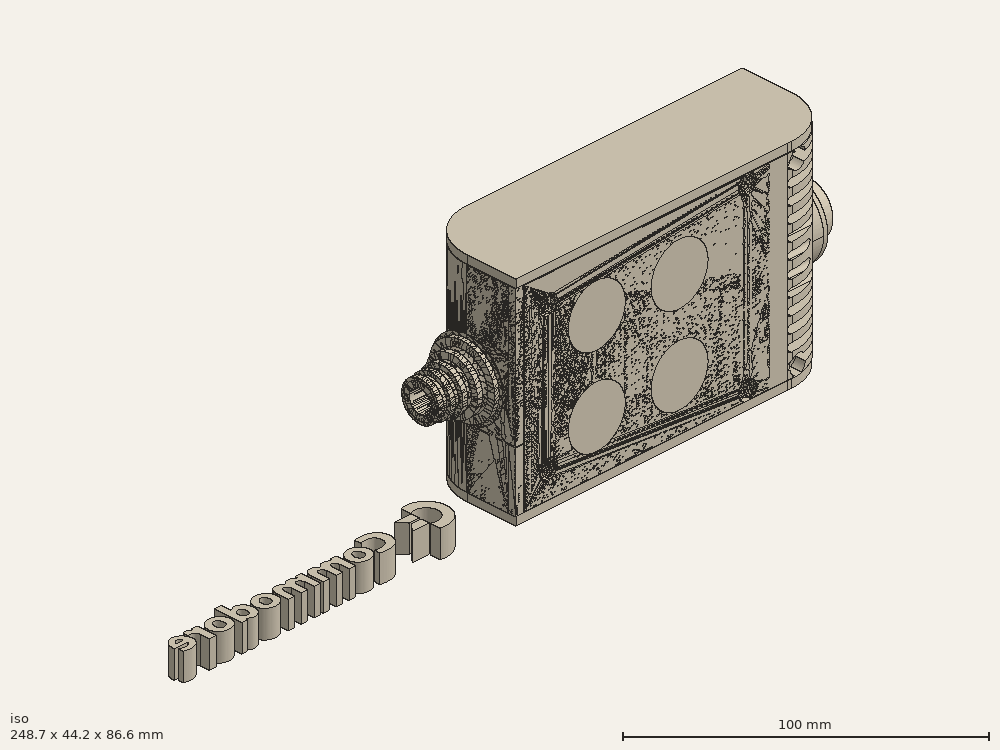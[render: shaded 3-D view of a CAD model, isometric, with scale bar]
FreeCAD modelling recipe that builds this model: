
FCSTD DOCUMENT  (FreeCAD 0.19R0.19.2)
Label: enclosure_206FCStd
License: All rights reserved
LicenseURL: http://en.wikipedia.org/wiki/All_rights_reserved
objects: Part::Revolution×152, Part::MultiFuse×146, Part::Feature×146, Sketcher::SketchObject×83, Part::Cut×70, Part::Cylinder×70, Part::Extrusion×68, Part::Fillet×58, Part::Box×36, App::MeasureDistance×4, Image::ImagePlane×1, PartDesign::Body×1, Part::FeaturePython×1, Part::Mirroring×1
note: 832 computed .brp shape members not serialized (recipe doc carries the construction recipe); baked Part::Feature solids carry a one-line shape summary decoded from their .brp

FEATURE [Sketcher::SketchObject] Sketch  label="topSketch"
  FullyConstrained = true
  sketch-geometry (20):
    g0: LineSegment StartX=5.21097e-06 StartY=3 StartZ=0 EndX=5.21097e-06 EndY=19 EndZ=0
    g1: ArcOfCircle CenterX=19 CenterY=19 CenterZ=0 NormalX=0 NormalY=0 NormalZ=1 AngleXU=0 Radius=19 StartAngle=1.5708 EndAngle=3.14159
    g2: ArcOfCircle CenterX=19 CenterY=19 CenterZ=0 NormalX=0 NormalY=0 NormalZ=1 AngleXU=0 Radius=16 StartAngle=1.5708 EndAngle=3.14159
    g3: LineSegment StartX=114 StartY=35 StartZ=0 EndX=19 EndY=35 EndZ=0
    g4: LineSegment StartX=5.21097e-06 StartY=3 StartZ=0 EndX=5.21097e-06 EndY=0 EndZ=0
    g5: LineSegment StartX=3 StartY=0 StartZ=0 EndX=5.21097e-06 EndY=0 EndZ=0
    g6: LineSegment StartX=3 StartY=19 StartZ=0 EndX=3 EndY=0 EndZ=0
    g7: LineSegment StartX=19 StartY=38 StartZ=0 EndX=124 EndY=38 EndZ=0
    g8: Circle CenterX=119 CenterY=35 CenterZ=0 NormalX=0 NormalY=0 NormalZ=1 AngleXU=0 Radius=1
    g9: Circle CenterX=121 CenterY=35 CenterZ=0 NormalX=0 NormalY=0 NormalZ=1 AngleXU=0 Radius=1
    g10: Circle CenterX=121 CenterY=33 CenterZ=0 NormalX=0 NormalY=0 NormalZ=1 AngleXU=0 Radius=1
    g11: BSplineCurve PolesCount=3 KnotsCount=2 Degree=2 IsPeriodic=0
    g12: GeomPoint X=119 Y=35 Z=0
    g13: GeomPoint X=121 Y=33 Z=0
    g14: LineSegment StartX=119 StartY=35 StartZ=0 EndX=114 EndY=35 EndZ=0
    g15: ArcOfCircle CenterX=105 CenterY=19 CenterZ=0 NormalX=0 NormalY=0 NormalZ=1 AngleXU=0 Radius=19 StartAngle=5.7297 EndAngle=6.28319
    g16: ArcOfCircle CenterX=105 CenterY=19 CenterZ=0 NormalX=0 NormalY=0 NormalZ=1 AngleXU=0 Radius=16 StartAngle=5.60905 EndAngle=6.28319
    g17: LineSegment StartX=121 StartY=33 StartZ=0 EndX=121 EndY=19 EndZ=0
    g18: LineSegment StartX=124 StartY=38 StartZ=0 EndX=124 EndY=19 EndZ=0
    g19: LineSegment StartX=117.5 StartY=9.01251 StartZ=0 EndX=121.163 EndY=9.0125 EndZ=0
  constraints (46):
    c: Vertical(g0)
    c: Block(g0)
    c: Coincident(g1,g0)
    c: Block(g1)
    c: Coincident(g2,g1)
    c: Block(g2)
    c: Coincident(g3,g2)
    c: Horizontal(g3)
    c: Tangent(g3,g2)
    c: Coincident(g4,g0)
    c: Distance(g4) = 3
    c: Vertical(g4)
    c: Coincident(g5,g4)
    c: Horizontal(g5)
    c: Coincident(g6,g2)
    c: Coincident(g6,g5)
    c: Vertical(g6)
    c: Horizontal(g7)
    c: Distance(g7) = 105
    c: Coincident(g7,g1)
    c: Block(g3)
    c: Weight(g8) = 1
    c: Equal(g8,g9)
    c: Equal(g8,g10)
    c: InternalAlignment(g8,g11)
    c: InternalAlignment(g9,g11)
    c: InternalAlignment(g10,g11)
    c: InternalAlignment(g12,g11)
    c: InternalAlignment(g13,g11)
    c: Block(g11)
    c: Coincident(g14,g11)
    c: Coincident(g14,g3)
    c: Horizontal(g14)
    c: Block(g15)
    c: Coincident(g16,g15)
    c: Block(g16)
    c: Coincident(g17,g11)
    c: Coincident(g17,g16)
    c: Vertical(g17)
    c: Distance(g17) = 14
    c: Coincident(g18,g7)
    c: Coincident(g18,g15)
    c: Vertical(g18)
    c: Distance(g18) = 19
    c: Coincident(g19,g16)
    c: Coincident(g19,g15)
FEATURE [Sketcher::SketchObject] Sketch001  label="bottomSketch"
  FullyConstrained = true
  sketch-geometry (32):
    g0: LineSegment StartX=3.3 StartY=-6.03275e-07 StartZ=0 EndX=98 EndY=-6.03275e-07 EndZ=0
    g1: ArcOfCircle CenterX=98 CenterY=19 CenterZ=0 NormalX=0 NormalY=0 NormalZ=1 AngleXU=0 Radius=19 StartAngle=4.71239 EndAngle=5.71103
    g2: LineSegment StartX=6.3 StartY=8 StartZ=0 EndX=3.3 EndY=8 EndZ=0
    g3: LineSegment StartX=3.3 StartY=8 StartZ=0 EndX=3.3 EndY=-6.03275e-07 EndZ=0
    g4: ArcOfCircle CenterX=8.3 CenterY=5 CenterZ=0 NormalX=0 NormalY=0 NormalZ=1 AngleXU=0 Radius=2 StartAngle=3.14159 EndAngle=4.71239
    g5: LineSegment StartX=6.3 StartY=8 StartZ=0 EndX=6.3 EndY=5 EndZ=0
    g6: ArcOfCircle CenterX=98 CenterY=19 CenterZ=0 NormalX=0 NormalY=0 NormalZ=1 AngleXU=0 Radius=12.7 StartAngle=4.71239 EndAngle=6.28319
    g7: LineSegment StartX=94.7 StartY=3 StartZ=0 EndX=8.3 EndY=3 EndZ=0
    g8-g12: Circle x5 (B-spline internal-alignment scaffolding for g13; pole/knot coordinates omitted)
    g13: BSplineCurve PolesCount=5 KnotsCount=3 Degree=3 IsPeriodic=0
    g14: GeomPoint X=98 Y=6.3 Z=0
    g15: GeomPoint X=96.3938 Y=4.71946 Z=0
    g16: GeomPoint X=94.7 Y=3 Z=0
    g17-g23: Circle x7 (B-spline internal-alignment scaffolding for g24; pole/knot coordinates omitted)
    g24: BSplineCurve PolesCount=7 KnotsCount=5 Degree=3 IsPeriodic=0
    g25-g29: GeomPoint x5 (B-spline internal-alignment scaffolding for g24; pole/knot coordinates omitted)
    g30: ArcOfCircle CenterX=98 CenterY=19 CenterZ=0 NormalX=0 NormalY=0 NormalZ=1 AngleXU=0 Radius=15.7 StartAngle=5.81226 EndAngle=6.28319
    g31: LineSegment StartX=110.7 StartY=19 StartZ=0 EndX=113.7 EndY=19 EndZ=0
  constraints (41):
    c: Horizontal(g0)
    c: Coincident(g1,g0)
    c: Block(g1)
    c: Horizontal(g2)
    c: Distance(g2) = 3
    c: Coincident(g3,g2)
    c: Vertical(g3)
    c: Coincident(g3,g0)
    c: Block(g4)
    c: Block(g2)
    c: Coincident(g5,g2)
    c: Coincident(g5,g4)
    c: Vertical(g5)
    c: Coincident(g6,g1)
    c: Block(g6)
    c: Coincident(g7,g4)
    c: Horizontal(g7)
    c: Block(g0)
    c: Block(g7)
    c: Block(g3)
    c: Coincident(g13,g6)
    c: Weight(g8) = 1
    c: Equal(g8, g9-g12) x4
    c: Coincident(g13,g7)
    c: InternalAlignment(g8-g12 -> g13) x5
    c: InternalAlignment(g14,g13)
    c: InternalAlignment(g15,g13)
    c: InternalAlignment(g16,g13)
    c: Block(g13)
    c: Weight(g17) = 1
    c: Equal(g17, g18-g23) x6
    c: Coincident(g24,g1)
    c: InternalAlignment(g17-g23 -> g24) x7
    c: InternalAlignment(g25-g29 -> g24) x5
    c: Block(g24)
    c: Coincident(g30,g24)
    c: Coincident(g31,g6)
    c: Coincident(g31,g30)
    c: Horizontal(g31)
    c: Block(g31)
    c: Block(g30)
FEATURE [Part::Extrusion] Extrude  label="top"
  Base = -> Sketch
  Dir = (0,0,1)
  DirMode = 2
  FaceMakerClass = Part::FaceMakerBullseye
  LengthFwd = 72
  LengthRev = 0
  Solid = true
  Symmetric = false
FEATURE [Part::Extrusion] Extrude001  label="bottom"
  Base = -> Sketch001
  Dir = (0,0,1)
  DirMode = 2
  FaceMakerClass = Part::FaceMakerBullseye
  LengthFwd = 71.4
  LengthRev = 0
  Placement = pos=(0,0,0.3) rot=(0,0,1;0rad)
  Solid = true
  Symmetric = false
FEATURE [Sketcher::SketchObject] Sketch002  label="topSketch001"
  FullyConstrained = true
  sketch-geometry (8):
    g0: ArcOfCircle CenterX=19 CenterY=19.0975 CenterZ=0 NormalX=0 NormalY=0 NormalZ=1 AngleXU=0 Radius=18.9025 StartAngle=1.5708 EndAngle=3.14674
    g1: LineSegment StartX=0.0977805 StartY=19.0003 StartZ=0 EndX=0.0977805 EndY=0.000251602 EndZ=0
    g2: LineSegment StartX=19 StartY=38 StartZ=0 EndX=124 EndY=38 EndZ=0
    g3: LineSegment StartX=0.0977805 StartY=0.000251602 StartZ=0 EndX=105.098 EndY=0.000251602 EndZ=0
    g4: LineSegment StartX=124 StartY=38 StartZ=0 EndX=125.616 EndY=38 EndZ=0
    g5: LineSegment StartX=105.098 StartY=0.000251602 StartZ=0 EndX=106.713 EndY=0.000251602 EndZ=0
    g6: ArcOfCircle CenterX=106.616 CenterY=19 CenterZ=0 NormalX=0 NormalY=0 NormalZ=1 AngleXU=0 Radius=19 StartAngle=4.71754 EndAngle=6.28319
    g7: LineSegment StartX=125.616 StartY=38 StartZ=0 EndX=125.616 EndY=19 EndZ=0
  constraints (21):
    c: Block(g0)
    c: Coincident(g1,g0)
    c: Vertical(g1)
    c: Horizontal(g2)
    c: Distance(g2) = 105
    c: Coincident(g2,g0)
    c: Distance(g1) = 19
    c: Coincident(g3,g1)
    c: Horizontal(g3)
    c: Distance(g3) = 105
    c: Coincident(g4,g2)
    c: Horizontal(g4)
    c: Distance(g4) = 1.61553
    c: Horizontal(g5)
    c: Equal(g4,g5) = 1.61553
    c: Coincident(g5,g3)
    c: Block(g6)
    c: Coincident(g6,g5)
    c: Coincident(g7,g4)
    c: Coincident(g7,g6)
    c: Vertical(g7)
FEATURE [Part::Extrusion] Extrude002  label="sideA"
  Base = -> Sketch002
  Dir = (0,0,1)
  DirMode = 2
  FaceMakerClass = Part::FaceMakerBullseye
  LengthFwd = 3
  LengthRev = 0
  Placement = pos=(0,0,-3) rot=(0,0,1;0rad)
  Solid = true
  Symmetric = false
FEATURE [Sketcher::SketchObject] Sketch003  label="topSketch002"
  FullyConstrained = true
  sketch-geometry (6):
    g0: LineSegment StartX=19 StartY=38 StartZ=0 EndX=117 EndY=38 EndZ=0
    g1: ArcOfCircle CenterX=19 CenterY=19 CenterZ=0 NormalX=0 NormalY=0 NormalZ=1 AngleXU=0 Radius=19 StartAngle=1.5708 EndAngle=3.14159
    g2: LineSegment StartX=117 StartY=38 StartZ=0 EndX=117 EndY=19 EndZ=0
    g3: LineSegment StartX=98 StartY=1.0161e-12 StartZ=0 EndX=5.22862e-06 EndY=1.0161e-12 EndZ=0
    g4: LineSegment StartX=5.22862e-06 StartY=19 StartZ=0 EndX=5.22862e-06 EndY=1.0161e-12 EndZ=0
    g5: ArcOfCircle CenterX=98 CenterY=19 CenterZ=0 NormalX=0 NormalY=0 NormalZ=1 AngleXU=0 Radius=19 StartAngle=4.71239 EndAngle=6.28319
  constraints (16):
    c: Horizontal(g0)
    c: Distance(g0) = 98
    c: Coincident(g1,g0)
    c: Block(g1)
    c: Coincident(g2,g0)
    c: Vertical(g2)
    c: Distance(g2) = 19
    c: Horizontal(g3)
    c: Coincident(g4,g1)
    c: Vertical(g4)
    c: Coincident(g3,g4)
    c: Block(g3)
    c: Coincident(g5,g2)
    c: Coincident(g5,g3)
    c: Block(g0)
    c: Block(g5)
FEATURE [Sketcher::SketchObject] Sketch004
  FullyConstrained = true
  MapMode = 3
  Placement = pos=(0,0,0) rot=(1,0,0;1.5708rad)
  Support = -> [Extrude]
  sketch-geometry (8):
    g0: Circle CenterX=80.351 CenterY=-67.6202 CenterZ=0 NormalX=0 NormalY=0 NormalZ=1 AngleXU=0 Radius=2
    g1: Circle CenterX=80.351 CenterY=-67.6202 CenterZ=0 NormalX=0 NormalY=0 NormalZ=1 AngleXU=0 Radius=3
    g2: Circle CenterX=80.351 CenterY=-4.92017 CenterZ=0 NormalX=0 NormalY=0 NormalZ=1 AngleXU=0 Radius=2
    g3: Circle CenterX=80.351 CenterY=-4.92017 CenterZ=0 NormalX=0 NormalY=0 NormalZ=1 AngleXU=0 Radius=3
    g4: Circle CenterX=23.851 CenterY=-4.92017 CenterZ=0 NormalX=0 NormalY=0 NormalZ=1 AngleXU=0 Radius=2
    g5: Circle CenterX=23.851 CenterY=-4.92017 CenterZ=0 NormalX=0 NormalY=0 NormalZ=1 AngleXU=0 Radius=3
    g6: Circle CenterX=23.851 CenterY=-67.6202 CenterZ=0 NormalX=0 NormalY=0 NormalZ=1 AngleXU=0 Radius=2
    g7: Circle CenterX=23.851 CenterY=-67.6202 CenterZ=0 NormalX=0 NormalY=0 NormalZ=1 AngleXU=0 Radius=3
  constraints (8):
    c: Block(g3)
    c: Block(g2)
    c: Block(g1)
    c: Block(g0)
    c: Block(g6)
    c: Block(g7)
    c: Block(g4)
    c: Block(g5)
FEATURE [Part::Extrusion] Extrude004
  Base = -> Sketch004
  Dir = (0,-1,2e-16)
  DirMode = 2
  FaceMakerClass = Part::FaceMakerBullseye
  LengthFwd = 6
  LengthRev = 0
  Placement = pos=(0,9,0) rot=(0,0,1;0rad)
  Solid = true
  Symmetric = false
FEATURE [Sketcher::SketchObject] Sketch005
  FullyConstrained = true
  MapMode = 3
  Placement = pos=(0,0,0) rot=(1,0,0;1.5708rad)
  Support = -> [Extrude]
  sketch-geometry (8):
    g0: Circle CenterX=80.351 CenterY=-67.6202 CenterZ=0 NormalX=0 NormalY=0 NormalZ=1 AngleXU=0 Radius=3
    g1: Circle CenterX=80.351 CenterY=-4.92017 CenterZ=0 NormalX=0 NormalY=0 NormalZ=1 AngleXU=0 Radius=3
    g2: Circle CenterX=23.851 CenterY=-4.92017 CenterZ=0 NormalX=0 NormalY=0 NormalZ=1 AngleXU=0 Radius=3
    g3: Circle CenterX=23.851 CenterY=-67.6202 CenterZ=0 NormalX=0 NormalY=0 NormalZ=1 AngleXU=0 Radius=3
    g4: Circle CenterX=23.851 CenterY=-67.6202 CenterZ=0 NormalX=0 NormalY=0 NormalZ=1 AngleXU=0 Radius=5
    g5: Circle CenterX=80.351 CenterY=-67.6202 CenterZ=0 NormalX=0 NormalY=0 NormalZ=1 AngleXU=0 Radius=5
    g6: Circle CenterX=23.851 CenterY=-4.92017 CenterZ=0 NormalX=0 NormalY=0 NormalZ=1 AngleXU=0 Radius=5
    g7: Circle CenterX=80.351 CenterY=-4.92017 CenterZ=0 NormalX=0 NormalY=0 NormalZ=1 AngleXU=0 Radius=5
  constraints (8):
    c: Block(g1)
    c: Block(g0)
    c: Block(g3)
    c: Block(g2)
    c: Block(g5)
    c: Block(g4)
    c: Block(g6)
    c: Block(g7)
FEATURE [Part::Extrusion] Extrude005
  Base = -> Sketch005
  Dir = (0,-1,2e-16)
  DirMode = 2
  FaceMakerClass = Part::FaceMakerBullseye
  LengthFwd = 2
  LengthRev = 0
  Solid = true
  Symmetric = false
FEATURE [Sketcher::SketchObject] Sketch006
  FullyConstrained = true
  MapMode = 3
  Placement = pos=(0,0,0) rot=(1,0,0;1.5708rad)
  sketch-geometry (8):
    g0: Circle CenterX=80.351 CenterY=-67.6202 CenterZ=0 NormalX=0 NormalY=0 NormalZ=1 AngleXU=0 Radius=3
    g1: Circle CenterX=80.351 CenterY=-4.92017 CenterZ=0 NormalX=0 NormalY=0 NormalZ=1 AngleXU=0 Radius=3
    g2: Circle CenterX=23.851 CenterY=-4.92017 CenterZ=0 NormalX=0 NormalY=0 NormalZ=1 AngleXU=0 Radius=3
    g3: Circle CenterX=23.851 CenterY=-67.6202 CenterZ=0 NormalX=0 NormalY=0 NormalZ=1 AngleXU=0 Radius=3
    g4: Circle CenterX=23.851 CenterY=-67.6202 CenterZ=0 NormalX=0 NormalY=0 NormalZ=1 AngleXU=0 Radius=5
    g5: Circle CenterX=80.351 CenterY=-67.6202 CenterZ=0 NormalX=0 NormalY=0 NormalZ=1 AngleXU=0 Radius=5
    g6: Circle CenterX=23.851 CenterY=-4.92017 CenterZ=0 NormalX=0 NormalY=0 NormalZ=1 AngleXU=0 Radius=5
    g7: Circle CenterX=80.351 CenterY=-4.92017 CenterZ=0 NormalX=0 NormalY=0 NormalZ=1 AngleXU=0 Radius=5
  constraints (8):
    c: Block(g1)
    c: Block(g0)
    c: Block(g3)
    c: Block(g2)
    c: Block(g5)
    c: Block(g4)
    c: Block(g6)
    c: Block(g7)
FEATURE [Part::Extrusion] Extrude007
  Base = -> Sketch006
  Dir = (0,-1,2e-16)
  DirMode = 2
  FaceMakerClass = Part::FaceMakerBullseye
  LengthFwd = 2
  LengthRev = 0
  Solid = true
  Symmetric = false
FEATURE [Part::Fillet] Fillet
  Base = -> Extrude007
  Edges = 4 edges r=1.99: [Edge6,Edge12,Edge18,Edge24]
FEATURE [Part::Cut] Cut
  Base = -> Extrude005
  Placement = pos=(0,5,0) rot=(0,0,1;0rad)
  Tool = -> Fillet
FEATURE [Part::MultiFuse] Fusion  label="pCBScrews"
  Placement = pos=(-2.5,0,72.3) rot=(0,0,1;0rad)
  Shapes = -> [Extrude004,Cut]
FEATURE [App::MeasureDistance] Distance  label="Distance: 0.69 mm"
  Distance = 0.685967
  P1 = (24.0138,2.9647,0.3)
  P2 = (23.8901,3,-0.373787)
FEATURE [App::MeasureDistance] Distance001  label="Distance: 0.53 mm"
  Distance = 0.533607
  P1 = (80.2939,3,72.2334)
  P2 = (80.281,2.99661,71.7)
FEATURE [Part::Fillet] Fillet001
  Base = -> Extrude001
  Edges = 1 edges r=2.4: [Edge17]
FEATURE [Part::Fillet] Fillet002  label="bottom001"
  Base = -> Fillet001
  Edges = 1 edges r=2.4: [Edge36]
FEATURE [Part::Fillet] Fillet003  label="top001"
  Base = -> Extrude
  Edges = 1 edges r=2: [Edge1]
FEATURE [Sketcher::SketchObject] Sketch007
  FullyConstrained = true
  sketch-geometry (16):
    g0: LineSegment StartX=4 StartY=0 StartZ=0 EndX=4 EndY=2.4 EndZ=0
    g1: LineSegment StartX=4 StartY=2.4 StartZ=0 EndX=7 EndY=2.4 EndZ=0
    g2: LineSegment StartX=4 StartY=0 StartZ=0 EndX=5.7 EndY=0 EndZ=0
    g3: LineSegment StartX=5.7 StartY=0 StartZ=0 EndX=5.7 EndY=-5.6 EndZ=0
    g4-g8: Circle x5 (B-spline internal-alignment scaffolding for g9; pole/knot coordinates omitted)
    g9: BSplineCurve PolesCount=5 KnotsCount=3 Degree=3 IsPeriodic=0
    g10: GeomPoint X=7 Y=2.4 Z=0
    g11: GeomPoint X=10.4582 Y=-1.55472 Z=0
    g12: GeomPoint X=14 Y=-5.6 Z=0
    g13: LineSegment StartX=14 StartY=-5.6 StartZ=0 EndX=14 EndY=-14.1 EndZ=0
    g14: LineSegment StartX=14 StartY=-14.1 StartZ=0 EndX=6.5 EndY=-14.1 EndZ=0
    g15: LineSegment StartX=5.7 StartY=-5.6 StartZ=0 EndX=6.5 EndY=-14.1 EndZ=0
  constraints (28):
    c: Distance(g0) = 2.4
    c: Vertical(g0)
    c: Block(g0)
    c: Coincident(g1,g0)
    c: Horizontal(g1)
    c: Distance(g1) = 3
    c: Coincident(g2,g0)
    c: Horizontal(g2)
    c: Distance(g2) = 1.7
    c: Coincident(g3,g2)
    c: Vertical(g3)
    c: Distance(g3) = 5.6
    c: Coincident(g9,g1)
    c: Weight(g4) = 1
    c: Equal(g4, g5-g8) x4
    c: InternalAlignment(g4-g8 -> g9) x5
    c: InternalAlignment(g10,g9)
    c: InternalAlignment(g11,g9)
    c: InternalAlignment(g12,g9)
    c: Block(g9)
    c: Coincident(g13,g9)
    c: Vertical(g13)
    c: Distance(g13) = 8.5
    c: Coincident(g14,g13)
    c: Horizontal(g14)
    c: Distance(g14) = 7.5
    c: Coincident(g15,g3)
    c: Coincident(g15,g14)
FEATURE [Part::Feature] Face
  shape: bbox 10 x 16.5 x 2e-07 mm, 1 faces, 0 solids (baked)
FEATURE [Part::Revolution] Revolve  label="plugHousing"
  Angle = 360
  Axis = (0,1,0)
  Base = (0,0,0)
  FaceMakerClass = Part::FaceMakerBullseye
  Placement = pos=(0,0,36.15) rot=(0,0,1;0rad)
  Solid = false
  Source = -> Face
  Symmetric = false
FEATURE [Part::Feature] Face001
  shape: bbox 10 x 16.5 x 2e-07 mm, 1 faces, 0 solids (baked)
FEATURE [Part::Revolution] Revolve001  label="plugHousing001"
  Angle = 360
  Axis = (0,1,0)
  Base = (0,0,0)
  FaceMakerClass = Part::FaceMakerBullseye
  Placement = pos=(0,0,36.15) rot=(0,0,1;0rad)
  Solid = false
  Source = -> Face001
  Symmetric = false
FEATURE [Part::MultiFuse] Fusion001  label="plugHousing002"
  Placement = pos=(0,0,0) rot=(0,0,1;1.5708rad)
  Shapes = -> [Revolve001,Revolve]
FEATURE [Part::Feature] Face002
  shape: bbox 10 x 16.5 x 2e-07 mm, 1 faces, 0 solids (baked)
FEATURE [Part::Revolution] Revolve003  label="plugHousing005"
  Angle = 360
  Axis = (0,1,0)
  Base = (0,0,0)
  FaceMakerClass = Part::FaceMakerBullseye
  Placement = pos=(0,0,36.15) rot=(0,0,1;0rad)
  Solid = false
  Source = -> Face002
  Symmetric = false
FEATURE [Part::Feature] Face003
  shape: bbox 10 x 16.5 x 2e-07 mm, 1 faces, 0 solids (baked)
FEATURE [Part::Revolution] Revolve002  label="plugHousing003"
  Angle = 360
  Axis = (0,1,0)
  Base = (0,0,0)
  FaceMakerClass = Part::FaceMakerBullseye
  Placement = pos=(0,0,36.15) rot=(0,0,1;0rad)
  Solid = false
  Source = -> Face003
  Symmetric = false
FEATURE [Part::MultiFuse] Fusion002  label="plugHousing004"
  Placement = pos=(0,0,0) rot=(0,0,1;1.5708rad)
  Shapes = -> [Revolve002,Revolve003]
FEATURE [Part::MultiFuse] Fusion003  label="plugHousing006"
  Placement = pos=(0,19,0) rot=(0,0,1;3.14159rad)
  Shapes = -> [Fusion002,Fusion001]
FEATURE [Part::Feature] Face004
  shape: bbox 10 x 16.5 x 2e-07 mm, 1 faces, 0 solids (baked)
FEATURE [Part::Revolution] Revolve006  label="plugHousing010"
  Angle = 360
  Axis = (0,1,0)
  Base = (0,0,0)
  FaceMakerClass = Part::FaceMakerBullseye
  Placement = pos=(0,0,36.15) rot=(0,0,1;0rad)
  Solid = false
  Source = -> Face004
  Symmetric = false
FEATURE [Part::Feature] Face005
  shape: bbox 10 x 16.5 x 2e-07 mm, 1 faces, 0 solids (baked)
FEATURE [Part::Revolution] Revolve007  label="plugHousing011"
  Angle = 360
  Axis = (0,1,0)
  Base = (0,0,0)
  FaceMakerClass = Part::FaceMakerBullseye
  Placement = pos=(0,0,36.15) rot=(0,0,1;0rad)
  Solid = false
  Source = -> Face005
  Symmetric = false
FEATURE [Part::Feature] Face006
  shape: bbox 10 x 16.5 x 2e-07 mm, 1 faces, 0 solids (baked)
FEATURE [Part::Revolution] Revolve004  label="plugHousing007"
  Angle = 360
  Axis = (0,1,0)
  Base = (0,0,0)
  FaceMakerClass = Part::FaceMakerBullseye
  Placement = pos=(0,0,36.15) rot=(0,0,1;0rad)
  Solid = false
  Source = -> Face006
  Symmetric = false
FEATURE [Part::MultiFuse] Fusion004  label="plugHousing009"
  Placement = pos=(0,0,0) rot=(0,0,1;1.5708rad)
  Shapes = -> [Revolve004,Revolve007]
FEATURE [Part::Feature] Face007
  shape: bbox 10 x 16.5 x 2e-07 mm, 1 faces, 0 solids (baked)
FEATURE [Part::Revolution] Revolve005  label="plugHousing008"
  Angle = 360
  Axis = (0,1,0)
  Base = (0,0,0)
  FaceMakerClass = Part::FaceMakerBullseye
  Placement = pos=(0,0,36.15) rot=(0,0,1;0rad)
  Solid = false
  Source = -> Face007
  Symmetric = false
FEATURE [Part::MultiFuse] Fusion005  label="plugHousing012"
  Placement = pos=(0,0,0) rot=(0,0,1;1.5708rad)
  Shapes = -> [Revolve006,Revolve005]
FEATURE [Part::MultiFuse] Fusion006  label="plugHousing013"
  Placement = pos=(0,19,0) rot=(0,0,1;3.14159rad)
  Shapes = -> [Fusion005,Fusion004]
FEATURE [Part::MultiFuse] Fusion007  label="plugHousing014"
  Placement = pos=(122.621,0,-0.15) rot=(0,0,1;0rad)
  Shapes = -> [Fusion003,Fusion006]
FEATURE [Part::Cylinder] Cylinder002
  Angle = 360
  AttacherType = Attacher::AttachEngine3D
  Height = 20
  Placement = pos=(0,0,36.15) rot=(0,0,1;0rad)
  Radius = 4
FEATURE [Part::Cylinder] Cylinder003
  Angle = 360
  AttacherType = Attacher::AttachEngine3D
  Height = 10
  Placement = pos=(0,0,36.15) rot=(0,0,1;0rad)
  Radius = 4
FEATURE [Part::MultiFuse] Fusion009  label="removeToCreateHoleForPlugHousing"
  Placement = pos=(70,19,36.15) rot=(0,1,0;1.5708rad)
  Shapes = -> [Cylinder002,Cylinder003]
FEATURE [Part::Cylinder] Cylinder004
  Angle = 360
  AttacherType = Attacher::AttachEngine3D
  Height = 20
  Placement = pos=(0,0,36.15) rot=(0,0,1;0rad)
  Radius = 4
FEATURE [Part::Cylinder] Cylinder005
  Angle = 360
  AttacherType = Attacher::AttachEngine3D
  Height = 10
  Placement = pos=(0,0,36.15) rot=(0,0,1;0rad)
  Radius = 4
FEATURE [Part::MultiFuse] Fusion010  label="removeToCreateHoleForPlugHousing001"
  Placement = pos=(70,19,36.15) rot=(0,1,0;1.5708rad)
  Shapes = -> [Cylinder004,Cylinder005]
FEATURE [Part::Cut] Cut001
  Base = -> Fillet003
  Tool = -> Fusion010
FEATURE [Part::Cut] Cut002  label="Bottom"
  Base = -> Fillet002
  Tool = -> Fusion009
FEATURE [Part::Feature] Face008
  shape: bbox 10 x 16.5 x 2e-07 mm, 1 faces, 0 solids (baked)
FEATURE [Part::Revolution] Revolve011  label="plugHousing021"
  Angle = 360
  Axis = (0,1,0)
  Base = (0,0,0)
  FaceMakerClass = Part::FaceMakerBullseye
  Placement = pos=(0,0,36.15) rot=(0,0,1;0rad)
  Solid = false
  Source = -> Face008
  Symmetric = false
FEATURE [Part::Feature] Face009
  shape: bbox 10 x 16.5 x 2e-07 mm, 1 faces, 0 solids (baked)
FEATURE [Part::Revolution] Revolve012  label="plugHousing022"
  Angle = 360
  Axis = (0,1,0)
  Base = (0,0,0)
  FaceMakerClass = Part::FaceMakerBullseye
  Placement = pos=(0,0,36.15) rot=(0,0,1;0rad)
  Solid = false
  Source = -> Face009
  Symmetric = false
FEATURE [Part::Feature] Face010 .. Face013  x4 (patterned run collapsed; names and placements below)
  shape: bbox 10 x 16.5 x 2e-07 mm, 1 faces, 0 solids (baked)
FEATURE [Part::Revolution] Revolve015  label="plugHousing027"
  Angle = 360
  Axis = (0,1,0)
  Base = (0,0,0)
  FaceMakerClass = Part::FaceMakerBullseye
  Placement = pos=(0,0,36.15) rot=(0,0,1;0rad)
  Solid = false
  Source = -> Face013
  Symmetric = false
FEATURE [Part::Feature] Face014
  shape: bbox 10 x 16.5 x 2e-07 mm, 1 faces, 0 solids (baked)
FEATURE [Part::Feature] Face015
  shape: bbox 10 x 16.5 x 2e-07 mm, 1 faces, 0 solids (baked)
FEATURE [Part::Feature] Face016
  shape: bbox 10 x 16.5 x 2e-07 mm, 1 faces, 0 solids (baked)
FEATURE [Part::Revolution] Revolve019  label="plugHousing033"
  Angle = 360
  Axis = (0,1,0)
  Base = (0,0,0)
  FaceMakerClass = Part::FaceMakerBullseye
  Placement = pos=(0,0,36.15) rot=(0,0,1;0rad)
  Solid = false
  Source = -> Face016
  Symmetric = false
FEATURE [Part::Feature] Face017
  shape: bbox 10 x 16.5 x 2e-07 mm, 1 faces, 0 solids (baked)
FEATURE [Part::Revolution] Revolve020  label="plugHousing034"
  Angle = 360
  Axis = (0,1,0)
  Base = (0,0,0)
  FaceMakerClass = Part::FaceMakerBullseye
  Placement = pos=(0,0,36.15) rot=(0,0,1;0rad)
  Solid = false
  Source = -> Face017
  Symmetric = false
FEATURE [Part::Feature] Face018
  shape: bbox 10 x 16.5 x 2e-07 mm, 1 faces, 0 solids (baked)
FEATURE [Part::Revolution] Revolve016  label="plugHousing030"
  Angle = 360
  Axis = (0,1,0)
  Base = (0,0,0)
  FaceMakerClass = Part::FaceMakerBullseye
  Placement = pos=(0,0,36.15) rot=(0,0,1;0rad)
  Solid = false
  Source = -> Face018
  Symmetric = false
FEATURE [Part::MultiFuse] Fusion020  label="plugHousing038"
  Placement = pos=(0,0,0) rot=(0,0,1;1.5708rad)
  Shapes = -> [Revolve016,Revolve020]
FEATURE [Part::Feature] Face019
  shape: bbox 10 x 16.5 x 2e-07 mm, 1 faces, 0 solids (baked)
FEATURE [Part::Feature] Face020
  shape: bbox 10 x 16.5 x 2e-07 mm, 1 faces, 0 solids (baked)
FEATURE [Part::Revolution] Revolve017  label="plugHousing031"
  Angle = 360
  Axis = (0,1,0)
  Base = (0,0,0)
  FaceMakerClass = Part::FaceMakerBullseye
  Placement = pos=(0,0,36.15) rot=(0,0,1;0rad)
  Solid = false
  Source = -> Face020
  Symmetric = false
FEATURE [Part::MultiFuse] Fusion021  label="plugHousing039"
  Placement = pos=(0,0,0) rot=(0,0,1;1.5708rad)
  Shapes = -> [Revolve019,Revolve017]
FEATURE [Part::MultiFuse] Fusion023  label="plugHousing041"
  Placement = pos=(0,19,0) rot=(0,0,1;3.14159rad)
  Shapes = -> [Fusion021,Fusion020]
FEATURE [Part::Revolution] Revolve022  label="plugHousing043"
  Angle = 360
  Axis = (0,1,0)
  Base = (0,0,0)
  FaceMakerClass = Part::FaceMakerBullseye
  Placement = pos=(0,0,36.15) rot=(0,0,1;0rad)
  Solid = false
  Source = -> Face019
  Symmetric = false
FEATURE [Part::Feature] Face021
  shape: bbox 10 x 16.5 x 2e-07 mm, 1 faces, 0 solids (baked)
FEATURE [Part::Revolution] Revolve023  label="plugHousing044"
  Angle = 360
  Axis = (0,1,0)
  Base = (0,0,0)
  FaceMakerClass = Part::FaceMakerBullseye
  Placement = pos=(0,0,36.15) rot=(0,0,1;0rad)
  Solid = false
  Source = -> Face021
  Symmetric = false
FEATURE [Part::Feature] Face022
  shape: bbox 10 x 16.5 x 2e-07 mm, 1 faces, 0 solids (baked)
FEATURE [Part::Revolution] Revolve018  label="plugHousing032"
  Angle = 360
  Axis = (0,1,0)
  Base = (0,0,0)
  FaceMakerClass = Part::FaceMakerBullseye
  Placement = pos=(0,0,36.15) rot=(0,0,1;0rad)
  Solid = false
  Source = -> Face022
  Symmetric = false
FEATURE [Part::MultiFuse] Fusion022  label="plugHousing040"
  Placement = pos=(0,0,0) rot=(0,0,1;1.5708rad)
  Shapes = -> [Revolve018,Revolve023]
FEATURE [Part::Feature] Face023
  shape: bbox 10 x 16.5 x 2e-07 mm, 1 faces, 0 solids (baked)
FEATURE [Part::Revolution] Revolve021  label="plugHousing035"
  Angle = 360
  Axis = (0,1,0)
  Base = (0,0,0)
  FaceMakerClass = Part::FaceMakerBullseye
  Placement = pos=(0,0,36.15) rot=(0,0,1;0rad)
  Solid = false
  Source = -> Face023
  Symmetric = false
FEATURE [Part::MultiFuse] Fusion018  label="plugHousing036"
  Placement = pos=(0,0,0) rot=(0,0,1;1.5708rad)
  Shapes = -> [Revolve022,Revolve021]
FEATURE [Part::MultiFuse] Fusion019  label="plugHousing037"
  Placement = pos=(0,19,0) rot=(0,0,1;3.14159rad)
  Shapes = -> [Fusion018,Fusion022]
FEATURE [Part::MultiFuse] Fusion024  label="plugHousing042"
  Placement = pos=(122.621,0,-0.15) rot=(0,0,1;0rad)
  Shapes = -> [Fusion023,Fusion019]
FEATURE [Part::Cylinder] Cylinder006
  Angle = 360
  AttacherType = Attacher::AttachEngine3D
  Height = 20
  Placement = pos=(0,0,36.15) rot=(0,0,1;0rad)
  Radius = 14.3
FEATURE [Part::Cylinder] Cylinder007
  Angle = 360
  AttacherType = Attacher::AttachEngine3D
  Height = 10
  Placement = pos=(0,0,36.15) rot=(0,0,1;0rad)
  Radius = 4
FEATURE [Part::MultiFuse] Fusion026  label="removeToCreteHoleForPlugHousing"
  Placement = pos=(70,19,36) rot=(0,1,0;1.5708rad)
  Shapes = -> [Cylinder006,Cylinder007]
FEATURE [Part::Box] Box001  label="Cube001"
  AttacherType = Attacher::AttachEngine3D
  Height = 28
  Length = 3
  Placement = pos=(110.7,19,22) rot=(0,0,1;0rad)
  Width = 15.7
FEATURE [Part::Cut] Cut003  label="top002"
  Base = -> Cut001
  Tool = -> Fusion007
FEATURE [Part::Revolution] Revolve008  label="plugHousing015"
  Angle = 360
  Axis = (0,1,0)
  Base = (0,0,0)
  FaceMakerClass = Part::FaceMakerBullseye
  Placement = pos=(0,0,36.15) rot=(0,0,1;0rad)
  Solid = false
  Source = -> Face010
  Symmetric = false
FEATURE [Part::MultiFuse] Fusion013  label="plugHousing020"
  Placement = pos=(0,0,0) rot=(0,0,1;1.5708rad)
  Shapes = -> [Revolve008,Revolve012]
FEATURE [Part::Cut] Cut004  label="top003"
  Base = -> Cut003
  Placement = pos=(1,0,0) rot=(0,0,1;0rad)
  Tool = -> Fusion026
FEATURE [Part::Cylinder] Cylinder008
  Angle = 360
  AttacherType = Attacher::AttachEngine3D
  Height = 20
  Placement = pos=(0,0,36.15) rot=(0,0,1;0rad)
  Radius = 10.3
FEATURE [Part::Cylinder] Cylinder009
  Angle = 360
  AttacherType = Attacher::AttachEngine3D
  Height = 10
  Placement = pos=(0,0,36.15) rot=(0,0,1;0rad)
  Radius = 4
FEATURE [Part::MultiFuse] Fusion027  label="removeToCreteHoleForPlugHousing001"
  Placement = pos=(70,19,36) rot=(0,1,0;1.5708rad)
  Shapes = -> [Cylinder008,Cylinder009]
FEATURE [Part::Cut] Cut005  label="plugHousingTab"
  Base = -> Box001
  Tool = -> Fusion027
FEATURE [Part::MultiFuse] Fusion028  label="plugHousing045"
  Shapes = -> [Fusion024,Cut005]
FEATURE [Part::Box] Box002  label="Cube002"
  AttacherType = Attacher::AttachEngine3D
  Height = 28.8
  Length = 3
  Placement = pos=(107.3,28,21.6) rot=(0,0,1;0rad)
  Width = 7
FEATURE [Part::Box] Box003  label="Cube003"
  AttacherType = Attacher::AttachEngine3D
  Height = 3
  Length = 6.4
  Placement = pos=(107.3,28,18.6) rot=(0,0,1;0rad)
  Width = 7
FEATURE [Part::Box] Box004  label="Cube004"
  AttacherType = Attacher::AttachEngine3D
  Height = 3
  Length = 6.4
  Placement = pos=(107.3,28,50.4) rot=(0,0,1;0rad)
  Width = 7
FEATURE [Part::MultiFuse] Fusion029  label="plugHousingBracketHolder"
  Shapes = -> [Box004,Box002,Box003]
FEATURE [Part::Cylinder] Cylinder010
  Angle = 360
  AttacherType = Attacher::AttachEngine3D
  Height = 20
  Placement = pos=(0,0,36.15) rot=(0,0,1;0rad)
  Radius = 14.3
FEATURE [Part::Cylinder] Cylinder011
  Angle = 360
  AttacherType = Attacher::AttachEngine3D
  Height = 10
  Placement = pos=(0,0,36.15) rot=(0,0,1;0rad)
  Radius = 4
FEATURE [Part::MultiFuse] Fusion030  label="removeToCreteHoleForPlugHousing002"
  Placement = pos=(70,19,36) rot=(0,1,0;1.5708rad)
  Shapes = -> [Cylinder010,Cylinder011]
FEATURE [Part::Cut] Cut006  label="plugHousingBracketHolder001"
  Base = -> Fusion029
  Tool = -> Fusion030
FEATURE [Part::Cylinder] Cylinder012
  Angle = 360
  AttacherType = Attacher::AttachEngine3D
  Height = 20
  Placement = pos=(0,0,36.15) rot=(0,0,1;0rad)
  Radius = 7
FEATURE [Part::Cylinder] Cylinder013
  Angle = 360
  AttacherType = Attacher::AttachEngine3D
  Height = 10
  Placement = pos=(0,0,36.15) rot=(0,0,1;0rad)
  Radius = 4
FEATURE [Part::MultiFuse] Fusion032  label="removeToCreteHoleForPlugHousing003"
  Placement = pos=(70,19,36) rot=(0,1,0;1.5708rad)
  Shapes = -> [Cylinder012,Cylinder013]
FEATURE [Part::Cut] Cut007  label="bottom002"
  Base = -> Cut002
  Tool = -> Fusion032
FEATURE [Sketcher::SketchObject] Sketch008
  FullyConstrained = true
  sketch-geometry (54):
    g0: LineSegment StartX=-4.2 StartY=0 StartZ=0 EndX=-6.2 EndY=0 EndZ=0
    g1: LineSegment StartX=-14 StartY=-18 StartZ=0 EndX=-14 EndY=-26.5 EndZ=0
    g2: LineSegment StartX=-4.2 StartY=0 StartZ=0 EndX=-4.2 EndY=-13.4877 EndZ=0
    g3: Circle CenterX=-4.2 CenterY=-13.4877 CenterZ=0 NormalX=0 NormalY=0 NormalZ=1 AngleXU=0 Radius=1
    g4: Circle CenterX=-4.2 CenterY=-26.5 CenterZ=0 NormalX=0 NormalY=0 NormalZ=1 AngleXU=0 Radius=1
    g5: Circle CenterX=-8.2 CenterY=-26.5 CenterZ=0 NormalX=0 NormalY=0 NormalZ=1 AngleXU=0 Radius=1
    g6: BSplineCurve PolesCount=3 KnotsCount=2 Degree=2 IsPeriodic=0
    g7: GeomPoint X=-4.2 Y=-13.4877 Z=0
    g8: GeomPoint X=-8.2 Y=-26.5 Z=0
    g9: LineSegment StartX=-14 StartY=-26.5 StartZ=0 EndX=-8.2 EndY=-26.5 EndZ=0
    g10: LineSegment StartX=-10.15 StartY=-12 StartZ=0 EndX=-10.15 EndY=-14 EndZ=0
    g11: LineSegment StartX=-12.8401 StartY=-16 StartZ=0 EndX=-10.1571 EndY=-16 EndZ=0
    g12: LineSegment StartX=-10.15 StartY=-14 StartZ=0 EndX=-8.70761 EndY=-14 EndZ=0
    g13: LineSegment StartX=-12.8401 StartY=-16 StartZ=0 EndX=-12.8401 EndY=-17.6958 EndZ=0
    g14: LineSegment StartX=-10.15 StartY=-12 StartZ=0 EndX=-7.79258 EndY=-12 EndZ=0
    g15: Circle CenterX=-6.2215 CenterY=-2 CenterZ=0 NormalX=0 NormalY=0 NormalZ=1 AngleXU=0 Radius=1
    g16: Circle CenterX=-6.22762 CenterY=-2.58724 CenterZ=0 NormalX=0 NormalY=0 NormalZ=1 AngleXU=0 Radius=1
    g17: Circle CenterX=-6.32538 CenterY=-4 CenterZ=0 NormalX=0 NormalY=0 NormalZ=1 AngleXU=0 Radius=1
    g18: BSplineCurve PolesCount=3 KnotsCount=2 Degree=2 IsPeriodic=0
    g19: GeomPoint X=-6.2215 Y=-2 Z=0
    g20: GeomPoint X=-6.32538 Y=-4 Z=0
    g21: Circle CenterX=-6.48644 CenterY=-5.99526 CenterZ=0 NormalX=0 NormalY=0 NormalZ=1 AngleXU=0 Radius=1
    g22: Circle CenterX=-6.58486 CenterY=-6.99526 CenterZ=0 NormalX=0 NormalY=0 NormalZ=1 AngleXU=0 Radius=1
    g23: Circle CenterX=-6.77343 CenterY=-8 CenterZ=0 NormalX=0 NormalY=0 NormalZ=1 AngleXU=0 Radius=1
    g24: BSplineCurve PolesCount=3 KnotsCount=2 Degree=2 IsPeriodic=0
    g25: GeomPoint X=-6.48644 Y=-5.99526 Z=0
    g26: GeomPoint X=-6.77343 Y=-8 Z=0
    g27: Circle CenterX=-7.19003 CenterY=-10 CenterZ=0 NormalX=0 NormalY=0 NormalZ=1 AngleXU=0 Radius=1
    g28: Circle CenterX=-7.44407 CenterY=-11.0915 CenterZ=0 NormalX=0 NormalY=0 NormalZ=1 AngleXU=0 Radius=1
    g29: Circle CenterX=-7.79258 CenterY=-12 CenterZ=0 NormalX=0 NormalY=0 NormalZ=1 AngleXU=0 Radius=1
    g30: BSplineCurve PolesCount=3 KnotsCount=2 Degree=2 IsPeriodic=0
    g31: GeomPoint X=-7.19003 Y=-10 Z=0
    g32: GeomPoint X=-7.79258 Y=-12 Z=0
    g33: Circle CenterX=-8.70761 CenterY=-14 CenterZ=0 NormalX=0 NormalY=0 NormalZ=1 AngleXU=0 Radius=1
    g34: Circle CenterX=-9.33087 CenterY=-15.1837 CenterZ=0 NormalX=0 NormalY=0 NormalZ=1 AngleXU=0 Radius=1
    g35: Circle CenterX=-10.1571 CenterY=-16 CenterZ=0 NormalX=0 NormalY=0 NormalZ=1 AngleXU=0 Radius=1
    g36: BSplineCurve PolesCount=3 KnotsCount=2 Degree=2 IsPeriodic=0
    g37: GeomPoint X=-8.70761 Y=-14 Z=0
    g38: GeomPoint X=-10.1571 Y=-16 Z=0
    g39: Circle CenterX=-12.8401 CenterY=-17.6958 CenterZ=0 NormalX=0 NormalY=0 NormalZ=1 AngleXU=0 Radius=1
    g40: Circle CenterX=-13.3521 CenterY=-17.9027 CenterZ=0 NormalX=0 NormalY=0 NormalZ=1 AngleXU=0 Radius=1
    g41: Circle CenterX=-14 CenterY=-18 CenterZ=0 NormalX=0 NormalY=0 NormalZ=1 AngleXU=0 Radius=1
    g42: BSplineCurve PolesCount=3 KnotsCount=2 Degree=2 IsPeriodic=0
    g43: GeomPoint X=-12.8401 Y=-17.6958 Z=0
    g44: GeomPoint X=-14 Y=-18 Z=0
    g45: LineSegment StartX=-6.2 StartY=0 StartZ=0 EndX=-7.2 EndY=0 EndZ=0
    g46: LineSegment StartX=-7.2 StartY=0 StartZ=0 EndX=-7.2 EndY=-2 EndZ=0
    g47: LineSegment StartX=-7.2 StartY=-2 StartZ=0 EndX=-6.2215 EndY=-2 EndZ=0
    g48: LineSegment StartX=-6.32538 StartY=-4 StartZ=0 EndX=-7.65538 EndY=-4 EndZ=0
    g49: LineSegment StartX=-7.65538 StartY=-4 StartZ=0 EndX=-7.65538 EndY=-5.99526 EndZ=0
    g50: LineSegment StartX=-7.65538 StartY=-5.99526 StartZ=0 EndX=-6.48644 EndY=-5.99526 EndZ=0
    g51: LineSegment StartX=-6.77343 StartY=-8 StartZ=0 EndX=-8.43343 EndY=-8 EndZ=0
    g52: LineSegment StartX=-8.43343 StartY=-8 StartZ=0 EndX=-8.43343 EndY=-10 EndZ=0
    g53: LineSegment StartX=-8.43343 StartY=-10 StartZ=0 EndX=-7.19003 EndY=-10 EndZ=0
  constraints (112):
    c: Horizontal(g0)
    c: Distance(g0) = 2
    c: Block(g0)
    c: Vertical(g1)
    c: Coincident(g2,g0)
    c: Vertical(g2)
    c: Block(g2)
    c: Coincident(g6,g2)
    c: Weight(g3) = 1
    c: Equal(g3,g4)
    c: Equal(g3,g5)
    c: InternalAlignment(g3,g6)
    c: InternalAlignment(g4,g6)
    c: InternalAlignment(g5,g6)
    c: InternalAlignment(g7,g6)
    c: InternalAlignment(g8,g6)
    c: Block(g6)
    c: Coincident(g9,g1)
    c: Coincident(g9,g6)
    c: Horizontal(g9)
    c: Vertical(g10)
    c: Block(g10)
    c: Horizontal(g11)
    c: Block(g11)
    c: Coincident(g12,g10)
    c: Horizontal(g12)
    c: Block(g12)
    c: Coincident(g13,g11)
    c: Vertical(g13)
    c: Block(g13)
    c: Coincident(g14,g10)
    c: Horizontal(g14)
    c: Block(g14)
    c: Block(g9)
    c: Block(g1)
    c: Weight(g15) = 1
    c: Equal(g15,g16)
    c: Equal(g15,g17)
    c: InternalAlignment(g15,g18)
    c: InternalAlignment(g16,g18)
    c: InternalAlignment(g17,g18)
    c: InternalAlignment(g19,g18)
    c: InternalAlignment(g20,g18)
    c: Weight(g21) = 1
    c: Equal(g21,g22)
    c: Equal(g21,g23)
    c: InternalAlignment(g21,g24)
    c: InternalAlignment(g22,g24)
    c: InternalAlignment(g23,g24)
    c: InternalAlignment(g25,g24)
    c: InternalAlignment(g26,g24)
    c: Weight(g27) = 1
    c: Equal(g27,g28)
    c: Equal(g27,g29)
    c: Coincident(g30,g14)
    c: InternalAlignment(g27,g30)
    c: InternalAlignment(g28,g30)
    c: InternalAlignment(g29,g30)
    c: InternalAlignment(g31,g30)
    c: InternalAlignment(g32,g30)
    c: Coincident(g36,g12)
    c: Weight(g33) = 1
    c: Equal(g33,g34)
    c: Equal(g33,g35)
    c: Coincident(g36,g11)
    c: InternalAlignment(g33,g36)
    c: InternalAlignment(g34,g36)
    c: InternalAlignment(g35,g36)
    c: InternalAlignment(g37,g36)
    c: InternalAlignment(g38,g36)
    c: Coincident(g42,g13)
    c: Weight(g39) = 1
    c: Equal(g39,g40)
    c: Equal(g39,g41)
    c: Coincident(g42,g1)
    c: InternalAlignment(g39,g42)
    c: InternalAlignment(g40,g42)
    c: InternalAlignment(g41,g42)
    c: InternalAlignment(g43,g42)
    c: InternalAlignment(g44,g42)
    c: Block(g18)
    c: Block(g24)
    c: Block(g30)
    c: Block(g36)
    c: Block(g42)
    c: Horizontal(g45)
    c: Coincident(g45,g0)
    c: Vertical(g46)
    c: Coincident(g46,g45)
    c: Coincident(g47,g46)
    c: Coincident(g47,g18)
    c: Horizontal(g47)
    c: Block(g46)
    c: Coincident(g48,g18)
    c: Horizontal(g48)
    c: Distance(g48) = 1.33
    c: Vertical(g49)
    c: Coincident(g49,g48)
    c: Coincident(g50,g49)
    c: Coincident(g50,g24)
    c: Horizontal(g50)
    c: Tangent(g50,g22)
    c: Horizontal(g51)
    c: Coincident(g51,g24)
    c: Block(g51)
    c: Vertical(g52)
    c: Block(g52)
    c: Coincident(g52,g51)
    c: Coincident(g53,g52)
    c: Coincident(g53,g30)
    c: Horizontal(g53)
    c: Distance(g1) = 8.5
FEATURE [Part::Feature] Face024
  shape: bbox 9.8 x 26.5 x 2e-07 mm, 1 faces, 0 solids (baked)
FEATURE [Part::Revolution] Revolve024
  Angle = 360
  Axis = (0,1,0)
  Base = (0,0,0)
  FaceMakerClass = Part::FaceMakerBullseye
  Placement = pos=(0,0,0) rot=(0,0,1;1.5708rad)
  Solid = false
  Source = -> Face024
  Symmetric = false
FEATURE [Part::Feature] Face025
  shape: bbox 9.8 x 26.5 x 2e-07 mm, 1 faces, 0 solids (baked)
FEATURE [Part::Revolution] Revolve025
  Angle = 360
  Axis = (0,1,0)
  Base = (0,0,0)
  FaceMakerClass = Part::FaceMakerBullseye
  Placement = pos=(0,0,0) rot=(0,0,1;1.5708rad)
  Solid = false
  Source = -> Face025
  Symmetric = false
FEATURE [Part::MultiFuse] Fusion033
  Placement = pos=(-18,19,36) rot=(0,0,1;0rad)
  Shapes = -> [Revolve025,Revolve024]
FEATURE [Part::Cylinder] Cylinder014
  Angle = 360
  AttacherType = Attacher::AttachEngine3D
  Height = 20
  Placement = pos=(0,0,36.15) rot=(0,0,1;0rad)
  Radius = 14.3
FEATURE [Part::Cylinder] Cylinder015
  Angle = 360
  AttacherType = Attacher::AttachEngine3D
  Height = 10
  Placement = pos=(0,0,36.15) rot=(0,0,1;0rad)
  Radius = 4
FEATURE [Part::MultiFuse] Fusion034  label="removeToCreteHoleForPlugHousing004"
  Placement = pos=(-42,19,36) rot=(0,1,0;1.5708rad)
  Shapes = -> [Cylinder014,Cylinder015]
FEATURE [Part::Cut] Cut008  label="top004"
  Base = -> Cut004
  Placement = pos=(-1,0,0) rot=(0,0,1;0rad)
  Tool = -> Fusion034
FEATURE [Part::Box] Box005  label="Cube005"
  AttacherType = Attacher::AttachEngine3D
  Height = 28
  Length = 3
  Placement = pos=(110.7,19,22) rot=(0,0,1;0rad)
  Width = 15.7
FEATURE [Part::Cylinder] Cylinder016
  Angle = 360
  AttacherType = Attacher::AttachEngine3D
  Height = 10
  Placement = pos=(0,0,36.15) rot=(0,0,1;0rad)
  Radius = 4
FEATURE [Part::Cylinder] Cylinder017
  Angle = 360
  AttacherType = Attacher::AttachEngine3D
  Height = 20
  Placement = pos=(0,0,36.15) rot=(0,0,1;0rad)
  Radius = 10.3
FEATURE [Part::MultiFuse] Fusion035  label="removeToCreteHoleForPlugHousing005"
  Placement = pos=(70,19,36) rot=(0,1,0;1.5708rad)
  Shapes = -> [Cylinder017,Cylinder016]
FEATURE [Part::Cut] Cut009  label="plugHousingTab001"
  Base = -> Box005
  Placement = pos=(-107.4,-14,0) rot=(0,0,1;0rad)
  Tool = -> Fusion035
FEATURE [Part::Box] Box006  label="Cube006"
  AttacherType = Attacher::AttachEngine3D
  Height = 28
  Length = 3
  Placement = pos=(110.7,19,22) rot=(0,0,1;0rad)
  Width = 15.7
FEATURE [Part::Cylinder] Cylinder018
  Angle = 360
  AttacherType = Attacher::AttachEngine3D
  Height = 10
  Placement = pos=(0,0,36.15) rot=(0,0,1;0rad)
  Radius = 4
FEATURE [Part::Cylinder] Cylinder019
  Angle = 360
  AttacherType = Attacher::AttachEngine3D
  Height = 20
  Placement = pos=(0,0,36.15) rot=(0,0,1;0rad)
  Radius = 10.3
FEATURE [Part::MultiFuse] Fusion036  label="removeToCreteHoleForPlugHousing006"
  Placement = pos=(70,19,36) rot=(0,1,0;1.5708rad)
  Shapes = -> [Cylinder019,Cylinder018]
FEATURE [Part::Cut] Cut010  label="plugHousingTab002"
  Base = -> Box006
  Placement = pos=(-107.4,-14,0) rot=(0,0,1;0rad)
  Tool = -> Fusion036
FEATURE [Part::MultiFuse] Fusion037
  Placement = pos=(9.6,23,0) rot=(0,0,1;3.14159rad)
  Shapes = -> [Cut009,Cut010]
FEATURE [Part::Box] Box  label="Cube"
  AttacherType = Attacher::AttachEngine3D
  Height = 10
  Length = 3
  Placement = pos=(3.3,4,12) rot=(0,0,1;0rad)
  Width = 10
FEATURE [Part::Fillet] Fillet004
  Base = -> Fusion028
  Edges = 1 edges r=2: [Edge25]
FEATURE [Part::Fillet] Fillet005  label="plugHousing046"
  Base = -> Fillet004
  Edges = 1 edges r=2: [Edge8]
FEATURE [Part::Fillet] Fillet006
  Base = -> Box
  Edges = 1 edges r=2: [Edge11]
FEATURE [Part::Box] Box007  label="Cube007"
  AttacherType = Attacher::AttachEngine3D
  Height = 10
  Length = 3
  Placement = pos=(3.3,4,50) rot=(0,0,1;0rad)
  Width = 10
FEATURE [Part::Fillet] Fillet007
  Base = -> Box007
  Edges = 1 edges r=2: [Edge12]
FEATURE [Part::Box] Box008  label="Cube008"
  AttacherType = Attacher::AttachEngine3D
  Height = 28
  Length = 4
  Placement = pos=(5,0,22) rot=(0,0,1;0rad)
  Width = 10
FEATURE [Part::Fillet] Fillet008
  Base = -> Box008
  Edges = 1 edges r=1: [Edge7]
FEATURE [Part::Fillet] Fillet009
  Base = -> Fillet008
  Edges = 1 edges r=2: [Edge5]
FEATURE [Part::Fillet] Fillet010
  Base = -> Fillet009
  Edges = 1 edges r=2: [Edge2]
FEATURE [Sketcher::SketchObject] Sketch009  label="topSketch003"
  FullyConstrained = true
  sketch-geometry (4):
    g0: LineSegment StartX=16.8446 StartY=31.512 StartZ=0 EndX=16.3251 EndY=34.4666 EndZ=0
    g1: ArcOfCircle CenterX=19 CenterY=19.2524 CenterZ=0 NormalX=0 NormalY=0 NormalZ=1 AngleXU=0 Radius=15.4476 StartAngle=1.74483 EndAngle=2.72717
    g2: ArcOfCircle CenterX=19 CenterY=19.2524 CenterZ=0 NormalX=0 NormalY=0 NormalZ=1 AngleXU=0 Radius=12.4476 StartAngle=1.74483 EndAngle=2.73189
    g3: LineSegment StartX=4.86004 StartY=25.4725 StartZ=0 EndX=7.58253 EndY=24.2107 EndZ=0
  constraints (7):
    c: Block(g0)
    c: Coincident(g1,g0)
    c: Coincident(g2,g0)
    c: Coincident(g3,g1)
    c: Coincident(g3,g2)
    c: Block(g1)
    c: Block(g2)
FEATURE [Part::Extrusion] Extrude008
  Base = -> Sketch009
  Dir = (0,0,1)
  DirMode = 2
  FaceMakerClass = Part::FaceMakerBullseye
  LengthFwd = 10
  LengthRev = 0
  Placement = pos=(0,0,31) rot=(0,0,1;0rad)
  Solid = true
  Symmetric = false
FEATURE [Part::Cylinder] Cylinder020
  Angle = 360
  AttacherType = Attacher::AttachEngine3D
  Height = 20
  Placement = pos=(0,0,36.15) rot=(0,0,1;0rad)
  Radius = 8.2
FEATURE [Part::Cylinder] Cylinder021
  Angle = 360
  AttacherType = Attacher::AttachEngine3D
  Height = 10
  Placement = pos=(0,0,36.15) rot=(0,0,1;0rad)
  Radius = 4
FEATURE [Part::MultiFuse] Fusion038  label="removeToCreteHoleForPlugHousing007"
  Placement = pos=(-42,19,36) rot=(0,1,0;1.5708rad)
  Shapes = -> [Cylinder020,Cylinder021]
FEATURE [Part::Cut] Cut011
  Base = -> Extrude008
  Tool = -> Fusion038
FEATURE [Part::Fillet] Fillet011
  Base = -> Cut011
  Edges = 1 edges r=2: [Edge1]
FEATURE [Part::Fillet] Fillet012
  Base = -> Fillet011
  Edges = 1 edges r=2.5: [Edge1]
FEATURE [Part::Fillet] Fillet013
  Base = -> Fillet012
  Edges = 1 edges r=2.5: [Edge2]
FEATURE [Part::Box] Box010  label="Cube010"
  AttacherType = Attacher::AttachEngine3D
  Height = 16
  Length = 8
  Placement = pos=(12.7,31.52,28) rot=(0,0,1;0rad)
  Width = 4
FEATURE [Sketcher::SketchObject] Sketch010  label="topSketch004"
  FullyConstrained = true
  sketch-geometry (4):
    g0: LineSegment StartX=16.8446 StartY=31.512 StartZ=0 EndX=16.3251 EndY=34.4666 EndZ=0
    g1: ArcOfCircle CenterX=19 CenterY=19.2524 CenterZ=0 NormalX=0 NormalY=0 NormalZ=1 AngleXU=0 Radius=15.4476 StartAngle=1.74483 EndAngle=2.72717
    g2: ArcOfCircle CenterX=19 CenterY=19.2524 CenterZ=0 NormalX=0 NormalY=0 NormalZ=1 AngleXU=0 Radius=12.4476 StartAngle=1.74483 EndAngle=2.73189
    g3: LineSegment StartX=4.86004 StartY=25.4725 StartZ=0 EndX=7.58253 EndY=24.2107 EndZ=0
  constraints (7):
    c: Block(g0)
    c: Coincident(g1,g0)
    c: Coincident(g2,g0)
    c: Coincident(g3,g1)
    c: Coincident(g3,g2)
    c: Block(g1)
    c: Block(g2)
FEATURE [Part::Cylinder] Cylinder022
  Angle = 360
  AttacherType = Attacher::AttachEngine3D
  Height = 10
  Placement = pos=(0,0,36.15) rot=(0,0,1;0rad)
  Radius = 4
FEATURE [Sketcher::SketchObject] Sketch011  label="topSketch005"
  FullyConstrained = true
  sketch-geometry (4):
    g0: LineSegment StartX=16.8446 StartY=31.512 StartZ=0 EndX=16.3251 EndY=34.4666 EndZ=0
    g1: ArcOfCircle CenterX=19 CenterY=19.2524 CenterZ=0 NormalX=0 NormalY=0 NormalZ=1 AngleXU=0 Radius=15.4476 StartAngle=1.74483 EndAngle=2.72717
    g2: ArcOfCircle CenterX=19 CenterY=19.2524 CenterZ=0 NormalX=0 NormalY=0 NormalZ=1 AngleXU=0 Radius=12.4476 StartAngle=1.74483 EndAngle=2.73189
    g3: LineSegment StartX=4.86004 StartY=25.4725 StartZ=0 EndX=7.58253 EndY=24.2107 EndZ=0
  constraints (7):
    c: Block(g0)
    c: Coincident(g1,g0)
    c: Coincident(g2,g0)
    c: Coincident(g3,g1)
    c: Coincident(g3,g2)
    c: Block(g1)
    c: Block(g2)
FEATURE [Part::Extrusion] Extrude010
  Base = -> Sketch011
  Dir = (0,0,1)
  DirMode = 2
  FaceMakerClass = Part::FaceMakerBullseye
  LengthFwd = 10.6
  LengthRev = 0
  Placement = pos=(0,0,31) rot=(0,0,1;0rad)
  Solid = true
  Symmetric = false
FEATURE [Part::Cylinder] Cylinder023
  Angle = 360
  AttacherType = Attacher::AttachEngine3D
  Height = 20
  Placement = pos=(0,0,36.15) rot=(0,0,1;0rad)
  Radius = 8.2
FEATURE [Part::MultiFuse] Fusion039  label="removeToCreteHoleForPlugHousing008"
  Placement = pos=(-42,19,36) rot=(0,1,0;1.5708rad)
  Shapes = -> [Cylinder023,Cylinder022]
FEATURE [Part::Cut] Cut012
  Base = -> Extrude010
  Placement = pos=(0,0,-0.3) rot=(0,0,1;0rad)
  Tool = -> Fusion039
FEATURE [Part::Cut] Cut013
  Base = -> Box010
  Tool = -> Cut012
FEATURE [Part::Fillet] Fillet014
  Base = -> Cut013
  Edges = 1 edges r=0.7: [Edge13]
FEATURE [Part::Fillet] Fillet015
  Base = -> Fillet014
  Edges = 1 edges r=0.7: [Edge13]
FEATURE [Part::Fillet] Fillet016
  Base = -> Fillet015
  Edges = 1 edges r=0.7: [Edge16]
FEATURE [Part::Fillet] Fillet017
  Base = -> Fillet016
  Edges = 1 edges r=0.7: [Edge11]
FEATURE [Part::Fillet] Fillet018
  Base = -> Fillet017
  Edges = 1 edges r=0.7: [Edge10]
FEATURE [Part::Fillet] Fillet019
  Base = -> Fillet018
  Edges = 1 edges r=1.2: [Edge5]
FEATURE [Part::Fillet] Fillet020
  Base = -> Fillet019
  Edges = 1 edges r=1.2: [Edge12]
FEATURE [Part::Fillet] Fillet021
  Base = -> Fillet020
  Edges = 1 edges r=2: [Edge1]
  Placement = pos=(0.3,0,0) rot=(0,0,1;0rad)
FEATURE [Part::MultiFuse] Fusion040  label="top005"
  Shapes = -> [Cut008,Fillet021]
FEATURE [Part::MultiFuse] Fusion041  label="wireHolder"
  Shapes = -> [Fusion033,Fillet013]
FEATURE [Part::MultiFuse] Fusion042
  Shapes = -> [Fillet007,Fusion041]
FEATURE [Part::MultiFuse] Fusion043  label="wireHolder001"
  Shapes = -> [Fusion042,Fillet010]
FEATURE [Part::MultiFuse] Fusion044  label="wireHolder002"
  Shapes = -> [Fillet006,Fusion037,Fusion043]
FEATURE [Part::Feature] Face026
  shape: bbox 11 x 6 x 2e-07 mm, 1 faces, 0 solids (baked)
FEATURE [Part::Revolution] Revolve026
  Angle = 360
  Axis = (0,1,0)
  Base = (0,0,0)
  FaceMakerClass = Part::FaceMakerBullseye
  Placement = pos=(30.3,-1,19.7) rot=(0,0,1;0rad)
  Solid = false
  Source = -> Face026
  Symmetric = false
FEATURE [Sketcher::SketchObject] Sketch013  label="topSketch006"
  FullyConstrained = true
  sketch-geometry (13):
    g0: LineSegment StartX=117 StartY=19 StartZ=0 EndX=117 EndY=38 EndZ=0
    g1: ArcOfCircle CenterX=98 CenterY=19 CenterZ=0 NormalX=0 NormalY=0 NormalZ=1 AngleXU=0 Radius=19 StartAngle=5.7297 EndAngle=6.28319
    g2: LineSegment StartX=0 StartY=3 StartZ=0 EndX=0 EndY=19 EndZ=0
    g3: LineSegment StartX=19 StartY=38 StartZ=0 EndX=117 EndY=38 EndZ=0
    g4: ArcOfCircle CenterX=19 CenterY=19 CenterZ=0 NormalX=0 NormalY=0 NormalZ=1 AngleXU=0 Radius=19 StartAngle=1.5708 EndAngle=3.14159
    g5: ArcOfCircle CenterX=19 CenterY=19 CenterZ=0 NormalX=0 NormalY=0 NormalZ=1 AngleXU=0 Radius=16 StartAngle=1.5708 EndAngle=3.14159
    g6: ArcOfCircle CenterX=98 CenterY=19 CenterZ=0 NormalX=0 NormalY=0 NormalZ=1 AngleXU=0 Radius=16 StartAngle=5.60905 EndAngle=6.28319
    g7: LineSegment StartX=114 StartY=19 StartZ=0 EndX=114 EndY=35 EndZ=0
    g8: LineSegment StartX=110.5 StartY=9.01251 StartZ=0 EndX=114.163 EndY=9.01251 EndZ=0
    g9: LineSegment StartX=114 StartY=35 StartZ=0 EndX=19 EndY=35 EndZ=0
    g10: LineSegment StartX=0 StartY=3 StartZ=0 EndX=0 EndY=0 EndZ=0
    g11: LineSegment StartX=3 StartY=0 StartZ=0 EndX=0 EndY=0 EndZ=0
    g12: LineSegment StartX=3 StartY=19 StartZ=0 EndX=3 EndY=0 EndZ=0
  constraints (33):
    c: Vertical(g0)
    c: Distance(g0) = 19
    c: Block(g0)
    c: Coincident(g1,g0)
    c: Block(g1)
    c: Vertical(g2)
    c: Block(g2)
    c: Coincident(g3,g0)
    c: Horizontal(g3)
    c: Distance(g3) = 98
    c: Coincident(g4,g3)
    c: Coincident(g4,g2)
    c: Block(g4)
    c: Coincident(g5,g4)
    c: Coincident(g6,g1)
    c: Block(g6)
    c: Block(g5)
    c: Coincident(g7,g6)
    c: Vertical(g7)
    c: Coincident(g8,g6)
    c: Coincident(g8,g1)
    c: Coincident(g9,g7)
    c: Coincident(g9,g5)
    c: Horizontal(g9)
    c: Tangent(g9,g5)
    c: Coincident(g10,g2)
    c: Distance(g10) = 3
    c: Vertical(g10)
    c: Coincident(g11,g10)
    c: Horizontal(g11)
    c: Coincident(g12,g5)
    c: Coincident(g12,g11)
    c: Vertical(g12)
FEATURE [Part::Extrusion] Extrude011  label="top006"
  Base = -> Sketch013
  Dir = (0,0,1)
  DirMode = 2
  FaceMakerClass = Part::FaceMakerBullseye
  LengthFwd = 72
  LengthRev = 0
  Solid = true
  Symmetric = false
FEATURE [Sketcher::SketchObject] Sketch014
  FullyConstrained = true
  MapMode = 3
  Placement = pos=(0,0,0) rot=(1,0,0;1.5708rad)
  Support = -> [Extrude011]
  sketch-geometry (8):
    g0: Circle CenterX=80.351 CenterY=-67.6202 CenterZ=0 NormalX=0 NormalY=0 NormalZ=1 AngleXU=0 Radius=2
    g1: Circle CenterX=80.351 CenterY=-67.6202 CenterZ=0 NormalX=0 NormalY=0 NormalZ=1 AngleXU=0 Radius=3
    g2: Circle CenterX=80.351 CenterY=-4.92017 CenterZ=0 NormalX=0 NormalY=0 NormalZ=1 AngleXU=0 Radius=2
    g3: Circle CenterX=80.351 CenterY=-4.92017 CenterZ=0 NormalX=0 NormalY=0 NormalZ=1 AngleXU=0 Radius=3
    g4: Circle CenterX=23.851 CenterY=-4.92017 CenterZ=0 NormalX=0 NormalY=0 NormalZ=1 AngleXU=0 Radius=2
    g5: Circle CenterX=23.851 CenterY=-4.92017 CenterZ=0 NormalX=0 NormalY=0 NormalZ=1 AngleXU=0 Radius=3
    g6: Circle CenterX=23.851 CenterY=-67.6202 CenterZ=0 NormalX=0 NormalY=0 NormalZ=1 AngleXU=0 Radius=2
    g7: Circle CenterX=23.851 CenterY=-67.6202 CenterZ=0 NormalX=0 NormalY=0 NormalZ=1 AngleXU=0 Radius=3
  constraints (8):
    c: Block(g3)
    c: Block(g2)
    c: Block(g1)
    c: Block(g0)
    c: Block(g6)
    c: Block(g7)
    c: Block(g4)
    c: Block(g5)
FEATURE [Part::Feature] Face027
  shape: bbox 11 x 6 x 2e-07 mm, 1 faces, 0 solids (baked)
FEATURE [Part::Revolution] Revolve027
  Angle = 360
  Axis = (0,1,0)
  Base = (0,0,0)
  FaceMakerClass = Part::FaceMakerBullseye
  Placement = pos=(30.3,-1,51.7) rot=(0,0,1;0rad)
  Solid = false
  Source = -> Face027
  Symmetric = false
FEATURE [Part::Feature] Face028
  shape: bbox 11 x 6 x 2e-07 mm, 1 faces, 0 solids (baked)
FEATURE [Part::Revolution] Revolve028
  Angle = 360
  Axis = (0,1,0)
  Base = (0,0,0)
  FaceMakerClass = Part::FaceMakerBullseye
  Placement = pos=(62.3,-1,19.7) rot=(0,0,1;0rad)
  Solid = false
  Source = -> Face028
  Symmetric = false
FEATURE [Part::Feature] Face029
  shape: bbox 11 x 6 x 2e-07 mm, 1 faces, 0 solids (baked)
FEATURE [Part::Revolution] Revolve029
  Angle = 360
  Axis = (0,1,0)
  Base = (0,0,0)
  FaceMakerClass = Part::FaceMakerBullseye
  Placement = pos=(62.3,-1,51.7) rot=(0,0,1;0rad)
  Solid = false
  Source = -> Face029
  Symmetric = false
FEATURE [Part::Feature] Wire
  shape: bbox 11 x 5.2 x 2e-07 mm, 0 faces, 0 solids (baked)
FEATURE [Part::Revolution] Revolve030
  Angle = 360
  Axis = (0,1,0)
  Base = (0,0,0)
  FaceMakerClass = Part::FaceMakerBullseye
  Placement = pos=(30.3,38,19.7) rot=(0,0,1;0rad)
  Solid = true
  Source = -> Wire
  Symmetric = false
FEATURE [Part::Feature] Wire001
  shape: bbox 11 x 5.2 x 2e-07 mm, 0 faces, 0 solids (baked)
FEATURE [Part::Revolution] Revolve031
  Angle = 360
  Axis = (0,1,0)
  Base = (0,0,0)
  FaceMakerClass = Part::FaceMakerBullseye
  Placement = pos=(30.3,38,51.7) rot=(0,0,1;0rad)
  Solid = true
  Source = -> Wire001
  Symmetric = false
FEATURE [Part::Feature] Wire002
  shape: bbox 11 x 5.2 x 2e-07 mm, 0 faces, 0 solids (baked)
FEATURE [Part::Revolution] Revolve032
  Angle = 360
  Axis = (0,1,0)
  Base = (0,0,0)
  FaceMakerClass = Part::FaceMakerBullseye
  Placement = pos=(62.3,38,51.7) rot=(0,0,1;0rad)
  Solid = true
  Source = -> Wire002
  Symmetric = false
FEATURE [Part::Feature] Wire003
  shape: bbox 11 x 5.2 x 2e-07 mm, 0 faces, 0 solids (baked)
FEATURE [Part::Revolution] Revolve033
  Angle = 360
  Axis = (0,1,0)
  Base = (0,0,0)
  FaceMakerClass = Part::FaceMakerBullseye
  Placement = pos=(62.3,38,19.7) rot=(0,0,1;0rad)
  Solid = true
  Source = -> Wire003
  Symmetric = false
FEATURE [Part::MultiFuse] Fusion045  label="altRandScrewHousing"
  Shapes = -> [Revolve029,Revolve027,Revolve028,Revolve026]
FEATURE [Part::MultiFuse] Fusion046  label="fanScrewHousing"
  Shapes = -> [Revolve033,Revolve032,Revolve031,Revolve030]
FEATURE [Sketcher::SketchObject] Sketch015
  FullyConstrained = true
  sketch-geometry (17):
    g0: Circle CenterX=-3.5 CenterY=23.5 CenterZ=0 NormalX=0 NormalY=0 NormalZ=1 AngleXU=0 Radius=1
    g1: Circle CenterX=-1 CenterY=15.25 CenterZ=0 NormalX=0 NormalY=0 NormalZ=1 AngleXU=0 Radius=1
    g2: Circle CenterX=-3.5 CenterY=7 CenterZ=0 NormalX=0 NormalY=0 NormalZ=1 AngleXU=0 Radius=1
    g3: BSplineCurve PolesCount=3 KnotsCount=2 Degree=2 IsPeriodic=0
    g4: GeomPoint X=-3.5 Y=23.5 Z=0
    g5: GeomPoint X=-3.5 Y=7 Z=0
    g6: Circle CenterX=-4.8 CenterY=30.5 CenterZ=0 NormalX=0 NormalY=0 NormalZ=1 AngleXU=0 Radius=1
    g7: Circle CenterX=-3.5 CenterY=30.5 CenterZ=0 NormalX=0 NormalY=0 NormalZ=1 AngleXU=0 Radius=1
    g8: Circle CenterX=-3.5 CenterY=29.2 CenterZ=0 NormalX=0 NormalY=0 NormalZ=1 AngleXU=0 Radius=1
    g9: BSplineCurve PolesCount=3 KnotsCount=2 Degree=2 IsPeriodic=0
    g10: GeomPoint X=-4.8 Y=30.5 Z=0
    g11: GeomPoint X=-3.5 Y=29.2 Z=0
    g12: LineSegment StartX=-3.5 StartY=29.2 StartZ=0 EndX=-3.5 EndY=23.5 EndZ=0
    g13: LineSegment StartX=-4.8 StartY=30.5 StartZ=0 EndX=0 EndY=30.5 EndZ=0
    g14: LineSegment StartX=-3.5 StartY=0.3 StartZ=0 EndX=0 EndY=0.3 EndZ=0
    g15: LineSegment StartX=-3.5 StartY=0.3 StartZ=0 EndX=-3.5 EndY=7 EndZ=0
    g16: LineSegment StartX=0 StartY=0.3 StartZ=0 EndX=0 EndY=30.5 EndZ=0
  constraints (33):
    c: Weight(g0) = 1
    c: Equal(g0,g1)
    c: Equal(g0,g2)
    c: InternalAlignment(g0,g3)
    c: InternalAlignment(g1,g3)
    c: InternalAlignment(g2,g3)
    c: InternalAlignment(g4,g3)
    c: InternalAlignment(g5,g3)
    c: Block(g3)
    c: Weight(g6) = 1
    c: Equal(g6,g7)
    c: Equal(g6,g8)
    c: InternalAlignment(g6,g9)
    c: InternalAlignment(g7,g9)
    c: InternalAlignment(g8,g9)
    c: InternalAlignment(g10,g9)
    c: InternalAlignment(g11,g9)
    c: Block(g9)
    c: Coincident(g12,g9)
    c: Coincident(g12,g3)
    c: Vertical(g12)
    c: Coincident(g13,g9)
    c: Horizontal(g13)
    c: Distance(g13) = 4.8
    c: Horizontal(g14)
    c: Block(g14)
    c: Coincident(g15,g14)
    c: Coincident(g15,g3)
    c: Vertical(g15)
    c: Coincident(g16,g14)
    c: Coincident(g16,g13)
    c: Vertical(g16)
    c: Tangent(g16,g1)
FEATURE [Sketcher::SketchObject] Sketch016
  FullyConstrained = true
  sketch-geometry (16):
    g0: Circle CenterX=-3.5 CenterY=23.5 CenterZ=0 NormalX=0 NormalY=0 NormalZ=1 AngleXU=0 Radius=1
    g1: Circle CenterX=-1 CenterY=15.25 CenterZ=0 NormalX=0 NormalY=0 NormalZ=1 AngleXU=0 Radius=1
    g2: Circle CenterX=-3.5 CenterY=7 CenterZ=0 NormalX=0 NormalY=0 NormalZ=1 AngleXU=0 Radius=1
    g3: BSplineCurve PolesCount=3 KnotsCount=2 Degree=2 IsPeriodic=0
    g4: GeomPoint X=-3.5 Y=23.5 Z=0
    g5: GeomPoint X=-3.5 Y=7 Z=0
    g6: LineSegment StartX=-3.5 StartY=28.2 StartZ=0 EndX=-3.5 EndY=23.5 EndZ=0
    g7: LineSegment StartX=0 StartY=29.5 StartZ=0 EndX=0 EndY=30 EndZ=0
    g8: LineSegment StartX=-3.5 StartY=28.2 StartZ=0 EndX=-3.5 EndY=30 EndZ=0
    g9: LineSegment StartX=0 StartY=30 StartZ=0 EndX=0 EndY=30.5 EndZ=0
    g10: LineSegment StartX=0 StartY=30.5 StartZ=0 EndX=-3.5 EndY=30.5 EndZ=0
    g11: LineSegment StartX=-3.5 StartY=30.5 StartZ=0 EndX=-3.5 EndY=30 EndZ=0
    g12: LineSegment StartX=0 StartY=29.5 StartZ=0 EndX=0 EndY=5 EndZ=0
    g13: LineSegment StartX=-3.5 StartY=0.3 StartZ=0 EndX=-3.5 EndY=7 EndZ=0
    g14: LineSegment StartX=-3.5 StartY=0.3 StartZ=0 EndX=0 EndY=0.3 EndZ=0
    g15: LineSegment StartX=0 StartY=5 StartZ=0 EndX=0 EndY=0.3 EndZ=0
  constraints (39):
    c: Weight(g0) = 1
    c: Equal(g0,g1)
    c: Equal(g0,g2)
    c: InternalAlignment(g0,g3)
    c: InternalAlignment(g1,g3)
    c: InternalAlignment(g2,g3)
    c: InternalAlignment(g4,g3)
    c: InternalAlignment(g5,g3)
    c: Block(g3)
    c: Coincident(g6,g3)
    c: Vertical(g6)
    c: Vertical(g7)
    c: Distance(g7) = 0.5
    c: Coincident(g8,g6)
    c: Vertical(g8)
    c: Block(g6)
    c: Block(g7)
    c: Vertical(g9)
    c: Equal(g7,g9) = 0.5
    c: Block(g9)
    c: Coincident(g9,g7)
    c: Horizontal(g10)
    c: Coincident(g10,g9)
    c: Coincident(g11,g10)
    c: Coincident(g11,g8)
    c: Vertical(g11)
    c: Block(g11)
    c: Coincident(g12,g7)
    c: Vertical(g12)
    c: Coincident(g13,g3)
    c: Vertical(g13)
    c: Distance(g13) = 6.7
    c: Coincident(g14,g13)
    c: Horizontal(g14)
    c: Block(g14)
    c: Coincident(g15,g12)
    c: Coincident(g15,g14)
    c: Vertical(g15)
    c: Block(g15)
FEATURE [Sketcher::SketchObject] Sketch017
  FullyConstrained = true
  sketch-geometry (11):
    g0: LineSegment StartX=-3.5 StartY=1e-16 StartZ=0 EndX=-1.6 EndY=1e-16 EndZ=0
    g1: LineSegment StartX=-1.6 StartY=1e-16 StartZ=0 EndX=-1.6 EndY=1.5 EndZ=0
    g2: LineSegment StartX=-3.5 StartY=1.5 StartZ=0 EndX=-1.6 EndY=1.5 EndZ=0
    g3: LineSegment StartX=-3.5 StartY=1e-16 StartZ=0 EndX=-4.8 EndY=1e-16 EndZ=0
    g4: Circle CenterX=-3.5 CenterY=1.3 CenterZ=0 NormalX=0 NormalY=0 NormalZ=1 AngleXU=0 Radius=1
    g5: Circle CenterX=-3.5 CenterY=1e-16 CenterZ=0 NormalX=0 NormalY=0 NormalZ=1 AngleXU=0 Radius=1
    g6: Circle CenterX=-4.8 CenterY=1e-16 CenterZ=0 NormalX=0 NormalY=0 NormalZ=1 AngleXU=0 Radius=1
    g7: BSplineCurve PolesCount=3 KnotsCount=2 Degree=2 IsPeriodic=0
    g8: GeomPoint X=-3.5 Y=1.3 Z=0
    g9: GeomPoint X=-4.8 Y=1e-16 Z=0
    g10: LineSegment StartX=-3.5 StartY=1.3 StartZ=0 EndX=-3.5 EndY=1.5 EndZ=0
  constraints (24):
    c: Horizontal(g0)
    c: Distance(g0) = 1.9
    c: Block(g0)
    c: Coincident(g1,g0)
    c: Vertical(g1)
    c: Coincident(g2,g1)
    c: Horizontal(g2)
    c: Coincident(g3,g0)
    c: Horizontal(g3)
    c: Distance(g3) = 1.3
    c: Weight(g4) = 1
    c: Equal(g4,g5)
    c: Coincident(g5,g0)
    c: Equal(g4,g6)
    c: Coincident(g7,g3)
    c: InternalAlignment(g4,g7)
    c: InternalAlignment(g5,g7)
    c: InternalAlignment(g6,g7)
    c: InternalAlignment(g8,g7)
    c: InternalAlignment(g9,g7)
    c: Coincident(g10,g7)
    c: Coincident(g10,g2)
    c: Vertical(g10)
    c: Block(g10)
FEATURE [Part::Feature] Face035
  shape: bbox 3.2 x 1.5 x 2e-07 mm, 1 faces, 0 solids (baked)
FEATURE [Part::Revolution] Revolve039  label="backCaseScrewRetainer"
  Angle = 360
  Axis = (0,1,0)
  Base = (0,0,0)
  FaceMakerClass = Part::FaceMakerBullseye
  Placement = pos=(12.5,3,62) rot=(0,0,1;0rad)
  Solid = false
  Source = -> Face035
  Symmetric = false
FEATURE [Part::Feature] Face036
  shape: bbox 3.2 x 1.5 x 2e-07 mm, 1 faces, 0 solids (baked)
FEATURE [Part::Feature] Face039
  shape: bbox 4.8 x 30.2 x 2e-07 mm, 1 faces, 0 solids (baked)
FEATURE [Part::Revolution] Revolve043  label="frontCaseScrewPost002"
  Angle = 360
  Axis = (0,1,0)
  Base = (0,0,0)
  FaceMakerClass = Part::FaceMakerBullseye
  Placement = pos=(89.5,4.5,3.5) rot=(0,0,1;0rad)
  Solid = false
  Source = -> Face039
  Symmetric = false
FEATURE [Part::Feature] Face042
  shape: bbox 4.8 x 30.2 x 2e-07 mm, 1 faces, 0 solids (baked)
FEATURE [Part::Revolution] Revolve046  label="frontCaseScrewPost003"
  Angle = 360
  Axis = (0,1,0)
  Base = (0,0,0)
  FaceMakerClass = Part::FaceMakerBullseye
  Placement = pos=(89.5,4.5,68.5) rot=(0,0,1;0rad)
  Solid = false
  Source = -> Face042
  Symmetric = false
FEATURE [Part::Feature] Face043
  shape: bbox 3.2 x 1.5 x 2e-07 mm, 1 faces, 0 solids (baked)
FEATURE [Part::Revolution] Revolve047  label="frontCaseScrewRetainer002"
  Angle = 360
  Axis = (0,1,0)
  Base = (0,0,0)
  FaceMakerClass = Part::FaceMakerBullseye
  Placement = pos=(89.5,3,68.5) rot=(0,0,1;0rad)
  Solid = false
  Source = -> Face043
  Symmetric = false
FEATURE [Part::Feature] Face044
  shape: bbox 3.2 x 1.5 x 2e-07 mm, 1 faces, 0 solids (baked)
FEATURE [Part::Revolution] Revolve048  label="frontCaseScrewRetainer003"
  Angle = 360
  Axis = (0,1,0)
  Base = (0,0,0)
  FaceMakerClass = Part::FaceMakerBullseye
  Placement = pos=(89.5,3,3.5) rot=(0,0,1;0rad)
  Solid = false
  Source = -> Face044
  Symmetric = false
FEATURE [App::MeasureDistance] Distance002  label="Distance: 1.67 mm"
  Distance = 1.66921
  P1 = (99.2361,4.7524,71.7)
  P2 = (99.2347,6.42161,71.7)
FEATURE [Sketcher::SketchObject] Sketch018
  FullyConstrained = true
  sketch-geometry (7):
    g0: LineSegment StartX=0 StartY=0 StartZ=0 EndX=0 EndY=6 EndZ=0
    g1: Circle CenterX=0 CenterY=0 CenterZ=0 NormalX=0 NormalY=0 NormalZ=1 AngleXU=0 Radius=1
    g2: Circle CenterX=8 CenterY=6 CenterZ=0 NormalX=0 NormalY=0 NormalZ=1 AngleXU=0 Radius=1
    g3: BSplineCurve PolesCount=3 KnotsCount=2 Degree=2 IsPeriodic=0
    g4: GeomPoint X=0 Y=0 Z=0
    g5: GeomPoint X=8 Y=6 Z=0
    g6: LineSegment StartX=0 StartY=6 StartZ=0 EndX=8 EndY=6 EndZ=0
  constraints (14):
    c: Coincident(g0,g-1)
    c: Distance(g0) = 6
    c: Vertical(g0)
    c: Coincident(g3,g0)
    c: Weight(g1) = 1
    c: Equal(g1,g2)
    c: InternalAlignment(g1,g3)
    c: InternalAlignment(g2,g3)
    c: InternalAlignment(g4,g3)
    c: InternalAlignment(g5,g3)
    c: Block(g3)
    c: Coincident(g6,g0)
    c: Coincident(g6,g3)
    c: Horizontal(g6)
FEATURE [Part::Extrusion] Extrude012  label="caseScrewPillarBracket"
  Base = -> Sketch018
  Dir = (0,0,1)
  DirMode = 2
  FaceMakerClass = Part::FaceMakerBullseye
  LengthFwd = 2.4
  LengthRev = 0
  Placement = pos=(15.76,29,8.8) rot=(0,1,0;0rad)
  Solid = true
  Symmetric = false
FEATURE [Sketcher::SketchObject] Sketch019
  FullyConstrained = true
  sketch-geometry (7):
    g0: LineSegment StartX=0 StartY=0 StartZ=0 EndX=0 EndY=6 EndZ=0
    g1: Circle CenterX=0 CenterY=0 CenterZ=0 NormalX=0 NormalY=0 NormalZ=1 AngleXU=0 Radius=1
    g2: Circle CenterX=8 CenterY=6 CenterZ=0 NormalX=0 NormalY=0 NormalZ=1 AngleXU=0 Radius=1
    g3: BSplineCurve PolesCount=3 KnotsCount=2 Degree=2 IsPeriodic=0
    g4: GeomPoint X=0 Y=0 Z=0
    g5: GeomPoint X=8 Y=6 Z=0
    g6: LineSegment StartX=0 StartY=6 StartZ=0 EndX=8 EndY=6 EndZ=0
  constraints (14):
    c: Coincident(g0,g-1)
    c: Distance(g0) = 6
    c: Vertical(g0)
    c: Coincident(g3,g0)
    c: Weight(g1) = 1
    c: Equal(g1,g2)
    c: InternalAlignment(g1,g3)
    c: InternalAlignment(g2,g3)
    c: InternalAlignment(g4,g3)
    c: InternalAlignment(g5,g3)
    c: Block(g3)
    c: Coincident(g6,g0)
    c: Coincident(g6,g3)
    c: Horizontal(g6)
FEATURE [Part::Extrusion] Extrude013  label="caseScrewPillarBracket001"
  Base = -> Sketch019
  Dir = (0,0,1)
  DirMode = 2
  FaceMakerClass = Part::FaceMakerBullseye
  LengthFwd = 2.4
  LengthRev = 0
  Placement = pos=(15.76,29,60.8) rot=(0,0,1;0rad)
  Solid = true
  Symmetric = false
FEATURE [Sketcher::SketchObject] Sketch020
  FullyConstrained = true
  sketch-geometry (7):
    g0: LineSegment StartX=0 StartY=0 StartZ=0 EndX=0 EndY=6 EndZ=0
    g1: Circle CenterX=0 CenterY=0 CenterZ=0 NormalX=0 NormalY=0 NormalZ=1 AngleXU=0 Radius=1
    g2: Circle CenterX=8 CenterY=6 CenterZ=0 NormalX=0 NormalY=0 NormalZ=1 AngleXU=0 Radius=1
    g3: BSplineCurve PolesCount=3 KnotsCount=2 Degree=2 IsPeriodic=0
    g4: GeomPoint X=0 Y=0 Z=0
    g5: GeomPoint X=8 Y=6 Z=0
    g6: LineSegment StartX=0 StartY=6 StartZ=0 EndX=8 EndY=6 EndZ=0
  constraints (14):
    c: Coincident(g0,g-1)
    c: Distance(g0) = 6
    c: Vertical(g0)
    c: Coincident(g3,g0)
    c: Weight(g1) = 1
    c: Equal(g1,g2)
    c: InternalAlignment(g1,g3)
    c: InternalAlignment(g2,g3)
    c: InternalAlignment(g4,g3)
    c: InternalAlignment(g5,g3)
    c: Block(g3)
    c: Coincident(g6,g0)
    c: Coincident(g6,g3)
    c: Horizontal(g6)
FEATURE [Part::Extrusion] Extrude014  label="caseScrewPillarBracket002"
  Base = -> Sketch020
  Dir = (0,0,1)
  DirMode = 2
  FaceMakerClass = Part::FaceMakerBullseye
  LengthFwd = 2.4
  LengthRev = 0
  Placement = pos=(13.7,29,13.26) rot=(0,-1,0;1.5708rad)
  Solid = true
  Symmetric = false
FEATURE [Sketcher::SketchObject] Sketch021
  FullyConstrained = true
  sketch-geometry (7):
    g0: LineSegment StartX=0 StartY=0 StartZ=0 EndX=0 EndY=6 EndZ=0
    g1: Circle CenterX=0 CenterY=0 CenterZ=0 NormalX=0 NormalY=0 NormalZ=1 AngleXU=0 Radius=1
    g2: Circle CenterX=8 CenterY=6 CenterZ=0 NormalX=0 NormalY=0 NormalZ=1 AngleXU=0 Radius=1
    g3: BSplineCurve PolesCount=3 KnotsCount=2 Degree=2 IsPeriodic=0
    g4: GeomPoint X=0 Y=0 Z=0
    g5: GeomPoint X=8 Y=6 Z=0
    g6: LineSegment StartX=0 StartY=6 StartZ=0 EndX=8 EndY=6 EndZ=0
  constraints (14):
    c: Coincident(g0,g-1)
    c: Distance(g0) = 6
    c: Vertical(g0)
    c: Coincident(g3,g0)
    c: Weight(g1) = 1
    c: Equal(g1,g2)
    c: InternalAlignment(g1,g3)
    c: InternalAlignment(g2,g3)
    c: InternalAlignment(g4,g3)
    c: InternalAlignment(g5,g3)
    c: Block(g3)
    c: Coincident(g6,g0)
    c: Coincident(g6,g3)
    c: Horizontal(g6)
FEATURE [Part::Extrusion] Extrude015  label="caseScrewPillarBracket003"
  Base = -> Sketch021
  Dir = (0,0,1)
  DirMode = 2
  FaceMakerClass = Part::FaceMakerBullseye
  LengthFwd = 2.4
  LengthRev = 0
  Placement = pos=(11.3,29,58.74) rot=(0,1,0;1.5708rad)
  Solid = true
  Symmetric = false
FEATURE [Sketcher::SketchObject] Sketch022
  FullyConstrained = true
  sketch-geometry (7):
    g0: LineSegment StartX=0 StartY=0 StartZ=0 EndX=0 EndY=6 EndZ=0
    g1: Circle CenterX=0 CenterY=0 CenterZ=0 NormalX=0 NormalY=0 NormalZ=1 AngleXU=0 Radius=1
    g2: Circle CenterX=8 CenterY=6 CenterZ=0 NormalX=0 NormalY=0 NormalZ=1 AngleXU=0 Radius=1
    g3: BSplineCurve PolesCount=3 KnotsCount=2 Degree=2 IsPeriodic=0
    g4: GeomPoint X=0 Y=0 Z=0
    g5: GeomPoint X=8 Y=6 Z=0
    g6: LineSegment StartX=0 StartY=6 StartZ=0 EndX=8 EndY=6 EndZ=0
  constraints (14):
    c: Coincident(g0,g-1)
    c: Distance(g0) = 6
    c: Vertical(g0)
    c: Coincident(g3,g0)
    c: Weight(g1) = 1
    c: Equal(g1,g2)
    c: InternalAlignment(g1,g3)
    c: InternalAlignment(g2,g3)
    c: InternalAlignment(g4,g3)
    c: InternalAlignment(g5,g3)
    c: Block(g3)
    c: Coincident(g6,g0)
    c: Coincident(g6,g3)
    c: Horizontal(g6)
FEATURE [Part::Extrusion] Extrude016  label="caseScrewPillarBracket004"
  Base = -> Sketch022
  Dir = (0,0,1)
  DirMode = 2
  FaceMakerClass = Part::FaceMakerBullseye
  LengthFwd = 2.4
  LengthRev = 0
  Placement = pos=(88.3,29,65.23) rot=(0,1,0;1.5708rad)
  Solid = true
  Symmetric = false
FEATURE [Sketcher::SketchObject] Sketch023
  FullyConstrained = true
  sketch-geometry (7):
    g0: LineSegment StartX=0 StartY=0 StartZ=0 EndX=0 EndY=6 EndZ=0
    g1: Circle CenterX=0 CenterY=0 CenterZ=0 NormalX=0 NormalY=0 NormalZ=1 AngleXU=0 Radius=1
    g2: Circle CenterX=8 CenterY=6 CenterZ=0 NormalX=0 NormalY=0 NormalZ=1 AngleXU=0 Radius=1
    g3: BSplineCurve PolesCount=3 KnotsCount=2 Degree=2 IsPeriodic=0
    g4: GeomPoint X=0 Y=0 Z=0
    g5: GeomPoint X=8 Y=6 Z=0
    g6: LineSegment StartX=0 StartY=6 StartZ=0 EndX=8 EndY=6 EndZ=0
  constraints (14):
    c: Coincident(g0,g-1)
    c: Distance(g0) = 6
    c: Vertical(g0)
    c: Coincident(g3,g0)
    c: Weight(g1) = 1
    c: Equal(g1,g2)
    c: InternalAlignment(g1,g3)
    c: InternalAlignment(g2,g3)
    c: InternalAlignment(g4,g3)
    c: InternalAlignment(g5,g3)
    c: Block(g3)
    c: Coincident(g6,g0)
    c: Coincident(g6,g3)
    c: Horizontal(g6)
FEATURE [Part::Extrusion] Extrude017  label="caseScrewPillarBracket005"
  Base = -> Sketch023
  Dir = (0,0,1)
  DirMode = 2
  FaceMakerClass = Part::FaceMakerBullseye
  LengthFwd = 2.4
  LengthRev = 0
  Placement = pos=(90.7,29,6.77) rot=(0,-1,0;1.5708rad)
  Solid = true
  Symmetric = false
FEATURE [Sketcher::SketchObject] Sketch024
  FullyConstrained = true
  sketch-geometry (7):
    g0: LineSegment StartX=0 StartY=0 StartZ=0 EndX=0 EndY=6 EndZ=0
    g1: Circle CenterX=0 CenterY=0 CenterZ=0 NormalX=0 NormalY=0 NormalZ=1 AngleXU=0 Radius=1
    g2: Circle CenterX=8 CenterY=6 CenterZ=0 NormalX=0 NormalY=0 NormalZ=1 AngleXU=0 Radius=1
    g3: BSplineCurve PolesCount=3 KnotsCount=2 Degree=2 IsPeriodic=0
    g4: GeomPoint X=0 Y=0 Z=0
    g5: GeomPoint X=8 Y=6 Z=0
    g6: LineSegment StartX=0 StartY=6 StartZ=0 EndX=8 EndY=6 EndZ=0
  constraints (14):
    c: Coincident(g0,g-1)
    c: Distance(g0) = 6
    c: Vertical(g0)
    c: Coincident(g3,g0)
    c: Weight(g1) = 1
    c: Equal(g1,g2)
    c: InternalAlignment(g1,g3)
    c: InternalAlignment(g2,g3)
    c: InternalAlignment(g4,g3)
    c: InternalAlignment(g5,g3)
    c: Block(g3)
    c: Coincident(g6,g0)
    c: Coincident(g6,g3)
    c: Horizontal(g6)
FEATURE [Part::Extrusion] Extrude018  label="caseScrewPillarBracket006"
  Base = -> Sketch024
  Dir = (0,0,1)
  DirMode = 2
  FaceMakerClass = Part::FaceMakerBullseye
  LengthFwd = 2.4
  LengthRev = 0
  Placement = pos=(103.7,29,6.77) rot=(0,-1,0;1.5708rad)
  Solid = true
  Symmetric = false
FEATURE [Sketcher::SketchObject] Sketch025
  FullyConstrained = true
  sketch-geometry (7):
    g0: LineSegment StartX=0 StartY=0 StartZ=0 EndX=0 EndY=6 EndZ=0
    g1: Circle CenterX=0 CenterY=0 CenterZ=0 NormalX=0 NormalY=0 NormalZ=1 AngleXU=0 Radius=1
    g2: Circle CenterX=8 CenterY=6 CenterZ=0 NormalX=0 NormalY=0 NormalZ=1 AngleXU=0 Radius=1
    g3: BSplineCurve PolesCount=3 KnotsCount=2 Degree=2 IsPeriodic=0
    g4: GeomPoint X=0 Y=0 Z=0
    g5: GeomPoint X=8 Y=6 Z=0
    g6: LineSegment StartX=0 StartY=6 StartZ=0 EndX=8 EndY=6 EndZ=0
  constraints (14):
    c: Coincident(g0,g-1)
    c: Distance(g0) = 6
    c: Vertical(g0)
    c: Coincident(g3,g0)
    c: Weight(g1) = 1
    c: Equal(g1,g2)
    c: InternalAlignment(g1,g3)
    c: InternalAlignment(g2,g3)
    c: InternalAlignment(g4,g3)
    c: InternalAlignment(g5,g3)
    c: Block(g3)
    c: Coincident(g6,g0)
    c: Coincident(g6,g3)
    c: Horizontal(g6)
FEATURE [Part::Extrusion] Extrude019  label="caseScrewPillarBracket007"
  Base = -> Sketch025
  Dir = (0,0,1)
  DirMode = 2
  FaceMakerClass = Part::FaceMakerBullseye
  LengthFwd = 2.4
  LengthRev = 0
  Placement = pos=(101.3,29,65.23) rot=(0,1,0;1.5708rad)
  Solid = true
  Symmetric = false
FEATURE [Part::Box] Box011  label="frontCaseScrewPillarBracket"
  AttacherType = Attacher::AttachEngine3D
  Height = 2.4
  Length = 16
  Placement = pos=(87,28,2.3) rot=(0,0,1;0rad)
  Width = 7
FEATURE [Part::Box] Box012  label="frontCaseScrewPillarBracket001"
  AttacherType = Attacher::AttachEngine3D
  Height = 2.4
  Length = 16
  Placement = pos=(87,28,67.3) rot=(0,0,1;0rad)
  Width = 7
FEATURE [Sketcher::SketchObject] Sketch026
  FullyConstrained = true
  sketch-geometry (17):
    g0: Circle CenterX=-3.5 CenterY=23.5 CenterZ=0 NormalX=0 NormalY=0 NormalZ=1 AngleXU=0 Radius=1
    g1: Circle CenterX=-1 CenterY=15.25 CenterZ=0 NormalX=0 NormalY=0 NormalZ=1 AngleXU=0 Radius=1
    g2: Circle CenterX=-3.5 CenterY=7 CenterZ=0 NormalX=0 NormalY=0 NormalZ=1 AngleXU=0 Radius=1
    g3: BSplineCurve PolesCount=3 KnotsCount=2 Degree=2 IsPeriodic=0
    g4: GeomPoint X=-3.5 Y=23.5 Z=0
    g5: GeomPoint X=-3.5 Y=7 Z=0
    g6: Circle CenterX=-4.8 CenterY=30.5 CenterZ=0 NormalX=0 NormalY=0 NormalZ=1 AngleXU=0 Radius=1
    g7: Circle CenterX=-3.5 CenterY=30.5 CenterZ=0 NormalX=0 NormalY=0 NormalZ=1 AngleXU=0 Radius=1
    g8: Circle CenterX=-3.5 CenterY=29.2 CenterZ=0 NormalX=0 NormalY=0 NormalZ=1 AngleXU=0 Radius=1
    g9: BSplineCurve PolesCount=3 KnotsCount=2 Degree=2 IsPeriodic=0
    g10: GeomPoint X=-4.8 Y=30.5 Z=0
    g11: GeomPoint X=-3.5 Y=29.2 Z=0
    g12: LineSegment StartX=-3.5 StartY=29.2 StartZ=0 EndX=-3.5 EndY=23.5 EndZ=0
    g13: LineSegment StartX=-4.8 StartY=30.5 StartZ=0 EndX=0 EndY=30.5 EndZ=0
    g14: LineSegment StartX=-3.5 StartY=5 StartZ=0 EndX=-3.5 EndY=7 EndZ=0
    g15: LineSegment StartX=0 StartY=5 StartZ=0 EndX=0 EndY=30.5 EndZ=0
    g16: LineSegment StartX=-3.5 StartY=5 StartZ=0 EndX=0 EndY=5 EndZ=0
  constraints (33):
    c: Weight(g0) = 1
    c: Equal(g0,g1)
    c: Equal(g0,g2)
    c: InternalAlignment(g0,g3)
    c: InternalAlignment(g1,g3)
    c: InternalAlignment(g2,g3)
    c: InternalAlignment(g4,g3)
    c: InternalAlignment(g5,g3)
    c: Block(g3)
    c: Weight(g6) = 1
    c: Equal(g6,g7)
    c: Equal(g6,g8)
    c: InternalAlignment(g6,g9)
    c: InternalAlignment(g7,g9)
    c: InternalAlignment(g8,g9)
    c: InternalAlignment(g10,g9)
    c: InternalAlignment(g11,g9)
    c: Block(g9)
    c: Coincident(g12,g9)
    c: Coincident(g12,g3)
    c: Vertical(g12)
    c: Coincident(g13,g9)
    c: Horizontal(g13)
    c: Distance(g13) = 4.8
    c: Coincident(g14,g3)
    c: Vertical(g14)
    c: Coincident(g15,g13)
    c: Vertical(g15)
    c: Tangent(g15,g1)
    c: Distance(g14) = 2
    c: Coincident(g16,g14)
    c: Horizontal(g16)
    c: Coincident(g15,g16)
FEATURE [Part::Feature] Face050
  shape: bbox 4.8 x 25.5 x 2e-07 mm, 1 faces, 0 solids (baked)
FEATURE [Part::Revolution] Revolve054  label="moreFrontCaseScrewPost001"
  Angle = 360
  Axis = (0,1,0)
  Base = (0,0,0)
  FaceMakerClass = Part::FaceMakerBullseye
  Placement = pos=(102.5,4.5,3.5) rot=(0,0,1;0rad)
  Solid = false
  Source = -> Face050
  Symmetric = false
FEATURE [Part::Feature] Face051
  shape: bbox 4.8 x 25.5 x 2e-07 mm, 1 faces, 0 solids (baked)
FEATURE [Part::Revolution] Revolve055  label="moreFrontCaseScrewPost002"
  Angle = 360
  Axis = (0,1,0)
  Base = (0,0,0)
  FaceMakerClass = Part::FaceMakerBullseye
  Placement = pos=(102.5,4.5,68.5) rot=(0,0,1;0rad)
  Solid = false
  Source = -> Face051
  Symmetric = false
FEATURE [Sketcher::SketchObject] Sketch027
  FullyConstrained = true
  sketch-geometry (10):
    g0: LineSegment StartX=-1.6 StartY=4.7 StartZ=0 EndX=-1.6 EndY=1.7 EndZ=0
    g1: LineSegment StartX=-3.5 StartY=4.7 StartZ=0 EndX=-1.6 EndY=4.7 EndZ=0
    g2: LineSegment StartX=-1.6 StartY=1.7 StartZ=0 EndX=-1.6 EndY=1.5 EndZ=0
    g3: LineSegment StartX=-1.6 StartY=1.5 StartZ=0 EndX=-5.2 EndY=1.5 EndZ=0
    g4: Circle CenterX=-3.5 CenterY=4.7 CenterZ=0 NormalX=0 NormalY=0 NormalZ=1 AngleXU=0 Radius=1
    g5: Circle CenterX=-3.59627 CenterY=2.99743 CenterZ=0 NormalX=0 NormalY=0 NormalZ=1 AngleXU=0 Radius=1
    g6: Circle CenterX=-5.2 CenterY=1.5 CenterZ=0 NormalX=0 NormalY=0 NormalZ=1 AngleXU=0 Radius=1
    g7: BSplineCurve PolesCount=3 KnotsCount=2 Degree=2 IsPeriodic=0
    g8: GeomPoint X=-3.5 Y=4.7 Z=0
    g9: GeomPoint X=-5.2 Y=1.5 Z=0
  constraints (23):
    c: Vertical(g0)
    c: Distance(g0) = 3
    c: Coincident(g1,g0)
    c: Horizontal(g1)
    c: Block(g0)
    c: Block(g1)
    c: Coincident(g2,g0)
    c: Vertical(g2)
    c: Distance(g2) = 0.2
    c: Coincident(g3,g2)
    c: Horizontal(g3)
    c: Block(g3)
    c: Coincident(g7,g1)
    c: Weight(g4) = 1
    c: Equal(g4,g5)
    c: Equal(g4,g6)
    c: Coincident(g7,g3)
    c: InternalAlignment(g4,g7)
    c: InternalAlignment(g5,g7)
    c: InternalAlignment(g6,g7)
    c: InternalAlignment(g8,g7)
    c: InternalAlignment(g9,g7)
    c: Block(g7)
FEATURE [Sketcher::SketchObject] Sketch028
  FullyConstrained = true
  sketch-geometry (18):
    g0: LineSegment StartX=0 StartY=3e-16 StartZ=0 EndX=0 EndY=1.7 EndZ=0
    g1: LineSegment StartX=-3.5 StartY=0 StartZ=0 EndX=-3.5 EndY=0.9 EndZ=0
    g2: Circle CenterX=-2.7 CenterY=1.7 CenterZ=0 NormalX=0 NormalY=0 NormalZ=1 AngleXU=0 Radius=1
    g3: Circle CenterX=-3.5 CenterY=1.7 CenterZ=0 NormalX=0 NormalY=0 NormalZ=1 AngleXU=0 Radius=1
    g4: Circle CenterX=-3.5 CenterY=0.9 CenterZ=0 NormalX=0 NormalY=0 NormalZ=1 AngleXU=0 Radius=1
    g5: BSplineCurve PolesCount=3 KnotsCount=2 Degree=2 IsPeriodic=0
    g6: GeomPoint X=-2.7 Y=1.7 Z=0
    g7: GeomPoint X=-3.5 Y=0.9 Z=0
    g8: LineSegment StartX=-3.5 StartY=0 StartZ=0 EndX=-3.5 EndY=-7 EndZ=0
    g9: LineSegment StartX=0 StartY=3e-16 StartZ=0 EndX=0 EndY=-7 EndZ=0
    g10: LineSegment StartX=-3.5 StartY=-7 StartZ=0 EndX=0 EndY=-7 EndZ=0
    g11: LineSegment StartX=-2.7 StartY=1.7 StartZ=0 EndX=-1.6 EndY=1.7 EndZ=0
    g12: LineSegment StartX=0 StartY=1.7 StartZ=0 EndX=0 EndY=4.5 EndZ=0
    g13: LineSegment StartX=0 StartY=4.5 StartZ=0 EndX=0 EndY=10.8 EndZ=0
    g14: LineSegment StartX=0 StartY=10.8 StartZ=0 EndX=-2 EndY=10.8 EndZ=0
    g15: LineSegment StartX=-1.6 StartY=4.7 StartZ=0 EndX=-1.6 EndY=1.7 EndZ=0
    g16: LineSegment StartX=-1.6 StartY=4.7 StartZ=0 EndX=-2 EndY=4.7 EndZ=0
    g17: LineSegment StartX=-2 StartY=4.7 StartZ=0 EndX=-2 EndY=10.8 EndZ=0
  constraints (44):
    c: Vertical(g0)
    c: Vertical(g1)
    c: Distance(g1) = 0.9
    c: Block(g0)
    c: Distance(g0) = 1.7
    c: Weight(g2) = 1
    c: Equal(g2,g3)
    c: Equal(g2,g4)
    c: Coincident(g5,g1)
    c: InternalAlignment(g2,g5)
    c: InternalAlignment(g3,g5)
    c: InternalAlignment(g4,g5)
    c: InternalAlignment(g6,g5)
    c: InternalAlignment(g7,g5)
    c: Block(g5)
    c: Coincident(g8,g1)
    c: Vertical(g8)
    c: Distance(g8) = 7
    c: Vertical(g9)
    c: Equal(g8,g9) = 7
    c: Coincident(g9,g0)
    c: Coincident(g10,g8)
    c: Coincident(g10,g9)
    c: Horizontal(g10)
    c: Coincident(g11,g5)
    c: Horizontal(g11)
    c: Coincident(g12,g0)
    c: Vertical(g12)
    c: Distance(g12) = 2.8
    c: Coincident(g13,g12)
    c: Vertical(g13)
    c: Distance(g13) = 6.3
    c: Coincident(g14,g13)
    c: Horizontal(g14)
    c: Distance(g14) = 2
    c: Vertical(g15)
    c: Distance(g15) = 3
    c: Block(g11)
    c: Coincident(g15,g11)
    c: Coincident(g16,g15)
    c: Horizontal(g16)
    c: Coincident(g17,g16)
    c: Coincident(g17,g14)
    c: Vertical(g17)
FEATURE [Part::Revolution] Revolve040  label="backCaseScrewRetainer001"
  Angle = 360
  Axis = (0,1,0)
  Base = (0,0,0)
  FaceMakerClass = Part::FaceMakerBullseye
  Placement = pos=(12.5,3,10) rot=(0,0,1;0rad)
  Solid = false
  Source = -> Face036
  Symmetric = false
FEATURE [Part::Feature] Face055
  shape: bbox 3.5 x 30.2 x 2e-07 mm, 1 faces, 0 solids (baked)
FEATURE [Part::Revolution] Revolve059  label="backCaseScrewPost"
  Angle = 360
  Axis = (0,1,0)
  Base = (0,0,0)
  FaceMakerClass = Part::FaceMakerBullseye
  Placement = pos=(12.5,4.5,10) rot=(0,0,1;0rad)
  Solid = false
  Source = -> Face055
  Symmetric = false
FEATURE [Part::Feature] Face056
  shape: bbox 3.5 x 30.2 x 2e-07 mm, 1 faces, 0 solids (baked)
FEATURE [Part::Revolution] Revolve060  label="backCaseScrewPost001"
  Angle = 360
  Axis = (0,1,0)
  Base = (0,0,0)
  FaceMakerClass = Part::FaceMakerBullseye
  Placement = pos=(12.5,4.5,62) rot=(0,0,1;0rad)
  Solid = false
  Source = -> Face056
  Symmetric = false
FEATURE [Part::Feature] Face057
  shape: bbox 3.5 x 17.8 x 2e-07 mm, 1 faces, 0 solids (baked)
FEATURE [Part::Revolution] Revolve061  label="removeToCreateScrewAndThreadedInsertHole"
  Angle = 360
  Axis = (0,1,0)
  Base = (0,0,0)
  FaceMakerClass = Part::FaceMakerBullseye
  Placement = pos=(12.5,0,10) rot=(0,0,1;0rad)
  Solid = false
  Source = -> Face057
  Symmetric = false
FEATURE [Part::Feature] Face058
  shape: bbox 3.5 x 17.8 x 2e-07 mm, 1 faces, 0 solids (baked)
FEATURE [Part::Revolution] Revolve062  label="removeToCreateScrewAndThreadedInsertHole001"
  Angle = 360
  Axis = (0,1,0)
  Base = (0,0,0)
  FaceMakerClass = Part::FaceMakerBullseye
  Placement = pos=(12.5,0,62) rot=(0,0,1;0rad)
  Solid = false
  Source = -> Face058
  Symmetric = false
FEATURE [Part::Feature] Face059
  shape: bbox 3.5 x 17.8 x 2e-07 mm, 1 faces, 0 solids (baked)
FEATURE [Part::Revolution] Revolve063  label="removeToCreateScrewAndThreadedInsertHole002"
  Angle = 360
  Axis = (0,1,0)
  Base = (0,0,0)
  FaceMakerClass = Part::FaceMakerBullseye
  Placement = pos=(89.5,0,68.5) rot=(0,0,1;0rad)
  Solid = false
  Source = -> Face059
  Symmetric = false
FEATURE [Part::Feature] Face060
  shape: bbox 3.5 x 17.8 x 2e-07 mm, 1 faces, 0 solids (baked)
FEATURE [Part::Revolution] Revolve064  label="removeToCreateScrewAndThreadedInsertHole003"
  Angle = 360
  Axis = (0,1,0)
  Base = (0,0,0)
  FaceMakerClass = Part::FaceMakerBullseye
  Placement = pos=(89.5,0,3.5) rot=(0,0,1;0rad)
  Solid = false
  Source = -> Face060
  Symmetric = false
FEATURE [Part::Feature] Face061
  shape: bbox 3.5 x 17.8 x 2e-07 mm, 1 faces, 0 solids (baked)
FEATURE [Part::Revolution] Revolve065  label="removeToCreateScrewAndThreadedInsertHole004"
  Angle = 360
  Axis = (0,1,0)
  Base = (0,0,0)
  FaceMakerClass = Part::FaceMakerBullseye
  Placement = pos=(102.5,4.7,3.5) rot=(0,0,1;0rad)
  Solid = false
  Source = -> Face061
  Symmetric = false
FEATURE [Part::Feature] Face062
  shape: bbox 3.5 x 17.8 x 2e-07 mm, 1 faces, 0 solids (baked)
FEATURE [Part::Revolution] Revolve066  label="removeToCreateScrewAndThreadedInsertHole005"
  Angle = 360
  Axis = (0,1,0)
  Base = (0,0,0)
  FaceMakerClass = Part::FaceMakerBullseye
  Placement = pos=(102.5,4.7,68.5) rot=(0,0,1;0rad)
  Solid = false
  Source = -> Face062
  Symmetric = false
FEATURE [Part::MultiFuse] Fusion047  label="makeHoles"
  Shapes = -> [Revolve066,Revolve065,Revolve064,Revolve063,Revolve062,Revolve061]
FEATURE [Part::Feature] Face063
  shape: bbox 3.6 x 3.2 x 2e-07 mm, 1 faces, 0 solids (baked)
FEATURE [Part::Revolution] Revolve067  label="moreFrontCaseScrewRetainer002"
  Angle = 360
  Axis = (0,1,0)
  Base = (0,0,0)
  FaceMakerClass = Part::FaceMakerBullseye
  Placement = pos=(102.5,4.5,68.5) rot=(0,0,1;0rad)
  Solid = false
  Source = -> Face063
  Symmetric = false
FEATURE [Part::Feature] Face064
  shape: bbox 3.6 x 3.2 x 2e-07 mm, 1 faces, 0 solids (baked)
FEATURE [Part::Revolution] Revolve068  label="moreFrontCaseScrewRetainer003"
  Angle = 360
  Axis = (0,1,0)
  Base = (0,0,0)
  FaceMakerClass = Part::FaceMakerBullseye
  Placement = pos=(102.5,4.5,3.5) rot=(0,0,1;0rad)
  Solid = false
  Source = -> Face064
  Symmetric = false
FEATURE [Part::Feature] Face065
  shape: bbox 3.5 x 17.8 x 2e-07 mm, 1 faces, 0 solids (baked)
FEATURE [Part::Revolution] Revolve069  label="removeToCreateScrewAndThreadedInsertHole006"
  Angle = 360
  Axis = (0,1,0)
  Base = (0,0,0)
  FaceMakerClass = Part::FaceMakerBullseye
  Placement = pos=(12.5,0,10) rot=(0,0,1;0rad)
  Solid = false
  Source = -> Face065
  Symmetric = false
FEATURE [Part::Feature] Face066
  shape: bbox 3.5 x 17.8 x 2e-07 mm, 1 faces, 0 solids (baked)
FEATURE [Part::Revolution] Revolve070  label="removeToCreateScrewAndThreadedInsertHole007"
  Angle = 360
  Axis = (0,1,0)
  Base = (0,0,0)
  FaceMakerClass = Part::FaceMakerBullseye
  Placement = pos=(12.5,0,62) rot=(0,0,1;0rad)
  Solid = false
  Source = -> Face066
  Symmetric = false
FEATURE [Part::Feature] Face067
  shape: bbox 3.5 x 17.8 x 2e-07 mm, 1 faces, 0 solids (baked)
FEATURE [Part::Revolution] Revolve071  label="removeToCreateScrewAndThreadedInsertHole008"
  Angle = 360
  Axis = (0,1,0)
  Base = (0,0,0)
  FaceMakerClass = Part::FaceMakerBullseye
  Placement = pos=(89.5,0,68.5) rot=(0,0,1;0rad)
  Solid = false
  Source = -> Face067
  Symmetric = false
FEATURE [Part::Feature] Face068
  shape: bbox 3.5 x 17.8 x 2e-07 mm, 1 faces, 0 solids (baked)
FEATURE [Part::Revolution] Revolve072  label="removeToCreateScrewAndThreadedInsertHole009"
  Angle = 360
  Axis = (0,1,0)
  Base = (0,0,0)
  FaceMakerClass = Part::FaceMakerBullseye
  Placement = pos=(89.5,0,3.5) rot=(0,0,1;0rad)
  Solid = false
  Source = -> Face068
  Symmetric = false
FEATURE [Part::Feature] Face069
  shape: bbox 3.5 x 17.8 x 2e-07 mm, 1 faces, 0 solids (baked)
FEATURE [Part::Feature] Face070
  shape: bbox 3.5 x 17.8 x 2e-07 mm, 1 faces, 0 solids (baked)
FEATURE [Part::Revolution] Revolve073  label="removeToCreateScrewAndThreadedInsertHole010"
  Angle = 360
  Axis = (0,1,0)
  Base = (0,0,0)
  FaceMakerClass = Part::FaceMakerBullseye
  Placement = pos=(102.5,4.7,3.5) rot=(0,0,1;0rad)
  Solid = false
  Source = -> Face069
  Symmetric = false
FEATURE [Part::Revolution] Revolve074  label="removeToCreateScrewAndThreadedInsertHole011"
  Angle = 360
  Axis = (0,1,0)
  Base = (0,0,0)
  FaceMakerClass = Part::FaceMakerBullseye
  Placement = pos=(102.5,4.7,68.5) rot=(0,0,1;0rad)
  Solid = false
  Source = -> Face070
  Symmetric = false
FEATURE [Part::MultiFuse] Fusion048  label="makeHoles001"
  Shapes = -> [Revolve074,Revolve073,Revolve072,Revolve071,Revolve070,Revolve069]
FEATURE [Part::MultiFuse] Fusion049  label="caseScrewRetainers"
  Shapes = -> [Revolve067,Revolve068,Revolve048,Revolve047,Revolve039,Revolve040]
FEATURE [Part::Cut] Cut015  label="caseScrewRetainers001"
  Base = -> Fusion049
  Tool = -> Fusion048
FEATURE [Part::MultiFuse] Fusion050  label="casePillars"
  Shapes = -> [Revolve055,Revolve054,Revolve043,Revolve046,Revolve059,Revolve060]
FEATURE [Part::Feature] Face071 .. Face076  x6 (patterned run collapsed; names and placements below)
  shape: bbox 3.5 x 17.8 x 2e-07 mm, 1 faces, 0 solids (baked)
FEATURE [Part::Revolution] Revolve075  label="removeToCreateScrewAndThreadedInsertHole012"
  Angle = 360
  Axis = (0,1,0)
  Base = (0,0,0)
  FaceMakerClass = Part::FaceMakerBullseye
  Placement = pos=(12.5,0,10) rot=(0,0,1;0rad)
  Solid = false
  Source = -> Face071
  Symmetric = false
FEATURE [Part::Revolution] Revolve076  label="removeToCreateScrewAndThreadedInsertHole013"
  Angle = 360
  Axis = (0,1,0)
  Base = (0,0,0)
  FaceMakerClass = Part::FaceMakerBullseye
  Placement = pos=(12.5,0,62) rot=(0,0,1;0rad)
  Solid = false
  Source = -> Face072
  Symmetric = false
FEATURE [Part::Revolution] Revolve077  label="removeToCreateScrewAndThreadedInsertHole014"
  Angle = 360
  Axis = (0,1,0)
  Base = (0,0,0)
  FaceMakerClass = Part::FaceMakerBullseye
  Placement = pos=(89.5,0,68.5) rot=(0,0,1;0rad)
  Solid = false
  Source = -> Face073
  Symmetric = false
FEATURE [Part::Revolution] Revolve078  label="removeToCreateScrewAndThreadedInsertHole015"
  Angle = 360
  Axis = (0,1,0)
  Base = (0,0,0)
  FaceMakerClass = Part::FaceMakerBullseye
  Placement = pos=(89.5,0,3.5) rot=(0,0,1;0rad)
  Solid = false
  Source = -> Face074
  Symmetric = false
FEATURE [Part::Revolution] Revolve079  label="removeToCreateScrewAndThreadedInsertHole016"
  Angle = 360
  Axis = (0,1,0)
  Base = (0,0,0)
  FaceMakerClass = Part::FaceMakerBullseye
  Placement = pos=(102.5,4.7,3.5) rot=(0,0,1;0rad)
  Solid = false
  Source = -> Face075
  Symmetric = false
FEATURE [Part::Revolution] Revolve080  label="removeToCreateScrewAndThreadedInsertHole017"
  Angle = 360
  Axis = (0,1,0)
  Base = (0,0,0)
  FaceMakerClass = Part::FaceMakerBullseye
  Placement = pos=(102.5,4.7,68.5) rot=(0,0,1;0rad)
  Solid = false
  Source = -> Face076
  Symmetric = false
FEATURE [Part::MultiFuse] Fusion051  label="makeHoles002"
  Shapes = -> [Revolve080,Revolve079,Revolve078,Revolve077,Revolve076,Revolve075]
FEATURE [Part::Cut] Cut016  label="caesPillars"
  Base = -> Fusion050
  Tool = -> Fusion051
FEATURE [Part::Revolution] Revolve009  label="plugHousing016"
  Angle = 360
  Axis = (0,1,0)
  Base = (0,0,0)
  FaceMakerClass = Part::FaceMakerBullseye
  Placement = pos=(0,0,36.15) rot=(0,0,1;0rad)
  Solid = false
  Source = -> Face012
  Symmetric = false
FEATURE [Part::MultiFuse] Fusion014  label="plugHousing023"
  Placement = pos=(0,0,0) rot=(0,0,1;1.5708rad)
  Shapes = -> [Revolve011,Revolve009]
FEATURE [Part::Revolution] Revolve010  label="plugHousing017"
  Angle = 360
  Axis = (0,1,0)
  Base = (0,0,0)
  FaceMakerClass = Part::FaceMakerBullseye
  Placement = pos=(0,0,36.15) rot=(0,0,1;0rad)
  Solid = false
  Source = -> Face014
  Symmetric = false
FEATURE [Part::MultiFuse] Fusion015  label="plugHousing024"
  Placement = pos=(0,0,0) rot=(0,0,1;1.5708rad)
  Shapes = -> [Revolve010,Revolve015]
FEATURE [Part::Revolution] Revolve014  label="plugHousing026"
  Angle = 360
  Axis = (0,1,0)
  Base = (0,0,0)
  FaceMakerClass = Part::FaceMakerBullseye
  Placement = pos=(0,0,36.15) rot=(0,0,1;0rad)
  Solid = false
  Source = -> Face011
  Symmetric = false
FEATURE [Part::Revolution] Revolve013  label="plugHousing025"
  Angle = 360
  Axis = (0,1,0)
  Base = (0,0,0)
  FaceMakerClass = Part::FaceMakerBullseye
  Placement = pos=(0,0,36.15) rot=(0,0,1;0rad)
  Solid = false
  Source = -> Face015
  Symmetric = false
FEATURE [Part::MultiFuse] Fusion016  label="plugHousing028"
  Placement = pos=(0,19,0) rot=(0,0,1;3.14159rad)
  Shapes = -> [Fusion014,Fusion013]
FEATURE [Part::MultiFuse] Fusion011  label="plugHousing018"
  Placement = pos=(0,0,0) rot=(0,0,1;1.5708rad)
  Shapes = -> [Revolve014,Revolve013]
FEATURE [Part::MultiFuse] Fusion012  label="plugHousing019"
  Placement = pos=(0,19,0) rot=(0,0,1;3.14159rad)
  Shapes = -> [Fusion011,Fusion015]
FEATURE [Part::MultiFuse] Fusion017  label="plugHousing029"
  Placement = pos=(122.621,0,-0.15) rot=(0,0,1;0rad)
  Shapes = -> [Fusion016,Fusion012]
FEATURE [Part::MultiFuse] Fusion052  label="casePillarRetainers"
  Shapes = -> [Extrude012,Extrude013,Extrude014,Extrude015,Extrude016,Extrude017,Extrude018,Extrude019,Box011,Box012]
FEATURE [Part::Feature] Face077
  shape: bbox 3.5 x 17.8 x 2e-07 mm, 1 faces, 0 solids (baked)
FEATURE [Part::Revolution] Revolve081  label="removeToCreateScrewAndThreadedInsertHole018"
  Angle = 360
  Axis = (0,1,0)
  Base = (0,0,0)
  FaceMakerClass = Part::FaceMakerBullseye
  Placement = pos=(62.3,30.3,19.7) rot=(0,0,1;0rad)
  Solid = false
  Source = -> Face077
  Symmetric = false
FEATURE [Part::Feature] Face078
  shape: bbox 3.5 x 17.8 x 2e-07 mm, 1 faces, 0 solids (baked)
FEATURE [Part::Revolution] Revolve082  label="removeToCreateScrewAndThreadedInsertHole019"
  Angle = 360
  Axis = (0,1,0)
  Base = (0,0,0)
  FaceMakerClass = Part::FaceMakerBullseye
  Placement = pos=(62.3,30.3,51.7) rot=(0,0,1;0rad)
  Solid = false
  Source = -> Face078
  Symmetric = false
FEATURE [Part::Feature] Face079
  shape: bbox 3.5 x 17.8 x 2e-07 mm, 1 faces, 0 solids (baked)
FEATURE [Part::Revolution] Revolve083  label="removeToCreateScrewAndThreadedInsertHole020"
  Angle = 360
  Axis = (0,1,0)
  Base = (0,0,0)
  FaceMakerClass = Part::FaceMakerBullseye
  Placement = pos=(30.3,30.3,19.7) rot=(0,0,1;0rad)
  Solid = false
  Source = -> Face079
  Symmetric = false
FEATURE [Part::Feature] Face080
  shape: bbox 3.5 x 17.8 x 2e-07 mm, 1 faces, 0 solids (baked)
FEATURE [Part::Revolution] Revolve084  label="removeToCreateScrewAndThreadedInsertHole021"
  Angle = 360
  Axis = (0,1,0)
  Base = (0,0,0)
  FaceMakerClass = Part::FaceMakerBullseye
  Placement = pos=(30.3,30.3,51.7) rot=(0,0,1;0rad)
  Solid = false
  Source = -> Face080
  Symmetric = false
FEATURE [Part::MultiFuse] Fusion053  label="createThreadedInsertHolesForFan"
  Shapes = -> [Revolve081,Revolve082,Revolve083,Revolve084]
FEATURE [Part::Cut] Cut017  label="fanScrewHousing001"
  Base = -> Fusion046
  Tool = -> Fusion053
FEATURE [Part::Feature] Face081
  shape: bbox 3.5 x 17.8 x 2e-07 mm, 1 faces, 0 solids (baked)
FEATURE [Part::Revolution] Revolve085  label="removeToCreateScrewAndThreadedInsertHole022"
  Angle = 360
  Axis = (0,1,0)
  Base = (0,0,0)
  FaceMakerClass = Part::FaceMakerBullseye
  Placement = pos=(62.3,30.3,19.7) rot=(0,0,1;0rad)
  Solid = false
  Source = -> Face081
  Symmetric = false
FEATURE [Part::Feature] Face082
  shape: bbox 3.5 x 17.8 x 2e-07 mm, 1 faces, 0 solids (baked)
FEATURE [Part::Revolution] Revolve086  label="removeToCreateScrewAndThreadedInsertHole023"
  Angle = 360
  Axis = (0,1,0)
  Base = (0,0,0)
  FaceMakerClass = Part::FaceMakerBullseye
  Placement = pos=(62.3,30.3,51.7) rot=(0,0,1;0rad)
  Solid = false
  Source = -> Face082
  Symmetric = false
FEATURE [Part::Feature] Face083
  shape: bbox 3.5 x 17.8 x 2e-07 mm, 1 faces, 0 solids (baked)
FEATURE [Part::Revolution] Revolve087  label="removeToCreateScrewAndThreadedInsertHole024"
  Angle = 360
  Axis = (0,1,0)
  Base = (0,0,0)
  FaceMakerClass = Part::FaceMakerBullseye
  Placement = pos=(30.3,30.3,19.7) rot=(0,0,1;0rad)
  Solid = false
  Source = -> Face083
  Symmetric = false
FEATURE [Part::Feature] Face084
  shape: bbox 3.5 x 17.8 x 2e-07 mm, 1 faces, 0 solids (baked)
FEATURE [Part::Revolution] Revolve088  label="removeToCreateScrewAndThreadedInsertHole025"
  Angle = 360
  Axis = (0,1,0)
  Base = (0,0,0)
  FaceMakerClass = Part::FaceMakerBullseye
  Placement = pos=(30.3,30.3,51.7) rot=(0,0,1;0rad)
  Solid = false
  Source = -> Face084
  Symmetric = false
FEATURE [Part::MultiFuse] Fusion054  label="createThreadedInsertHolesForFan001"
  Shapes = -> [Revolve085,Revolve086,Revolve087,Revolve088]
FEATURE [Part::Cut] Cut018  label="top007"
  Base = -> Fusion040
  Tool = -> Fusion054
FEATURE [Sketcher::SketchObject] Sketch029
  FullyConstrained = false
  Placement = pos=(0,0,0) rot=(1,0,0;1.5708rad)
  sketch-geometry (24):
    g0: ArcOfCircle CenterX=-4 CenterY=-10.5 CenterZ=0 NormalX=0 NormalY=0 NormalZ=1 AngleXU=0 Radius=1.5 StartAngle=6e-16 EndAngle=3.14159
    g1: ArcOfCircle CenterX=-34.2 CenterY=-10.5 CenterZ=0 NormalX=0 NormalY=0 NormalZ=1 AngleXU=0 Radius=1.5 StartAngle=0 EndAngle=3.14159
    g2: ArcOfCircle CenterX=-34.2 CenterY=-27.7 CenterZ=0 NormalX=0 NormalY=0 NormalZ=1 AngleXU=0 Radius=1.5 StartAngle=3.14159 EndAngle=6.28319
    g3: ArcOfCircle CenterX=-4 CenterY=-27.7 CenterZ=0 NormalX=0 NormalY=0 NormalZ=1 AngleXU=0 Radius=1.5 StartAngle=3.1416 EndAngle=6.28319
    g4: ArcOfCircle CenterX=-10 CenterY=-4.3 CenterZ=0 NormalX=0 NormalY=0 NormalZ=1 AngleXU=0 Radius=1.5 StartAngle=2e-16 EndAngle=3.14159
    g5: ArcOfCircle CenterX=-16.1 CenterY=-1.8 CenterZ=0 NormalX=0 NormalY=0 NormalZ=1 AngleXU=0 Radius=1.5 StartAngle=5e-16 EndAngle=3.14159
    g6: ArcOfCircle CenterX=-22.1 CenterY=-1.8 CenterZ=0 NormalX=0 NormalY=0 NormalZ=1 AngleXU=0 Radius=1.5 StartAngle=5e-16 EndAngle=3.14159
    g7: ArcOfCircle CenterX=-28.2 CenterY=-4.3 CenterZ=0 NormalX=0 NormalY=0 NormalZ=1 AngleXU=0 Radius=1.5 StartAngle=2e-16 EndAngle=3.14159
    g8: ArcOfCircle CenterX=-10 CenterY=-33.9 CenterZ=0 NormalX=0 NormalY=0 NormalZ=1 AngleXU=0 Radius=1.5 StartAngle=3.14159 EndAngle=6.28319
    g9: ArcOfCircle CenterX=-16.1 CenterY=-36.4 CenterZ=0 NormalX=0 NormalY=0 NormalZ=1 AngleXU=0 Radius=1.5 StartAngle=3.14159 EndAngle=6.28319
    g10: ArcOfCircle CenterX=-22.1 CenterY=-36.4 CenterZ=0 NormalX=0 NormalY=0 NormalZ=1 AngleXU=0 Radius=1.5 StartAngle=3.14159 EndAngle=6.28319
    g11: ArcOfCircle CenterX=-28.2 CenterY=-33.9 CenterZ=0 NormalX=0 NormalY=0 NormalZ=1 AngleXU=0 Radius=1.5 StartAngle=3.14159 EndAngle=6.28319
    g12: LineSegment StartX=-35.7 StartY=-10.5 StartZ=0 EndX=-35.7 EndY=-27.7 EndZ=0
    g13: LineSegment StartX=-32.7 StartY=-10.5 StartZ=0 EndX=-32.7 EndY=-27.7 EndZ=0
    g14: LineSegment StartX=-29.7 StartY=-33.9 StartZ=0 EndX=-29.7 EndY=-4.3 EndZ=0
    g15: LineSegment StartX=-26.7 StartY=-33.9 StartZ=0 EndX=-26.7 EndY=-4.3 EndZ=0
    g16: LineSegment StartX=-2.5 StartY=-10.5 StartZ=0 EndX=-2.5 EndY=-27.7 EndZ=0
    g17: LineSegment StartX=-8.5 StartY=-4.3 StartZ=0 EndX=-8.5 EndY=-33.9 EndZ=0
    g18: LineSegment StartX=-5.5 StartY=-10.5 StartZ=0 EndX=-5.5 EndY=-27.7 EndZ=0
    g19: LineSegment StartX=-11.5 StartY=-4.3 StartZ=0 EndX=-11.5 EndY=-33.9 EndZ=0
    g20: LineSegment StartX=-14.6 StartY=-1.8 StartZ=0 EndX=-14.6 EndY=-36.4 EndZ=0
    g21: LineSegment StartX=-17.6 StartY=-1.8 StartZ=0 EndX=-17.6 EndY=-36.4 EndZ=0
    g22: LineSegment StartX=-20.6 StartY=-36.4 StartZ=0 EndX=-20.6 EndY=-1.8 EndZ=0
    g23: LineSegment StartX=-23.6 StartY=-1.8 StartZ=0 EndX=-23.6 EndY=-36.4 EndZ=0
  constraints (48):
    c: Block(g0)
    c: Block(g1)
    c: Block(g2)
    c: Block(g3)
    c: Block(g4)
    c: Block(g5)
    c: Block(g6)
    c: Block(g7)
    c: Block(g8)
    c: Block(g9)
    c: Block(g10)
    c: Block(g11)
    c: Coincident(g12,g1)
    c: Coincident(g12,g2)
    c: Vertical(g12)
    c: Coincident(g13,g1)
    c: Coincident(g13,g2)
    c: Vertical(g13)
    c: Coincident(g14,g11)
    c: Coincident(g14,g7)
    c: Vertical(g14)
    c: Coincident(g15,g11)
    c: Coincident(g15,g7)
    c: Vertical(g15)
    c: Coincident(g16,g0)
    c: Coincident(g16,g3)
    c: Vertical(g16)
    c: Coincident(g17,g4)
    c: Coincident(g17,g8)
    c: Vertical(g17)
    c: Coincident(g18,g0)
    c: Coincident(g18,g3)
    c: Vertical(g18)
    c: Coincident(g19,g4)
    c: Coincident(g19,g8)
    c: Vertical(g19)
    c: Coincident(g20,g5)
    c: Coincident(g20,g9)
    c: Vertical(g20)
    c: Coincident(g21,g5)
    c: Coincident(g21,g9)
    c: Vertical(g21)
    c: Coincident(g22,g10)
    c: Coincident(g22,g6)
    c: Vertical(g22)
    c: Coincident(g23,g6)
    c: Coincident(g23,g10)
    c: Vertical(g23)
FEATURE [Part::Extrusion] Extrude020  label="removeToCreateFanGrillHoles"
  Base = -> Sketch029
  Dir = (0,-1,6e-16)
  DirMode = 2
  FaceMakerClass = Part::FaceMakerBullseye
  LengthFwd = 10
  LengthRev = 0
  Placement = pos=(65.4,44,54.82) rot=(0,0,1;0rad)
  Solid = true
  Symmetric = false
FEATURE [Part::MultiFuse] Fusion055  label="top008"
  Shapes = -> [Cut017,Cut018]
FEATURE [Part::Cut] Cut019  label="top009"
  Base = -> Fusion055
  Tool = -> Extrude020
FEATURE [App::MeasureDistance] Distance003  label="Distance: 71.95 mm"
  Distance = 71.9513
  P1 = (117,38,72)
  P2 = (117,38,0.0487319)
FEATURE [Sketcher::SketchObject] Sketch030
  FullyConstrained = true
  Placement = pos=(117,19,0) rot=(0.57735,0.57735,0.57735;2.0944rad)
  sketch-geometry (48):
    g0: LineSegment StartX=-49.19 StartY=69.25 StartZ=0 EndX=-49.19 EndY=66.25 EndZ=0
    g1: LineSegment StartX=-49.19 StartY=63.5 StartZ=0 EndX=-49.19 EndY=60.5 EndZ=0
    g2: LineSegment StartX=-49.19 StartY=57.75 StartZ=0 EndX=-49.19 EndY=54.75 EndZ=0
    g3: LineSegment StartX=-49.19 StartY=52 StartZ=0 EndX=-49.19 EndY=49 EndZ=0
    g4: LineSegment StartX=-49.19 StartY=46.25 StartZ=0 EndX=-49.19 EndY=43.25 EndZ=0
    g5: LineSegment StartX=-49.19 StartY=40.5 StartZ=0 EndX=-49.19 EndY=37.5 EndZ=0
    g6: LineSegment StartX=-49.19 StartY=34.5 StartZ=0 EndX=-49.19 EndY=31.5 EndZ=0
    g7: LineSegment StartX=-49.19 StartY=28.75 StartZ=0 EndX=-49.19 EndY=25.75 EndZ=0
    g8: LineSegment StartX=-49.19 StartY=23 StartZ=0 EndX=-49.19 EndY=20 EndZ=0
    g9: LineSegment StartX=-49.19 StartY=17.25 StartZ=0 EndX=-49.19 EndY=14.25 EndZ=0
    g10: LineSegment StartX=-49.19 StartY=11.5 StartZ=0 EndX=-49.19 EndY=8.5 EndZ=0
    g11: LineSegment StartX=-49.19 StartY=5.75 StartZ=0 EndX=-49.19 EndY=2.75 EndZ=0
    g12: ArcOfCircle CenterX=-1.5 CenterY=67.75 CenterZ=0 NormalX=0 NormalY=0 NormalZ=1 AngleXU=0 Radius=1.5 StartAngle=4.71239 EndAngle=7.85398
    g13: ArcOfCircle CenterX=-1.5 CenterY=62 CenterZ=0 NormalX=0 NormalY=0 NormalZ=1 AngleXU=0 Radius=1.5 StartAngle=4.71239 EndAngle=7.85398
    g14: ArcOfCircle CenterX=-1.5 CenterY=56.25 CenterZ=0 NormalX=0 NormalY=0 NormalZ=1 AngleXU=0 Radius=1.5 StartAngle=4.71239 EndAngle=7.85398
    g15: ArcOfCircle CenterX=-11.49 CenterY=50.5 CenterZ=0 NormalX=0 NormalY=0 NormalZ=1 AngleXU=0 Radius=1.5 StartAngle=4.71239 EndAngle=7.85398
    g16: ArcOfCircle CenterX=-16.28 CenterY=44.75 CenterZ=0 NormalX=0 NormalY=0 NormalZ=1 AngleXU=0 Radius=1.5 StartAngle=4.71239 EndAngle=7.85398
    g17: ArcOfCircle CenterX=-18.2337 CenterY=39 CenterZ=0 NormalX=0 NormalY=0 NormalZ=1 AngleXU=0 Radius=1.5 StartAngle=4.71485 EndAngle=7.85398
    g18: ArcOfCircle CenterX=-16.2837 CenterY=27.25 CenterZ=0 NormalX=0 NormalY=0 NormalZ=1 AngleXU=0 Radius=1.5 StartAngle=4.71485 EndAngle=7.85398
    g19: ArcOfCircle CenterX=-18.2337 CenterY=33 CenterZ=0 NormalX=0 NormalY=0 NormalZ=1 AngleXU=0 Radius=1.5 StartAngle=4.71485 EndAngle=7.85398
    g20: ArcOfCircle CenterX=-11.49 CenterY=21.5 CenterZ=0 NormalX=0 NormalY=0 NormalZ=1 AngleXU=0 Radius=1.5 StartAngle=4.71239 EndAngle=7.85398
    g21: ArcOfCircle CenterX=-1.5 CenterY=4.25 CenterZ=0 NormalX=0 NormalY=0 NormalZ=1 AngleXU=0 Radius=1.5 StartAngle=4.71239 EndAngle=7.85398
    g22: ArcOfCircle CenterX=-1.5 CenterY=10 CenterZ=0 NormalX=0 NormalY=0 NormalZ=1 AngleXU=0 Radius=1.5 StartAngle=4.71239 EndAngle=7.85398
    g23: ArcOfCircle CenterX=-1.5 CenterY=15.75 CenterZ=0 NormalX=0 NormalY=0 NormalZ=1 AngleXU=0 Radius=1.5 StartAngle=4.71239 EndAngle=7.85398
    g24: LineSegment StartX=-49.19 StartY=69.25 StartZ=0 EndX=-1.5 EndY=69.25 EndZ=0
    g25: LineSegment StartX=-49.19 StartY=66.25 StartZ=0 EndX=-1.5 EndY=66.25 EndZ=0
    g26: LineSegment StartX=-49.19 StartY=63.5 StartZ=0 EndX=-1.5 EndY=63.5 EndZ=0
    g27: LineSegment StartX=-49.19 StartY=60.5 StartZ=0 EndX=-1.5 EndY=60.5 EndZ=0
    g28: LineSegment StartX=-49.19 StartY=57.75 StartZ=0 EndX=-1.5 EndY=57.75 EndZ=0
    g29: LineSegment StartX=-49.19 StartY=54.75 StartZ=0 EndX=-1.5 EndY=54.75 EndZ=0
    g30: LineSegment StartX=-49.19 StartY=52 StartZ=0 EndX=-11.49 EndY=52 EndZ=0
    g31: LineSegment StartX=-49.19 StartY=49 StartZ=0 EndX=-11.49 EndY=49 EndZ=0
    g32: LineSegment StartX=-49.19 StartY=46.25 StartZ=0 EndX=-16.28 EndY=46.25 EndZ=0
    g33: LineSegment StartX=-49.19 StartY=43.25 StartZ=0 EndX=-16.28 EndY=43.25 EndZ=0
    g34: LineSegment StartX=-49.19 StartY=40.5 StartZ=0 EndX=-18.2337 EndY=40.5 EndZ=0
    g35: LineSegment StartX=-49.19 StartY=37.5 StartZ=0 EndX=-18.23 EndY=37.5 EndZ=0
    g36: LineSegment StartX=-49.19 StartY=34.5 StartZ=0 EndX=-18.2337 EndY=34.5 EndZ=0
    g37: LineSegment StartX=-49.19 StartY=31.5 StartZ=0 EndX=-18.23 EndY=31.5 EndZ=0
    g38: LineSegment StartX=-49.19 StartY=28.75 StartZ=0 EndX=-16.2837 EndY=28.75 EndZ=0
    g39: LineSegment StartX=-49.19 StartY=25.75 StartZ=0 EndX=-16.28 EndY=25.75 EndZ=0
    g40: LineSegment StartX=-49.19 StartY=23 StartZ=0 EndX=-11.49 EndY=23 EndZ=0
    g41: LineSegment StartX=-49.19 StartY=20 StartZ=0 EndX=-11.49 EndY=20 EndZ=0
    g42: LineSegment StartX=-49.19 StartY=17.25 StartZ=0 EndX=-1.5 EndY=17.25 EndZ=0
    g43: LineSegment StartX=-49.19 StartY=14.25 StartZ=0 EndX=-1.5 EndY=14.25 EndZ=0
    g44: LineSegment StartX=-49.19 StartY=11.5 StartZ=0 EndX=-1.5 EndY=11.5 EndZ=0
    g45: LineSegment StartX=-49.19 StartY=8.5 StartZ=0 EndX=-1.5 EndY=8.5 EndZ=0
    g46: LineSegment StartX=-49.19 StartY=5.75 StartZ=0 EndX=-1.5 EndY=5.75 EndZ=0
    g47: LineSegment StartX=-49.19 StartY=2.75 StartZ=0 EndX=-1.5 EndY=2.75 EndZ=0
  constraints (120):
    c: Vertical(g0)
    c: Distance(g0) = 3
    c: Block(g0)
    c: Vertical(g1)
    c: Distance(g1) = 3
    c: Vertical(g2)
    c: Equal(g0,g2) = 3
    c: Block(g2)
    c: Vertical(g3)
    c: Equal(g1,g3) = 3
    c: Vertical(g4)
    c: Equal(g0,g4) = 3
    c: Block(g4)
    c: Vertical(g5)
    c: Equal(g1,g5) = 3
    c: Vertical(g6)
    c: Equal(g0,g6) = 3
    c: Block(g6)
    c: Vertical(g7)
    c: Equal(g1,g7) = 3
    c: Vertical(g8)
    c: Equal(g0,g8) = 3
    c: Block(g8)
    c: Vertical(g9)
    c: Equal(g1,g9) = 3
    c: Vertical(g10)
    c: Equal(g0,g10) = 3
    c: Block(g10)
    c: Vertical(g11)
    c: Equal(g1,g11) = 3
    c: Block(g12)
    c: Block(g13)
    c: Block(g14)
    c: Block(g15)
    c: Block(g16)
    c: Block(g17)
    c: Block(g18)
    c: Block(g19)
    c: Block(g20)
    c: Block(g21)
    c: Block(g22)
    c: Block(g23)
    c: Block(g11)
    c: Block(g9)
    c: Block(g7)
    c: Block(g5)
    c: Block(g3)
    c: Block(g1)
    c: Coincident(g24,g0)
    c: Coincident(g24,g12)
    c: Horizontal(g24)
    c: Coincident(g25,g0)
    c: Coincident(g25,g12)
    c: Horizontal(g25)
    c: Coincident(g26,g1)
    c: Coincident(g26,g13)
    c: Horizontal(g26)
    c: Coincident(g27,g1)
    c: Coincident(g27,g13)
    c: Horizontal(g27)
    c: Coincident(g28,g2)
    c: Coincident(g28,g14)
    c: Horizontal(g28)
    c: Coincident(g29,g2)
    c: Coincident(g29,g14)
    c: Horizontal(g29)
    c: Coincident(g30,g3)
    c: Coincident(g30,g15)
    c: Horizontal(g30)
    c: Coincident(g31,g3)
    c: Coincident(g31,g15)
    c: Horizontal(g31)
    c: Coincident(g32,g4)
    c: Coincident(g32,g16)
    c: Horizontal(g32)
    c: Coincident(g33,g4)
    c: Coincident(g33,g16)
    c: Horizontal(g33)
    c: Coincident(g34,g5)
    c: Coincident(g34,g17)
    c: Horizontal(g34)
    c: Coincident(g35,g5)
    c: Coincident(g35,g17)
    c: Horizontal(g35)
    c: Coincident(g36,g6)
    c: Coincident(g36,g19)
    c: Horizontal(g36)
    c: Coincident(g37,g6)
    c: Coincident(g37,g19)
    c: Horizontal(g37)
    c: Coincident(g38,g7)
    c: Coincident(g38,g18)
    c: Horizontal(g38)
    c: Coincident(g39,g7)
    c: Coincident(g39,g18)
    c: Horizontal(g39)
    c: Coincident(g40,g8)
    c: Coincident(g40,g20)
    c: Horizontal(g40)
    c: Coincident(g41,g8)
    c: Coincident(g41,g20)
    c: Horizontal(g41)
    c: Coincident(g42,g9)
    c: Coincident(g42,g23)
    c: Horizontal(g42)
    c: Coincident(g43,g9)
    c: Coincident(g43,g23)
    c: Horizontal(g43)
    c: Coincident(g44,g10)
    c: Coincident(g44,g22)
    c: Horizontal(g44)
    c: Coincident(g45,g10)
    c: Coincident(g45,g22)
    c: Horizontal(g45)
    c: Coincident(g46,g11)
    c: Coincident(g46,g21)
    c: Horizontal(g46)
    c: Coincident(g47,g11)
    c: Coincident(g47,g21)
    c: Horizontal(g47)
FEATURE [Sketcher::SketchObject] Sketch031
  FullyConstrained = true
  Placement = pos=(117,19,0) rot=(0.57735,0.57735,0.57735;2.0944rad)
  sketch-geometry (24):
    g0: ArcOfCircle CenterX=-49.19 CenterY=67.75 CenterZ=0 NormalX=0 NormalY=0 NormalZ=1 AngleXU=0 Radius=1.5 StartAngle=1.5708 EndAngle=4.71239
    g1: ArcOfCircle CenterX=-49.19 CenterY=62 CenterZ=0 NormalX=0 NormalY=0 NormalZ=1 AngleXU=0 Radius=1.5 StartAngle=1.5708 EndAngle=4.71239
    g2: ArcOfCircle CenterX=-49.19 CenterY=56.25 CenterZ=0 NormalX=0 NormalY=0 NormalZ=1 AngleXU=0 Radius=1.5 StartAngle=1.5708 EndAngle=4.71239
    g3: ArcOfCircle CenterX=-49.19 CenterY=50.5 CenterZ=0 NormalX=0 NormalY=0 NormalZ=1 AngleXU=0 Radius=1.5 StartAngle=1.5708 EndAngle=4.71239
    g4: ArcOfCircle CenterX=-49.19 CenterY=44.75 CenterZ=0 NormalX=0 NormalY=0 NormalZ=1 AngleXU=0 Radius=1.5 StartAngle=1.5708 EndAngle=4.71239
    g5: ArcOfCircle CenterX=-49.19 CenterY=39 CenterZ=0 NormalX=0 NormalY=0 NormalZ=1 AngleXU=0 Radius=1.5 StartAngle=1.5708 EndAngle=4.71239
    g6: ArcOfCircle CenterX=-49.19 CenterY=33 CenterZ=0 NormalX=0 NormalY=0 NormalZ=1 AngleXU=0 Radius=1.5 StartAngle=1.5708 EndAngle=4.71239
    g7: ArcOfCircle CenterX=-49.19 CenterY=27.25 CenterZ=0 NormalX=0 NormalY=0 NormalZ=1 AngleXU=0 Radius=1.5 StartAngle=1.5708 EndAngle=4.71239
    g8: ArcOfCircle CenterX=-49.19 CenterY=21.5 CenterZ=0 NormalX=0 NormalY=0 NormalZ=1 AngleXU=0 Radius=1.5 StartAngle=1.5708 EndAngle=4.71239
    g9: ArcOfCircle CenterX=-49.19 CenterY=15.75 CenterZ=0 NormalX=0 NormalY=0 NormalZ=1 AngleXU=0 Radius=1.5 StartAngle=1.5708 EndAngle=4.71239
    g10: ArcOfCircle CenterX=-49.19 CenterY=10 CenterZ=0 NormalX=0 NormalY=0 NormalZ=1 AngleXU=0 Radius=1.5 StartAngle=1.5708 EndAngle=4.71239
    g11: ArcOfCircle CenterX=-49.19 CenterY=4.25 CenterZ=0 NormalX=0 NormalY=0 NormalZ=1 AngleXU=0 Radius=1.5 StartAngle=1.5708 EndAngle=4.71239
    g12: LineSegment StartX=-49.19 StartY=69.25 StartZ=0 EndX=-49.19 EndY=66.25 EndZ=0
    g13: LineSegment StartX=-49.19 StartY=63.5 StartZ=0 EndX=-49.19 EndY=60.5 EndZ=0
    g14: LineSegment StartX=-49.19 StartY=57.75 StartZ=0 EndX=-49.19 EndY=54.75 EndZ=0
    g15: LineSegment StartX=-49.19 StartY=52 StartZ=0 EndX=-49.19 EndY=49 EndZ=0
    g16: LineSegment StartX=-49.19 StartY=46.25 StartZ=0 EndX=-49.19 EndY=43.25 EndZ=0
    g17: LineSegment StartX=-49.19 StartY=40.5 StartZ=0 EndX=-49.19 EndY=37.5 EndZ=0
    g18: LineSegment StartX=-49.19 StartY=34.5 StartZ=0 EndX=-49.19 EndY=31.5 EndZ=0
    g19: LineSegment StartX=-49.19 StartY=28.75 StartZ=0 EndX=-49.19 EndY=25.75 EndZ=0
    g20: LineSegment StartX=-49.19 StartY=23 StartZ=0 EndX=-49.19 EndY=20 EndZ=0
    g21: LineSegment StartX=-49.19 StartY=17.25 StartZ=0 EndX=-49.19 EndY=14.25 EndZ=0
    g22: LineSegment StartX=-49.19 StartY=11.5 StartZ=0 EndX=-49.19 EndY=8.5 EndZ=0
    g23: LineSegment StartX=-49.19 StartY=5.75 StartZ=0 EndX=-49.19 EndY=2.75 EndZ=0
  constraints (48):
    c: Block(g0)
    c: Block(g1)
    c: Block(g2)
    c: Block(g3)
    c: Block(g4)
    c: Block(g5)
    c: Block(g6)
    c: Block(g7)
    c: Block(g8)
    c: Block(g9)
    c: Block(g10)
    c: Block(g11)
    c: Coincident(g12,g0)
    c: Coincident(g12,g0)
    c: Vertical(g12)
    c: Vertical(g13)
    c: Coincident(g13,g1)
    c: Vertical(g14)
    c: Coincident(g14,g2)
    c: Vertical(g15)
    c: Coincident(g15,g3)
    c: Vertical(g16)
    c: Coincident(g16,g4)
    c: Vertical(g17)
    c: Coincident(g17,g5)
    c: Vertical(g18)
    c: Coincident(g18,g6)
    c: Vertical(g19)
    c: Coincident(g19,g7)
    c: Vertical(g20)
    c: Coincident(g20,g8)
    c: Vertical(g21)
    c: Coincident(g21,g9)
    c: Vertical(g22)
    c: Coincident(g22,g10)
    c: Vertical(g23)
    c: Coincident(g23,g11)
    c: Block(g23)
    c: Block(g22)
    c: Block(g21)
    c: Block(g20)
    c: Block(g13)
    c: Block(g14)
    c: Block(g15)
    c: Block(g16)
    c: Block(g17)
    c: Block(g18)
    c: Block(g19)
FEATURE [Part::Extrusion] Extrude022
  Base = -> Sketch030
  Dir = (1,-2e-16,2e-16)
  DirMode = 2
  FaceMakerClass = Part::FaceMakerBullseye
  LengthFwd = 19
  LengthRev = 0
  Placement = pos=(-19,0,0) rot=(0,0,1;0rad)
  Solid = true
  Symmetric = false
FEATURE [Part::Fillet] Fillet022
  Base = -> Extrude022
  Edges = 24 edges r=1.49: [Edge6,Edge11,Edge18,Edge23,Edge30,Edge35,Edge42,Edge47,Edge54,Edge59,Edge66,Edge71,Edge78,Edge83,Edge90,Edge95,Edge102,Edge107,Edge114,Edge119,Edge126,Edge131,Edge138,Edge143]
FEATURE [Part::Cut] Cut020  label="top010"
  Base = -> Cut019
  Tool = -> Fillet022
FEATURE [Sketcher::SketchObject] Sketch032
  FullyConstrained = true
  Placement = pos=(117,19,0) rot=(0.57735,0.57735,0.57735;2.0944rad)
  sketch-geometry (48):
    g0: LineSegment StartX=-49.19 StartY=69.25 StartZ=0 EndX=-49.19 EndY=66.25 EndZ=0
    g1: LineSegment StartX=-49.19 StartY=63.5 StartZ=0 EndX=-49.19 EndY=60.5 EndZ=0
    g2: LineSegment StartX=-49.19 StartY=57.75 StartZ=0 EndX=-49.19 EndY=54.75 EndZ=0
    g3: LineSegment StartX=-49.19 StartY=52 StartZ=0 EndX=-49.19 EndY=49 EndZ=0
    g4: LineSegment StartX=-49.19 StartY=46.25 StartZ=0 EndX=-49.19 EndY=43.25 EndZ=0
    g5: LineSegment StartX=-49.19 StartY=40.5 StartZ=0 EndX=-49.19 EndY=37.5 EndZ=0
    g6: LineSegment StartX=-49.19 StartY=34.5 StartZ=0 EndX=-49.19 EndY=31.5 EndZ=0
    g7: LineSegment StartX=-49.19 StartY=28.75 StartZ=0 EndX=-49.19 EndY=25.75 EndZ=0
    g8: LineSegment StartX=-49.19 StartY=23 StartZ=0 EndX=-49.19 EndY=20 EndZ=0
    g9: LineSegment StartX=-49.19 StartY=17.25 StartZ=0 EndX=-49.19 EndY=14.25 EndZ=0
    g10: LineSegment StartX=-49.19 StartY=11.5 StartZ=0 EndX=-49.19 EndY=8.5 EndZ=0
    g11: LineSegment StartX=-49.19 StartY=5.75 StartZ=0 EndX=-49.19 EndY=2.75 EndZ=0
    g12: ArcOfCircle CenterX=-1.5 CenterY=67.75 CenterZ=0 NormalX=0 NormalY=0 NormalZ=1 AngleXU=0 Radius=1.5 StartAngle=4.71239 EndAngle=7.85398
    g13: ArcOfCircle CenterX=-1.5 CenterY=62 CenterZ=0 NormalX=0 NormalY=0 NormalZ=1 AngleXU=0 Radius=1.5 StartAngle=4.71239 EndAngle=7.85398
    g14: ArcOfCircle CenterX=-1.5 CenterY=56.25 CenterZ=0 NormalX=0 NormalY=0 NormalZ=1 AngleXU=0 Radius=1.5 StartAngle=4.71239 EndAngle=7.85398
    g15: ArcOfCircle CenterX=-11.49 CenterY=50.5 CenterZ=0 NormalX=0 NormalY=0 NormalZ=1 AngleXU=0 Radius=1.5 StartAngle=4.71239 EndAngle=7.85398
    g16: ArcOfCircle CenterX=-16.28 CenterY=44.75 CenterZ=0 NormalX=0 NormalY=0 NormalZ=1 AngleXU=0 Radius=1.5 StartAngle=4.71239 EndAngle=7.85398
    g17: ArcOfCircle CenterX=-18.2337 CenterY=39 CenterZ=0 NormalX=0 NormalY=0 NormalZ=1 AngleXU=0 Radius=1.5 StartAngle=4.71485 EndAngle=7.85398
    g18: ArcOfCircle CenterX=-16.2837 CenterY=27.25 CenterZ=0 NormalX=0 NormalY=0 NormalZ=1 AngleXU=0 Radius=1.5 StartAngle=4.71485 EndAngle=7.85398
    g19: ArcOfCircle CenterX=-18.2337 CenterY=33 CenterZ=0 NormalX=0 NormalY=0 NormalZ=1 AngleXU=0 Radius=1.5 StartAngle=4.71485 EndAngle=7.85398
    g20: ArcOfCircle CenterX=-11.49 CenterY=21.5 CenterZ=0 NormalX=0 NormalY=0 NormalZ=1 AngleXU=0 Radius=1.5 StartAngle=4.71239 EndAngle=7.85398
    g21: ArcOfCircle CenterX=-1.5 CenterY=4.25 CenterZ=0 NormalX=0 NormalY=0 NormalZ=1 AngleXU=0 Radius=1.5 StartAngle=4.71239 EndAngle=7.85398
    g22: ArcOfCircle CenterX=-1.5 CenterY=10 CenterZ=0 NormalX=0 NormalY=0 NormalZ=1 AngleXU=0 Radius=1.5 StartAngle=4.71239 EndAngle=7.85398
    g23: ArcOfCircle CenterX=-1.5 CenterY=15.75 CenterZ=0 NormalX=0 NormalY=0 NormalZ=1 AngleXU=0 Radius=1.5 StartAngle=4.71239 EndAngle=7.85398
    g24: LineSegment StartX=-49.19 StartY=69.25 StartZ=0 EndX=-1.5 EndY=69.25 EndZ=0
    g25: LineSegment StartX=-49.19 StartY=66.25 StartZ=0 EndX=-1.5 EndY=66.25 EndZ=0
    g26: LineSegment StartX=-49.19 StartY=63.5 StartZ=0 EndX=-1.5 EndY=63.5 EndZ=0
    g27: LineSegment StartX=-49.19 StartY=60.5 StartZ=0 EndX=-1.5 EndY=60.5 EndZ=0
    g28: LineSegment StartX=-49.19 StartY=57.75 StartZ=0 EndX=-1.5 EndY=57.75 EndZ=0
    g29: LineSegment StartX=-49.19 StartY=54.75 StartZ=0 EndX=-1.5 EndY=54.75 EndZ=0
    g30: LineSegment StartX=-49.19 StartY=52 StartZ=0 EndX=-11.49 EndY=52 EndZ=0
    g31: LineSegment StartX=-49.19 StartY=49 StartZ=0 EndX=-11.49 EndY=49 EndZ=0
    g32: LineSegment StartX=-49.19 StartY=46.25 StartZ=0 EndX=-16.28 EndY=46.25 EndZ=0
    g33: LineSegment StartX=-49.19 StartY=43.25 StartZ=0 EndX=-16.28 EndY=43.25 EndZ=0
    g34: LineSegment StartX=-49.19 StartY=40.5 StartZ=0 EndX=-18.2337 EndY=40.5 EndZ=0
    g35: LineSegment StartX=-49.19 StartY=37.5 StartZ=0 EndX=-18.23 EndY=37.5 EndZ=0
    g36: LineSegment StartX=-49.19 StartY=34.5 StartZ=0 EndX=-18.2337 EndY=34.5 EndZ=0
    g37: LineSegment StartX=-49.19 StartY=31.5 StartZ=0 EndX=-18.23 EndY=31.5 EndZ=0
    g38: LineSegment StartX=-49.19 StartY=28.75 StartZ=0 EndX=-16.2837 EndY=28.75 EndZ=0
    g39: LineSegment StartX=-49.19 StartY=25.75 StartZ=0 EndX=-16.28 EndY=25.75 EndZ=0
    g40: LineSegment StartX=-49.19 StartY=23 StartZ=0 EndX=-11.49 EndY=23 EndZ=0
    g41: LineSegment StartX=-49.19 StartY=20 StartZ=0 EndX=-11.49 EndY=20 EndZ=0
    g42: LineSegment StartX=-49.19 StartY=17.25 StartZ=0 EndX=-1.5 EndY=17.25 EndZ=0
    g43: LineSegment StartX=-49.19 StartY=14.25 StartZ=0 EndX=-1.5 EndY=14.25 EndZ=0
    g44: LineSegment StartX=-49.19 StartY=11.5 StartZ=0 EndX=-1.5 EndY=11.5 EndZ=0
    g45: LineSegment StartX=-49.19 StartY=8.5 StartZ=0 EndX=-1.5 EndY=8.5 EndZ=0
    g46: LineSegment StartX=-49.19 StartY=5.75 StartZ=0 EndX=-1.5 EndY=5.75 EndZ=0
    g47: LineSegment StartX=-49.19 StartY=2.75 StartZ=0 EndX=-1.5 EndY=2.75 EndZ=0
  constraints (120):
    c: Vertical(g0)
    c: Distance(g0) = 3
    c: Block(g0)
    c: Vertical(g1)
    c: Distance(g1) = 3
    c: Vertical(g2)
    c: Equal(g0,g2) = 3
    c: Block(g2)
    c: Vertical(g3)
    c: Equal(g1,g3) = 3
    c: Vertical(g4)
    c: Equal(g0,g4) = 3
    c: Block(g4)
    c: Vertical(g5)
    c: Equal(g1,g5) = 3
    c: Vertical(g6)
    c: Equal(g0,g6) = 3
    c: Block(g6)
    c: Vertical(g7)
    c: Equal(g1,g7) = 3
    c: Vertical(g8)
    c: Equal(g0,g8) = 3
    c: Block(g8)
    c: Vertical(g9)
    c: Equal(g1,g9) = 3
    c: Vertical(g10)
    c: Equal(g0,g10) = 3
    c: Block(g10)
    c: Vertical(g11)
    c: Equal(g1,g11) = 3
    c: Block(g12)
    c: Block(g13)
    c: Block(g14)
    c: Block(g15)
    c: Block(g16)
    c: Block(g17)
    c: Block(g18)
    c: Block(g19)
    c: Block(g20)
    c: Block(g21)
    c: Block(g22)
    c: Block(g23)
    c: Block(g11)
    c: Block(g9)
    c: Block(g7)
    c: Block(g5)
    c: Block(g3)
    c: Block(g1)
    c: Coincident(g24,g0)
    c: Coincident(g24,g12)
    c: Horizontal(g24)
    c: Coincident(g25,g0)
    c: Coincident(g25,g12)
    c: Horizontal(g25)
    c: Coincident(g26,g1)
    c: Coincident(g26,g13)
    c: Horizontal(g26)
    c: Coincident(g27,g1)
    c: Coincident(g27,g13)
    c: Horizontal(g27)
    c: Coincident(g28,g2)
    c: Coincident(g28,g14)
    c: Horizontal(g28)
    c: Coincident(g29,g2)
    c: Coincident(g29,g14)
    c: Horizontal(g29)
    c: Coincident(g30,g3)
    c: Coincident(g30,g15)
    c: Horizontal(g30)
    c: Coincident(g31,g3)
    c: Coincident(g31,g15)
    c: Horizontal(g31)
    c: Coincident(g32,g4)
    c: Coincident(g32,g16)
    c: Horizontal(g32)
    c: Coincident(g33,g4)
    c: Coincident(g33,g16)
    c: Horizontal(g33)
    c: Coincident(g34,g5)
    c: Coincident(g34,g17)
    c: Horizontal(g34)
    c: Coincident(g35,g5)
    c: Coincident(g35,g17)
    c: Horizontal(g35)
    c: Coincident(g36,g6)
    c: Coincident(g36,g19)
    c: Horizontal(g36)
    c: Coincident(g37,g6)
    c: Coincident(g37,g19)
    c: Horizontal(g37)
    c: Coincident(g38,g7)
    c: Coincident(g38,g18)
    c: Horizontal(g38)
    c: Coincident(g39,g7)
    c: Coincident(g39,g18)
    c: Horizontal(g39)
    c: Coincident(g40,g8)
    c: Coincident(g40,g20)
    c: Horizontal(g40)
    c: Coincident(g41,g8)
    c: Coincident(g41,g20)
    c: Horizontal(g41)
    c: Coincident(g42,g9)
    c: Coincident(g42,g23)
    c: Horizontal(g42)
    c: Coincident(g43,g9)
    c: Coincident(g43,g23)
    c: Horizontal(g43)
    c: Coincident(g44,g10)
    c: Coincident(g44,g22)
    c: Horizontal(g44)
    c: Coincident(g45,g10)
    c: Coincident(g45,g22)
    c: Horizontal(g45)
    c: Coincident(g46,g11)
    c: Coincident(g46,g21)
    c: Horizontal(g46)
    c: Coincident(g47,g11)
    c: Coincident(g47,g21)
    c: Horizontal(g47)
FEATURE [Part::Extrusion] Extrude023
  Base = -> Sketch032
  Dir = (1,-2e-16,2e-16)
  DirMode = 2
  FaceMakerClass = Part::FaceMakerBullseye
  LengthFwd = 19
  LengthRev = 0
  Placement = pos=(-19,0,0) rot=(0,0,1;0rad)
  Solid = true
  Symmetric = false
FEATURE [Part::Fillet] Fillet023
  Base = -> Extrude023
  Edges = <same value as first occurrence — deduplicated (x6 in doc)>
  Placement = pos=(0,0.05,0) rot=(0,0,1;0rad)
FEATURE [Part::Cut] Cut014  label="bottom003"
  Base = -> Cut007
  Tool = -> Fusion047
FEATURE [Part::Cut] Cut021  label="bottom004"
  Base = -> Cut014
  Tool = -> Fillet023
FEATURE [Sketcher::SketchObject] Sketch033
  FullyConstrained = true
  Placement = pos=(117,19,0) rot=(0.57735,0.57735,0.57735;2.0944rad)
  sketch-geometry (8):
    g0: LineSegment StartX=-49.19 StartY=69.25 StartZ=0 EndX=-49.19 EndY=66.25 EndZ=0
    g1: LineSegment StartX=-49.19 StartY=5.75 StartZ=0 EndX=-49.19 EndY=2.75 EndZ=0
    g2: ArcOfCircle CenterX=-1.5 CenterY=67.75 CenterZ=0 NormalX=0 NormalY=0 NormalZ=1 AngleXU=0 Radius=1.5 StartAngle=4.71239 EndAngle=7.85398
    g3: ArcOfCircle CenterX=-1.5 CenterY=4.25 CenterZ=0 NormalX=0 NormalY=0 NormalZ=1 AngleXU=0 Radius=1.5 StartAngle=4.71239 EndAngle=7.85398
    g4: LineSegment StartX=-49.19 StartY=69.25 StartZ=0 EndX=-1.5 EndY=69.25 EndZ=0
    g5: LineSegment StartX=-49.19 StartY=66.25 StartZ=0 EndX=-1.5 EndY=66.25 EndZ=0
    g6: LineSegment StartX=-49.19 StartY=5.75 StartZ=0 EndX=-1.5 EndY=5.75 EndZ=0
    g7: LineSegment StartX=-49.19 StartY=2.75 StartZ=0 EndX=-1.5 EndY=2.75 EndZ=0
  constraints (19):
    c: Vertical(g0)
    c: Distance(g0) = 3
    c: Block(g0)
    c: Vertical(g1)
    c: Block(g2)
    c: Block(g3)
    c: Block(g1)
    c: Coincident(g4,g0)
    c: Coincident(g4,g2)
    c: Horizontal(g4)
    c: Coincident(g5,g0)
    c: Coincident(g5,g2)
    c: Horizontal(g5)
    c: Coincident(g6,g1)
    c: Coincident(g6,g3)
    c: Horizontal(g6)
    c: Coincident(g7,g1)
    c: Coincident(g7,g3)
    c: Horizontal(g7)
FEATURE [Sketcher::SketchObject] Sketch034
  FullyConstrained = true
  Placement = pos=(117,19,0) rot=(0.57735,0.57735,0.57735;2.0944rad)
  sketch-geometry (8):
    g0: LineSegment StartX=-49.19 StartY=63.5 StartZ=0 EndX=-49.19 EndY=60.5 EndZ=0
    g1: LineSegment StartX=-49.19 StartY=11.5 StartZ=0 EndX=-49.19 EndY=8.5 EndZ=0
    g2: ArcOfCircle CenterX=-1.5 CenterY=62 CenterZ=0 NormalX=0 NormalY=0 NormalZ=1 AngleXU=0 Radius=1.5 StartAngle=4.71239 EndAngle=7.85398
    g3: ArcOfCircle CenterX=-1.5 CenterY=10 CenterZ=0 NormalX=0 NormalY=0 NormalZ=1 AngleXU=0 Radius=1.5 StartAngle=4.71239 EndAngle=7.85398
    g4: LineSegment StartX=-49.19 StartY=63.5 StartZ=0 EndX=-1.5 EndY=63.5 EndZ=0
    g5: LineSegment StartX=-49.19 StartY=60.5 StartZ=0 EndX=-1.5 EndY=60.5 EndZ=0
    g6: LineSegment StartX=-49.19 StartY=11.5 StartZ=0 EndX=-1.5 EndY=11.5 EndZ=0
    g7: LineSegment StartX=-49.19 StartY=8.5 StartZ=0 EndX=-1.5 EndY=8.5 EndZ=0
  constraints (19):
    c: Vertical(g0)
    c: Distance(g0) = 3
    c: Vertical(g1)
    c: Block(g1)
    c: Block(g2)
    c: Block(g3)
    c: Block(g0)
    c: Coincident(g4,g0)
    c: Coincident(g4,g2)
    c: Horizontal(g4)
    c: Coincident(g5,g0)
    c: Coincident(g5,g2)
    c: Horizontal(g5)
    c: Coincident(g6,g1)
    c: Coincident(g6,g3)
    c: Horizontal(g6)
    c: Coincident(g7,g1)
    c: Coincident(g7,g3)
    c: Horizontal(g7)
FEATURE [Part::Extrusion] Extrude024
  Base = -> Sketch033
  Dir = (1,0,0)
  DirMode = 2
  FaceMakerClass = Part::FaceMakerBullseye
  LengthFwd = 10
  LengthRev = 0
  Solid = true
  Symmetric = false
FEATURE [Part::Extrusion] Extrude025
  Base = -> Sketch034
  Dir = (1,0,0)
  DirMode = 2
  FaceMakerClass = Part::FaceMakerBullseye
  LengthFwd = 10
  LengthRev = 0
  Solid = true
  Symmetric = false
FEATURE [Part::Fillet] Fillet024  label="removeFromtMoreFrontCaseScrewRetainers"
  Base = -> Extrude024
  Edges = 4 edges r=1.49: [Edge6,Edge11,Edge18,Edge23]
  Placement = pos=(-11,0,0) rot=(0,0,1;0rad)
FEATURE [Part::Fillet] Fillet025  label="removeFromtMoreFrontCaseScrewRetainers001"
  Base = -> Extrude025
  Edges = 4 edges r=1.49: [Edge6,Edge11,Edge18,Edge23]
  Placement = pos=(-19,0,0) rot=(0,0,1;0rad)
FEATURE [Part::Cut] Cut022
  Base = -> Cut015
  Tool = -> Fillet025
FEATURE [Part::Cut] Cut023  label="screwRetainers"
  Base = -> Cut022
  Tool = -> Fillet024
FEATURE [Part::MultiFuse] Fusion056  label="bottom005"
  Shapes = -> [Fusion044,Cut021]
FEATURE [Part::MultiFuse] Fusion057  label="casePillars001"
  Shapes = -> [Cut016,Fusion052]
FEATURE [Part::MultiFuse] Fusion058  label="bottom006"
  Shapes = -> [Fusion056,Cut023]
FEATURE [Part::MultiFuse] Fusion059  label="bottom007"
  Shapes = -> [Fusion058,Fillet005]
FEATURE [Part::MultiFuse] Fusion060  label="bottom008"
  Shapes = -> [Fusion059,Fusion]
FEATURE [Part::MultiFuse] Fusion061  label="top011"
  Shapes = -> [Cut006,Cut020]
FEATURE [Part::MultiFuse] Fusion062  label="top012"
  Shapes = -> [Fusion057,Fusion061]
FEATURE [Sketcher::SketchObject] Sketch035  label="topSketch007"
  FullyConstrained = true
  sketch-geometry (6):
    g0: LineSegment StartX=19 StartY=38 StartZ=0 EndX=117 EndY=38 EndZ=0
    g1: ArcOfCircle CenterX=19 CenterY=19 CenterZ=0 NormalX=0 NormalY=0 NormalZ=1 AngleXU=0 Radius=19 StartAngle=1.5708 EndAngle=3.14159
    g2: LineSegment StartX=117 StartY=38 StartZ=0 EndX=117 EndY=19 EndZ=0
    g3: LineSegment StartX=98 StartY=1.0161e-12 StartZ=0 EndX=5.22862e-06 EndY=1.0161e-12 EndZ=0
    g4: LineSegment StartX=5.22862e-06 StartY=19 StartZ=0 EndX=5.22862e-06 EndY=1.0161e-12 EndZ=0
    g5: ArcOfCircle CenterX=98 CenterY=19 CenterZ=0 NormalX=0 NormalY=0 NormalZ=1 AngleXU=0 Radius=19 StartAngle=4.71239 EndAngle=6.28319
  constraints (16):
    c: Horizontal(g0)
    c: Distance(g0) = 98
    c: Coincident(g1,g0)
    c: Block(g1)
    c: Coincident(g2,g0)
    c: Vertical(g2)
    c: Distance(g2) = 19
    c: Horizontal(g3)
    c: Coincident(g4,g1)
    c: Vertical(g4)
    c: Coincident(g3,g4)
    c: Block(g3)
    c: Coincident(g5,g2)
    c: Coincident(g5,g3)
    c: Block(g0)
    c: Block(g5)
FEATURE [Part::Extrusion] Extrude026  label="sideA001"
  Base = -> Sketch035
  Dir = (0,0,1)
  DirMode = 2
  FaceMakerClass = Part::FaceMakerBullseye
  LengthFwd = 3
  LengthRev = 0
  Placement = pos=(0,0,-2.7) rot=(0,0,1;0rad)
  Solid = true
  Symmetric = false
FEATURE [Sketcher::SketchObject] Sketch036  label="topSketch008"
  FullyConstrained = true
  sketch-geometry (6):
    g0: LineSegment StartX=19 StartY=38 StartZ=0 EndX=117 EndY=38 EndZ=0
    g1: ArcOfCircle CenterX=19 CenterY=19 CenterZ=0 NormalX=0 NormalY=0 NormalZ=1 AngleXU=0 Radius=19 StartAngle=1.5708 EndAngle=3.14159
    g2: LineSegment StartX=117 StartY=38 StartZ=0 EndX=117 EndY=19 EndZ=0
    g3: LineSegment StartX=98 StartY=1.0161e-12 StartZ=0 EndX=5.22862e-06 EndY=1.0161e-12 EndZ=0
    g4: LineSegment StartX=5.22862e-06 StartY=19 StartZ=0 EndX=5.22862e-06 EndY=1.0161e-12 EndZ=0
    g5: ArcOfCircle CenterX=98 CenterY=19 CenterZ=0 NormalX=0 NormalY=0 NormalZ=1 AngleXU=0 Radius=19 StartAngle=4.71239 EndAngle=6.28319
  constraints (16):
    c: Horizontal(g0)
    c: Distance(g0) = 98
    c: Coincident(g1,g0)
    c: Block(g1)
    c: Coincident(g2,g0)
    c: Vertical(g2)
    c: Distance(g2) = 19
    c: Horizontal(g3)
    c: Coincident(g4,g1)
    c: Vertical(g4)
    c: Coincident(g3,g4)
    c: Block(g3)
    c: Coincident(g5,g2)
    c: Coincident(g5,g3)
    c: Block(g0)
    c: Block(g5)
FEATURE [Part::Extrusion] Extrude027  label="sideB001"
  Base = -> Sketch036
  Dir = (0,0,1)
  DirMode = 2
  FaceMakerClass = Part::FaceMakerBullseye
  LengthFwd = 3
  LengthRev = 0
  Placement = pos=(0,0,71.7) rot=(0,0,1;0rad)
  Solid = true
  Symmetric = false
FEATURE [Part::MultiFuse] Fusion064  label="removeFromBottom"
  Shapes = -> [Extrude026,Extrude027]
FEATURE [Part::Cut] Cut024  label="bottom009"
  Base = -> Fusion060
  Tool = -> Fusion064
FEATURE [Sketcher::SketchObject] Sketch037  label="topSketch009"
  FullyConstrained = true
  sketch-geometry (8):
    g0: ArcOfCircle CenterX=19 CenterY=19.1201 CenterZ=0 NormalX=0 NormalY=0 NormalZ=1 AngleXU=0 Radius=18.8799 StartAngle=1.5708 EndAngle=3.14793
    g1: LineSegment StartX=0.120501 StartY=19.0004 StartZ=0 EndX=0.120501 EndY=0.000382114 EndZ=0
    g2: LineSegment StartX=19 StartY=38 StartZ=0 EndX=124 EndY=38 EndZ=0
    g3: LineSegment StartX=0.120501 StartY=0.000382114 StartZ=0 EndX=105.121 EndY=0.000382114 EndZ=0
    g4: LineSegment StartX=124 StartY=38 StartZ=0 EndX=125.616 EndY=38 EndZ=0
    g5: LineSegment StartX=105.121 StartY=0.000382114 StartZ=0 EndX=106.736 EndY=0.000382114 EndZ=0
    g6: ArcOfCircle CenterX=106.616 CenterY=19 CenterZ=0 NormalX=0 NormalY=0 NormalZ=1 AngleXU=0 Radius=19 StartAngle=4.71873 EndAngle=6.28319
    g7: LineSegment StartX=125.616 StartY=38 StartZ=0 EndX=125.616 EndY=19 EndZ=0
  constraints (21):
    c: Block(g0)
    c: Coincident(g1,g0)
    c: Vertical(g1)
    c: Horizontal(g2)
    c: Distance(g2) = 105
    c: Coincident(g2,g0)
    c: Distance(g1) = 19
    c: Coincident(g3,g1)
    c: Horizontal(g3)
    c: Distance(g3) = 105
    c: Coincident(g4,g2)
    c: Horizontal(g4)
    c: Distance(g4) = 1.61553
    c: Horizontal(g5)
    c: Equal(g4,g5) = 1.61553
    c: Coincident(g5,g3)
    c: Block(g6)
    c: Coincident(g6,g5)
    c: Coincident(g7,g4)
    c: Coincident(g7,g6)
    c: Vertical(g7)
FEATURE [Part::Extrusion] Extrude028  label="sideB"
  Base = -> Sketch037
  Dir = (0,0,1)
  DirMode = 2
  FaceMakerClass = Part::FaceMakerBullseye
  LengthFwd = 3
  LengthRev = 0
  Placement = pos=(0,0,72) rot=(0,0,1;0rad)
  Solid = true
  Symmetric = false
FEATURE [Sketcher::SketchObject] Sketch038  label="topSketch010"
  FullyConstrained = true
  sketch-geometry (22):
    g0: LineSegment StartX=5.21097e-06 StartY=3 StartZ=0 EndX=5.21097e-06 EndY=19 EndZ=0
    g1: ArcOfCircle CenterX=19 CenterY=19 CenterZ=0 NormalX=0 NormalY=0 NormalZ=1 AngleXU=0 Radius=19 StartAngle=1.5708 EndAngle=3.14159
    g2: ArcOfCircle CenterX=19 CenterY=19 CenterZ=0 NormalX=0 NormalY=0 NormalZ=1 AngleXU=0 Radius=16 StartAngle=1.5708 EndAngle=3.14159
    g3: LineSegment StartX=114 StartY=35 StartZ=0 EndX=19 EndY=35 EndZ=0
    g4: LineSegment StartX=5.21097e-06 StartY=3 StartZ=0 EndX=5.21097e-06 EndY=0 EndZ=0
    g5: LineSegment StartX=3 StartY=0 StartZ=0 EndX=5.21097e-06 EndY=0 EndZ=0
    g6: LineSegment StartX=3 StartY=19 StartZ=0 EndX=3 EndY=0 EndZ=0
    g7: LineSegment StartX=19 StartY=38 StartZ=0 EndX=124 EndY=38 EndZ=0
    g8: Circle CenterX=119 CenterY=35 CenterZ=0 NormalX=0 NormalY=0 NormalZ=1 AngleXU=0 Radius=1
    g9: Circle CenterX=121 CenterY=35 CenterZ=0 NormalX=0 NormalY=0 NormalZ=1 AngleXU=0 Radius=1
    g10: Circle CenterX=121 CenterY=33 CenterZ=0 NormalX=0 NormalY=0 NormalZ=1 AngleXU=0 Radius=1
    g11: BSplineCurve PolesCount=3 KnotsCount=2 Degree=2 IsPeriodic=0
    g12: GeomPoint X=119 Y=35 Z=0
    g13: GeomPoint X=121 Y=33 Z=0
    g14: LineSegment StartX=119 StartY=35 StartZ=0 EndX=114 EndY=35 EndZ=0
    g15: ArcOfCircle CenterX=105 CenterY=19 CenterZ=0 NormalX=0 NormalY=0 NormalZ=1 AngleXU=0 Radius=16 StartAngle=5.60905 EndAngle=6.28319
    g16: LineSegment StartX=121 StartY=33 StartZ=0 EndX=121 EndY=19 EndZ=0
    g17: LineSegment StartX=117.5 StartY=9.01251 StartZ=0 EndX=121.163 EndY=9.0125 EndZ=0
    g18: ArcOfCircle CenterX=105 CenterY=19 CenterZ=0 NormalX=0 NormalY=0 NormalZ=1 AngleXU=0 Radius=20.6155 StartAngle=5.7297 EndAngle=6.28319
    g19: LineSegment StartX=121.163 StartY=9.0125 StartZ=0 EndX=122.538 EndY=8.16329 EndZ=0
    g20: LineSegment StartX=124 StartY=38 StartZ=0 EndX=125.616 EndY=38 EndZ=0
    g21: LineSegment StartX=125.616 StartY=19 StartZ=0 EndX=125.616 EndY=38 EndZ=0
  constraints (49):
    c: Vertical(g0)
    c: Block(g0)
    c: Coincident(g1,g0)
    c: Block(g1)
    c: Coincident(g2,g1)
    c: Block(g2)
    c: Coincident(g3,g2)
    c: Horizontal(g3)
    c: Tangent(g3,g2)
    c: Coincident(g4,g0)
    c: Distance(g4) = 3
    c: Vertical(g4)
    c: Coincident(g5,g4)
    c: Horizontal(g5)
    c: Coincident(g6,g2)
    c: Coincident(g6,g5)
    c: Vertical(g6)
    c: Horizontal(g7)
    c: Distance(g7) = 105
    c: Coincident(g7,g1)
    c: Block(g3)
    c: Weight(g8) = 1
    c: Equal(g8,g9)
    c: Equal(g8,g10)
    c: InternalAlignment(g8,g11)
    c: InternalAlignment(g9,g11)
    c: InternalAlignment(g10,g11)
    c: InternalAlignment(g12,g11)
    c: InternalAlignment(g13,g11)
    c: Block(g11)
    c: Coincident(g14,g11)
    c: Coincident(g14,g3)
    c: Horizontal(g14)
    c: Block(g15)
    c: Coincident(g16,g11)
    c: Coincident(g16,g15)
    c: Vertical(g16)
    c: Distance(g16) = 14
    c: Coincident(g17,g15)
    c: Block(g18)
    c: Coincident(g19,g18)
    c: Coincident(g20,g7)
    c: Horizontal(g20)
    c: Vertical(g21)
    c: Coincident(g20,g21)
    c: Block(g20)
    c: Block(g21)
    c: Block(g19)
    c: Block(g17)
FEATURE [Part::Extrusion] Extrude029
  Base = -> Sketch038
  Dir = (0,0,1)
  DirMode = 2
  FaceMakerClass = Part::FaceMakerBullseye
  LengthFwd = 72
  LengthRev = 0
  Solid = true
  Symmetric = false
FEATURE [Part::Feature] Face085
  shape: bbox 4.8 x 25.5 x 2e-07 mm, 1 faces, 0 solids (baked)
FEATURE [Part::Revolution] Revolve089  label="moreFrontCaseScrewPost003"
  Angle = 360
  Axis = (0,1,0)
  Base = (0,0,0)
  FaceMakerClass = Part::FaceMakerBullseye
  Placement = pos=(109.5,4.5,3.5) rot=(0,0,1;0rad)
  Solid = false
  Source = -> Face085
  Symmetric = false
FEATURE [Part::Feature] Face086
  shape: bbox 4.8 x 25.5 x 2e-07 mm, 1 faces, 0 solids (baked)
FEATURE [Part::Revolution] Revolve090  label="moreFrontCaseScrewPost004"
  Angle = 360
  Axis = (0,1,0)
  Base = (0,0,0)
  FaceMakerClass = Part::FaceMakerBullseye
  Placement = pos=(109.5,4.5,68.5) rot=(0,0,1;0rad)
  Solid = false
  Source = -> Face086
  Symmetric = false
FEATURE [Part::Fillet] Fillet026  label="top013"
  Base = -> Extrude029
  Edges = 1 edges r=2: [Edge35]
FEATURE [Sketcher::SketchObject] Sketch039
  FullyConstrained = true
  sketch-geometry (7):
    g0: LineSegment StartX=0 StartY=0 StartZ=0 EndX=0 EndY=6 EndZ=0
    g1: Circle CenterX=0 CenterY=0 CenterZ=0 NormalX=0 NormalY=0 NormalZ=1 AngleXU=0 Radius=1
    g2: Circle CenterX=8 CenterY=6 CenterZ=0 NormalX=0 NormalY=0 NormalZ=1 AngleXU=0 Radius=1
    g3: BSplineCurve PolesCount=3 KnotsCount=2 Degree=2 IsPeriodic=0
    g4: GeomPoint X=0 Y=0 Z=0
    g5: GeomPoint X=8 Y=6 Z=0
    g6: LineSegment StartX=0 StartY=6 StartZ=0 EndX=8 EndY=6 EndZ=0
  constraints (14):
    c: Coincident(g0,g-1)
    c: Distance(g0) = 6
    c: Vertical(g0)
    c: Coincident(g3,g0)
    c: Weight(g1) = 1
    c: Equal(g1,g2)
    c: InternalAlignment(g1,g3)
    c: InternalAlignment(g2,g3)
    c: InternalAlignment(g4,g3)
    c: InternalAlignment(g5,g3)
    c: Block(g3)
    c: Coincident(g6,g0)
    c: Coincident(g6,g3)
    c: Horizontal(g6)
FEATURE [Sketcher::SketchObject] Sketch040
  FullyConstrained = true
  sketch-geometry (7):
    g0: LineSegment StartX=0 StartY=0 StartZ=0 EndX=0 EndY=6 EndZ=0
    g1: Circle CenterX=0 CenterY=0 CenterZ=0 NormalX=0 NormalY=0 NormalZ=1 AngleXU=0 Radius=1
    g2: Circle CenterX=8 CenterY=6 CenterZ=0 NormalX=0 NormalY=0 NormalZ=1 AngleXU=0 Radius=1
    g3: BSplineCurve PolesCount=3 KnotsCount=2 Degree=2 IsPeriodic=0
    g4: GeomPoint X=0 Y=0 Z=0
    g5: GeomPoint X=8 Y=6 Z=0
    g6: LineSegment StartX=0 StartY=6 StartZ=0 EndX=8 EndY=6 EndZ=0
  constraints (14):
    c: Coincident(g0,g-1)
    c: Distance(g0) = 6
    c: Vertical(g0)
    c: Coincident(g3,g0)
    c: Weight(g1) = 1
    c: Equal(g1,g2)
    c: InternalAlignment(g1,g3)
    c: InternalAlignment(g2,g3)
    c: InternalAlignment(g4,g3)
    c: InternalAlignment(g5,g3)
    c: Block(g3)
    c: Coincident(g6,g0)
    c: Coincident(g6,g3)
    c: Horizontal(g6)
FEATURE [Sketcher::SketchObject] Sketch041
  FullyConstrained = true
  sketch-geometry (7):
    g0: LineSegment StartX=0 StartY=0 StartZ=0 EndX=0 EndY=6 EndZ=0
    g1: Circle CenterX=0 CenterY=0 CenterZ=0 NormalX=0 NormalY=0 NormalZ=1 AngleXU=0 Radius=1
    g2: Circle CenterX=8 CenterY=6 CenterZ=0 NormalX=0 NormalY=0 NormalZ=1 AngleXU=0 Radius=1
    g3: BSplineCurve PolesCount=3 KnotsCount=2 Degree=2 IsPeriodic=0
    g4: GeomPoint X=0 Y=0 Z=0
    g5: GeomPoint X=8 Y=6 Z=0
    g6: LineSegment StartX=0 StartY=6 StartZ=0 EndX=8 EndY=6 EndZ=0
  constraints (14):
    c: Coincident(g0,g-1)
    c: Distance(g0) = 6
    c: Vertical(g0)
    c: Coincident(g3,g0)
    c: Weight(g1) = 1
    c: Equal(g1,g2)
    c: InternalAlignment(g1,g3)
    c: InternalAlignment(g2,g3)
    c: InternalAlignment(g4,g3)
    c: InternalAlignment(g5,g3)
    c: Block(g3)
    c: Coincident(g6,g0)
    c: Coincident(g6,g3)
    c: Horizontal(g6)
FEATURE [Sketcher::SketchObject] Sketch042
  FullyConstrained = true
  sketch-geometry (7):
    g0: LineSegment StartX=0 StartY=0 StartZ=0 EndX=0 EndY=6 EndZ=0
    g1: Circle CenterX=0 CenterY=0 CenterZ=0 NormalX=0 NormalY=0 NormalZ=1 AngleXU=0 Radius=1
    g2: Circle CenterX=8 CenterY=6 CenterZ=0 NormalX=0 NormalY=0 NormalZ=1 AngleXU=0 Radius=1
    g3: BSplineCurve PolesCount=3 KnotsCount=2 Degree=2 IsPeriodic=0
    g4: GeomPoint X=0 Y=0 Z=0
    g5: GeomPoint X=8 Y=6 Z=0
    g6: LineSegment StartX=0 StartY=6 StartZ=0 EndX=8 EndY=6 EndZ=0
  constraints (14):
    c: Coincident(g0,g-1)
    c: Distance(g0) = 6
    c: Vertical(g0)
    c: Coincident(g3,g0)
    c: Weight(g1) = 1
    c: Equal(g1,g2)
    c: InternalAlignment(g1,g3)
    c: InternalAlignment(g2,g3)
    c: InternalAlignment(g4,g3)
    c: InternalAlignment(g5,g3)
    c: Block(g3)
    c: Coincident(g6,g0)
    c: Coincident(g6,g3)
    c: Horizontal(g6)
FEATURE [Part::Extrusion] Extrude030  label="caseScrewPillarBracket008"
  Base = -> Sketch039
  Dir = (0,0,1)
  DirMode = 2
  FaceMakerClass = Part::FaceMakerBullseye
  LengthFwd = 2.4
  LengthRev = 0
  Placement = pos=(15.76,29,8.8) rot=(0,1,0;0rad)
  Solid = true
  Symmetric = false
FEATURE [Part::Extrusion] Extrude031  label="caseScrewPillarBracket009"
  Base = -> Sketch040
  Dir = (0,0,1)
  DirMode = 2
  FaceMakerClass = Part::FaceMakerBullseye
  LengthFwd = 2.4
  LengthRev = 0
  Placement = pos=(15.76,29,60.8) rot=(0,0,1;0rad)
  Solid = true
  Symmetric = false
FEATURE [Part::Extrusion] Extrude032  label="caseScrewPillarBracket010"
  Base = -> Sketch041
  Dir = (0,0,1)
  DirMode = 2
  FaceMakerClass = Part::FaceMakerBullseye
  LengthFwd = 2.4
  LengthRev = 0
  Placement = pos=(13.7,29,13.26) rot=(0,-1,0;1.5708rad)
  Solid = true
  Symmetric = false
FEATURE [Part::Extrusion] Extrude033  label="caseScrewPillarBracket011"
  Base = -> Sketch042
  Dir = (0,0,1)
  DirMode = 2
  FaceMakerClass = Part::FaceMakerBullseye
  LengthFwd = 2.4
  LengthRev = 0
  Placement = pos=(11.3,29,58.74) rot=(0,1,0;1.5708rad)
  Solid = true
  Symmetric = false
FEATURE [Sketcher::SketchObject] Sketch043
  FullyConstrained = true
  sketch-geometry (7):
    g0: LineSegment StartX=0 StartY=0 StartZ=0 EndX=0 EndY=6 EndZ=0
    g1: Circle CenterX=0 CenterY=0 CenterZ=0 NormalX=0 NormalY=0 NormalZ=1 AngleXU=0 Radius=1
    g2: Circle CenterX=8 CenterY=6 CenterZ=0 NormalX=0 NormalY=0 NormalZ=1 AngleXU=0 Radius=1
    g3: BSplineCurve PolesCount=3 KnotsCount=2 Degree=2 IsPeriodic=0
    g4: GeomPoint X=0 Y=0 Z=0
    g5: GeomPoint X=8 Y=6 Z=0
    g6: LineSegment StartX=0 StartY=6 StartZ=0 EndX=8 EndY=6 EndZ=0
  constraints (14):
    c: Coincident(g0,g-1)
    c: Distance(g0) = 6
    c: Vertical(g0)
    c: Coincident(g3,g0)
    c: Weight(g1) = 1
    c: Equal(g1,g2)
    c: InternalAlignment(g1,g3)
    c: InternalAlignment(g2,g3)
    c: InternalAlignment(g4,g3)
    c: InternalAlignment(g5,g3)
    c: Block(g3)
    c: Coincident(g6,g0)
    c: Coincident(g6,g3)
    c: Horizontal(g6)
FEATURE [Part::Extrusion] Extrude034  label="caseScrewPillarBracket012"
  Base = -> Sketch043
  Dir = (0,0,1)
  DirMode = 2
  FaceMakerClass = Part::FaceMakerBullseye
  LengthFwd = 2.4
  LengthRev = 0
  Placement = pos=(88.3,29,65.23) rot=(0,1,0;1.5708rad)
  Solid = true
  Symmetric = false
FEATURE [Sketcher::SketchObject] Sketch044
  FullyConstrained = true
  sketch-geometry (7):
    g0: LineSegment StartX=0 StartY=0 StartZ=0 EndX=0 EndY=6 EndZ=0
    g1: Circle CenterX=0 CenterY=0 CenterZ=0 NormalX=0 NormalY=0 NormalZ=1 AngleXU=0 Radius=1
    g2: Circle CenterX=8 CenterY=6 CenterZ=0 NormalX=0 NormalY=0 NormalZ=1 AngleXU=0 Radius=1
    g3: BSplineCurve PolesCount=3 KnotsCount=2 Degree=2 IsPeriodic=0
    g4: GeomPoint X=0 Y=0 Z=0
    g5: GeomPoint X=8 Y=6 Z=0
    g6: LineSegment StartX=0 StartY=6 StartZ=0 EndX=8 EndY=6 EndZ=0
  constraints (14):
    c: Coincident(g0,g-1)
    c: Distance(g0) = 6
    c: Vertical(g0)
    c: Coincident(g3,g0)
    c: Weight(g1) = 1
    c: Equal(g1,g2)
    c: InternalAlignment(g1,g3)
    c: InternalAlignment(g2,g3)
    c: InternalAlignment(g4,g3)
    c: InternalAlignment(g5,g3)
    c: Block(g3)
    c: Coincident(g6,g0)
    c: Coincident(g6,g3)
    c: Horizontal(g6)
FEATURE [Part::Extrusion] Extrude035  label="caseScrewPillarBracket013"
  Base = -> Sketch044
  Dir = (0,0,1)
  DirMode = 2
  FaceMakerClass = Part::FaceMakerBullseye
  LengthFwd = 2.4
  LengthRev = 0
  Placement = pos=(90.7,29,6.77) rot=(0,-1,0;1.5708rad)
  Solid = true
  Symmetric = false
FEATURE [Sketcher::SketchObject] Sketch045
  FullyConstrained = true
  sketch-geometry (7):
    g0: LineSegment StartX=0 StartY=0 StartZ=0 EndX=0 EndY=6 EndZ=0
    g1: Circle CenterX=0 CenterY=0 CenterZ=0 NormalX=0 NormalY=0 NormalZ=1 AngleXU=0 Radius=1
    g2: Circle CenterX=8 CenterY=6 CenterZ=0 NormalX=0 NormalY=0 NormalZ=1 AngleXU=0 Radius=1
    g3: BSplineCurve PolesCount=3 KnotsCount=2 Degree=2 IsPeriodic=0
    g4: GeomPoint X=0 Y=0 Z=0
    g5: GeomPoint X=8 Y=6 Z=0
    g6: LineSegment StartX=0 StartY=6 StartZ=0 EndX=8 EndY=6 EndZ=0
  constraints (14):
    c: Coincident(g0,g-1)
    c: Distance(g0) = 6
    c: Vertical(g0)
    c: Coincident(g3,g0)
    c: Weight(g1) = 1
    c: Equal(g1,g2)
    c: InternalAlignment(g1,g3)
    c: InternalAlignment(g2,g3)
    c: InternalAlignment(g4,g3)
    c: InternalAlignment(g5,g3)
    c: Block(g3)
    c: Coincident(g6,g0)
    c: Coincident(g6,g3)
    c: Horizontal(g6)
FEATURE [Sketcher::SketchObject] Sketch046
  FullyConstrained = true
  sketch-geometry (7):
    g0: LineSegment StartX=0 StartY=0 StartZ=0 EndX=0 EndY=6 EndZ=0
    g1: Circle CenterX=0 CenterY=0 CenterZ=0 NormalX=0 NormalY=0 NormalZ=1 AngleXU=0 Radius=1
    g2: Circle CenterX=8 CenterY=6 CenterZ=0 NormalX=0 NormalY=0 NormalZ=1 AngleXU=0 Radius=1
    g3: BSplineCurve PolesCount=3 KnotsCount=2 Degree=2 IsPeriodic=0
    g4: GeomPoint X=0 Y=0 Z=0
    g5: GeomPoint X=8 Y=6 Z=0
    g6: LineSegment StartX=0 StartY=6 StartZ=0 EndX=8 EndY=6 EndZ=0
  constraints (14):
    c: Coincident(g0,g-1)
    c: Distance(g0) = 6
    c: Vertical(g0)
    c: Coincident(g3,g0)
    c: Weight(g1) = 1
    c: Equal(g1,g2)
    c: InternalAlignment(g1,g3)
    c: InternalAlignment(g2,g3)
    c: InternalAlignment(g4,g3)
    c: InternalAlignment(g5,g3)
    c: Block(g3)
    c: Coincident(g6,g0)
    c: Coincident(g6,g3)
    c: Horizontal(g6)
FEATURE [Part::Extrusion] Extrude036  label="caseScrewPillarBracket014"
  Base = -> Sketch045
  Dir = (0,0,1)
  DirMode = 2
  FaceMakerClass = Part::FaceMakerBullseye
  LengthFwd = 2.4
  LengthRev = 0
  Placement = pos=(110.7,29,6.77) rot=(0,-1,0;1.5708rad)
  Solid = true
  Symmetric = false
FEATURE [Part::Extrusion] Extrude037  label="caseScrewPillarBracket015"
  Base = -> Sketch046
  Dir = (0,0,1)
  DirMode = 2
  FaceMakerClass = Part::FaceMakerBullseye
  LengthFwd = 2.4
  LengthRev = 0
  Placement = pos=(108.3,29,65.23) rot=(0,1,0;1.5708rad)
  Solid = true
  Symmetric = false
FEATURE [Part::Box] Box013  label="frontCaseScrewPillarBracket002"
  AttacherType = Attacher::AttachEngine3D
  Height = 2.4
  Length = 22
  Placement = pos=(87,28,2.3) rot=(0,0,1;0rad)
  Width = 7
FEATURE [Part::Box] Box014  label="frontCaseScrewPillarBracket003"
  AttacherType = Attacher::AttachEngine3D
  Height = 2.4
  Length = 22
  Placement = pos=(87,28,67.3) rot=(0,0,1;0rad)
  Width = 7
FEATURE [Part::Feature] Face087
  shape: bbox 4.8 x 30.2 x 2e-07 mm, 1 faces, 0 solids (baked)
FEATURE [Part::Revolution] Revolve091  label="frontCaseScrewPost004"
  Angle = 360
  Axis = (0,1,0)
  Base = (0,0,0)
  FaceMakerClass = Part::FaceMakerBullseye
  Placement = pos=(89.5,4.5,3.5) rot=(0,0,1;0rad)
  Solid = false
  Source = -> Face087
  Symmetric = false
FEATURE [Part::Feature] Face088
  shape: bbox 4.8 x 30.2 x 2e-07 mm, 1 faces, 0 solids (baked)
FEATURE [Part::Revolution] Revolve092  label="frontCaseScrewPost005"
  Angle = 360
  Axis = (0,1,0)
  Base = (0,0,0)
  FaceMakerClass = Part::FaceMakerBullseye
  Placement = pos=(89.5,4.5,68.5) rot=(0,0,1;0rad)
  Solid = false
  Source = -> Face088
  Symmetric = false
FEATURE [Part::Feature] Face089
  shape: bbox 3.5 x 30.2 x 2e-07 mm, 1 faces, 0 solids (baked)
FEATURE [Part::Revolution] Revolve093  label="backCaseScrewPost002"
  Angle = 360
  Axis = (0,1,0)
  Base = (0,0,0)
  FaceMakerClass = Part::FaceMakerBullseye
  Placement = pos=(12.5,4.5,10) rot=(0,0,1;0rad)
  Solid = false
  Source = -> Face089
  Symmetric = false
FEATURE [Part::Feature] Face090
  shape: bbox 3.5 x 30.2 x 2e-07 mm, 1 faces, 0 solids (baked)
FEATURE [Part::Revolution] Revolve094  label="backCaseScrewPost003"
  Angle = 360
  Axis = (0,1,0)
  Base = (0,0,0)
  FaceMakerClass = Part::FaceMakerBullseye
  Placement = pos=(12.5,4.5,62) rot=(0,0,1;0rad)
  Solid = false
  Source = -> Face090
  Symmetric = false
FEATURE [Part::Box] Box015  label="Cube011"
  AttacherType = Attacher::AttachEngine3D
  Height = 28.8
  Length = 3
  Placement = pos=(107.3,28,21.6) rot=(0,0,1;0rad)
  Width = 7
FEATURE [Part::Box] Box016  label="Cube012"
  AttacherType = Attacher::AttachEngine3D
  Height = 3
  Length = 7.4
  Placement = pos=(107.3,28,18.6) rot=(0,0,1;0rad)
  Width = 7
FEATURE [Part::Box] Box017  label="Cube013"
  AttacherType = Attacher::AttachEngine3D
  Height = 3
  Length = 7.4
  Placement = pos=(107.3,28,50.4) rot=(0,0,1;0rad)
  Width = 7
FEATURE [Part::Cylinder] Cylinder024
  Angle = 360
  AttacherType = Attacher::AttachEngine3D
  Height = 20
  Placement = pos=(0,0,36.15) rot=(0,0,1;0rad)
  Radius = 14.3
FEATURE [Part::Cylinder] Cylinder025
  Angle = 360
  AttacherType = Attacher::AttachEngine3D
  Height = 10
  Placement = pos=(0,0,36.15) rot=(0,0,1;0rad)
  Radius = 4
FEATURE [Part::MultiFuse] Fusion066  label="removeToCreteHoleForPlugHousing009"
  Placement = pos=(70,19,36) rot=(0,1,0;1.5708rad)
  Shapes = -> [Cylinder024,Cylinder025]
FEATURE [Part::MultiFuse] Fusion065  label="plugHousingBracketHolder002"
  Shapes = -> [Box017,Box015,Box016]
FEATURE [Part::Cut] Cut025  label="plugHousingBracketHolder003"
  Base = -> Fusion065
  Placement = pos=(7,0,0) rot=(0,0,1;0rad)
  Tool = -> Fusion066
FEATURE [Sketcher::SketchObject] Sketch047
  FullyConstrained = false
  Placement = pos=(0,0,0) rot=(1,0,0;1.5708rad)
  sketch-geometry (24):
    g0: ArcOfCircle CenterX=-4 CenterY=-10.5 CenterZ=0 NormalX=0 NormalY=0 NormalZ=1 AngleXU=0 Radius=1.5 StartAngle=6e-16 EndAngle=3.14159
    g1: ArcOfCircle CenterX=-34.2 CenterY=-10.5 CenterZ=0 NormalX=0 NormalY=0 NormalZ=1 AngleXU=0 Radius=1.5 StartAngle=0 EndAngle=3.14159
    g2: ArcOfCircle CenterX=-34.2 CenterY=-27.7 CenterZ=0 NormalX=0 NormalY=0 NormalZ=1 AngleXU=0 Radius=1.5 StartAngle=3.14159 EndAngle=6.28319
    g3: ArcOfCircle CenterX=-4 CenterY=-27.7 CenterZ=0 NormalX=0 NormalY=0 NormalZ=1 AngleXU=0 Radius=1.5 StartAngle=3.1416 EndAngle=6.28319
    g4: ArcOfCircle CenterX=-10 CenterY=-4.3 CenterZ=0 NormalX=0 NormalY=0 NormalZ=1 AngleXU=0 Radius=1.5 StartAngle=2e-16 EndAngle=3.14159
    g5: ArcOfCircle CenterX=-16.1 CenterY=-1.8 CenterZ=0 NormalX=0 NormalY=0 NormalZ=1 AngleXU=0 Radius=1.5 StartAngle=5e-16 EndAngle=3.14159
    g6: ArcOfCircle CenterX=-22.1 CenterY=-1.8 CenterZ=0 NormalX=0 NormalY=0 NormalZ=1 AngleXU=0 Radius=1.5 StartAngle=5e-16 EndAngle=3.14159
    g7: ArcOfCircle CenterX=-28.2 CenterY=-4.3 CenterZ=0 NormalX=0 NormalY=0 NormalZ=1 AngleXU=0 Radius=1.5 StartAngle=2e-16 EndAngle=3.14159
    g8: ArcOfCircle CenterX=-10 CenterY=-33.9 CenterZ=0 NormalX=0 NormalY=0 NormalZ=1 AngleXU=0 Radius=1.5 StartAngle=3.14159 EndAngle=6.28319
    g9: ArcOfCircle CenterX=-16.1 CenterY=-36.4 CenterZ=0 NormalX=0 NormalY=0 NormalZ=1 AngleXU=0 Radius=1.5 StartAngle=3.14159 EndAngle=6.28319
    g10: ArcOfCircle CenterX=-22.1 CenterY=-36.4 CenterZ=0 NormalX=0 NormalY=0 NormalZ=1 AngleXU=0 Radius=1.5 StartAngle=3.14159 EndAngle=6.28319
    g11: ArcOfCircle CenterX=-28.2 CenterY=-33.9 CenterZ=0 NormalX=0 NormalY=0 NormalZ=1 AngleXU=0 Radius=1.5 StartAngle=3.14159 EndAngle=6.28319
    g12: LineSegment StartX=-35.7 StartY=-10.5 StartZ=0 EndX=-35.7 EndY=-27.7 EndZ=0
    g13: LineSegment StartX=-32.7 StartY=-10.5 StartZ=0 EndX=-32.7 EndY=-27.7 EndZ=0
    g14: LineSegment StartX=-29.7 StartY=-33.9 StartZ=0 EndX=-29.7 EndY=-4.3 EndZ=0
    g15: LineSegment StartX=-26.7 StartY=-33.9 StartZ=0 EndX=-26.7 EndY=-4.3 EndZ=0
    g16: LineSegment StartX=-2.5 StartY=-10.5 StartZ=0 EndX=-2.5 EndY=-27.7 EndZ=0
    g17: LineSegment StartX=-8.5 StartY=-4.3 StartZ=0 EndX=-8.5 EndY=-33.9 EndZ=0
    g18: LineSegment StartX=-5.5 StartY=-10.5 StartZ=0 EndX=-5.5 EndY=-27.7 EndZ=0
    g19: LineSegment StartX=-11.5 StartY=-4.3 StartZ=0 EndX=-11.5 EndY=-33.9 EndZ=0
    g20: LineSegment StartX=-14.6 StartY=-1.8 StartZ=0 EndX=-14.6 EndY=-36.4 EndZ=0
    g21: LineSegment StartX=-17.6 StartY=-1.8 StartZ=0 EndX=-17.6 EndY=-36.4 EndZ=0
    g22: LineSegment StartX=-20.6 StartY=-36.4 StartZ=0 EndX=-20.6 EndY=-1.8 EndZ=0
    g23: LineSegment StartX=-23.6 StartY=-1.8 StartZ=0 EndX=-23.6 EndY=-36.4 EndZ=0
  constraints (48):
    c: Block(g0)
    c: Block(g1)
    c: Block(g2)
    c: Block(g3)
    c: Block(g4)
    c: Block(g5)
    c: Block(g6)
    c: Block(g7)
    c: Block(g8)
    c: Block(g9)
    c: Block(g10)
    c: Block(g11)
    c: Coincident(g12,g1)
    c: Coincident(g12,g2)
    c: Vertical(g12)
    c: Coincident(g13,g1)
    c: Coincident(g13,g2)
    c: Vertical(g13)
    c: Coincident(g14,g11)
    c: Coincident(g14,g7)
    c: Vertical(g14)
    c: Coincident(g15,g11)
    c: Coincident(g15,g7)
    c: Vertical(g15)
    c: Coincident(g16,g0)
    c: Coincident(g16,g3)
    c: Vertical(g16)
    c: Coincident(g17,g4)
    c: Coincident(g17,g8)
    c: Vertical(g17)
    c: Coincident(g18,g0)
    c: Coincident(g18,g3)
    c: Vertical(g18)
    c: Coincident(g19,g4)
    c: Coincident(g19,g8)
    c: Vertical(g19)
    c: Coincident(g20,g5)
    c: Coincident(g20,g9)
    c: Vertical(g20)
    c: Coincident(g21,g5)
    c: Coincident(g21,g9)
    c: Vertical(g21)
    c: Coincident(g22,g10)
    c: Coincident(g22,g6)
    c: Vertical(g22)
    c: Coincident(g23,g6)
    c: Coincident(g23,g10)
    c: Vertical(g23)
FEATURE [Part::Extrusion] Extrude038  label="removeToCreateFanGrillHoles001"
  Base = -> Sketch047
  Dir = (0,-1,6e-16)
  DirMode = 2
  FaceMakerClass = Part::FaceMakerBullseye
  LengthFwd = 10
  LengthRev = 0
  Placement = pos=(65.4,44,54.82) rot=(0,0,1;0rad)
  Solid = true
  Symmetric = false
FEATURE [Part::Feature] Wire004
  shape: bbox 11 x 5.2 x 2e-07 mm, 0 faces, 0 solids (baked)
FEATURE [Part::Revolution] Revolve095
  Angle = 360
  Axis = (0,1,0)
  Base = (0,0,0)
  FaceMakerClass = Part::FaceMakerBullseye
  Placement = pos=(30.3,38,19.7) rot=(0,0,1;0rad)
  Solid = true
  Source = -> Wire004
  Symmetric = false
FEATURE [Part::Feature] Wire005
  shape: bbox 11 x 5.2 x 2e-07 mm, 0 faces, 0 solids (baked)
FEATURE [Part::Revolution] Revolve096
  Angle = 360
  Axis = (0,1,0)
  Base = (0,0,0)
  FaceMakerClass = Part::FaceMakerBullseye
  Placement = pos=(30.3,38,51.7) rot=(0,0,1;0rad)
  Solid = true
  Source = -> Wire005
  Symmetric = false
FEATURE [Part::Feature] Wire006
  shape: bbox 11 x 5.2 x 2e-07 mm, 0 faces, 0 solids (baked)
FEATURE [Part::Revolution] Revolve097
  Angle = 360
  Axis = (0,1,0)
  Base = (0,0,0)
  FaceMakerClass = Part::FaceMakerBullseye
  Placement = pos=(62.3,38,51.7) rot=(0,0,1;0rad)
  Solid = true
  Source = -> Wire006
  Symmetric = false
FEATURE [Part::Feature] Wire007
  shape: bbox 11 x 5.2 x 2e-07 mm, 0 faces, 0 solids (baked)
FEATURE [Part::Revolution] Revolve098
  Angle = 360
  Axis = (0,1,0)
  Base = (0,0,0)
  FaceMakerClass = Part::FaceMakerBullseye
  Placement = pos=(62.3,38,19.7) rot=(0,0,1;0rad)
  Solid = true
  Source = -> Wire007
  Symmetric = false
FEATURE [Part::MultiFuse] Fusion067  label="fanScrewHousing002"
  Shapes = -> [Revolve098,Revolve097,Revolve096,Revolve095]
FEATURE [Part::Feature] Face091 .. Face094  x4 (patterned run collapsed; names and placements below)
  shape: bbox 3.5 x 17.8 x 2e-07 mm, 1 faces, 0 solids (baked)
FEATURE [Part::Revolution] Revolve099  label="removeToCreateScrewAndThreadedInsertHole026"
  Angle = 360
  Axis = (0,1,0)
  Base = (0,0,0)
  FaceMakerClass = Part::FaceMakerBullseye
  Placement = pos=(62.3,30.3,19.7) rot=(0,0,1;0rad)
  Solid = false
  Source = -> Face091
  Symmetric = false
FEATURE [Part::Revolution] Revolve100  label="removeToCreateScrewAndThreadedInsertHole027"
  Angle = 360
  Axis = (0,1,0)
  Base = (0,0,0)
  FaceMakerClass = Part::FaceMakerBullseye
  Placement = pos=(62.3,30.3,51.7) rot=(0,0,1;0rad)
  Solid = false
  Source = -> Face092
  Symmetric = false
FEATURE [Part::Revolution] Revolve101  label="removeToCreateScrewAndThreadedInsertHole028"
  Angle = 360
  Axis = (0,1,0)
  Base = (0,0,0)
  FaceMakerClass = Part::FaceMakerBullseye
  Placement = pos=(30.3,30.3,19.7) rot=(0,0,1;0rad)
  Solid = false
  Source = -> Face093
  Symmetric = false
FEATURE [Part::Revolution] Revolve102  label="removeToCreateScrewAndThreadedInsertHole029"
  Angle = 360
  Axis = (0,1,0)
  Base = (0,0,0)
  FaceMakerClass = Part::FaceMakerBullseye
  Placement = pos=(30.3,30.3,51.7) rot=(0,0,1;0rad)
  Solid = false
  Source = -> Face094
  Symmetric = false
FEATURE [Part::MultiFuse] Fusion068  label="createThreadedInsertHolesForFan002"
  Shapes = -> [Revolve099,Revolve100,Revolve101,Revolve102]
FEATURE [Part::Cut] Cut026  label="fanScrewHousing003"
  Base = -> Fusion067
  Tool = -> Fusion068
FEATURE [Sketcher::SketchObject] Sketch048
  FullyConstrained = false
  Placement = pos=(0,0,0) rot=(1,0,0;1.5708rad)
  sketch-geometry (24):
    g0: ArcOfCircle CenterX=-4 CenterY=-10.5 CenterZ=0 NormalX=0 NormalY=0 NormalZ=1 AngleXU=0 Radius=1.5 StartAngle=6e-16 EndAngle=3.14159
    g1: ArcOfCircle CenterX=-34.2 CenterY=-10.5 CenterZ=0 NormalX=0 NormalY=0 NormalZ=1 AngleXU=0 Radius=1.5 StartAngle=0 EndAngle=3.14159
    g2: ArcOfCircle CenterX=-34.2 CenterY=-27.7 CenterZ=0 NormalX=0 NormalY=0 NormalZ=1 AngleXU=0 Radius=1.5 StartAngle=3.14159 EndAngle=6.28319
    g3: ArcOfCircle CenterX=-4 CenterY=-27.7 CenterZ=0 NormalX=0 NormalY=0 NormalZ=1 AngleXU=0 Radius=1.5 StartAngle=3.1416 EndAngle=6.28319
    g4: ArcOfCircle CenterX=-10 CenterY=-4.3 CenterZ=0 NormalX=0 NormalY=0 NormalZ=1 AngleXU=0 Radius=1.5 StartAngle=2e-16 EndAngle=3.14159
    g5: ArcOfCircle CenterX=-16.1 CenterY=-1.8 CenterZ=0 NormalX=0 NormalY=0 NormalZ=1 AngleXU=0 Radius=1.5 StartAngle=5e-16 EndAngle=3.14159
    g6: ArcOfCircle CenterX=-22.1 CenterY=-1.8 CenterZ=0 NormalX=0 NormalY=0 NormalZ=1 AngleXU=0 Radius=1.5 StartAngle=5e-16 EndAngle=3.14159
    g7: ArcOfCircle CenterX=-28.2 CenterY=-4.3 CenterZ=0 NormalX=0 NormalY=0 NormalZ=1 AngleXU=0 Radius=1.5 StartAngle=2e-16 EndAngle=3.14159
    g8: ArcOfCircle CenterX=-10 CenterY=-33.9 CenterZ=0 NormalX=0 NormalY=0 NormalZ=1 AngleXU=0 Radius=1.5 StartAngle=3.14159 EndAngle=6.28319
    g9: ArcOfCircle CenterX=-16.1 CenterY=-36.4 CenterZ=0 NormalX=0 NormalY=0 NormalZ=1 AngleXU=0 Radius=1.5 StartAngle=3.14159 EndAngle=6.28319
    g10: ArcOfCircle CenterX=-22.1 CenterY=-36.4 CenterZ=0 NormalX=0 NormalY=0 NormalZ=1 AngleXU=0 Radius=1.5 StartAngle=3.14159 EndAngle=6.28319
    g11: ArcOfCircle CenterX=-28.2 CenterY=-33.9 CenterZ=0 NormalX=0 NormalY=0 NormalZ=1 AngleXU=0 Radius=1.5 StartAngle=3.14159 EndAngle=6.28319
    g12: LineSegment StartX=-35.7 StartY=-10.5 StartZ=0 EndX=-35.7 EndY=-27.7 EndZ=0
    g13: LineSegment StartX=-32.7 StartY=-10.5 StartZ=0 EndX=-32.7 EndY=-27.7 EndZ=0
    g14: LineSegment StartX=-29.7 StartY=-33.9 StartZ=0 EndX=-29.7 EndY=-4.3 EndZ=0
    g15: LineSegment StartX=-26.7 StartY=-33.9 StartZ=0 EndX=-26.7 EndY=-4.3 EndZ=0
    g16: LineSegment StartX=-2.5 StartY=-10.5 StartZ=0 EndX=-2.5 EndY=-27.7 EndZ=0
    g17: LineSegment StartX=-8.5 StartY=-4.3 StartZ=0 EndX=-8.5 EndY=-33.9 EndZ=0
    g18: LineSegment StartX=-5.5 StartY=-10.5 StartZ=0 EndX=-5.5 EndY=-27.7 EndZ=0
    g19: LineSegment StartX=-11.5 StartY=-4.3 StartZ=0 EndX=-11.5 EndY=-33.9 EndZ=0
    g20: LineSegment StartX=-14.6 StartY=-1.8 StartZ=0 EndX=-14.6 EndY=-36.4 EndZ=0
    g21: LineSegment StartX=-17.6 StartY=-1.8 StartZ=0 EndX=-17.6 EndY=-36.4 EndZ=0
    g22: LineSegment StartX=-20.6 StartY=-36.4 StartZ=0 EndX=-20.6 EndY=-1.8 EndZ=0
    g23: LineSegment StartX=-23.6 StartY=-1.8 StartZ=0 EndX=-23.6 EndY=-36.4 EndZ=0
  constraints (48):
    c: Block(g0)
    c: Block(g1)
    c: Block(g2)
    c: Block(g3)
    c: Block(g4)
    c: Block(g5)
    c: Block(g6)
    c: Block(g7)
    c: Block(g8)
    c: Block(g9)
    c: Block(g10)
    c: Block(g11)
    c: Coincident(g12,g1)
    c: Coincident(g12,g2)
    c: Vertical(g12)
    c: Coincident(g13,g1)
    c: Coincident(g13,g2)
    c: Vertical(g13)
    c: Coincident(g14,g11)
    c: Coincident(g14,g7)
    c: Vertical(g14)
    c: Coincident(g15,g11)
    c: Coincident(g15,g7)
    c: Vertical(g15)
    c: Coincident(g16,g0)
    c: Coincident(g16,g3)
    c: Vertical(g16)
    c: Coincident(g17,g4)
    c: Coincident(g17,g8)
    c: Vertical(g17)
    c: Coincident(g18,g0)
    c: Coincident(g18,g3)
    c: Vertical(g18)
    c: Coincident(g19,g4)
    c: Coincident(g19,g8)
    c: Vertical(g19)
    c: Coincident(g20,g5)
    c: Coincident(g20,g9)
    c: Vertical(g20)
    c: Coincident(g21,g5)
    c: Coincident(g21,g9)
    c: Vertical(g21)
    c: Coincident(g22,g10)
    c: Coincident(g22,g6)
    c: Vertical(g22)
    c: Coincident(g23,g6)
    c: Coincident(g23,g10)
    c: Vertical(g23)
FEATURE [Part::Extrusion] Extrude039  label="removeToCreateFanGrillHoles002"
  Base = -> Sketch048
  Dir = (0,-1,6e-16)
  DirMode = 2
  FaceMakerClass = Part::FaceMakerBullseye
  LengthFwd = 10
  LengthRev = 0
  Placement = pos=(65.4,44,54.82) rot=(0,0,1;0rad)
  Solid = true
  Symmetric = false
FEATURE [Part::Cut] Cut027  label="fanScrewHousing004"
  Base = -> Cut026
  Tool = -> Extrude038
FEATURE [Part::Cut] Cut028  label="top014"
  Base = -> Fillet026
  Tool = -> Extrude039
FEATURE [Part::Feature] Face095 .. Face098  x4 (patterned run collapsed; names and placements below)
  shape: bbox 3.5 x 17.8 x 2e-07 mm, 1 faces, 0 solids (baked)
FEATURE [Part::Revolution] Revolve103  label="removeToCreateScrewAndThreadedInsertHole030"
  Angle = 360
  Axis = (0,1,0)
  Base = (0,0,0)
  FaceMakerClass = Part::FaceMakerBullseye
  Placement = pos=(62.3,30.3,19.7) rot=(0,0,1;0rad)
  Solid = false
  Source = -> Face095
  Symmetric = false
FEATURE [Part::Revolution] Revolve104  label="removeToCreateScrewAndThreadedInsertHole031"
  Angle = 360
  Axis = (0,1,0)
  Base = (0,0,0)
  FaceMakerClass = Part::FaceMakerBullseye
  Placement = pos=(62.3,30.3,51.7) rot=(0,0,1;0rad)
  Solid = false
  Source = -> Face096
  Symmetric = false
FEATURE [Part::Revolution] Revolve105  label="removeToCreateScrewAndThreadedInsertHole032"
  Angle = 360
  Axis = (0,1,0)
  Base = (0,0,0)
  FaceMakerClass = Part::FaceMakerBullseye
  Placement = pos=(30.3,30.3,19.7) rot=(0,0,1;0rad)
  Solid = false
  Source = -> Face097
  Symmetric = false
FEATURE [Part::Revolution] Revolve106  label="removeToCreateScrewAndThreadedInsertHole033"
  Angle = 360
  Axis = (0,1,0)
  Base = (0,0,0)
  FaceMakerClass = Part::FaceMakerBullseye
  Placement = pos=(30.3,30.3,51.7) rot=(0,0,1;0rad)
  Solid = false
  Source = -> Face098
  Symmetric = false
FEATURE [Part::MultiFuse] Fusion069  label="createThreadedInsertHolesForFan003"
  Shapes = -> [Revolve103,Revolve104,Revolve105,Revolve106]
FEATURE [Part::Cut] Cut029  label="top015"
  Base = -> Cut028
  Tool = -> Fusion054
FEATURE [Part::Cut] Cut030  label="fanScrewHousing005"
  Base = -> Cut027
  Tool = -> Fusion069
FEATURE [Part::Cylinder] Cylinder026  label="removeToCreteHoleForPlugHousing010"
  Angle = 360
  AttacherType = Attacher::AttachEngine3D
  Height = 20
  Placement = pos=(-2,19,36) rot=(0,1,0;1.5708rad)
  Radius = 14.3
FEATURE [Part::Box] Box018  label="removeToCreteHoleForPlugHousing011"
  AttacherType = Attacher::AttachEngine3D
  Height = 28.6
  Length = 10
  Placement = pos=(-2,0,21.7) rot=(0,0,1;0rad)
  Width = 19
FEATURE [Part::Box] Box019  label="wireHolderBottomCaseBit"
  AttacherType = Attacher::AttachEngine3D
  Height = 28
  Length = 3
  Placement = pos=(0,0,22) rot=(0,0,1;0rad)
  Width = 21
FEATURE [Part::Cylinder] Cylinder027  label="removeToCreteHoleForPlugHousing012"
  Angle = 360
  AttacherType = Attacher::AttachEngine3D
  Height = 20
  Placement = pos=(-2,19,36) rot=(0,1,0;1.5708rad)
  Radius = 14.3
FEATURE [Part::Cut] Cut031  label="wireHolderBottomCaseBit001"
  Base = -> Box019
  Tool = -> Cylinder027
FEATURE [Part::MultiFuse] Fusion070  label="removeToCreteHoleForPlugHousing013"
  Shapes = -> [Box018,Cylinder026]
FEATURE [Part::Cut] Cut032  label="top016"
  Base = -> Cut029
  Tool = -> Fusion070
FEATURE [Part::Cylinder] Cylinder028
  Angle = 360
  AttacherType = Attacher::AttachEngine3D
  Height = 20
  Placement = pos=(0,0,36.15) rot=(0,0,1;0rad)
  Radius = 14.3
FEATURE [Part::Cylinder] Cylinder029
  Angle = 360
  AttacherType = Attacher::AttachEngine3D
  Height = 10
  Placement = pos=(0,0,36.15) rot=(0,0,1;0rad)
  Radius = 4
FEATURE [Part::MultiFuse] Fusion071  label="removeToCreteHoleForPlugHousing014"
  Placement = pos=(70,19,36) rot=(0,1,0;1.5708rad)
  Shapes = -> [Cylinder028,Cylinder029]
FEATURE [Sketcher::SketchObject] Sketch049  label="topSketch011"
  FullyConstrained = true
  sketch-geometry (4):
    g0: ArcOfCircle CenterX=105 CenterY=19 CenterZ=0 NormalX=0 NormalY=0 NormalZ=1 AngleXU=0 Radius=20.6155 StartAngle=5.54125 EndAngle=6.28319
    g1: ArcOfCircle CenterX=105 CenterY=19 CenterZ=0 NormalX=0 NormalY=0 NormalZ=1 AngleXU=0 Radius=13 StartAngle=5.54125 EndAngle=6.28319
    g2: LineSegment StartX=118 StartY=19 StartZ=0 EndX=125.616 EndY=19 EndZ=0
    g3: LineSegment StartX=114.583 StartY=10.2157 StartZ=0 EndX=120.197 EndY=5.06982 EndZ=0
  constraints (7):
    c: Block(g0)
    c: Block(g1)
    c: Coincident(g2,g1)
    c: Coincident(g2,g0)
    c: Horizontal(g2)
    c: Coincident(g3,g1)
    c: Coincident(g3,g0)
FEATURE [Part::Box] Box020  label="removeToCreteHoleForPlugHousing015"
  AttacherType = Attacher::AttachEngine3D
  Height = 28.6
  Length = 20
  Placement = pos=(106.15,0,21.7) rot=(0,0,1;0rad)
  Width = 19
FEATURE [Part::MultiFuse] Fusion072  label="removeToCreteHoleForPlugHousing016"
  Shapes = -> [Box020,Fusion071]
FEATURE [Part::Cut] Cut033  label="removeToCreteHoleForPlugHousing017"
  Base = -> Cut032
  Tool = -> Fusion072
FEATURE [Part::Cylinder] Cylinder030
  Angle = 360
  AttacherType = Attacher::AttachEngine3D
  Height = 20
  Placement = pos=(0,0,36.15) rot=(0,0,1;0rad)
  Radius = 14.3
FEATURE [Part::Cylinder] Cylinder031
  Angle = 360
  AttacherType = Attacher::AttachEngine3D
  Height = 10
  Placement = pos=(0,0,36.15) rot=(0,0,1;0rad)
  Radius = 4
FEATURE [Part::Box] Box021  label="removeToCreteHoleForPlugHousing019"
  AttacherType = Attacher::AttachEngine3D
  Height = 28.6
  Length = 20
  Placement = pos=(106.15,0,21.7) rot=(0,0,1;0rad)
  Width = 19
FEATURE [Part::MultiFuse] Fusion074  label="removeToCreteHoleForPlugHousing020"
  Placement = pos=(70,19,36) rot=(0,1,0;1.5708rad)
  Shapes = -> [Cylinder030,Cylinder031]
FEATURE [Part::MultiFuse] Fusion073  label="removeToCreteHoleForPlugHousing018"
  Placement = pos=(0,0,28.3) rot=(0,0,1;0rad)
  Shapes = -> [Box021,Fusion074]
FEATURE [Part::Cylinder] Cylinder032
  Angle = 360
  AttacherType = Attacher::AttachEngine3D
  Height = 20
  Placement = pos=(0,0,36.15) rot=(0,0,1;0rad)
  Radius = 14.3
FEATURE [Part::Cylinder] Cylinder033
  Angle = 360
  AttacherType = Attacher::AttachEngine3D
  Height = 10
  Placement = pos=(0,0,36.15) rot=(0,0,1;0rad)
  Radius = 4
FEATURE [Part::Box] Box022  label="removeToCreteHoleForPlugHousing021"
  AttacherType = Attacher::AttachEngine3D
  Height = 28.6
  Length = 20
  Placement = pos=(106.15,0,21.7) rot=(0,0,1;0rad)
  Width = 19
FEATURE [Part::MultiFuse] Fusion076  label="removeToCreteHoleForPlugHousing023"
  Placement = pos=(70,19,36) rot=(0,1,0;1.5708rad)
  Shapes = -> [Cylinder032,Cylinder033]
FEATURE [Part::MultiFuse] Fusion075  label="removeToCreteHoleForPlugHousing022"
  Placement = pos=(0,0,-28.3) rot=(0,0,1;0rad)
  Shapes = -> [Box022,Fusion076]
FEATURE [Part::MultiFuse] Fusion077  label="removeToCreatePlugHousingBottomBit"
  Shapes = -> [Fusion075,Fusion073]
FEATURE [Part::Cylinder] Cylinder034
  Angle = 360
  AttacherType = Attacher::AttachEngine3D
  Height = 20
  Placement = pos=(0,0,36.15) rot=(0,0,1;0rad)
  Radius = 14
FEATURE [Part::Cylinder] Cylinder035
  Angle = 360
  AttacherType = Attacher::AttachEngine3D
  Height = 10
  Placement = pos=(0,0,36.15) rot=(0,0,1;0rad)
  Radius = 4
FEATURE [Part::MultiFuse] Fusion078  label="removeToCreteHoleForPlugHousing024"
  Placement = pos=(70,19,36) rot=(0,1,0;1.5708rad)
  Shapes = -> [Cylinder034,Cylinder035]
FEATURE [Part::MultiFuse] Fusion079  label="removeToCreatePlugHousingBottomBit001"
  Shapes = -> [Fusion078,Fusion077]
FEATURE [Part::Extrusion] Extrude040  label="bottomPlugHousingBit"
  Base = -> Sketch049
  Dir = (0,0,1)
  DirMode = 2
  FaceMakerClass = Part::FaceMakerBullseye
  LengthFwd = 72
  LengthRev = 0
  Solid = true
  Symmetric = false
FEATURE [Part::Cut] Cut034  label="bottomPlugHousingBit001"
  Base = -> Extrude040
  Placement = pos=(-0.09,0,0) rot=(0,0,1;0rad)
  Tool = -> Fusion079
FEATURE [Part::Box] Box023  label="Cube014"
  AttacherType = Attacher::AttachEngine3D
  Height = 16
  Length = 8
  Placement = pos=(12.7,31.52,28) rot=(0,0,1;0rad)
  Width = 4
FEATURE [Part::Cylinder] Cylinder036
  Angle = 360
  AttacherType = Attacher::AttachEngine3D
  Height = 10
  Placement = pos=(0,0,36.15) rot=(0,0,1;0rad)
  Radius = 4
FEATURE [Part::Cylinder] Cylinder037
  Angle = 360
  AttacherType = Attacher::AttachEngine3D
  Height = 20
  Placement = pos=(0,0,36.15) rot=(0,0,1;0rad)
  Radius = 8.2
FEATURE [Part::MultiFuse] Fusion080  label="removeToCreteHoleForPlugHousing025"
  Placement = pos=(-42,19,36) rot=(0,1,0;1.5708rad)
  Shapes = -> [Cylinder037,Cylinder036]
FEATURE [Sketcher::SketchObject] Sketch050  label="topSketch012"
  FullyConstrained = true
  sketch-geometry (4):
    g0: LineSegment StartX=16.8446 StartY=31.512 StartZ=0 EndX=16.3251 EndY=34.4666 EndZ=0
    g1: ArcOfCircle CenterX=19 CenterY=19.2524 CenterZ=0 NormalX=0 NormalY=0 NormalZ=1 AngleXU=0 Radius=15.4476 StartAngle=1.74483 EndAngle=2.72717
    g2: ArcOfCircle CenterX=19 CenterY=19.2524 CenterZ=0 NormalX=0 NormalY=0 NormalZ=1 AngleXU=0 Radius=12.4476 StartAngle=1.74483 EndAngle=2.73189
    g3: LineSegment StartX=4.86004 StartY=25.4725 StartZ=0 EndX=7.58253 EndY=24.2107 EndZ=0
  constraints (7):
    c: Block(g0)
    c: Coincident(g1,g0)
    c: Coincident(g2,g0)
    c: Coincident(g3,g1)
    c: Coincident(g3,g2)
    c: Block(g1)
    c: Block(g2)
FEATURE [Part::Extrusion] Extrude041
  Base = -> Sketch050
  Dir = (0,0,1)
  DirMode = 2
  FaceMakerClass = Part::FaceMakerBullseye
  LengthFwd = 10.6
  LengthRev = 0
  Placement = pos=(0,0,31) rot=(0,0,1;0rad)
  Solid = true
  Symmetric = false
FEATURE [Part::Cut] Cut035
  Base = -> Extrude041
  Placement = pos=(0,0,-0.3) rot=(0,0,1;0rad)
  Tool = -> Fusion080
FEATURE [Part::Cut] Cut036
  Base = -> Box023
  Tool = -> Cut035
FEATURE [Part::Fillet] Fillet027
  Base = -> Cut036
  Edges = 1 edges r=0.7: [Edge13]
FEATURE [Part::Fillet] Fillet028
  Base = -> Fillet027
  Edges = 1 edges r=0.7: [Edge13]
FEATURE [Part::Fillet] Fillet029
  Base = -> Fillet028
  Edges = 1 edges r=0.7: [Edge16]
FEATURE [Part::Fillet] Fillet030
  Base = -> Fillet029
  Edges = 1 edges r=0.7: [Edge11]
FEATURE [Part::Fillet] Fillet031
  Base = -> Fillet030
  Edges = 1 edges r=0.7: [Edge10]
FEATURE [Part::Fillet] Fillet032
  Base = -> Fillet031
  Edges = 1 edges r=1.2: [Edge5]
FEATURE [Part::Fillet] Fillet033
  Base = -> Fillet032
  Edges = 1 edges r=1.2: [Edge12]
FEATURE [Part::Fillet] Fillet034  label="wireHousingRetainer"
  Base = -> Fillet033
  Edges = 1 edges r=2: [Edge1]
  Placement = pos=(0.3,0,0) rot=(0,0,1;0rad)
FEATURE [Part::Feature] Face099
  shape: bbox 3.5 x 17.8 x 2e-07 mm, 1 faces, 0 solids (baked)
FEATURE [Part::Revolution] Revolve107  label="removeToCreateScrewAndThreadedInsertHole034"
  Angle = 360
  Axis = (0,1,0)
  Base = (0,0,0)
  FaceMakerClass = Part::FaceMakerBullseye
  Placement = pos=(12.5,0,10) rot=(0,0,1;0rad)
  Solid = false
  Source = -> Face099
  Symmetric = false
FEATURE [Part::Feature] Face100
  shape: bbox 3.5 x 17.8 x 2e-07 mm, 1 faces, 0 solids (baked)
FEATURE [Part::Revolution] Revolve108  label="removeToCreateScrewAndThreadedInsertHole035"
  Angle = 360
  Axis = (0,1,0)
  Base = (0,0,0)
  FaceMakerClass = Part::FaceMakerBullseye
  Placement = pos=(12.5,0,62) rot=(0,0,1;0rad)
  Solid = false
  Source = -> Face100
  Symmetric = false
FEATURE [Part::Feature] Face101
  shape: bbox 3.5 x 17.8 x 2e-07 mm, 1 faces, 0 solids (baked)
FEATURE [Part::Revolution] Revolve109  label="removeToCreateScrewAndThreadedInsertHole036"
  Angle = 360
  Axis = (0,1,0)
  Base = (0,0,0)
  FaceMakerClass = Part::FaceMakerBullseye
  Placement = pos=(89.5,0,68.5) rot=(0,0,1;0rad)
  Solid = false
  Source = -> Face101
  Symmetric = false
FEATURE [Part::Feature] Face102
  shape: bbox 3.5 x 17.8 x 2e-07 mm, 1 faces, 0 solids (baked)
FEATURE [Part::Revolution] Revolve110  label="removeToCreateScrewAndThreadedInsertHole037"
  Angle = 360
  Axis = (0,1,0)
  Base = (0,0,0)
  FaceMakerClass = Part::FaceMakerBullseye
  Placement = pos=(89.5,0,3.5) rot=(0,0,1;0rad)
  Solid = false
  Source = -> Face102
  Symmetric = false
FEATURE [Part::Feature] Face103
  shape: bbox 3.5 x 17.8 x 2e-07 mm, 1 faces, 0 solids (baked)
FEATURE [Part::Revolution] Revolve111  label="removeToCreateScrewAndThreadedInsertHole038"
  Angle = 360
  Axis = (0,1,0)
  Base = (0,0,0)
  FaceMakerClass = Part::FaceMakerBullseye
  Placement = pos=(109.5,4.7,3.5) rot=(0,0,1;0rad)
  Solid = false
  Source = -> Face103
  Symmetric = false
FEATURE [Part::Feature] Face104
  shape: bbox 3.5 x 17.8 x 2e-07 mm, 1 faces, 0 solids (baked)
FEATURE [Part::Revolution] Revolve112  label="removeToCreateScrewAndThreadedInsertHole039"
  Angle = 360
  Axis = (0,1,0)
  Base = (0,0,0)
  FaceMakerClass = Part::FaceMakerBullseye
  Placement = pos=(109.5,4.7,68.5) rot=(0,0,1;0rad)
  Solid = false
  Source = -> Face104
  Symmetric = false
FEATURE [Part::MultiFuse] Fusion081  label="removeToCreateScrewAndThreadedInsertHole040"
  Shapes = -> [Revolve107,Revolve108,Revolve109,Revolve110,Revolve111,Revolve112]
FEATURE [Part::MultiFuse] Fusion082  label="casePillars002"
  Shapes = -> [Revolve094,Revolve092,Revolve090,Revolve089,Revolve091,Revolve093]
FEATURE [Part::Cut] Cut037  label="casePillars003"
  Base = -> Fusion082
  Tool = -> Fusion081
FEATURE [Sketcher::SketchObject] Sketch051
  FullyConstrained = true
  Placement = pos=(117,19,0) rot=(0.57735,0.57735,0.57735;2.0944rad)
  sketch-geometry (48):
    g0: LineSegment StartX=-49.19 StartY=69.25 StartZ=0 EndX=-49.19 EndY=66.25 EndZ=0
    g1: LineSegment StartX=-49.19 StartY=63.5 StartZ=0 EndX=-49.19 EndY=60.5 EndZ=0
    g2: LineSegment StartX=-49.19 StartY=57.75 StartZ=0 EndX=-49.19 EndY=54.75 EndZ=0
    g3: LineSegment StartX=-49.19 StartY=52 StartZ=0 EndX=-49.19 EndY=49 EndZ=0
    g4: LineSegment StartX=-49.19 StartY=46.25 StartZ=0 EndX=-49.19 EndY=43.25 EndZ=0
    g5: LineSegment StartX=-49.19 StartY=40.5 StartZ=0 EndX=-49.19 EndY=37.5 EndZ=0
    g6: LineSegment StartX=-49.19 StartY=34.5 StartZ=0 EndX=-49.19 EndY=31.5 EndZ=0
    g7: LineSegment StartX=-49.19 StartY=28.75 StartZ=0 EndX=-49.19 EndY=25.75 EndZ=0
    g8: LineSegment StartX=-49.19 StartY=23 StartZ=0 EndX=-49.19 EndY=20 EndZ=0
    g9: LineSegment StartX=-49.19 StartY=17.25 StartZ=0 EndX=-49.19 EndY=14.25 EndZ=0
    g10: LineSegment StartX=-49.19 StartY=11.5 StartZ=0 EndX=-49.19 EndY=8.5 EndZ=0
    g11: LineSegment StartX=-49.19 StartY=5.75 StartZ=0 EndX=-49.19 EndY=2.75 EndZ=0
    g12: ArcOfCircle CenterX=-1.5 CenterY=67.75 CenterZ=0 NormalX=0 NormalY=0 NormalZ=1 AngleXU=0 Radius=1.5 StartAngle=4.71239 EndAngle=7.85398
    g13: ArcOfCircle CenterX=-1.5 CenterY=62 CenterZ=0 NormalX=0 NormalY=0 NormalZ=1 AngleXU=0 Radius=1.5 StartAngle=4.71239 EndAngle=7.85398
    g14: ArcOfCircle CenterX=-1.5 CenterY=56.25 CenterZ=0 NormalX=0 NormalY=0 NormalZ=1 AngleXU=0 Radius=1.5 StartAngle=4.71239 EndAngle=7.85398
    g15: ArcOfCircle CenterX=-11.49 CenterY=50.5 CenterZ=0 NormalX=0 NormalY=0 NormalZ=1 AngleXU=0 Radius=1.5 StartAngle=4.71239 EndAngle=7.85398
    g16: ArcOfCircle CenterX=-16.28 CenterY=44.75 CenterZ=0 NormalX=0 NormalY=0 NormalZ=1 AngleXU=0 Radius=1.5 StartAngle=4.71239 EndAngle=7.85398
    g17: ArcOfCircle CenterX=-18.2337 CenterY=39 CenterZ=0 NormalX=0 NormalY=0 NormalZ=1 AngleXU=0 Radius=1.5 StartAngle=4.71485 EndAngle=7.85398
    g18: ArcOfCircle CenterX=-16.2837 CenterY=27.25 CenterZ=0 NormalX=0 NormalY=0 NormalZ=1 AngleXU=0 Radius=1.5 StartAngle=4.71485 EndAngle=7.85398
    g19: ArcOfCircle CenterX=-18.2337 CenterY=33 CenterZ=0 NormalX=0 NormalY=0 NormalZ=1 AngleXU=0 Radius=1.5 StartAngle=4.71485 EndAngle=7.85398
    g20: ArcOfCircle CenterX=-11.49 CenterY=21.5 CenterZ=0 NormalX=0 NormalY=0 NormalZ=1 AngleXU=0 Radius=1.5 StartAngle=4.71239 EndAngle=7.85398
    g21: ArcOfCircle CenterX=-1.5 CenterY=4.25 CenterZ=0 NormalX=0 NormalY=0 NormalZ=1 AngleXU=0 Radius=1.5 StartAngle=4.71239 EndAngle=7.85398
    g22: ArcOfCircle CenterX=-1.5 CenterY=10 CenterZ=0 NormalX=0 NormalY=0 NormalZ=1 AngleXU=0 Radius=1.5 StartAngle=4.71239 EndAngle=7.85398
    g23: ArcOfCircle CenterX=-1.5 CenterY=15.75 CenterZ=0 NormalX=0 NormalY=0 NormalZ=1 AngleXU=0 Radius=1.5 StartAngle=4.71239 EndAngle=7.85398
    g24: LineSegment StartX=-49.19 StartY=69.25 StartZ=0 EndX=-1.5 EndY=69.25 EndZ=0
    g25: LineSegment StartX=-49.19 StartY=66.25 StartZ=0 EndX=-1.5 EndY=66.25 EndZ=0
    g26: LineSegment StartX=-49.19 StartY=63.5 StartZ=0 EndX=-1.5 EndY=63.5 EndZ=0
    g27: LineSegment StartX=-49.19 StartY=60.5 StartZ=0 EndX=-1.5 EndY=60.5 EndZ=0
    g28: LineSegment StartX=-49.19 StartY=57.75 StartZ=0 EndX=-1.5 EndY=57.75 EndZ=0
    g29: LineSegment StartX=-49.19 StartY=54.75 StartZ=0 EndX=-1.5 EndY=54.75 EndZ=0
    g30: LineSegment StartX=-49.19 StartY=52 StartZ=0 EndX=-11.49 EndY=52 EndZ=0
    g31: LineSegment StartX=-49.19 StartY=49 StartZ=0 EndX=-11.49 EndY=49 EndZ=0
    g32: LineSegment StartX=-49.19 StartY=46.25 StartZ=0 EndX=-16.28 EndY=46.25 EndZ=0
    g33: LineSegment StartX=-49.19 StartY=43.25 StartZ=0 EndX=-16.28 EndY=43.25 EndZ=0
    g34: LineSegment StartX=-49.19 StartY=40.5 StartZ=0 EndX=-18.2337 EndY=40.5 EndZ=0
    g35: LineSegment StartX=-49.19 StartY=37.5 StartZ=0 EndX=-18.23 EndY=37.5 EndZ=0
    g36: LineSegment StartX=-49.19 StartY=34.5 StartZ=0 EndX=-18.2337 EndY=34.5 EndZ=0
    g37: LineSegment StartX=-49.19 StartY=31.5 StartZ=0 EndX=-18.23 EndY=31.5 EndZ=0
    g38: LineSegment StartX=-49.19 StartY=28.75 StartZ=0 EndX=-16.2837 EndY=28.75 EndZ=0
    g39: LineSegment StartX=-49.19 StartY=25.75 StartZ=0 EndX=-16.28 EndY=25.75 EndZ=0
    g40: LineSegment StartX=-49.19 StartY=23 StartZ=0 EndX=-11.49 EndY=23 EndZ=0
    g41: LineSegment StartX=-49.19 StartY=20 StartZ=0 EndX=-11.49 EndY=20 EndZ=0
    g42: LineSegment StartX=-49.19 StartY=17.25 StartZ=0 EndX=-1.5 EndY=17.25 EndZ=0
    g43: LineSegment StartX=-49.19 StartY=14.25 StartZ=0 EndX=-1.5 EndY=14.25 EndZ=0
    g44: LineSegment StartX=-49.19 StartY=11.5 StartZ=0 EndX=-1.5 EndY=11.5 EndZ=0
    g45: LineSegment StartX=-49.19 StartY=8.5 StartZ=0 EndX=-1.5 EndY=8.5 EndZ=0
    g46: LineSegment StartX=-49.19 StartY=5.75 StartZ=0 EndX=-1.5 EndY=5.75 EndZ=0
    g47: LineSegment StartX=-49.19 StartY=2.75 StartZ=0 EndX=-1.5 EndY=2.75 EndZ=0
  constraints (120):
    c: Vertical(g0)
    c: Distance(g0) = 3
    c: Block(g0)
    c: Vertical(g1)
    c: Distance(g1) = 3
    c: Vertical(g2)
    c: Equal(g0,g2) = 3
    c: Block(g2)
    c: Vertical(g3)
    c: Equal(g1,g3) = 3
    c: Vertical(g4)
    c: Equal(g0,g4) = 3
    c: Block(g4)
    c: Vertical(g5)
    c: Equal(g1,g5) = 3
    c: Vertical(g6)
    c: Equal(g0,g6) = 3
    c: Block(g6)
    c: Vertical(g7)
    c: Equal(g1,g7) = 3
    c: Vertical(g8)
    c: Equal(g0,g8) = 3
    c: Block(g8)
    c: Vertical(g9)
    c: Equal(g1,g9) = 3
    c: Vertical(g10)
    c: Equal(g0,g10) = 3
    c: Block(g10)
    c: Vertical(g11)
    c: Equal(g1,g11) = 3
    c: Block(g12)
    c: Block(g13)
    c: Block(g14)
    c: Block(g15)
    c: Block(g16)
    c: Block(g17)
    c: Block(g18)
    c: Block(g19)
    c: Block(g20)
    c: Block(g21)
    c: Block(g22)
    c: Block(g23)
    c: Block(g11)
    c: Block(g9)
    c: Block(g7)
    c: Block(g5)
    c: Block(g3)
    c: Block(g1)
    c: Coincident(g24,g0)
    c: Coincident(g24,g12)
    c: Horizontal(g24)
    c: Coincident(g25,g0)
    c: Coincident(g25,g12)
    c: Horizontal(g25)
    c: Coincident(g26,g1)
    c: Coincident(g26,g13)
    c: Horizontal(g26)
    c: Coincident(g27,g1)
    c: Coincident(g27,g13)
    c: Horizontal(g27)
    c: Coincident(g28,g2)
    c: Coincident(g28,g14)
    c: Horizontal(g28)
    c: Coincident(g29,g2)
    c: Coincident(g29,g14)
    c: Horizontal(g29)
    c: Coincident(g30,g3)
    c: Coincident(g30,g15)
    c: Horizontal(g30)
    c: Coincident(g31,g3)
    c: Coincident(g31,g15)
    c: Horizontal(g31)
    c: Coincident(g32,g4)
    c: Coincident(g32,g16)
    c: Horizontal(g32)
    c: Coincident(g33,g4)
    c: Coincident(g33,g16)
    c: Horizontal(g33)
    c: Coincident(g34,g5)
    c: Coincident(g34,g17)
    c: Horizontal(g34)
    c: Coincident(g35,g5)
    c: Coincident(g35,g17)
    c: Horizontal(g35)
    c: Coincident(g36,g6)
    c: Coincident(g36,g19)
    c: Horizontal(g36)
    c: Coincident(g37,g6)
    c: Coincident(g37,g19)
    c: Horizontal(g37)
    c: Coincident(g38,g7)
    c: Coincident(g38,g18)
    c: Horizontal(g38)
    c: Coincident(g39,g7)
    c: Coincident(g39,g18)
    c: Horizontal(g39)
    c: Coincident(g40,g8)
    c: Coincident(g40,g20)
    c: Horizontal(g40)
    c: Coincident(g41,g8)
    c: Coincident(g41,g20)
    c: Horizontal(g41)
    c: Coincident(g42,g9)
    c: Coincident(g42,g23)
    c: Horizontal(g42)
    c: Coincident(g43,g9)
    c: Coincident(g43,g23)
    c: Horizontal(g43)
    c: Coincident(g44,g10)
    c: Coincident(g44,g22)
    c: Horizontal(g44)
    c: Coincident(g45,g10)
    c: Coincident(g45,g22)
    c: Horizontal(g45)
    c: Coincident(g46,g11)
    c: Coincident(g46,g21)
    c: Horizontal(g46)
    c: Coincident(g47,g11)
    c: Coincident(g47,g21)
    c: Horizontal(g47)
FEATURE [Part::Extrusion] Extrude042
  Base = -> Sketch051
  Dir = (1,-2e-16,2e-16)
  DirMode = 2
  FaceMakerClass = Part::FaceMakerBullseye
  LengthFwd = 19
  LengthRev = 0
  Placement = pos=(-19,0,0) rot=(0,0,1;0rad)
  Solid = true
  Symmetric = false
FEATURE [Part::Fillet] Fillet035  label="removeToCreateVentalationHoles"
  Base = -> Extrude042
  Edges = <same value as first occurrence — deduplicated (x6 in doc)>
  Placement = pos=(7,0,0) rot=(0,0,1;0rad)
FEATURE [Part::Cut] Cut038  label="top017"
  Base = -> Cut033
  Tool = -> Fillet035
FEATURE [Sketcher::SketchObject] Sketch052  label="bottomSketch001"
  FullyConstrained = true
  sketch-geometry (45):
    g0: LineSegment StartX=6.29999 StartY=8 StartZ=0 EndX=3.29999 EndY=8 EndZ=0
    g1: LineSegment StartX=3.29999 StartY=8 StartZ=0 EndX=3.29999 EndY=-6.03275e-07 EndZ=0
    g2: ArcOfCircle CenterX=8.29999 CenterY=5 CenterZ=0 NormalX=0 NormalY=0 NormalZ=1 AngleXU=0 Radius=2 StartAngle=3.14159 EndAngle=4.71239
    g3: LineSegment StartX=6.29999 StartY=8 StartZ=0 EndX=6.29999 EndY=5 EndZ=0
    g4: ArcOfCircle CenterX=105 CenterY=19 CenterZ=0 NormalX=0 NormalY=0 NormalZ=1 AngleXU=0 Radius=12.7 StartAngle=4.71239 EndAngle=5.94289
    g5-g11: Circle x7 (B-spline internal-alignment scaffolding for g12; pole/knot coordinates omitted)
    g12: BSplineCurve PolesCount=7 KnotsCount=5 Degree=3 IsPeriodic=0
    g13-g17: GeomPoint x5 (B-spline internal-alignment scaffolding for g12; pole/knot coordinates omitted)
    g18: ArcOfCircle CenterX=105 CenterY=19 CenterZ=0 NormalX=0 NormalY=0 NormalZ=1 AngleXU=0 Radius=15.7 StartAngle=5.81226 EndAngle=6.28319
    g19: BSplineCurve PolesCount=5 KnotsCount=3 Degree=3 IsPeriodic=0
    g20: LineSegment StartX=8.29999 StartY=3 StartZ=0 EndX=101.7 EndY=3 EndZ=0
    g21: LineSegment StartX=3.29999 StartY=-6.03275e-07 StartZ=0 EndX=105 EndY=-6.03275e-07 EndZ=0
    g22: LineSegment StartX=120.974 StartY=8.71251 StartZ=0 EndX=122.332 EndY=7.83778 EndZ=0
    g23: LineSegment StartX=105 StartY=-6.03274e-07 StartZ=0 EndX=113 EndY=-6.03274e-07 EndZ=0
    g24: ArcOfCircle CenterX=105 CenterY=19 CenterZ=0 NormalX=0 NormalY=0 NormalZ=1 AngleXU=0 Radius=20.6155 StartAngle=5.11091 EndAngle=5.71103
    g25: ArcOfCircle CenterX=117.7 CenterY=19 CenterZ=0 NormalX=0 NormalY=0 NormalZ=1 AngleXU=0 Radius=3 StartAngle=1.2e-15 EndAngle=2.10468
    g26: Circle CenterX=116.345 CenterY=16.3232 CenterZ=0 NormalX=0 NormalY=0 NormalZ=1 AngleXU=0 Radius=1
    g27: Circle CenterX=117.24 CenterY=15.7584 CenterZ=0 NormalX=0 NormalY=0 NormalZ=1 AngleXU=0 Radius=1
    g28: Circle CenterX=116.972 CenterY=14.7612 CenterZ=0 NormalX=0 NormalY=0 NormalZ=1 AngleXU=0 Radius=1
    g29: BSplineCurve PolesCount=3 KnotsCount=2 Degree=2 IsPeriodic=0
    g30: GeomPoint X=116.345 Y=16.3232 Z=0
    g31: GeomPoint X=116.972 Y=14.7612 Z=0
    g32: Circle CenterX=115.828 CenterY=17.157 CenterZ=0 NormalX=0 NormalY=0 NormalZ=1 AngleXU=0 Radius=1
    g33: Circle CenterX=115.841 CenterY=16.639 CenterZ=0 NormalX=0 NormalY=0 NormalZ=1 AngleXU=0 Radius=1
    g34: Circle CenterX=116.345 CenterY=16.3232 CenterZ=0 NormalX=0 NormalY=0 NormalZ=1 AngleXU=0 Radius=1
    g35: BSplineCurve PolesCount=3 KnotsCount=2 Degree=2 IsPeriodic=0
    g36: GeomPoint X=115.828 Y=17.157 Z=0
    g37: GeomPoint X=116.345 Y=16.3232 Z=0
    g38: LineSegment StartX=115.828 StartY=17.157 StartZ=0 EndX=115.828 EndY=20.8307 EndZ=0
    g39: Circle CenterX=115.828 CenterY=20.8307 CenterZ=0 NormalX=0 NormalY=0 NormalZ=1 AngleXU=0 Radius=1
    g40: Circle CenterX=115.831 CenterY=21.3396 CenterZ=0 NormalX=0 NormalY=0 NormalZ=1 AngleXU=0 Radius=1
    g41: Circle CenterX=116.173 CenterY=21.5825 CenterZ=0 NormalX=0 NormalY=0 NormalZ=1 AngleXU=0 Radius=1
    g42: BSplineCurve PolesCount=3 KnotsCount=2 Degree=2 IsPeriodic=0
    g43: GeomPoint X=115.828 Y=20.8307 Z=0
    g44: GeomPoint X=116.173 Y=21.5825 Z=0
  constraints (70):
    c: Horizontal(g0)
    c: Distance(g0) = 3
    c: Coincident(g1,g0)
    c: Vertical(g1)
    c: Block(g2)
    c: Block(g0)
    c: Coincident(g3,g0)
    c: Coincident(g3,g2)
    c: Vertical(g3)
    c: Block(g1)
    c: Block(g4)
    c: Coincident(g19,g4)
    c: Block(g19)
    c: Equal(g5, g6-g11) x6
    c: InternalAlignment(g5-g11 -> g12) x7
    c: InternalAlignment(g13-g17 -> g12) x5
    c: Block(g12)
    c: Coincident(g18,g12)
    c: Block(g18)
    c: Coincident(g20,g2)
    c: Coincident(g20,g19)
    c: Horizontal(g20)
    c: Distance(g20) = 93.4
    c: Coincident(g21,g1)
    c: Horizontal(g21)
    c: Distance(g21) = 101.7
    c: Horizontal(g23)
    c: Distance(g23) = 8
    c: Coincident(g24,g23)
    c: Block(g23)
    c: Coincident(g22,g24)
    c: Block(g24)
    c: Block(g22)
    c: Distance(g22) = 1.61553
    c: Coincident(g25,g18)
    c: Block(g25)
    c: Weight(g26) = 1
    c: Equal(g26,g27)
    c: Equal(g26,g28)
    c: Coincident(g29,g4)
    c: InternalAlignment(g26,g29)
    c: InternalAlignment(g27,g29)
    c: InternalAlignment(g28,g29)
    c: InternalAlignment(g30,g29)
    c: InternalAlignment(g31,g29)
    c: Block(g29)
    c: Weight(g32) = 1
    c: Equal(g32,g33)
    c: Equal(g32,g34)
    c: Coincident(g35,g29)
    c: InternalAlignment(g32,g35)
    c: InternalAlignment(g33,g35)
    c: InternalAlignment(g34,g35)
    c: InternalAlignment(g36,g35)
    c: InternalAlignment(g37,g35)
    c: Block(g35)
    c: Coincident(g38,g35)
    c: Vertical(g38)
    c: Block(g38)
    c: Coincident(g42,g38)
    c: Weight(g39) = 1
    c: Equal(g39,g40)
    c: Equal(g39,g41)
    c: Coincident(g42,g25)
    c: InternalAlignment(g39,g42)
    c: InternalAlignment(g40,g42)
    c: InternalAlignment(g41,g42)
    c: InternalAlignment(g43,g42)
    c: InternalAlignment(g44,g42)
    c: Block(g42)
FEATURE [Part::Extrusion] Extrude043  label="bottom010"
  Base = -> Sketch052
  Dir = (0,0,1)
  DirMode = 2
  FaceMakerClass = Part::FaceMakerBullseye
  LengthFwd = 71.4
  LengthRev = 0
  Placement = pos=(0,0,0.3) rot=(0,0,1;0rad)
  Solid = true
  Symmetric = false
FEATURE [Sketcher::SketchObject] Sketch053  label="topSketch013"
  FullyConstrained = true
  sketch-geometry (22):
    g0: LineSegment StartX=5.21097e-06 StartY=3 StartZ=0 EndX=5.21097e-06 EndY=19 EndZ=0
    g1: ArcOfCircle CenterX=19 CenterY=19 CenterZ=0 NormalX=0 NormalY=0 NormalZ=1 AngleXU=0 Radius=19 StartAngle=1.5708 EndAngle=3.14159
    g2: ArcOfCircle CenterX=19 CenterY=19 CenterZ=0 NormalX=0 NormalY=0 NormalZ=1 AngleXU=0 Radius=16 StartAngle=1.5708 EndAngle=3.14159
    g3: LineSegment StartX=114 StartY=35 StartZ=0 EndX=19 EndY=35 EndZ=0
    g4: LineSegment StartX=5.21097e-06 StartY=3 StartZ=0 EndX=5.21097e-06 EndY=0 EndZ=0
    g5: LineSegment StartX=3 StartY=0 StartZ=0 EndX=5.21097e-06 EndY=0 EndZ=0
    g6: LineSegment StartX=3 StartY=19 StartZ=0 EndX=3 EndY=0 EndZ=0
    g7: LineSegment StartX=19 StartY=38 StartZ=0 EndX=124 EndY=38 EndZ=0
    g8: Circle CenterX=119 CenterY=35 CenterZ=0 NormalX=0 NormalY=0 NormalZ=1 AngleXU=0 Radius=1
    g9: Circle CenterX=121 CenterY=35 CenterZ=0 NormalX=0 NormalY=0 NormalZ=1 AngleXU=0 Radius=1
    g10: Circle CenterX=121 CenterY=33 CenterZ=0 NormalX=0 NormalY=0 NormalZ=1 AngleXU=0 Radius=1
    g11: BSplineCurve PolesCount=3 KnotsCount=2 Degree=2 IsPeriodic=0
    g12: GeomPoint X=119 Y=35 Z=0
    g13: GeomPoint X=121 Y=33 Z=0
    g14: LineSegment StartX=119 StartY=35 StartZ=0 EndX=114 EndY=35 EndZ=0
    g15: ArcOfCircle CenterX=105 CenterY=19 CenterZ=0 NormalX=0 NormalY=0 NormalZ=1 AngleXU=0 Radius=16 StartAngle=5.60905 EndAngle=6.28319
    g16: LineSegment StartX=121 StartY=33 StartZ=0 EndX=121 EndY=19 EndZ=0
    g17: LineSegment StartX=117.5 StartY=9.01251 StartZ=0 EndX=121.163 EndY=9.0125 EndZ=0
    g18: ArcOfCircle CenterX=105 CenterY=19 CenterZ=0 NormalX=0 NormalY=0 NormalZ=1 AngleXU=0 Radius=20.6155 StartAngle=5.7297 EndAngle=6.28319
    g19: LineSegment StartX=121.163 StartY=9.0125 StartZ=0 EndX=122.538 EndY=8.16329 EndZ=0
    g20: LineSegment StartX=124 StartY=38 StartZ=0 EndX=125.616 EndY=38 EndZ=0
    g21: LineSegment StartX=125.616 StartY=19 StartZ=0 EndX=125.616 EndY=38 EndZ=0
  constraints (50):
    c: Vertical(g0)
    c: Block(g0)
    c: Coincident(g1,g0)
    c: Block(g1)
    c: Coincident(g2,g1)
    c: Block(g2)
    c: Coincident(g3,g2)
    c: Horizontal(g3)
    c: Tangent(g3,g2)
    c: Coincident(g4,g0)
    c: Distance(g4) = 3
    c: Vertical(g4)
    c: Coincident(g5,g4)
    c: Horizontal(g5)
    c: Coincident(g6,g2)
    c: Coincident(g6,g5)
    c: Vertical(g6)
    c: Horizontal(g7)
    c: Distance(g7) = 105
    c: Coincident(g7,g1)
    c: Block(g3)
    c: Weight(g8) = 1
    c: Equal(g8,g9)
    c: Equal(g8,g10)
    c: InternalAlignment(g8,g11)
    c: InternalAlignment(g9,g11)
    c: InternalAlignment(g10,g11)
    c: InternalAlignment(g12,g11)
    c: InternalAlignment(g13,g11)
    c: Block(g11)
    c: Coincident(g14,g11)
    c: Coincident(g14,g3)
    c: Horizontal(g14)
    c: Block(g15)
    c: Coincident(g16,g11)
    c: Coincident(g16,g15)
    c: Vertical(g16)
    c: Distance(g16) = 14
    c: Coincident(g17,g15)
    c: Block(g18)
    c: Coincident(g19,g18)
    c: Coincident(g20,g7)
    c: Horizontal(g20)
    c: Vertical(g21)
    c: Coincident(g20,g21)
    c: Block(g20)
    c: Block(g21)
    c: Block(g19)
    c: Block(g17)
    c: Distance(g20) = 1.61553
FEATURE [Part::Extrusion] Extrude044
  Base = -> Sketch053
  Dir = (0,0,1)
  DirMode = 2
  FaceMakerClass = Part::FaceMakerBullseye
  LengthFwd = 72
  LengthRev = 0
  Solid = true
  Symmetric = false
FEATURE [Part::Fillet] Fillet036  label="top018"
  Base = -> Extrude044
  Edges = 1 edges r=2: [Edge41]
FEATURE [Sketcher::SketchObject] Sketch054
  FullyConstrained = false
  Placement = pos=(0,0,0) rot=(1,0,0;1.5708rad)
  sketch-geometry (24):
    g0: ArcOfCircle CenterX=-4 CenterY=-10.5 CenterZ=0 NormalX=0 NormalY=0 NormalZ=1 AngleXU=0 Radius=1.5 StartAngle=6e-16 EndAngle=3.14159
    g1: ArcOfCircle CenterX=-34.2 CenterY=-10.5 CenterZ=0 NormalX=0 NormalY=0 NormalZ=1 AngleXU=0 Radius=1.5 StartAngle=0 EndAngle=3.14159
    g2: ArcOfCircle CenterX=-34.2 CenterY=-27.7 CenterZ=0 NormalX=0 NormalY=0 NormalZ=1 AngleXU=0 Radius=1.5 StartAngle=3.14159 EndAngle=6.28319
    g3: ArcOfCircle CenterX=-4 CenterY=-27.7 CenterZ=0 NormalX=0 NormalY=0 NormalZ=1 AngleXU=0 Radius=1.5 StartAngle=3.1416 EndAngle=6.28319
    g4: ArcOfCircle CenterX=-10 CenterY=-4.3 CenterZ=0 NormalX=0 NormalY=0 NormalZ=1 AngleXU=0 Radius=1.5 StartAngle=2e-16 EndAngle=3.14159
    g5: ArcOfCircle CenterX=-16.1 CenterY=-1.8 CenterZ=0 NormalX=0 NormalY=0 NormalZ=1 AngleXU=0 Radius=1.5 StartAngle=5e-16 EndAngle=3.14159
    g6: ArcOfCircle CenterX=-22.1 CenterY=-1.8 CenterZ=0 NormalX=0 NormalY=0 NormalZ=1 AngleXU=0 Radius=1.5 StartAngle=5e-16 EndAngle=3.14159
    g7: ArcOfCircle CenterX=-28.2 CenterY=-4.3 CenterZ=0 NormalX=0 NormalY=0 NormalZ=1 AngleXU=0 Radius=1.5 StartAngle=2e-16 EndAngle=3.14159
    g8: ArcOfCircle CenterX=-10 CenterY=-33.9 CenterZ=0 NormalX=0 NormalY=0 NormalZ=1 AngleXU=0 Radius=1.5 StartAngle=3.14159 EndAngle=6.28319
    g9: ArcOfCircle CenterX=-16.1 CenterY=-36.4 CenterZ=0 NormalX=0 NormalY=0 NormalZ=1 AngleXU=0 Radius=1.5 StartAngle=3.14159 EndAngle=6.28319
    g10: ArcOfCircle CenterX=-22.1 CenterY=-36.4 CenterZ=0 NormalX=0 NormalY=0 NormalZ=1 AngleXU=0 Radius=1.5 StartAngle=3.14159 EndAngle=6.28319
    g11: ArcOfCircle CenterX=-28.2 CenterY=-33.9 CenterZ=0 NormalX=0 NormalY=0 NormalZ=1 AngleXU=0 Radius=1.5 StartAngle=3.14159 EndAngle=6.28319
    g12: LineSegment StartX=-35.7 StartY=-10.5 StartZ=0 EndX=-35.7 EndY=-27.7 EndZ=0
    g13: LineSegment StartX=-32.7 StartY=-10.5 StartZ=0 EndX=-32.7 EndY=-27.7 EndZ=0
    g14: LineSegment StartX=-29.7 StartY=-33.9 StartZ=0 EndX=-29.7 EndY=-4.3 EndZ=0
    g15: LineSegment StartX=-26.7 StartY=-33.9 StartZ=0 EndX=-26.7 EndY=-4.3 EndZ=0
    g16: LineSegment StartX=-2.5 StartY=-10.5 StartZ=0 EndX=-2.5 EndY=-27.7 EndZ=0
    g17: LineSegment StartX=-8.5 StartY=-4.3 StartZ=0 EndX=-8.5 EndY=-33.9 EndZ=0
    g18: LineSegment StartX=-5.5 StartY=-10.5 StartZ=0 EndX=-5.5 EndY=-27.7 EndZ=0
    g19: LineSegment StartX=-11.5 StartY=-4.3 StartZ=0 EndX=-11.5 EndY=-33.9 EndZ=0
    g20: LineSegment StartX=-14.6 StartY=-1.8 StartZ=0 EndX=-14.6 EndY=-36.4 EndZ=0
    g21: LineSegment StartX=-17.6 StartY=-1.8 StartZ=0 EndX=-17.6 EndY=-36.4 EndZ=0
    g22: LineSegment StartX=-20.6 StartY=-36.4 StartZ=0 EndX=-20.6 EndY=-1.8 EndZ=0
    g23: LineSegment StartX=-23.6 StartY=-1.8 StartZ=0 EndX=-23.6 EndY=-36.4 EndZ=0
  constraints (48):
    c: Block(g0)
    c: Block(g1)
    c: Block(g2)
    c: Block(g3)
    c: Block(g4)
    c: Block(g5)
    c: Block(g6)
    c: Block(g7)
    c: Block(g8)
    c: Block(g9)
    c: Block(g10)
    c: Block(g11)
    c: Coincident(g12,g1)
    c: Coincident(g12,g2)
    c: Vertical(g12)
    c: Coincident(g13,g1)
    c: Coincident(g13,g2)
    c: Vertical(g13)
    c: Coincident(g14,g11)
    c: Coincident(g14,g7)
    c: Vertical(g14)
    c: Coincident(g15,g11)
    c: Coincident(g15,g7)
    c: Vertical(g15)
    c: Coincident(g16,g0)
    c: Coincident(g16,g3)
    c: Vertical(g16)
    c: Coincident(g17,g4)
    c: Coincident(g17,g8)
    c: Vertical(g17)
    c: Coincident(g18,g0)
    c: Coincident(g18,g3)
    c: Vertical(g18)
    c: Coincident(g19,g4)
    c: Coincident(g19,g8)
    c: Vertical(g19)
    c: Coincident(g20,g5)
    c: Coincident(g20,g9)
    c: Vertical(g20)
    c: Coincident(g21,g5)
    c: Coincident(g21,g9)
    c: Vertical(g21)
    c: Coincident(g22,g10)
    c: Coincident(g22,g6)
    c: Vertical(g22)
    c: Coincident(g23,g6)
    c: Coincident(g23,g10)
    c: Vertical(g23)
FEATURE [Part::Extrusion] Extrude045  label="removeToCreateFanGrillHoles003"
  Base = -> Sketch054
  Dir = (0,-1,6e-16)
  DirMode = 2
  FaceMakerClass = Part::FaceMakerBullseye
  LengthFwd = 10
  LengthRev = 0
  Placement = pos=(65.4,44,54.82) rot=(0,0,1;0rad)
  Solid = true
  Symmetric = false
FEATURE [Part::Feature] Face105 .. Face108  x4 (patterned run collapsed; names and placements below)
  shape: bbox 3.5 x 17.8 x 2e-07 mm, 1 faces, 0 solids (baked)
FEATURE [Part::Revolution] Revolve113  label="removeToCreateScrewAndThreadedInsertHole041"
  Angle = 360
  Axis = (0,1,0)
  Base = (0,0,0)
  FaceMakerClass = Part::FaceMakerBullseye
  Placement = pos=(62.3,30.3,19.7) rot=(0,0,1;0rad)
  Solid = false
  Source = -> Face105
  Symmetric = false
FEATURE [Part::Revolution] Revolve114  label="removeToCreateScrewAndThreadedInsertHole042"
  Angle = 360
  Axis = (0,1,0)
  Base = (0,0,0)
  FaceMakerClass = Part::FaceMakerBullseye
  Placement = pos=(62.3,30.3,51.7) rot=(0,0,1;0rad)
  Solid = false
  Source = -> Face106
  Symmetric = false
FEATURE [Part::Revolution] Revolve115  label="removeToCreateScrewAndThreadedInsertHole043"
  Angle = 360
  Axis = (0,1,0)
  Base = (0,0,0)
  FaceMakerClass = Part::FaceMakerBullseye
  Placement = pos=(30.3,30.3,19.7) rot=(0,0,1;0rad)
  Solid = false
  Source = -> Face107
  Symmetric = false
FEATURE [Part::Revolution] Revolve116  label="removeToCreateScrewAndThreadedInsertHole044"
  Angle = 360
  Axis = (0,1,0)
  Base = (0,0,0)
  FaceMakerClass = Part::FaceMakerBullseye
  Placement = pos=(30.3,30.3,51.7) rot=(0,0,1;0rad)
  Solid = false
  Source = -> Face108
  Symmetric = false
FEATURE [Part::MultiFuse] Fusion083  label="createThreadedInsertHolesForFan004"
  Shapes = -> [Revolve113,Revolve114,Revolve115,Revolve116]
FEATURE [Part::Box] Box024  label="removeToCreteHoleForPlugHousing026"
  AttacherType = Attacher::AttachEngine3D
  Height = 28.6
  Length = 10
  Placement = pos=(-2,0,21.7) rot=(0,0,1;0rad)
  Width = 19
FEATURE [Part::Cylinder] Cylinder038  label="removeToCreteHoleForPlugHousing027"
  Angle = 360
  AttacherType = Attacher::AttachEngine3D
  Height = 20
  Placement = pos=(-2,19,36) rot=(0,1,0;1.5708rad)
  Radius = 14.3
FEATURE [Part::MultiFuse] Fusion084  label="removeToCreteHoleForPlugHousing028"
  Shapes = -> [Box024,Cylinder038]
FEATURE [Part::Cylinder] Cylinder039
  Angle = 360
  AttacherType = Attacher::AttachEngine3D
  Height = 20
  Placement = pos=(0,0,36.15) rot=(0,0,1;0rad)
  Radius = 14.3
FEATURE [Part::Cylinder] Cylinder040
  Angle = 360
  AttacherType = Attacher::AttachEngine3D
  Height = 10
  Placement = pos=(0,0,36.15) rot=(0,0,1;0rad)
  Radius = 4
FEATURE [Part::Box] Box025  label="removeToCreteHoleForPlugHousing030"
  AttacherType = Attacher::AttachEngine3D
  Height = 28.6
  Length = 20
  Placement = pos=(106.15,0,21.7) rot=(0,0,1;0rad)
  Width = 19
FEATURE [Part::MultiFuse] Fusion086  label="removeToCreteHoleForPlugHousing031"
  Placement = pos=(70,19,36) rot=(0,1,0;1.5708rad)
  Shapes = -> [Cylinder039,Cylinder040]
FEATURE [Part::MultiFuse] Fusion085  label="removeToCreteHoleForPlugHousing029"
  Shapes = -> [Box025,Fusion086]
FEATURE [Sketcher::SketchObject] Sketch055
  FullyConstrained = true
  Placement = pos=(117,19,0) rot=(0.57735,0.57735,0.57735;2.0944rad)
  sketch-geometry (48):
    g0: LineSegment StartX=-49.19 StartY=69.25 StartZ=0 EndX=-49.19 EndY=66.25 EndZ=0
    g1: LineSegment StartX=-49.19 StartY=63.5 StartZ=0 EndX=-49.19 EndY=60.5 EndZ=0
    g2: LineSegment StartX=-49.19 StartY=57.75 StartZ=0 EndX=-49.19 EndY=54.75 EndZ=0
    g3: LineSegment StartX=-49.19 StartY=52 StartZ=0 EndX=-49.19 EndY=49 EndZ=0
    g4: LineSegment StartX=-49.19 StartY=46.25 StartZ=0 EndX=-49.19 EndY=43.25 EndZ=0
    g5: LineSegment StartX=-49.19 StartY=40.5 StartZ=0 EndX=-49.19 EndY=37.5 EndZ=0
    g6: LineSegment StartX=-49.19 StartY=34.5 StartZ=0 EndX=-49.19 EndY=31.5 EndZ=0
    g7: LineSegment StartX=-49.19 StartY=28.75 StartZ=0 EndX=-49.19 EndY=25.75 EndZ=0
    g8: LineSegment StartX=-49.19 StartY=23 StartZ=0 EndX=-49.19 EndY=20 EndZ=0
    g9: LineSegment StartX=-49.19 StartY=17.25 StartZ=0 EndX=-49.19 EndY=14.25 EndZ=0
    g10: LineSegment StartX=-49.19 StartY=11.5 StartZ=0 EndX=-49.19 EndY=8.5 EndZ=0
    g11: LineSegment StartX=-49.19 StartY=5.75 StartZ=0 EndX=-49.19 EndY=2.75 EndZ=0
    g12: ArcOfCircle CenterX=-1.5 CenterY=67.75 CenterZ=0 NormalX=0 NormalY=0 NormalZ=1 AngleXU=0 Radius=1.5 StartAngle=4.71239 EndAngle=7.85398
    g13: ArcOfCircle CenterX=-1.5 CenterY=62 CenterZ=0 NormalX=0 NormalY=0 NormalZ=1 AngleXU=0 Radius=1.5 StartAngle=4.71239 EndAngle=7.85398
    g14: ArcOfCircle CenterX=-1.5 CenterY=56.25 CenterZ=0 NormalX=0 NormalY=0 NormalZ=1 AngleXU=0 Radius=1.5 StartAngle=4.71239 EndAngle=7.85398
    g15: ArcOfCircle CenterX=-11.49 CenterY=50.5 CenterZ=0 NormalX=0 NormalY=0 NormalZ=1 AngleXU=0 Radius=1.5 StartAngle=4.71239 EndAngle=7.85398
    g16: ArcOfCircle CenterX=-16.28 CenterY=44.75 CenterZ=0 NormalX=0 NormalY=0 NormalZ=1 AngleXU=0 Radius=1.5 StartAngle=4.71239 EndAngle=7.85398
    g17: ArcOfCircle CenterX=-18.2337 CenterY=39 CenterZ=0 NormalX=0 NormalY=0 NormalZ=1 AngleXU=0 Radius=1.5 StartAngle=4.71485 EndAngle=7.85398
    g18: ArcOfCircle CenterX=-16.2837 CenterY=27.25 CenterZ=0 NormalX=0 NormalY=0 NormalZ=1 AngleXU=0 Radius=1.5 StartAngle=4.71485 EndAngle=7.85398
    g19: ArcOfCircle CenterX=-18.2337 CenterY=33 CenterZ=0 NormalX=0 NormalY=0 NormalZ=1 AngleXU=0 Radius=1.5 StartAngle=4.71485 EndAngle=7.85398
    g20: ArcOfCircle CenterX=-11.49 CenterY=21.5 CenterZ=0 NormalX=0 NormalY=0 NormalZ=1 AngleXU=0 Radius=1.5 StartAngle=4.71239 EndAngle=7.85398
    g21: ArcOfCircle CenterX=-1.5 CenterY=4.25 CenterZ=0 NormalX=0 NormalY=0 NormalZ=1 AngleXU=0 Radius=1.5 StartAngle=4.71239 EndAngle=7.85398
    g22: ArcOfCircle CenterX=-1.5 CenterY=10 CenterZ=0 NormalX=0 NormalY=0 NormalZ=1 AngleXU=0 Radius=1.5 StartAngle=4.71239 EndAngle=7.85398
    g23: ArcOfCircle CenterX=-1.5 CenterY=15.75 CenterZ=0 NormalX=0 NormalY=0 NormalZ=1 AngleXU=0 Radius=1.5 StartAngle=4.71239 EndAngle=7.85398
    g24: LineSegment StartX=-49.19 StartY=69.25 StartZ=0 EndX=-1.5 EndY=69.25 EndZ=0
    g25: LineSegment StartX=-49.19 StartY=66.25 StartZ=0 EndX=-1.5 EndY=66.25 EndZ=0
    g26: LineSegment StartX=-49.19 StartY=63.5 StartZ=0 EndX=-1.5 EndY=63.5 EndZ=0
    g27: LineSegment StartX=-49.19 StartY=60.5 StartZ=0 EndX=-1.5 EndY=60.5 EndZ=0
    g28: LineSegment StartX=-49.19 StartY=57.75 StartZ=0 EndX=-1.5 EndY=57.75 EndZ=0
    g29: LineSegment StartX=-49.19 StartY=54.75 StartZ=0 EndX=-1.5 EndY=54.75 EndZ=0
    g30: LineSegment StartX=-49.19 StartY=52 StartZ=0 EndX=-11.49 EndY=52 EndZ=0
    g31: LineSegment StartX=-49.19 StartY=49 StartZ=0 EndX=-11.49 EndY=49 EndZ=0
    g32: LineSegment StartX=-49.19 StartY=46.25 StartZ=0 EndX=-16.28 EndY=46.25 EndZ=0
    g33: LineSegment StartX=-49.19 StartY=43.25 StartZ=0 EndX=-16.28 EndY=43.25 EndZ=0
    g34: LineSegment StartX=-49.19 StartY=40.5 StartZ=0 EndX=-18.2337 EndY=40.5 EndZ=0
    g35: LineSegment StartX=-49.19 StartY=37.5 StartZ=0 EndX=-18.23 EndY=37.5 EndZ=0
    g36: LineSegment StartX=-49.19 StartY=34.5 StartZ=0 EndX=-18.2337 EndY=34.5 EndZ=0
    g37: LineSegment StartX=-49.19 StartY=31.5 StartZ=0 EndX=-18.23 EndY=31.5 EndZ=0
    g38: LineSegment StartX=-49.19 StartY=28.75 StartZ=0 EndX=-16.2837 EndY=28.75 EndZ=0
    g39: LineSegment StartX=-49.19 StartY=25.75 StartZ=0 EndX=-16.28 EndY=25.75 EndZ=0
    g40: LineSegment StartX=-49.19 StartY=23 StartZ=0 EndX=-11.49 EndY=23 EndZ=0
    g41: LineSegment StartX=-49.19 StartY=20 StartZ=0 EndX=-11.49 EndY=20 EndZ=0
    g42: LineSegment StartX=-49.19 StartY=17.25 StartZ=0 EndX=-1.5 EndY=17.25 EndZ=0
    g43: LineSegment StartX=-49.19 StartY=14.25 StartZ=0 EndX=-1.5 EndY=14.25 EndZ=0
    g44: LineSegment StartX=-49.19 StartY=11.5 StartZ=0 EndX=-1.5 EndY=11.5 EndZ=0
    g45: LineSegment StartX=-49.19 StartY=8.5 StartZ=0 EndX=-1.5 EndY=8.5 EndZ=0
    g46: LineSegment StartX=-49.19 StartY=5.75 StartZ=0 EndX=-1.5 EndY=5.75 EndZ=0
    g47: LineSegment StartX=-49.19 StartY=2.75 StartZ=0 EndX=-1.5 EndY=2.75 EndZ=0
  constraints (120):
    c: Vertical(g0)
    c: Distance(g0) = 3
    c: Block(g0)
    c: Vertical(g1)
    c: Distance(g1) = 3
    c: Vertical(g2)
    c: Equal(g0,g2) = 3
    c: Block(g2)
    c: Vertical(g3)
    c: Equal(g1,g3) = 3
    c: Vertical(g4)
    c: Equal(g0,g4) = 3
    c: Block(g4)
    c: Vertical(g5)
    c: Equal(g1,g5) = 3
    c: Vertical(g6)
    c: Equal(g0,g6) = 3
    c: Block(g6)
    c: Vertical(g7)
    c: Equal(g1,g7) = 3
    c: Vertical(g8)
    c: Equal(g0,g8) = 3
    c: Block(g8)
    c: Vertical(g9)
    c: Equal(g1,g9) = 3
    c: Vertical(g10)
    c: Equal(g0,g10) = 3
    c: Block(g10)
    c: Vertical(g11)
    c: Equal(g1,g11) = 3
    c: Block(g12)
    c: Block(g13)
    c: Block(g14)
    c: Block(g15)
    c: Block(g16)
    c: Block(g17)
    c: Block(g18)
    c: Block(g19)
    c: Block(g20)
    c: Block(g21)
    c: Block(g22)
    c: Block(g23)
    c: Block(g11)
    c: Block(g9)
    c: Block(g7)
    c: Block(g5)
    c: Block(g3)
    c: Block(g1)
    c: Coincident(g24,g0)
    c: Coincident(g24,g12)
    c: Horizontal(g24)
    c: Coincident(g25,g0)
    c: Coincident(g25,g12)
    c: Horizontal(g25)
    c: Coincident(g26,g1)
    c: Coincident(g26,g13)
    c: Horizontal(g26)
    c: Coincident(g27,g1)
    c: Coincident(g27,g13)
    c: Horizontal(g27)
    c: Coincident(g28,g2)
    c: Coincident(g28,g14)
    c: Horizontal(g28)
    c: Coincident(g29,g2)
    c: Coincident(g29,g14)
    c: Horizontal(g29)
    c: Coincident(g30,g3)
    c: Coincident(g30,g15)
    c: Horizontal(g30)
    c: Coincident(g31,g3)
    c: Coincident(g31,g15)
    c: Horizontal(g31)
    c: Coincident(g32,g4)
    c: Coincident(g32,g16)
    c: Horizontal(g32)
    c: Coincident(g33,g4)
    c: Coincident(g33,g16)
    c: Horizontal(g33)
    c: Coincident(g34,g5)
    c: Coincident(g34,g17)
    c: Horizontal(g34)
    c: Coincident(g35,g5)
    c: Coincident(g35,g17)
    c: Horizontal(g35)
    c: Coincident(g36,g6)
    c: Coincident(g36,g19)
    c: Horizontal(g36)
    c: Coincident(g37,g6)
    c: Coincident(g37,g19)
    c: Horizontal(g37)
    c: Coincident(g38,g7)
    c: Coincident(g38,g18)
    c: Horizontal(g38)
    c: Coincident(g39,g7)
    c: Coincident(g39,g18)
    c: Horizontal(g39)
    c: Coincident(g40,g8)
    c: Coincident(g40,g20)
    c: Horizontal(g40)
    c: Coincident(g41,g8)
    c: Coincident(g41,g20)
    c: Horizontal(g41)
    c: Coincident(g42,g9)
    c: Coincident(g42,g23)
    c: Horizontal(g42)
    c: Coincident(g43,g9)
    c: Coincident(g43,g23)
    c: Horizontal(g43)
    c: Coincident(g44,g10)
    c: Coincident(g44,g22)
    c: Horizontal(g44)
    c: Coincident(g45,g10)
    c: Coincident(g45,g22)
    c: Horizontal(g45)
    c: Coincident(g46,g11)
    c: Coincident(g46,g21)
    c: Horizontal(g46)
    c: Coincident(g47,g11)
    c: Coincident(g47,g21)
    c: Horizontal(g47)
FEATURE [Part::Extrusion] Extrude046
  Base = -> Sketch055
  Dir = (1,0,0)
  DirMode = 2
  FaceMakerClass = Part::FaceMakerBullseye
  LengthFwd = 23
  LengthRev = 0
  Placement = pos=(-19,0,0) rot=(0,0,1;0rad)
  Solid = true
  Symmetric = false
FEATURE [Part::Fillet] Fillet038  label="removeToCreateVentalationHoles001"
  Base = -> Extrude046
  Edges = <same value as first occurrence — deduplicated (x6 in doc)>
  Placement = pos=(7,0,0) rot=(0,0,1;0rad)
FEATURE [Sketcher::SketchObject] Sketch056  label="topSketch014"
  FullyConstrained = true
  sketch-geometry (22):
    g0: LineSegment StartX=5.21097e-06 StartY=3 StartZ=0 EndX=5.21097e-06 EndY=19 EndZ=0
    g1: ArcOfCircle CenterX=19 CenterY=19 CenterZ=0 NormalX=0 NormalY=0 NormalZ=1 AngleXU=0 Radius=19 StartAngle=1.5708 EndAngle=3.14159
    g2: ArcOfCircle CenterX=19 CenterY=19 CenterZ=0 NormalX=0 NormalY=0 NormalZ=1 AngleXU=0 Radius=16 StartAngle=1.5708 EndAngle=3.14159
    g3: LineSegment StartX=114 StartY=35 StartZ=0 EndX=19 EndY=35 EndZ=0
    g4: LineSegment StartX=5.21097e-06 StartY=3 StartZ=0 EndX=5.21097e-06 EndY=0 EndZ=0
    g5: LineSegment StartX=3 StartY=0 StartZ=0 EndX=5.21097e-06 EndY=0 EndZ=0
    g6: LineSegment StartX=3 StartY=19 StartZ=0 EndX=3 EndY=0 EndZ=0
    g7: LineSegment StartX=19 StartY=38 StartZ=0 EndX=124 EndY=38 EndZ=0
    g8: Circle CenterX=119 CenterY=35 CenterZ=0 NormalX=0 NormalY=0 NormalZ=1 AngleXU=0 Radius=1
    g9: Circle CenterX=121 CenterY=35 CenterZ=0 NormalX=0 NormalY=0 NormalZ=1 AngleXU=0 Radius=1
    g10: Circle CenterX=121 CenterY=33 CenterZ=0 NormalX=0 NormalY=0 NormalZ=1 AngleXU=0 Radius=1
    g11: BSplineCurve PolesCount=3 KnotsCount=2 Degree=2 IsPeriodic=0
    g12: GeomPoint X=119 Y=35 Z=0
    g13: GeomPoint X=121 Y=33 Z=0
    g14: LineSegment StartX=119 StartY=35 StartZ=0 EndX=114 EndY=35 EndZ=0
    g15: ArcOfCircle CenterX=105 CenterY=19 CenterZ=0 NormalX=0 NormalY=0 NormalZ=1 AngleXU=0 Radius=16 StartAngle=5.60905 EndAngle=6.28319
    g16: LineSegment StartX=121 StartY=33 StartZ=0 EndX=121 EndY=19 EndZ=0
    g17: LineSegment StartX=117.5 StartY=9.01251 StartZ=0 EndX=121.163 EndY=9.0125 EndZ=0
    g18: ArcOfCircle CenterX=105 CenterY=19 CenterZ=0 NormalX=0 NormalY=0 NormalZ=1 AngleXU=0 Radius=20.6155 StartAngle=5.7297 EndAngle=6.28319
    g19: LineSegment StartX=121.163 StartY=9.0125 StartZ=0 EndX=122.538 EndY=8.16329 EndZ=0
    g20: LineSegment StartX=124 StartY=38 StartZ=0 EndX=125.616 EndY=38 EndZ=0
    g21: LineSegment StartX=125.616 StartY=19 StartZ=0 EndX=125.616 EndY=38 EndZ=0
  constraints (49):
    c: Vertical(g0)
    c: Block(g0)
    c: Coincident(g1,g0)
    c: Block(g1)
    c: Coincident(g2,g1)
    c: Block(g2)
    c: Coincident(g3,g2)
    c: Horizontal(g3)
    c: Tangent(g3,g2)
    c: Coincident(g4,g0)
    c: Distance(g4) = 3
    c: Vertical(g4)
    c: Coincident(g5,g4)
    c: Horizontal(g5)
    c: Coincident(g6,g2)
    c: Coincident(g6,g5)
    c: Vertical(g6)
    c: Horizontal(g7)
    c: Distance(g7) = 105
    c: Coincident(g7,g1)
    c: Block(g3)
    c: Weight(g8) = 1
    c: Equal(g8,g9)
    c: Equal(g8,g10)
    c: InternalAlignment(g8,g11)
    c: InternalAlignment(g9,g11)
    c: InternalAlignment(g10,g11)
    c: InternalAlignment(g12,g11)
    c: InternalAlignment(g13,g11)
    c: Block(g11)
    c: Coincident(g14,g11)
    c: Coincident(g14,g3)
    c: Horizontal(g14)
    c: Block(g15)
    c: Coincident(g16,g11)
    c: Coincident(g16,g15)
    c: Vertical(g16)
    c: Distance(g16) = 14
    c: Coincident(g17,g15)
    c: Block(g18)
    c: Coincident(g19,g18)
    c: Coincident(g20,g7)
    c: Horizontal(g20)
    c: Vertical(g21)
    c: Coincident(g20,g21)
    c: Block(g20)
    c: Block(g21)
    c: Block(g19)
    c: Block(g17)
FEATURE [Part::Box] Box026  label="removeToCreteHoleForPlugHousing032"
  AttacherType = Attacher::AttachEngine3D
  Height = 28.6
  Length = 10
  Placement = pos=(-2,0,21.7) rot=(0,0,1;0rad)
  Width = 19
FEATURE [Part::Feature] Face109 .. Face112  x4 (patterned run collapsed; names and placements below)
  shape: bbox 3.5 x 17.8 x 2e-07 mm, 1 faces, 0 solids (baked)
FEATURE [Part::Revolution] Revolve117  label="removeToCreateScrewAndThreadedInsertHole045"
  Angle = 360
  Axis = (0,1,0)
  Base = (0,0,0)
  FaceMakerClass = Part::FaceMakerBullseye
  Placement = pos=(62.3,30.3,19.7) rot=(0,0,1;0rad)
  Solid = false
  Source = -> Face109
  Symmetric = false
FEATURE [Part::Revolution] Revolve118  label="removeToCreateScrewAndThreadedInsertHole046"
  Angle = 360
  Axis = (0,1,0)
  Base = (0,0,0)
  FaceMakerClass = Part::FaceMakerBullseye
  Placement = pos=(62.3,30.3,51.7) rot=(0,0,1;0rad)
  Solid = false
  Source = -> Face110
  Symmetric = false
FEATURE [Part::Revolution] Revolve119  label="removeToCreateScrewAndThreadedInsertHole047"
  Angle = 360
  Axis = (0,1,0)
  Base = (0,0,0)
  FaceMakerClass = Part::FaceMakerBullseye
  Placement = pos=(30.3,30.3,19.7) rot=(0,0,1;0rad)
  Solid = false
  Source = -> Face111
  Symmetric = false
FEATURE [Part::Revolution] Revolve120  label="removeToCreateScrewAndThreadedInsertHole048"
  Angle = 360
  Axis = (0,1,0)
  Base = (0,0,0)
  FaceMakerClass = Part::FaceMakerBullseye
  Placement = pos=(30.3,30.3,51.7) rot=(0,0,1;0rad)
  Solid = false
  Source = -> Face112
  Symmetric = false
FEATURE [Part::MultiFuse] Fusion087  label="createThreadedInsertHolesForFan005"
  Shapes = -> [Revolve117,Revolve118,Revolve119,Revolve120]
FEATURE [Part::Extrusion] Extrude047
  Base = -> Sketch056
  Dir = (0,0,1)
  DirMode = 2
  FaceMakerClass = Part::FaceMakerBullseye
  LengthFwd = 72
  LengthRev = 0
  Solid = true
  Symmetric = false
FEATURE [Part::Fillet] Fillet039  label="top019"
  Base = -> Extrude047
  Edges = 1 edges r=2: [Edge35]
FEATURE [Sketcher::SketchObject] Sketch057
  FullyConstrained = false
  Placement = pos=(0,0,0) rot=(1,0,0;1.5708rad)
  sketch-geometry (24):
    g0: ArcOfCircle CenterX=-4 CenterY=-10.5 CenterZ=0 NormalX=0 NormalY=0 NormalZ=1 AngleXU=0 Radius=1.5 StartAngle=6e-16 EndAngle=3.14159
    g1: ArcOfCircle CenterX=-34.2 CenterY=-10.5 CenterZ=0 NormalX=0 NormalY=0 NormalZ=1 AngleXU=0 Radius=1.5 StartAngle=0 EndAngle=3.14159
    g2: ArcOfCircle CenterX=-34.2 CenterY=-27.7 CenterZ=0 NormalX=0 NormalY=0 NormalZ=1 AngleXU=0 Radius=1.5 StartAngle=3.14159 EndAngle=6.28319
    g3: ArcOfCircle CenterX=-4 CenterY=-27.7 CenterZ=0 NormalX=0 NormalY=0 NormalZ=1 AngleXU=0 Radius=1.5 StartAngle=3.1416 EndAngle=6.28319
    g4: ArcOfCircle CenterX=-10 CenterY=-4.3 CenterZ=0 NormalX=0 NormalY=0 NormalZ=1 AngleXU=0 Radius=1.5 StartAngle=2e-16 EndAngle=3.14159
    g5: ArcOfCircle CenterX=-16.1 CenterY=-1.8 CenterZ=0 NormalX=0 NormalY=0 NormalZ=1 AngleXU=0 Radius=1.5 StartAngle=5e-16 EndAngle=3.14159
    g6: ArcOfCircle CenterX=-22.1 CenterY=-1.8 CenterZ=0 NormalX=0 NormalY=0 NormalZ=1 AngleXU=0 Radius=1.5 StartAngle=5e-16 EndAngle=3.14159
    g7: ArcOfCircle CenterX=-28.2 CenterY=-4.3 CenterZ=0 NormalX=0 NormalY=0 NormalZ=1 AngleXU=0 Radius=1.5 StartAngle=2e-16 EndAngle=3.14159
    g8: ArcOfCircle CenterX=-10 CenterY=-33.9 CenterZ=0 NormalX=0 NormalY=0 NormalZ=1 AngleXU=0 Radius=1.5 StartAngle=3.14159 EndAngle=6.28319
    g9: ArcOfCircle CenterX=-16.1 CenterY=-36.4 CenterZ=0 NormalX=0 NormalY=0 NormalZ=1 AngleXU=0 Radius=1.5 StartAngle=3.14159 EndAngle=6.28319
    g10: ArcOfCircle CenterX=-22.1 CenterY=-36.4 CenterZ=0 NormalX=0 NormalY=0 NormalZ=1 AngleXU=0 Radius=1.5 StartAngle=3.14159 EndAngle=6.28319
    g11: ArcOfCircle CenterX=-28.2 CenterY=-33.9 CenterZ=0 NormalX=0 NormalY=0 NormalZ=1 AngleXU=0 Radius=1.5 StartAngle=3.14159 EndAngle=6.28319
    g12: LineSegment StartX=-35.7 StartY=-10.5 StartZ=0 EndX=-35.7 EndY=-27.7 EndZ=0
    g13: LineSegment StartX=-32.7 StartY=-10.5 StartZ=0 EndX=-32.7 EndY=-27.7 EndZ=0
    g14: LineSegment StartX=-29.7 StartY=-33.9 StartZ=0 EndX=-29.7 EndY=-4.3 EndZ=0
    g15: LineSegment StartX=-26.7 StartY=-33.9 StartZ=0 EndX=-26.7 EndY=-4.3 EndZ=0
    g16: LineSegment StartX=-2.5 StartY=-10.5 StartZ=0 EndX=-2.5 EndY=-27.7 EndZ=0
    g17: LineSegment StartX=-8.5 StartY=-4.3 StartZ=0 EndX=-8.5 EndY=-33.9 EndZ=0
    g18: LineSegment StartX=-5.5 StartY=-10.5 StartZ=0 EndX=-5.5 EndY=-27.7 EndZ=0
    g19: LineSegment StartX=-11.5 StartY=-4.3 StartZ=0 EndX=-11.5 EndY=-33.9 EndZ=0
    g20: LineSegment StartX=-14.6 StartY=-1.8 StartZ=0 EndX=-14.6 EndY=-36.4 EndZ=0
    g21: LineSegment StartX=-17.6 StartY=-1.8 StartZ=0 EndX=-17.6 EndY=-36.4 EndZ=0
    g22: LineSegment StartX=-20.6 StartY=-36.4 StartZ=0 EndX=-20.6 EndY=-1.8 EndZ=0
    g23: LineSegment StartX=-23.6 StartY=-1.8 StartZ=0 EndX=-23.6 EndY=-36.4 EndZ=0
  constraints (48):
    c: Block(g0)
    c: Block(g1)
    c: Block(g2)
    c: Block(g3)
    c: Block(g4)
    c: Block(g5)
    c: Block(g6)
    c: Block(g7)
    c: Block(g8)
    c: Block(g9)
    c: Block(g10)
    c: Block(g11)
    c: Coincident(g12,g1)
    c: Coincident(g12,g2)
    c: Vertical(g12)
    c: Coincident(g13,g1)
    c: Coincident(g13,g2)
    c: Vertical(g13)
    c: Coincident(g14,g11)
    c: Coincident(g14,g7)
    c: Vertical(g14)
    c: Coincident(g15,g11)
    c: Coincident(g15,g7)
    c: Vertical(g15)
    c: Coincident(g16,g0)
    c: Coincident(g16,g3)
    c: Vertical(g16)
    c: Coincident(g17,g4)
    c: Coincident(g17,g8)
    c: Vertical(g17)
    c: Coincident(g18,g0)
    c: Coincident(g18,g3)
    c: Vertical(g18)
    c: Coincident(g19,g4)
    c: Coincident(g19,g8)
    c: Vertical(g19)
    c: Coincident(g20,g5)
    c: Coincident(g20,g9)
    c: Vertical(g20)
    c: Coincident(g21,g5)
    c: Coincident(g21,g9)
    c: Vertical(g21)
    c: Coincident(g22,g10)
    c: Coincident(g22,g6)
    c: Vertical(g22)
    c: Coincident(g23,g6)
    c: Coincident(g23,g10)
    c: Vertical(g23)
FEATURE [Part::Extrusion] Extrude048  label="removeToCreateFanGrillHoles004"
  Base = -> Sketch057
  Dir = (0,-1,6e-16)
  DirMode = 2
  FaceMakerClass = Part::FaceMakerBullseye
  LengthFwd = 10
  LengthRev = 0
  Placement = pos=(65.4,44,54.82) rot=(0,0,1;0rad)
  Solid = true
  Symmetric = false
FEATURE [Part::Cut] Cut040  label="top021"
  Base = -> Fillet039
  Tool = -> Extrude048
FEATURE [Part::Cylinder] Cylinder041  label="removeToCreteHoleForPlugHousing034"
  Angle = 360
  AttacherType = Attacher::AttachEngine3D
  Height = 20
  Placement = pos=(-2,19,36) rot=(0,1,0;1.5708rad)
  Radius = 14.3
FEATURE [Part::MultiFuse] Fusion089  label="removeToCreteHoleForPlugHousing035"
  Shapes = -> [Box026,Cylinder041]
FEATURE [Part::Cylinder] Cylinder042
  Angle = 360
  AttacherType = Attacher::AttachEngine3D
  Height = 20
  Placement = pos=(0,0,36.15) rot=(0,0,1;0rad)
  Radius = 14.3
FEATURE [Part::Cylinder] Cylinder043
  Angle = 360
  AttacherType = Attacher::AttachEngine3D
  Height = 10
  Placement = pos=(0,0,36.15) rot=(0,0,1;0rad)
  Radius = 4
FEATURE [Part::Box] Box027  label="removeToCreteHoleForPlugHousing036"
  AttacherType = Attacher::AttachEngine3D
  Height = 28.6
  Length = 20
  Placement = pos=(106.15,0,21.7) rot=(0,0,1;0rad)
  Width = 19
FEATURE [Part::Cut] Cut041  label="top022"
  Base = -> Cut040
  Tool = -> Fusion087
FEATURE [Part::Cut] Cut039  label="top020"
  Base = -> Cut041
  Tool = -> Fusion089
FEATURE [Part::MultiFuse] Fusion090  label="removeToCreteHoleForPlugHousing037"
  Placement = pos=(70,19,36) rot=(0,1,0;1.5708rad)
  Shapes = -> [Cylinder042,Cylinder043]
FEATURE [Part::MultiFuse] Fusion088  label="removeToCreteHoleForPlugHousing033"
  Shapes = -> [Box027,Fusion090]
FEATURE [Part::Cut] Cut042  label="removeToCreteHoleForPlugHousing038"
  Base = -> Cut039
  Tool = -> Fusion088
FEATURE [Part::MultiFuse] Fusion091  label="removeFromTop"
  Shapes = -> [Fillet038,Fusion085,Fusion084,Fusion083,Extrude045]
FEATURE [Part::Cut] Cut043  label="REAL TOP ====="
  Base = -> Fillet036
  Tool = -> Fusion091
FEATURE [Part::MultiFuse] Fusion092  label="caseScrewPillarBracket016"
  Shapes = -> [Extrude030,Extrude031,Extrude032,Extrude033,Extrude034,Extrude035,Extrude036,Extrude037,Box013,Box014]
FEATURE [Sketcher::SketchObject] Sketch058  label="topSketch015"
  FullyConstrained = true
  sketch-geometry (20):
    g0: LineSegment StartX=5.21097e-06 StartY=3 StartZ=0 EndX=5.21097e-06 EndY=19 EndZ=0
    g1: ArcOfCircle CenterX=19 CenterY=19 CenterZ=0 NormalX=0 NormalY=0 NormalZ=1 AngleXU=0 Radius=19 StartAngle=1.5708 EndAngle=3.14159
    g2: ArcOfCircle CenterX=19 CenterY=19 CenterZ=0 NormalX=0 NormalY=0 NormalZ=1 AngleXU=0 Radius=16 StartAngle=1.5708 EndAngle=3.14159
    g3: LineSegment StartX=114 StartY=35 StartZ=0 EndX=19 EndY=35 EndZ=0
    g4: LineSegment StartX=5.21097e-06 StartY=3 StartZ=0 EndX=5.21097e-06 EndY=0 EndZ=0
    g5: LineSegment StartX=3 StartY=0 StartZ=0 EndX=5.21097e-06 EndY=0 EndZ=0
    g6: LineSegment StartX=3 StartY=19 StartZ=0 EndX=3 EndY=0 EndZ=0
    g7: LineSegment StartX=19 StartY=38 StartZ=0 EndX=124 EndY=38 EndZ=0
    g8: Circle CenterX=119 CenterY=35 CenterZ=0 NormalX=0 NormalY=0 NormalZ=1 AngleXU=0 Radius=1
    g9: Circle CenterX=121 CenterY=35 CenterZ=0 NormalX=0 NormalY=0 NormalZ=1 AngleXU=0 Radius=1
    g10: Circle CenterX=121 CenterY=33 CenterZ=0 NormalX=0 NormalY=0 NormalZ=1 AngleXU=0 Radius=1
    g11: BSplineCurve PolesCount=3 KnotsCount=2 Degree=2 IsPeriodic=0
    g12: GeomPoint X=119 Y=35 Z=0
    g13: GeomPoint X=121 Y=33 Z=0
    g14: LineSegment StartX=119 StartY=35 StartZ=0 EndX=114 EndY=35 EndZ=0
    g15: ArcOfCircle CenterX=105 CenterY=19 CenterZ=0 NormalX=0 NormalY=0 NormalZ=1 AngleXU=0 Radius=19 StartAngle=5.7297 EndAngle=6.28319
    g16: ArcOfCircle CenterX=105 CenterY=19 CenterZ=0 NormalX=0 NormalY=0 NormalZ=1 AngleXU=0 Radius=16 StartAngle=5.60905 EndAngle=6.28319
    g17: LineSegment StartX=121 StartY=33 StartZ=0 EndX=121 EndY=19 EndZ=0
    g18: LineSegment StartX=124 StartY=38 StartZ=0 EndX=124 EndY=19 EndZ=0
    g19: LineSegment StartX=117.5 StartY=9.01251 StartZ=0 EndX=121.163 EndY=9.0125 EndZ=0
  constraints (46):
    c: Vertical(g0)
    c: Block(g0)
    c: Coincident(g1,g0)
    c: Block(g1)
    c: Coincident(g2,g1)
    c: Block(g2)
    c: Coincident(g3,g2)
    c: Horizontal(g3)
    c: Tangent(g3,g2)
    c: Coincident(g4,g0)
    c: Distance(g4) = 3
    c: Vertical(g4)
    c: Coincident(g5,g4)
    c: Horizontal(g5)
    c: Coincident(g6,g2)
    c: Coincident(g6,g5)
    c: Vertical(g6)
    c: Horizontal(g7)
    c: Distance(g7) = 105
    c: Coincident(g7,g1)
    c: Block(g3)
    c: Weight(g8) = 1
    c: Equal(g8,g9)
    c: Equal(g8,g10)
    c: InternalAlignment(g8,g11)
    c: InternalAlignment(g9,g11)
    c: InternalAlignment(g10,g11)
    c: InternalAlignment(g12,g11)
    c: InternalAlignment(g13,g11)
    c: Block(g11)
    c: Coincident(g14,g11)
    c: Coincident(g14,g3)
    c: Horizontal(g14)
    c: Block(g15)
    c: Coincident(g16,g15)
    c: Block(g16)
    c: Coincident(g17,g11)
    c: Coincident(g17,g16)
    c: Vertical(g17)
    c: Distance(g17) = 14
    c: Coincident(g18,g7)
    c: Coincident(g18,g15)
    c: Vertical(g18)
    c: Distance(g18) = 19
    c: Coincident(g19,g16)
    c: Coincident(g19,g15)
FEATURE [Part::Extrusion] Extrude049  label="top023"
  Base = -> Sketch058
  Dir = (0,0,1)
  DirMode = 2
  FaceMakerClass = Part::FaceMakerBullseye
  LengthFwd = 72
  LengthRev = 0
  Solid = true
  Symmetric = false
FEATURE [Sketcher::SketchObject] Sketch059
  FullyConstrained = true
  MapMode = 3
  Placement = pos=(0,0,0) rot=(1,0,0;1.5708rad)
  Support = -> [Extrude049]
  sketch-geometry (8):
    g0: Circle CenterX=80.351 CenterY=-67.6202 CenterZ=0 NormalX=0 NormalY=0 NormalZ=1 AngleXU=0 Radius=2
    g1: Circle CenterX=80.351 CenterY=-67.6202 CenterZ=0 NormalX=0 NormalY=0 NormalZ=1 AngleXU=0 Radius=3
    g2: Circle CenterX=80.351 CenterY=-4.92017 CenterZ=0 NormalX=0 NormalY=0 NormalZ=1 AngleXU=0 Radius=2
    g3: Circle CenterX=80.351 CenterY=-4.92017 CenterZ=0 NormalX=0 NormalY=0 NormalZ=1 AngleXU=0 Radius=3
    g4: Circle CenterX=23.851 CenterY=-4.92017 CenterZ=0 NormalX=0 NormalY=0 NormalZ=1 AngleXU=0 Radius=2
    g5: Circle CenterX=23.851 CenterY=-4.92017 CenterZ=0 NormalX=0 NormalY=0 NormalZ=1 AngleXU=0 Radius=3
    g6: Circle CenterX=23.851 CenterY=-67.6202 CenterZ=0 NormalX=0 NormalY=0 NormalZ=1 AngleXU=0 Radius=2
    g7: Circle CenterX=23.851 CenterY=-67.6202 CenterZ=0 NormalX=0 NormalY=0 NormalZ=1 AngleXU=0 Radius=3
  constraints (8):
    c: Block(g3)
    c: Block(g2)
    c: Block(g1)
    c: Block(g0)
    c: Block(g6)
    c: Block(g7)
    c: Block(g4)
    c: Block(g5)
FEATURE [Sketcher::SketchObject] Sketch060
  FullyConstrained = true
  MapMode = 3
  Placement = pos=(0,0,0) rot=(1,0,0;1.5708rad)
  Support = -> [Extrude049]
  sketch-geometry (8):
    g0: Circle CenterX=80.351 CenterY=-67.6202 CenterZ=0 NormalX=0 NormalY=0 NormalZ=1 AngleXU=0 Radius=3
    g1: Circle CenterX=80.351 CenterY=-4.92017 CenterZ=0 NormalX=0 NormalY=0 NormalZ=1 AngleXU=0 Radius=3
    g2: Circle CenterX=23.851 CenterY=-4.92017 CenterZ=0 NormalX=0 NormalY=0 NormalZ=1 AngleXU=0 Radius=3
    g3: Circle CenterX=23.851 CenterY=-67.6202 CenterZ=0 NormalX=0 NormalY=0 NormalZ=1 AngleXU=0 Radius=3
    g4: Circle CenterX=23.851 CenterY=-67.6202 CenterZ=0 NormalX=0 NormalY=0 NormalZ=1 AngleXU=0 Radius=5
    g5: Circle CenterX=80.351 CenterY=-67.6202 CenterZ=0 NormalX=0 NormalY=0 NormalZ=1 AngleXU=0 Radius=5
    g6: Circle CenterX=23.851 CenterY=-4.92017 CenterZ=0 NormalX=0 NormalY=0 NormalZ=1 AngleXU=0 Radius=5
    g7: Circle CenterX=80.351 CenterY=-4.92017 CenterZ=0 NormalX=0 NormalY=0 NormalZ=1 AngleXU=0 Radius=5
  constraints (8):
    c: Block(g1)
    c: Block(g0)
    c: Block(g3)
    c: Block(g2)
    c: Block(g5)
    c: Block(g4)
    c: Block(g6)
    c: Block(g7)
FEATURE [Sketcher::SketchObject] Sketch061
  FullyConstrained = true
  MapMode = 3
  Placement = pos=(0,0,0) rot=(1,0,0;1.5708rad)
  sketch-geometry (8):
    g0: Circle CenterX=80.351 CenterY=-67.6202 CenterZ=0 NormalX=0 NormalY=0 NormalZ=1 AngleXU=0 Radius=3
    g1: Circle CenterX=80.351 CenterY=-4.92017 CenterZ=0 NormalX=0 NormalY=0 NormalZ=1 AngleXU=0 Radius=3
    g2: Circle CenterX=23.851 CenterY=-4.92017 CenterZ=0 NormalX=0 NormalY=0 NormalZ=1 AngleXU=0 Radius=3
    g3: Circle CenterX=23.851 CenterY=-67.6202 CenterZ=0 NormalX=0 NormalY=0 NormalZ=1 AngleXU=0 Radius=3
    g4: Circle CenterX=23.851 CenterY=-67.6202 CenterZ=0 NormalX=0 NormalY=0 NormalZ=1 AngleXU=0 Radius=5
    g5: Circle CenterX=80.351 CenterY=-67.6202 CenterZ=0 NormalX=0 NormalY=0 NormalZ=1 AngleXU=0 Radius=5
    g6: Circle CenterX=23.851 CenterY=-4.92017 CenterZ=0 NormalX=0 NormalY=0 NormalZ=1 AngleXU=0 Radius=5
    g7: Circle CenterX=80.351 CenterY=-4.92017 CenterZ=0 NormalX=0 NormalY=0 NormalZ=1 AngleXU=0 Radius=5
  constraints (8):
    c: Block(g1)
    c: Block(g0)
    c: Block(g3)
    c: Block(g2)
    c: Block(g5)
    c: Block(g4)
    c: Block(g6)
    c: Block(g7)
FEATURE [Sketcher::SketchObject] Sketch062  label="topSketch016"
  FullyConstrained = true
  sketch-geometry (20):
    g0: LineSegment StartX=5.21097e-06 StartY=3 StartZ=0 EndX=5.21097e-06 EndY=19 EndZ=0
    g1: ArcOfCircle CenterX=19 CenterY=19 CenterZ=0 NormalX=0 NormalY=0 NormalZ=1 AngleXU=0 Radius=19 StartAngle=1.5708 EndAngle=3.14159
    g2: ArcOfCircle CenterX=19 CenterY=19 CenterZ=0 NormalX=0 NormalY=0 NormalZ=1 AngleXU=0 Radius=16 StartAngle=1.5708 EndAngle=3.14159
    g3: LineSegment StartX=114 StartY=35 StartZ=0 EndX=19 EndY=35 EndZ=0
    g4: LineSegment StartX=5.21097e-06 StartY=3 StartZ=0 EndX=5.21097e-06 EndY=0 EndZ=0
    g5: LineSegment StartX=3 StartY=0 StartZ=0 EndX=5.21097e-06 EndY=0 EndZ=0
    g6: LineSegment StartX=3 StartY=19 StartZ=0 EndX=3 EndY=0 EndZ=0
    g7: LineSegment StartX=19 StartY=38 StartZ=0 EndX=124 EndY=38 EndZ=0
    g8: Circle CenterX=119 CenterY=35 CenterZ=0 NormalX=0 NormalY=0 NormalZ=1 AngleXU=0 Radius=1
    g9: Circle CenterX=121 CenterY=35 CenterZ=0 NormalX=0 NormalY=0 NormalZ=1 AngleXU=0 Radius=1
    g10: Circle CenterX=121 CenterY=33 CenterZ=0 NormalX=0 NormalY=0 NormalZ=1 AngleXU=0 Radius=1
    g11: BSplineCurve PolesCount=3 KnotsCount=2 Degree=2 IsPeriodic=0
    g12: GeomPoint X=119 Y=35 Z=0
    g13: GeomPoint X=121 Y=33 Z=0
    g14: LineSegment StartX=119 StartY=35 StartZ=0 EndX=114 EndY=35 EndZ=0
    g15: ArcOfCircle CenterX=105 CenterY=19 CenterZ=0 NormalX=0 NormalY=0 NormalZ=1 AngleXU=0 Radius=19 StartAngle=5.7297 EndAngle=6.28319
    g16: ArcOfCircle CenterX=105 CenterY=19 CenterZ=0 NormalX=0 NormalY=0 NormalZ=1 AngleXU=0 Radius=16 StartAngle=5.60905 EndAngle=6.28319
    g17: LineSegment StartX=121 StartY=33 StartZ=0 EndX=121 EndY=19 EndZ=0
    g18: LineSegment StartX=124 StartY=38 StartZ=0 EndX=124 EndY=19 EndZ=0
    g19: LineSegment StartX=117.5 StartY=9.01251 StartZ=0 EndX=121.163 EndY=9.0125 EndZ=0
  constraints (46):
    c: Vertical(g0)
    c: Block(g0)
    c: Coincident(g1,g0)
    c: Block(g1)
    c: Coincident(g2,g1)
    c: Block(g2)
    c: Coincident(g3,g2)
    c: Horizontal(g3)
    c: Tangent(g3,g2)
    c: Coincident(g4,g0)
    c: Distance(g4) = 3
    c: Vertical(g4)
    c: Coincident(g5,g4)
    c: Horizontal(g5)
    c: Coincident(g6,g2)
    c: Coincident(g6,g5)
    c: Vertical(g6)
    c: Horizontal(g7)
    c: Distance(g7) = 105
    c: Coincident(g7,g1)
    c: Block(g3)
    c: Weight(g8) = 1
    c: Equal(g8,g9)
    c: Equal(g8,g10)
    c: InternalAlignment(g8,g11)
    c: InternalAlignment(g9,g11)
    c: InternalAlignment(g10,g11)
    c: InternalAlignment(g12,g11)
    c: InternalAlignment(g13,g11)
    c: Block(g11)
    c: Coincident(g14,g11)
    c: Coincident(g14,g3)
    c: Horizontal(g14)
    c: Block(g15)
    c: Coincident(g16,g15)
    c: Block(g16)
    c: Coincident(g17,g11)
    c: Coincident(g17,g16)
    c: Vertical(g17)
    c: Distance(g17) = 14
    c: Coincident(g18,g7)
    c: Coincident(g18,g15)
    c: Vertical(g18)
    c: Distance(g18) = 19
    c: Coincident(g19,g16)
    c: Coincident(g19,g15)
FEATURE [Part::Extrusion] Extrude053  label="top024"
  Base = -> Sketch062
  Dir = (0,0,1)
  DirMode = 2
  FaceMakerClass = Part::FaceMakerBullseye
  LengthFwd = 72
  LengthRev = 0
  Solid = true
  Symmetric = false
FEATURE [Sketcher::SketchObject] Sketch063
  FullyConstrained = true
  MapMode = 3
  Placement = pos=(0,0,0) rot=(1,0,0;1.5708rad)
  Support = -> [Extrude053]
  sketch-geometry (8):
    g0: Circle CenterX=80.351 CenterY=-67.6202 CenterZ=0 NormalX=0 NormalY=0 NormalZ=1 AngleXU=0 Radius=2
    g1: Circle CenterX=80.351 CenterY=-67.6202 CenterZ=0 NormalX=0 NormalY=0 NormalZ=1 AngleXU=0 Radius=3
    g2: Circle CenterX=80.351 CenterY=-4.92017 CenterZ=0 NormalX=0 NormalY=0 NormalZ=1 AngleXU=0 Radius=2
    g3: Circle CenterX=80.351 CenterY=-4.92017 CenterZ=0 NormalX=0 NormalY=0 NormalZ=1 AngleXU=0 Radius=3
    g4: Circle CenterX=23.851 CenterY=-4.92017 CenterZ=0 NormalX=0 NormalY=0 NormalZ=1 AngleXU=0 Radius=2
    g5: Circle CenterX=23.851 CenterY=-4.92017 CenterZ=0 NormalX=0 NormalY=0 NormalZ=1 AngleXU=0 Radius=3
    g6: Circle CenterX=23.851 CenterY=-67.6202 CenterZ=0 NormalX=0 NormalY=0 NormalZ=1 AngleXU=0 Radius=2
    g7: Circle CenterX=23.851 CenterY=-67.6202 CenterZ=0 NormalX=0 NormalY=0 NormalZ=1 AngleXU=0 Radius=3
  constraints (8):
    c: Block(g3)
    c: Block(g2)
    c: Block(g1)
    c: Block(g0)
    c: Block(g6)
    c: Block(g7)
    c: Block(g4)
    c: Block(g5)
FEATURE [Part::Extrusion] Extrude054
  Base = -> Sketch063
  Dir = (0,-1,2e-16)
  DirMode = 2
  FaceMakerClass = Part::FaceMakerBullseye
  LengthFwd = 6
  LengthRev = 0
  Placement = pos=(0,9,0) rot=(0,0,1;0rad)
  Solid = true
  Symmetric = false
FEATURE [Sketcher::SketchObject] Sketch064  label="topSketch017"
  FullyConstrained = true
  sketch-geometry (20):
    g0: LineSegment StartX=5.21097e-06 StartY=3 StartZ=0 EndX=5.21097e-06 EndY=19 EndZ=0
    g1: ArcOfCircle CenterX=19 CenterY=19 CenterZ=0 NormalX=0 NormalY=0 NormalZ=1 AngleXU=0 Radius=19 StartAngle=1.5708 EndAngle=3.14159
    g2: ArcOfCircle CenterX=19 CenterY=19 CenterZ=0 NormalX=0 NormalY=0 NormalZ=1 AngleXU=0 Radius=16 StartAngle=1.5708 EndAngle=3.14159
    g3: LineSegment StartX=114 StartY=35 StartZ=0 EndX=19 EndY=35 EndZ=0
    g4: LineSegment StartX=5.21097e-06 StartY=3 StartZ=0 EndX=5.21097e-06 EndY=0 EndZ=0
    g5: LineSegment StartX=3 StartY=0 StartZ=0 EndX=5.21097e-06 EndY=0 EndZ=0
    g6: LineSegment StartX=3 StartY=19 StartZ=0 EndX=3 EndY=0 EndZ=0
    g7: LineSegment StartX=19 StartY=38 StartZ=0 EndX=124 EndY=38 EndZ=0
    g8: Circle CenterX=119 CenterY=35 CenterZ=0 NormalX=0 NormalY=0 NormalZ=1 AngleXU=0 Radius=1
    g9: Circle CenterX=121 CenterY=35 CenterZ=0 NormalX=0 NormalY=0 NormalZ=1 AngleXU=0 Radius=1
    g10: Circle CenterX=121 CenterY=33 CenterZ=0 NormalX=0 NormalY=0 NormalZ=1 AngleXU=0 Radius=1
    g11: BSplineCurve PolesCount=3 KnotsCount=2 Degree=2 IsPeriodic=0
    g12: GeomPoint X=119 Y=35 Z=0
    g13: GeomPoint X=121 Y=33 Z=0
    g14: LineSegment StartX=119 StartY=35 StartZ=0 EndX=114 EndY=35 EndZ=0
    g15: ArcOfCircle CenterX=105 CenterY=19 CenterZ=0 NormalX=0 NormalY=0 NormalZ=1 AngleXU=0 Radius=19 StartAngle=5.7297 EndAngle=6.28319
    g16: ArcOfCircle CenterX=105 CenterY=19 CenterZ=0 NormalX=0 NormalY=0 NormalZ=1 AngleXU=0 Radius=16 StartAngle=5.60905 EndAngle=6.28319
    g17: LineSegment StartX=121 StartY=33 StartZ=0 EndX=121 EndY=19 EndZ=0
    g18: LineSegment StartX=124 StartY=38 StartZ=0 EndX=124 EndY=19 EndZ=0
    g19: LineSegment StartX=117.5 StartY=9.01251 StartZ=0 EndX=121.163 EndY=9.0125 EndZ=0
  constraints (46):
    c: Vertical(g0)
    c: Block(g0)
    c: Coincident(g1,g0)
    c: Block(g1)
    c: Coincident(g2,g1)
    c: Block(g2)
    c: Coincident(g3,g2)
    c: Horizontal(g3)
    c: Tangent(g3,g2)
    c: Coincident(g4,g0)
    c: Distance(g4) = 3
    c: Vertical(g4)
    c: Coincident(g5,g4)
    c: Horizontal(g5)
    c: Coincident(g6,g2)
    c: Coincident(g6,g5)
    c: Vertical(g6)
    c: Horizontal(g7)
    c: Distance(g7) = 105
    c: Coincident(g7,g1)
    c: Block(g3)
    c: Weight(g8) = 1
    c: Equal(g8,g9)
    c: Equal(g8,g10)
    c: InternalAlignment(g8,g11)
    c: InternalAlignment(g9,g11)
    c: InternalAlignment(g10,g11)
    c: InternalAlignment(g12,g11)
    c: InternalAlignment(g13,g11)
    c: Block(g11)
    c: Coincident(g14,g11)
    c: Coincident(g14,g3)
    c: Horizontal(g14)
    c: Block(g15)
    c: Coincident(g16,g15)
    c: Block(g16)
    c: Coincident(g17,g11)
    c: Coincident(g17,g16)
    c: Vertical(g17)
    c: Distance(g17) = 14
    c: Coincident(g18,g7)
    c: Coincident(g18,g15)
    c: Vertical(g18)
    c: Distance(g18) = 19
    c: Coincident(g19,g16)
    c: Coincident(g19,g15)
FEATURE [Sketcher::SketchObject] Sketch065
  FullyConstrained = true
  MapMode = 3
  Placement = pos=(0,0,0) rot=(1,0,0;1.5708rad)
  sketch-geometry (8):
    g0: Circle CenterX=80.351 CenterY=-67.6202 CenterZ=0 NormalX=0 NormalY=0 NormalZ=1 AngleXU=0 Radius=3
    g1: Circle CenterX=80.351 CenterY=-4.92017 CenterZ=0 NormalX=0 NormalY=0 NormalZ=1 AngleXU=0 Radius=3
    g2: Circle CenterX=23.851 CenterY=-4.92017 CenterZ=0 NormalX=0 NormalY=0 NormalZ=1 AngleXU=0 Radius=3
    g3: Circle CenterX=23.851 CenterY=-67.6202 CenterZ=0 NormalX=0 NormalY=0 NormalZ=1 AngleXU=0 Radius=3
    g4: Circle CenterX=23.851 CenterY=-67.6202 CenterZ=0 NormalX=0 NormalY=0 NormalZ=1 AngleXU=0 Radius=5
    g5: Circle CenterX=80.351 CenterY=-67.6202 CenterZ=0 NormalX=0 NormalY=0 NormalZ=1 AngleXU=0 Radius=5
    g6: Circle CenterX=23.851 CenterY=-4.92017 CenterZ=0 NormalX=0 NormalY=0 NormalZ=1 AngleXU=0 Radius=5
    g7: Circle CenterX=80.351 CenterY=-4.92017 CenterZ=0 NormalX=0 NormalY=0 NormalZ=1 AngleXU=0 Radius=5
  constraints (8):
    c: Block(g1)
    c: Block(g0)
    c: Block(g3)
    c: Block(g2)
    c: Block(g5)
    c: Block(g4)
    c: Block(g6)
    c: Block(g7)
FEATURE [Part::Extrusion] Extrude056
  Base = -> Sketch065
  Dir = (0,-1,2e-16)
  DirMode = 2
  FaceMakerClass = Part::FaceMakerBullseye
  LengthFwd = 2
  LengthRev = 0
  Solid = true
  Symmetric = false
FEATURE [Part::Extrusion] Extrude057  label="top025"
  Base = -> Sketch064
  Dir = (0,0,1)
  DirMode = 2
  FaceMakerClass = Part::FaceMakerBullseye
  LengthFwd = 72
  LengthRev = 0
  Solid = true
  Symmetric = false
FEATURE [Sketcher::SketchObject] Sketch066
  FullyConstrained = true
  MapMode = 3
  Placement = pos=(0,0,0) rot=(1,0,0;1.5708rad)
  Support = -> [Extrude057]
  sketch-geometry (8):
    g0: Circle CenterX=80.351 CenterY=-67.6202 CenterZ=0 NormalX=0 NormalY=0 NormalZ=1 AngleXU=0 Radius=3
    g1: Circle CenterX=80.351 CenterY=-4.92017 CenterZ=0 NormalX=0 NormalY=0 NormalZ=1 AngleXU=0 Radius=3
    g2: Circle CenterX=23.851 CenterY=-4.92017 CenterZ=0 NormalX=0 NormalY=0 NormalZ=1 AngleXU=0 Radius=3
    g3: Circle CenterX=23.851 CenterY=-67.6202 CenterZ=0 NormalX=0 NormalY=0 NormalZ=1 AngleXU=0 Radius=3
    g4: Circle CenterX=23.851 CenterY=-67.6202 CenterZ=0 NormalX=0 NormalY=0 NormalZ=1 AngleXU=0 Radius=5
    g5: Circle CenterX=80.351 CenterY=-67.6202 CenterZ=0 NormalX=0 NormalY=0 NormalZ=1 AngleXU=0 Radius=5
    g6: Circle CenterX=23.851 CenterY=-4.92017 CenterZ=0 NormalX=0 NormalY=0 NormalZ=1 AngleXU=0 Radius=5
    g7: Circle CenterX=80.351 CenterY=-4.92017 CenterZ=0 NormalX=0 NormalY=0 NormalZ=1 AngleXU=0 Radius=5
  constraints (8):
    c: Block(g1)
    c: Block(g0)
    c: Block(g3)
    c: Block(g2)
    c: Block(g5)
    c: Block(g4)
    c: Block(g6)
    c: Block(g7)
FEATURE [Part::Extrusion] Extrude055
  Base = -> Sketch066
  Dir = (0,-1,2e-16)
  DirMode = 2
  FaceMakerClass = Part::FaceMakerBullseye
  LengthFwd = 2
  LengthRev = 0
  Solid = true
  Symmetric = false
FEATURE [Part::Fillet] Fillet041
  Base = -> Extrude056
  Edges = 4 edges r=1.99: [Edge6,Edge12,Edge18,Edge24]
FEATURE [Part::Cut] Cut045
  Base = -> Extrude055
  Placement = pos=(0,6,0) rot=(0,0,1;0rad)
  Tool = -> Fillet041
FEATURE [Part::MultiFuse] Fusion095  label="pcbScrewPillars"
  Placement = pos=(-3.2,-1,72.3) rot=(0,0,1;0rad)
  Shapes = -> [Cut045,Extrude054]
FEATURE [Part::Feature] Face113
  shape: bbox 3.2 x 1.5 x 2e-07 mm, 1 faces, 0 solids (baked)
FEATURE [Part::Revolution] Revolve121  label="backCaseScrewRetainer002"
  Angle = 360
  Axis = (0,1,0)
  Base = (0,0,0)
  FaceMakerClass = Part::FaceMakerBullseye
  Placement = pos=(12.5,3,62) rot=(0,0,1;0rad)
  Solid = false
  Source = -> Face113
  Symmetric = false
FEATURE [Part::Feature] Face114
  shape: bbox 3.2 x 1.5 x 2e-07 mm, 1 faces, 0 solids (baked)
FEATURE [Part::Feature] Face115
  shape: bbox 3.2 x 1.5 x 2e-07 mm, 1 faces, 0 solids (baked)
FEATURE [Part::Feature] Face116
  shape: bbox 3.2 x 1.5 x 2e-07 mm, 1 faces, 0 solids (baked)
FEATURE [Part::Revolution] Revolve122  label="frontCaseScrewRetainer004"
  Angle = 360
  Axis = (0,1,0)
  Base = (0,0,0)
  FaceMakerClass = Part::FaceMakerBullseye
  Placement = pos=(89.5,3,68.5) rot=(0,0,1;0rad)
  Solid = false
  Source = -> Face115
  Symmetric = false
FEATURE [Part::Revolution] Revolve123  label="frontCaseScrewRetainer005"
  Angle = 360
  Axis = (0,1,0)
  Base = (0,0,0)
  FaceMakerClass = Part::FaceMakerBullseye
  Placement = pos=(89.5,3,3.5) rot=(0,0,1;0rad)
  Solid = false
  Source = -> Face116
  Symmetric = false
FEATURE [Part::Revolution] Revolve124  label="backCaseScrewRetainer003"
  Angle = 360
  Axis = (0,1,0)
  Base = (0,0,0)
  FaceMakerClass = Part::FaceMakerBullseye
  Placement = pos=(12.5,3,10) rot=(0,0,1;0rad)
  Solid = false
  Source = -> Face114
  Symmetric = false
FEATURE [Part::Feature] Face117
  shape: bbox 3.6 x 3.2 x 2e-07 mm, 1 faces, 0 solids (baked)
FEATURE [Part::Revolution] Revolve125  label="moreFrontCaseScrewRetainer004"
  Angle = 360
  Axis = (0,1,0)
  Base = (0,0,0)
  FaceMakerClass = Part::FaceMakerBullseye
  Placement = pos=(109.5,4.5,68.5) rot=(0,0,1;0rad)
  Solid = false
  Source = -> Face117
  Symmetric = false
FEATURE [Part::Feature] Face118
  shape: bbox 3.6 x 3.2 x 2e-07 mm, 1 faces, 0 solids (baked)
FEATURE [Part::Revolution] Revolve126  label="moreFrontCaseScrewRetainer005"
  Angle = 360
  Axis = (0,1,0)
  Base = (0,0,0)
  FaceMakerClass = Part::FaceMakerBullseye
  Placement = pos=(109.5,4.5,3.5) rot=(0,0,1;0rad)
  Solid = false
  Source = -> Face118
  Symmetric = false
FEATURE [Part::MultiFuse] Fusion096  label="screwRetainers001"
  Shapes = -> [Revolve126,Revolve125,Revolve124,Revolve123,Revolve122,Revolve121]
FEATURE [Part::Feature] Face119
  shape: bbox 10 x 16.5 x 2e-07 mm, 1 faces, 0 solids (baked)
FEATURE [Part::Revolution] Revolve130  label="plugHousing050"
  Angle = 360
  Axis = (0,1,0)
  Base = (0,0,0)
  FaceMakerClass = Part::FaceMakerBullseye
  Placement = pos=(0,0,36.15) rot=(0,0,1;0rad)
  Solid = false
  Source = -> Face119
  Symmetric = false
FEATURE [Part::Feature] Face120
  shape: bbox 10 x 16.5 x 2e-07 mm, 1 faces, 0 solids (baked)
FEATURE [Part::Feature] Face121
  shape: bbox 10 x 16.5 x 2e-07 mm, 1 faces, 0 solids (baked)
FEATURE [Part::Revolution] Revolve127  label="plugHousing047"
  Angle = 360
  Axis = (0,1,0)
  Base = (0,0,0)
  FaceMakerClass = Part::FaceMakerBullseye
  Placement = pos=(0,0,36.15) rot=(0,0,1;0rad)
  Solid = false
  Source = -> Face121
  Symmetric = false
FEATURE [Part::Feature] Face122
  shape: bbox 10 x 16.5 x 2e-07 mm, 1 faces, 0 solids (baked)
FEATURE [Part::Feature] Face123
  shape: bbox 10 x 16.5 x 2e-07 mm, 1 faces, 0 solids (baked)
FEATURE [Part::Revolution] Revolve128  label="plugHousing048"
  Angle = 360
  Axis = (0,1,0)
  Base = (0,0,0)
  FaceMakerClass = Part::FaceMakerBullseye
  Placement = pos=(0,0,36.15) rot=(0,0,1;0rad)
  Solid = false
  Source = -> Face123
  Symmetric = false
FEATURE [Part::MultiFuse] Fusion100  label="plugHousing054"
  Placement = pos=(0,0,0) rot=(0,0,1;1.5708rad)
  Shapes = -> [Revolve130,Revolve128]
FEATURE [Part::Feature] Face124
  shape: bbox 10 x 16.5 x 2e-07 mm, 1 faces, 0 solids (baked)
FEATURE [Part::Feature] Face125
  shape: bbox 10 x 16.5 x 2e-07 mm, 1 faces, 0 solids (baked)
FEATURE [Part::Revolution] Revolve129  label="plugHousing049"
  Angle = 360
  Axis = (0,1,0)
  Base = (0,0,0)
  FaceMakerClass = Part::FaceMakerBullseye
  Placement = pos=(0,0,36.15) rot=(0,0,1;0rad)
  Solid = false
  Source = -> Face125
  Symmetric = false
FEATURE [Part::Feature] Face126
  shape: bbox 10 x 16.5 x 2e-07 mm, 1 faces, 0 solids (baked)
FEATURE [Part::Revolution] Revolve131  label="plugHousing058"
  Angle = 360
  Axis = (0,1,0)
  Base = (0,0,0)
  FaceMakerClass = Part::FaceMakerBullseye
  Placement = pos=(0,0,36.15) rot=(0,0,1;0rad)
  Solid = false
  Source = -> Face120
  Symmetric = false
FEATURE [Part::MultiFuse] Fusion099  label="plugHousing053"
  Placement = pos=(0,0,0) rot=(0,0,1;1.5708rad)
  Shapes = -> [Revolve127,Revolve131]
FEATURE [Part::MultiFuse] Fusion102  label="plugHousing056"
  Placement = pos=(0,19,0) rot=(0,0,1;3.14159rad)
  Shapes = -> [Fusion100,Fusion099]
FEATURE [Part::Revolution] Revolve132  label="plugHousing059"
  Angle = 360
  Axis = (0,1,0)
  Base = (0,0,0)
  FaceMakerClass = Part::FaceMakerBullseye
  Placement = pos=(0,0,36.15) rot=(0,0,1;0rad)
  Solid = false
  Source = -> Face126
  Symmetric = false
FEATURE [Part::Revolution] Revolve133  label="plugHousing060"
  Angle = 360
  Axis = (0,1,0)
  Base = (0,0,0)
  FaceMakerClass = Part::FaceMakerBullseye
  Placement = pos=(0,0,36.15) rot=(0,0,1;0rad)
  Solid = false
  Source = -> Face122
  Symmetric = false
FEATURE [Part::MultiFuse] Fusion097  label="plugHousing051"
  Placement = pos=(0,0,0) rot=(0,0,1;1.5708rad)
  Shapes = -> [Revolve133,Revolve132]
FEATURE [Part::Revolution] Revolve134  label="plugHousing061"
  Angle = 360
  Axis = (0,1,0)
  Base = (0,0,0)
  FaceMakerClass = Part::FaceMakerBullseye
  Placement = pos=(0,0,36.15) rot=(0,0,1;0rad)
  Solid = false
  Source = -> Face124
  Symmetric = false
FEATURE [Part::MultiFuse] Fusion101  label="plugHousing055"
  Placement = pos=(0,0,0) rot=(0,0,1;1.5708rad)
  Shapes = -> [Revolve129,Revolve134]
FEATURE [Part::MultiFuse] Fusion098  label="plugHousing052"
  Placement = pos=(0,19,0) rot=(0,0,1;3.14159rad)
  Shapes = -> [Fusion097,Fusion101]
FEATURE [Part::MultiFuse] Fusion103  label="plugHousing057"
  Placement = pos=(122.621,0,-0.15) rot=(0,0,1;0rad)
  Shapes = -> [Fusion102,Fusion098]
FEATURE [Part::Box] Box028  label="Cube015"
  AttacherType = Attacher::AttachEngine3D
  Height = 28
  Length = 3
  Placement = pos=(110.7,19,22) rot=(0,0,1;0rad)
  Width = 15.7
FEATURE [Part::Cylinder] Cylinder044
  Angle = 360
  AttacherType = Attacher::AttachEngine3D
  Height = 20
  Placement = pos=(0,0,36.15) rot=(0,0,1;0rad)
  Radius = 10.3
FEATURE [Part::Cylinder] Cylinder045
  Angle = 360
  AttacherType = Attacher::AttachEngine3D
  Height = 10
  Placement = pos=(0,0,36.15) rot=(0,0,1;0rad)
  Radius = 4
FEATURE [Part::MultiFuse] Fusion104  label="removeToCreteHoleForPlugHousing040"
  Placement = pos=(70,19,36) rot=(0,1,0;1.5708rad)
  Shapes = -> [Cylinder044,Cylinder045]
FEATURE [Part::Cut] Cut046  label="plugHousingTab003"
  Base = -> Box028
  Tool = -> Fusion104
FEATURE [Part::MultiFuse] Fusion105  label="plugHousing062"
  Shapes = -> [Fusion103,Cut046]
FEATURE [Part::Fillet] Fillet042
  Base = -> Fusion105
  Edges = 1 edges r=2: [Edge25]
FEATURE [Part::Fillet] Fillet043  label="plugHousing063"
  Base = -> Fillet042
  Edges = 1 edges r=2: [Edge8]
  Placement = pos=(7,0,0) rot=(0,0,1;0rad)
FEATURE [Part::Feature] Face127
  shape: bbox 10 x 16.5 x 2e-07 mm, 1 faces, 0 solids (baked)
FEATURE [Part::Feature] Face128
  shape: bbox 10 x 16.5 x 2e-07 mm, 1 faces, 0 solids (baked)
FEATURE [Part::Revolution] Revolve137  label="plugHousing070"
  Angle = 360
  Axis = (0,1,0)
  Base = (0,0,0)
  FaceMakerClass = Part::FaceMakerBullseye
  Placement = pos=(0,0,36.15) rot=(0,0,1;0rad)
  Solid = false
  Source = -> Face127
  Symmetric = false
FEATURE [Part::Revolution] Revolve140  label="plugHousing073"
  Angle = 360
  Axis = (0,1,0)
  Base = (0,0,0)
  FaceMakerClass = Part::FaceMakerBullseye
  Placement = pos=(0,0,36.15) rot=(0,0,1;0rad)
  Solid = false
  Source = -> Face128
  Symmetric = false
FEATURE [Part::Feature] Face129
  shape: bbox 10 x 16.5 x 2e-07 mm, 1 faces, 0 solids (baked)
FEATURE [Part::Revolution] Revolve138  label="plugHousing071"
  Angle = 360
  Axis = (0,1,0)
  Base = (0,0,0)
  FaceMakerClass = Part::FaceMakerBullseye
  Placement = pos=(0,0,36.15) rot=(0,0,1;0rad)
  Solid = false
  Source = -> Face129
  Symmetric = false
FEATURE [Part::Feature] Face130
  shape: bbox 10 x 16.5 x 2e-07 mm, 1 faces, 0 solids (baked)
FEATURE [Part::Revolution] Revolve139  label="plugHousing072"
  Angle = 360
  Axis = (0,1,0)
  Base = (0,0,0)
  FaceMakerClass = Part::FaceMakerBullseye
  Placement = pos=(0,0,36.15) rot=(0,0,1;0rad)
  Solid = false
  Source = -> Face130
  Symmetric = false
FEATURE [Part::Feature] Face131
  shape: bbox 10 x 16.5 x 2e-07 mm, 1 faces, 0 solids (baked)
FEATURE [Part::Revolution] Revolve135  label="plugHousing068"
  Angle = 360
  Axis = (0,1,0)
  Base = (0,0,0)
  FaceMakerClass = Part::FaceMakerBullseye
  Placement = pos=(0,0,36.15) rot=(0,0,1;0rad)
  Solid = false
  Source = -> Face131
  Symmetric = false
FEATURE [Part::MultiFuse] Fusion112  label="plugHousing078"
  Placement = pos=(0,0,0) rot=(0,0,1;1.5708rad)
  Shapes = -> [Revolve135,Revolve139]
FEATURE [Part::Feature] Face132
  shape: bbox 10 x 16.5 x 2e-07 mm, 1 faces, 0 solids (baked)
FEATURE [Part::Revolution] Revolve141  label="plugHousing074"
  Angle = 360
  Axis = (0,1,0)
  Base = (0,0,0)
  FaceMakerClass = Part::FaceMakerBullseye
  Placement = pos=(0,0,36.15) rot=(0,0,1;0rad)
  Solid = false
  Source = -> Face132
  Symmetric = false
FEATURE [Part::MultiFuse] Fusion110  label="plugHousing076"
  Placement = pos=(0,0,0) rot=(0,0,1;1.5708rad)
  Shapes = -> [Revolve141,Revolve140]
FEATURE [Part::Feature] Face133
  shape: bbox 10 x 16.5 x 2e-07 mm, 1 faces, 0 solids (baked)
FEATURE [Part::Revolution] Revolve136  label="plugHousing069"
  Angle = 360
  Axis = (0,1,0)
  Base = (0,0,0)
  FaceMakerClass = Part::FaceMakerBullseye
  Placement = pos=(0,0,36.15) rot=(0,0,1;0rad)
  Solid = false
  Source = -> Face133
  Symmetric = false
FEATURE [Part::MultiFuse] Fusion106  label="plugHousing064"
  Placement = pos=(0,0,0) rot=(0,0,1;1.5708rad)
  Shapes = -> [Revolve138,Revolve136]
FEATURE [Part::MultiFuse] Fusion108  label="plugHousing066"
  Placement = pos=(0,19,0) rot=(0,0,1;3.14159rad)
  Shapes = -> [Fusion106,Fusion112]
FEATURE [Part::Feature] Face134
  shape: bbox 10 x 16.5 x 2e-07 mm, 1 faces, 0 solids (baked)
FEATURE [Part::Revolution] Revolve142  label="plugHousing075"
  Angle = 360
  Axis = (0,1,0)
  Base = (0,0,0)
  FaceMakerClass = Part::FaceMakerBullseye
  Placement = pos=(0,0,36.15) rot=(0,0,1;0rad)
  Solid = false
  Source = -> Face134
  Symmetric = false
FEATURE [Part::MultiFuse] Fusion107  label="plugHousing065"
  Placement = pos=(0,0,0) rot=(0,0,1;1.5708rad)
  Shapes = -> [Revolve137,Revolve142]
FEATURE [Part::MultiFuse] Fusion111  label="plugHousing077"
  Placement = pos=(0,19,0) rot=(0,0,1;3.14159rad)
  Shapes = -> [Fusion110,Fusion107]
FEATURE [Part::MultiFuse] Fusion109  label="plugHousing067"
  Placement = pos=(131.236,0,-0.15) rot=(0,0,1;0rad)
  Shapes = -> [Fusion108,Fusion111]
FEATURE [Part::MultiFuse] Fusion113  label="plugHousing079"
  Shapes = -> [Fillet043,Fusion109]
FEATURE [Part::Feature] Face135
  shape: bbox 3.5 x 17.8 x 2e-07 mm, 1 faces, 0 solids (baked)
FEATURE [Part::Revolution] Revolve143  label="removeToCreateScrewAndThreadedInsertHole049"
  Angle = 360
  Axis = (0,1,0)
  Base = (0,0,0)
  FaceMakerClass = Part::FaceMakerBullseye
  Placement = pos=(12.5,0,10) rot=(0,0,1;0rad)
  Solid = false
  Source = -> Face135
  Symmetric = false
FEATURE [Part::Feature] Face136
  shape: bbox 3.5 x 17.8 x 2e-07 mm, 1 faces, 0 solids (baked)
FEATURE [Part::Revolution] Revolve144  label="removeToCreateScrewAndThreadedInsertHole050"
  Angle = 360
  Axis = (0,1,0)
  Base = (0,0,0)
  FaceMakerClass = Part::FaceMakerBullseye
  Placement = pos=(12.5,0,62) rot=(0,0,1;0rad)
  Solid = false
  Source = -> Face136
  Symmetric = false
FEATURE [Part::Feature] Face137
  shape: bbox 3.5 x 17.8 x 2e-07 mm, 1 faces, 0 solids (baked)
FEATURE [Part::Revolution] Revolve145  label="removeToCreateScrewAndThreadedInsertHole051"
  Angle = 360
  Axis = (0,1,0)
  Base = (0,0,0)
  FaceMakerClass = Part::FaceMakerBullseye
  Placement = pos=(89.5,0,68.5) rot=(0,0,1;0rad)
  Solid = false
  Source = -> Face137
  Symmetric = false
FEATURE [Part::Feature] Face138
  shape: bbox 3.5 x 17.8 x 2e-07 mm, 1 faces, 0 solids (baked)
FEATURE [Part::Revolution] Revolve146  label="removeToCreateScrewAndThreadedInsertHole052"
  Angle = 360
  Axis = (0,1,0)
  Base = (0,0,0)
  FaceMakerClass = Part::FaceMakerBullseye
  Placement = pos=(89.5,0,3.5) rot=(0,0,1;0rad)
  Solid = false
  Source = -> Face138
  Symmetric = false
FEATURE [Part::Feature] Face139
  shape: bbox 3.5 x 17.8 x 2e-07 mm, 1 faces, 0 solids (baked)
FEATURE [Part::Revolution] Revolve147  label="removeToCreateScrewAndThreadedInsertHole053"
  Angle = 360
  Axis = (0,1,0)
  Base = (0,0,0)
  FaceMakerClass = Part::FaceMakerBullseye
  Placement = pos=(109.5,4.7,3.5) rot=(0,0,1;0rad)
  Solid = false
  Source = -> Face139
  Symmetric = false
FEATURE [Part::Feature] Face140
  shape: bbox 3.5 x 17.8 x 2e-07 mm, 1 faces, 0 solids (baked)
FEATURE [Part::Revolution] Revolve148  label="removeToCreateScrewAndThreadedInsertHole054"
  Angle = 360
  Axis = (0,1,0)
  Base = (0,0,0)
  FaceMakerClass = Part::FaceMakerBullseye
  Placement = pos=(109.5,4.7,68.5) rot=(0,0,1;0rad)
  Solid = false
  Source = -> Face140
  Symmetric = false
FEATURE [Part::MultiFuse] Fusion114  label="removeToCreateScrewAndThreadedInsertHole055"
  Shapes = -> [Revolve148,Revolve147,Revolve146,Revolve145,Revolve144,Revolve143]
FEATURE [Part::Cut] Cut047  label="casePillars004"
  Base = -> Cut037
  Tool = -> Fusion114
FEATURE [Part::Feature] Face141
  shape: bbox 3.5 x 17.8 x 2e-07 mm, 1 faces, 0 solids (baked)
FEATURE [Part::Feature] Face142
  shape: bbox 3.5 x 17.8 x 2e-07 mm, 1 faces, 0 solids (baked)
FEATURE [Part::Feature] Face143
  shape: bbox 3.5 x 17.8 x 2e-07 mm, 1 faces, 0 solids (baked)
FEATURE [Part::Revolution] Revolve149  label="removeToCreateScrewAndThreadedInsertHole057"
  Angle = 360
  Axis = (0,1,0)
  Base = (0,0,0)
  FaceMakerClass = Part::FaceMakerBullseye
  Placement = pos=(12.5,0,10) rot=(0,0,1;0rad)
  Solid = false
  Source = -> Face141
  Symmetric = false
FEATURE [Part::Feature] Face144
  shape: bbox 3.5 x 17.8 x 2e-07 mm, 1 faces, 0 solids (baked)
FEATURE [Part::Feature] Face145
  shape: bbox 3.5 x 17.8 x 2e-07 mm, 1 faces, 0 solids (baked)
FEATURE [Part::Feature] Face146
  shape: bbox 3.5 x 17.8 x 2e-07 mm, 1 faces, 0 solids (baked)
FEATURE [Part::Revolution] Revolve150  label="removeToCreateScrewAndThreadedInsertHole058"
  Angle = 360
  Axis = (0,1,0)
  Base = (0,0,0)
  FaceMakerClass = Part::FaceMakerBullseye
  Placement = pos=(12.5,0,62) rot=(0,0,1;0rad)
  Solid = false
  Source = -> Face146
  Symmetric = false
FEATURE [Part::Revolution] Revolve151  label="removeToCreateScrewAndThreadedInsertHole059"
  Angle = 360
  Axis = (0,1,0)
  Base = (0,0,0)
  FaceMakerClass = Part::FaceMakerBullseye
  Placement = pos=(89.5,0,68.5) rot=(0,0,1;0rad)
  Solid = false
  Source = -> Face143
  Symmetric = false
FEATURE [Part::Revolution] Revolve152  label="removeToCreateScrewAndThreadedInsertHole060"
  Angle = 360
  Axis = (0,1,0)
  Base = (0,0,0)
  FaceMakerClass = Part::FaceMakerBullseye
  Placement = pos=(89.5,0,3.5) rot=(0,0,1;0rad)
  Solid = false
  Source = -> Face142
  Symmetric = false
FEATURE [Part::Revolution] Revolve153  label="removeToCreateScrewAndThreadedInsertHole061"
  Angle = 360
  Axis = (0,1,0)
  Base = (0,0,0)
  FaceMakerClass = Part::FaceMakerBullseye
  Placement = pos=(109.5,4.7,3.5) rot=(0,0,1;0rad)
  Solid = false
  Source = -> Face145
  Symmetric = false
FEATURE [Part::Revolution] Revolve154  label="removeToCreateScrewAndThreadedInsertHole062"
  Angle = 360
  Axis = (0,1,0)
  Base = (0,0,0)
  FaceMakerClass = Part::FaceMakerBullseye
  Placement = pos=(109.5,4.7,68.5) rot=(0,0,1;0rad)
  Solid = false
  Source = -> Face144
  Symmetric = false
FEATURE [Part::MultiFuse] Fusion115  label="removeToCreateScrewAndThreadedInsertHole056"
  Shapes = -> [Revolve154,Revolve153,Revolve152,Revolve151,Revolve150,Revolve149]
FEATURE [Part::Feature] Face147
  shape: bbox 9.8 x 26.5 x 2e-07 mm, 1 faces, 0 solids (baked)
FEATURE [Part::Revolution] Revolve155
  Angle = 360
  Axis = (0,1,0)
  Base = (0,0,0)
  FaceMakerClass = Part::FaceMakerBullseye
  Placement = pos=(0,0,0) rot=(0,0,1;1.5708rad)
  Solid = false
  Source = -> Face147
  Symmetric = false
FEATURE [Part::Feature] Face148
  shape: bbox 9.8 x 26.5 x 2e-07 mm, 1 faces, 0 solids (baked)
FEATURE [Part::Revolution] Revolve156
  Angle = 360
  Axis = (0,1,0)
  Base = (0,0,0)
  FaceMakerClass = Part::FaceMakerBullseye
  Placement = pos=(0,0,0) rot=(0,0,1;1.5708rad)
  Solid = false
  Source = -> Face148
  Symmetric = false
FEATURE [Part::MultiFuse] Fusion116
  Placement = pos=(-18,19,36) rot=(0,0,1;0rad)
  Shapes = -> [Revolve156,Revolve155]
FEATURE [Part::Box] Box029  label="Cube016"
  AttacherType = Attacher::AttachEngine3D
  Height = 28
  Length = 3
  Placement = pos=(110.7,19,22) rot=(0,0,1;0rad)
  Width = 15.7
FEATURE [Part::Cylinder] Cylinder046
  Angle = 360
  AttacherType = Attacher::AttachEngine3D
  Height = 10
  Placement = pos=(0,0,36.15) rot=(0,0,1;0rad)
  Radius = 4
FEATURE [Part::Cylinder] Cylinder047
  Angle = 360
  AttacherType = Attacher::AttachEngine3D
  Height = 20
  Placement = pos=(0,0,36.15) rot=(0,0,1;0rad)
  Radius = 10.3
FEATURE [Part::MultiFuse] Fusion117  label="removeToCreteHoleForPlugHousing041"
  Placement = pos=(70,19,36) rot=(0,1,0;1.5708rad)
  Shapes = -> [Cylinder047,Cylinder046]
FEATURE [Part::Cut] Cut049  label="plugHousingTab004"
  Base = -> Box029
  Placement = pos=(-107.4,-14,0) rot=(0,0,1;0rad)
  Tool = -> Fusion117
FEATURE [Part::Box] Box030  label="Cube017"
  AttacherType = Attacher::AttachEngine3D
  Height = 28
  Length = 3
  Placement = pos=(110.7,19,22) rot=(0,0,1;0rad)
  Width = 15.7
FEATURE [Part::Cylinder] Cylinder048
  Angle = 360
  AttacherType = Attacher::AttachEngine3D
  Height = 10
  Placement = pos=(0,0,36.15) rot=(0,0,1;0rad)
  Radius = 4
FEATURE [Part::Cylinder] Cylinder049
  Angle = 360
  AttacherType = Attacher::AttachEngine3D
  Height = 20
  Placement = pos=(0,0,36.15) rot=(0,0,1;0rad)
  Radius = 10.3
FEATURE [Part::MultiFuse] Fusion118  label="removeToCreteHoleForPlugHousing042"
  Placement = pos=(70,19,36) rot=(0,1,0;1.5708rad)
  Shapes = -> [Cylinder049,Cylinder048]
FEATURE [Part::Cut] Cut050  label="plugHousingTab005"
  Base = -> Box030
  Placement = pos=(-107.4,-14,0) rot=(0,0,1;0rad)
  Tool = -> Fusion118
FEATURE [Part::MultiFuse] Fusion119
  Placement = pos=(9.6,23,0) rot=(0,0,1;3.14159rad)
  Shapes = -> [Cut049,Cut050]
FEATURE [Part::Box] Box031  label="Cube018"
  AttacherType = Attacher::AttachEngine3D
  Height = 10
  Length = 3
  Placement = pos=(3.3,4,12) rot=(0,0,1;0rad)
  Width = 10
FEATURE [Part::Fillet] Fillet044
  Base = -> Box031
  Edges = 1 edges r=2: [Edge11]
FEATURE [Part::Box] Box032  label="Cube019"
  AttacherType = Attacher::AttachEngine3D
  Height = 10
  Length = 3
  Placement = pos=(3.3,4,50) rot=(0,0,1;0rad)
  Width = 10
FEATURE [Part::Fillet] Fillet045
  Base = -> Box032
  Edges = 1 edges r=2: [Edge12]
FEATURE [Part::Box] Box033  label="Cube020"
  AttacherType = Attacher::AttachEngine3D
  Height = 28
  Length = 4
  Placement = pos=(5,0,22) rot=(0,0,1;0rad)
  Width = 10
FEATURE [Part::Fillet] Fillet046
  Base = -> Box033
  Edges = 1 edges r=1: [Edge7]
FEATURE [Part::Fillet] Fillet047
  Base = -> Fillet046
  Edges = 1 edges r=2: [Edge5]
FEATURE [Part::Fillet] Fillet048
  Base = -> Fillet047
  Edges = 1 edges r=2: [Edge2]
FEATURE [Part::Cylinder] Cylinder050
  Angle = 360
  AttacherType = Attacher::AttachEngine3D
  Height = 20
  Placement = pos=(0,0,36.15) rot=(0,0,1;0rad)
  Radius = 8.2
FEATURE [Part::Cylinder] Cylinder051
  Angle = 360
  AttacherType = Attacher::AttachEngine3D
  Height = 10
  Placement = pos=(0,0,36.15) rot=(0,0,1;0rad)
  Radius = 4
FEATURE [Part::MultiFuse] Fusion120  label="removeToCreteHoleForPlugHousing043"
  Placement = pos=(-42,19,36) rot=(0,1,0;1.5708rad)
  Shapes = -> [Cylinder050,Cylinder051]
FEATURE [Sketcher::SketchObject] Sketch067  label="topSketch018"
  FullyConstrained = true
  sketch-geometry (4):
    g0: LineSegment StartX=16.8446 StartY=31.512 StartZ=0 EndX=16.3251 EndY=34.4666 EndZ=0
    g1: ArcOfCircle CenterX=19 CenterY=19.2524 CenterZ=0 NormalX=0 NormalY=0 NormalZ=1 AngleXU=0 Radius=15.4476 StartAngle=1.74483 EndAngle=2.72717
    g2: ArcOfCircle CenterX=19 CenterY=19.2524 CenterZ=0 NormalX=0 NormalY=0 NormalZ=1 AngleXU=0 Radius=12.4476 StartAngle=1.74483 EndAngle=2.73189
    g3: LineSegment StartX=4.86004 StartY=25.4725 StartZ=0 EndX=7.58253 EndY=24.2107 EndZ=0
  constraints (7):
    c: Block(g0)
    c: Coincident(g1,g0)
    c: Coincident(g2,g0)
    c: Coincident(g3,g1)
    c: Coincident(g3,g2)
    c: Block(g1)
    c: Block(g2)
FEATURE [Part::Extrusion] Extrude058
  Base = -> Sketch067
  Dir = (0,0,1)
  DirMode = 2
  FaceMakerClass = Part::FaceMakerBullseye
  LengthFwd = 10
  LengthRev = 0
  Placement = pos=(0,0,31) rot=(0,0,1;0rad)
  Solid = true
  Symmetric = false
FEATURE [Part::Cut] Cut051
  Base = -> Extrude058
  Tool = -> Fusion120
FEATURE [Part::Fillet] Fillet049
  Base = -> Cut051
  Edges = 1 edges r=2: [Edge1]
FEATURE [Part::Fillet] Fillet050
  Base = -> Fillet049
  Edges = 1 edges r=2.5: [Edge1]
FEATURE [Part::Fillet] Fillet051
  Base = -> Fillet050
  Edges = 1 edges r=2.5: [Edge2]
FEATURE [Part::MultiFuse] Fusion121  label="wireHolder003"
  Shapes = -> [Fusion116,Fillet051]
FEATURE [Part::MultiFuse] Fusion122
  Shapes = -> [Fillet045,Fusion121]
FEATURE [Part::MultiFuse] Fusion123  label="wireHolder004"
  Shapes = -> [Fusion122,Fillet048]
FEATURE [Part::MultiFuse] Fusion124  label="wireHolder005"
  Shapes = -> [Fillet044,Fusion119,Fusion123]
FEATURE [Sketcher::SketchObject] Sketch068  label="topSketch019"
  FullyConstrained = true
  sketch-geometry (6):
    g0: LineSegment StartX=19 StartY=38 StartZ=0 EndX=117 EndY=38 EndZ=0
    g1: ArcOfCircle CenterX=19 CenterY=19 CenterZ=0 NormalX=0 NormalY=0 NormalZ=1 AngleXU=0 Radius=19 StartAngle=1.5708 EndAngle=3.14159
    g2: LineSegment StartX=117 StartY=38 StartZ=0 EndX=117 EndY=19 EndZ=0
    g3: LineSegment StartX=98 StartY=1.0161e-12 StartZ=0 EndX=5.22862e-06 EndY=1.0161e-12 EndZ=0
    g4: LineSegment StartX=5.22862e-06 StartY=19 StartZ=0 EndX=5.22862e-06 EndY=1.0161e-12 EndZ=0
    g5: ArcOfCircle CenterX=98 CenterY=19 CenterZ=0 NormalX=0 NormalY=0 NormalZ=1 AngleXU=0 Radius=19 StartAngle=4.71239 EndAngle=6.28319
  constraints (16):
    c: Horizontal(g0)
    c: Distance(g0) = 98
    c: Coincident(g1,g0)
    c: Block(g1)
    c: Coincident(g2,g0)
    c: Vertical(g2)
    c: Distance(g2) = 19
    c: Horizontal(g3)
    c: Coincident(g4,g1)
    c: Vertical(g4)
    c: Coincident(g3,g4)
    c: Block(g3)
    c: Coincident(g5,g2)
    c: Coincident(g5,g3)
    c: Block(g0)
    c: Block(g5)
FEATURE [Part::Extrusion] Extrude059  label="sideA002"
  Base = -> Sketch068
  Dir = (0,0,1)
  DirMode = 2
  FaceMakerClass = Part::FaceMakerBullseye
  LengthFwd = 3
  LengthRev = 0
  Placement = pos=(0,0,-2.7) rot=(0,0,1;0rad)
  Solid = true
  Symmetric = false
FEATURE [Sketcher::SketchObject] Sketch069  label="topSketch020"
  FullyConstrained = true
  sketch-geometry (6):
    g0: LineSegment StartX=19 StartY=38 StartZ=0 EndX=117 EndY=38 EndZ=0
    g1: ArcOfCircle CenterX=19 CenterY=19 CenterZ=0 NormalX=0 NormalY=0 NormalZ=1 AngleXU=0 Radius=19 StartAngle=1.5708 EndAngle=3.14159
    g2: LineSegment StartX=117 StartY=38 StartZ=0 EndX=117 EndY=19 EndZ=0
    g3: LineSegment StartX=98 StartY=1.0161e-12 StartZ=0 EndX=5.22862e-06 EndY=1.0161e-12 EndZ=0
    g4: LineSegment StartX=5.22862e-06 StartY=19 StartZ=0 EndX=5.22862e-06 EndY=1.0161e-12 EndZ=0
    g5: ArcOfCircle CenterX=98 CenterY=19 CenterZ=0 NormalX=0 NormalY=0 NormalZ=1 AngleXU=0 Radius=19 StartAngle=4.71239 EndAngle=6.28319
  constraints (16):
    c: Horizontal(g0)
    c: Distance(g0) = 98
    c: Coincident(g1,g0)
    c: Block(g1)
    c: Coincident(g2,g0)
    c: Vertical(g2)
    c: Distance(g2) = 19
    c: Horizontal(g3)
    c: Coincident(g4,g1)
    c: Vertical(g4)
    c: Coincident(g3,g4)
    c: Block(g3)
    c: Coincident(g5,g2)
    c: Coincident(g5,g3)
    c: Block(g0)
    c: Block(g5)
FEATURE [Part::Extrusion] Extrude060  label="sideB002"
  Base = -> Sketch069
  Dir = (0,0,1)
  DirMode = 2
  FaceMakerClass = Part::FaceMakerBullseye
  LengthFwd = 3
  LengthRev = 0
  Placement = pos=(0,0,71.7) rot=(0,0,1;0rad)
  Solid = true
  Symmetric = false
FEATURE [Part::MultiFuse] Fusion127  label="removeFromBottom001"
  Placement = pos=(2,0,0) rot=(0,0,1;0rad)
  Shapes = -> [Extrude059,Extrude060]
FEATURE [Part::Cylinder] Cylinder052
  Angle = 360
  AttacherType = Attacher::AttachEngine3D
  Height = 20
  Placement = pos=(0,0,36.15) rot=(0,0,1;0rad)
  Radius = 14
FEATURE [Part::Cylinder] Cylinder053
  Angle = 360
  AttacherType = Attacher::AttachEngine3D
  Height = 10
  Placement = pos=(0,0,36.15) rot=(0,0,1;0rad)
  Radius = 4
FEATURE [Part::MultiFuse] Fusion128  label="removeToCreteHoleForPlugHousing044"
  Placement = pos=(70,19,36) rot=(0,1,0;1.5708rad)
  Shapes = -> [Cylinder052,Cylinder053]
FEATURE [Part::Cut] Cut052  label="bottom011"
  Base = -> Extrude043
  Tool = -> Fusion128
FEATURE [Part::Cut] Cut054  label="bottom012"
  Base = -> Cut052
  Tool = -> Fusion115
FEATURE [Sketcher::SketchObject] Sketch070
  FullyConstrained = true
  Placement = pos=(117,19,0) rot=(0.57735,0.57735,0.57735;2.0944rad)
  sketch-geometry (48):
    g0: LineSegment StartX=-49.19 StartY=69.25 StartZ=0 EndX=-49.19 EndY=66.25 EndZ=0
    g1: LineSegment StartX=-49.19 StartY=63.5 StartZ=0 EndX=-49.19 EndY=60.5 EndZ=0
    g2: LineSegment StartX=-49.19 StartY=57.75 StartZ=0 EndX=-49.19 EndY=54.75 EndZ=0
    g3: LineSegment StartX=-49.19 StartY=52 StartZ=0 EndX=-49.19 EndY=49 EndZ=0
    g4: LineSegment StartX=-49.19 StartY=46.25 StartZ=0 EndX=-49.19 EndY=43.25 EndZ=0
    g5: LineSegment StartX=-49.19 StartY=40.5 StartZ=0 EndX=-49.19 EndY=37.5 EndZ=0
    g6: LineSegment StartX=-49.19 StartY=34.5 StartZ=0 EndX=-49.19 EndY=31.5 EndZ=0
    g7: LineSegment StartX=-49.19 StartY=28.75 StartZ=0 EndX=-49.19 EndY=25.75 EndZ=0
    g8: LineSegment StartX=-49.19 StartY=23 StartZ=0 EndX=-49.19 EndY=20 EndZ=0
    g9: LineSegment StartX=-49.19 StartY=17.25 StartZ=0 EndX=-49.19 EndY=14.25 EndZ=0
    g10: LineSegment StartX=-49.19 StartY=11.5 StartZ=0 EndX=-49.19 EndY=8.5 EndZ=0
    g11: LineSegment StartX=-49.19 StartY=5.75 StartZ=0 EndX=-49.19 EndY=2.75 EndZ=0
    g12: ArcOfCircle CenterX=-1.5 CenterY=67.75 CenterZ=0 NormalX=0 NormalY=0 NormalZ=1 AngleXU=0 Radius=1.5 StartAngle=4.71239 EndAngle=7.85398
    g13: ArcOfCircle CenterX=-1.5 CenterY=62 CenterZ=0 NormalX=0 NormalY=0 NormalZ=1 AngleXU=0 Radius=1.5 StartAngle=4.71239 EndAngle=7.85398
    g14: ArcOfCircle CenterX=-1.5 CenterY=56.25 CenterZ=0 NormalX=0 NormalY=0 NormalZ=1 AngleXU=0 Radius=1.5 StartAngle=4.71239 EndAngle=7.85398
    g15: ArcOfCircle CenterX=-11.49 CenterY=50.5 CenterZ=0 NormalX=0 NormalY=0 NormalZ=1 AngleXU=0 Radius=1.5 StartAngle=4.71239 EndAngle=7.85398
    g16: ArcOfCircle CenterX=-16.28 CenterY=44.75 CenterZ=0 NormalX=0 NormalY=0 NormalZ=1 AngleXU=0 Radius=1.5 StartAngle=4.71239 EndAngle=7.85398
    g17: ArcOfCircle CenterX=-18.2337 CenterY=39 CenterZ=0 NormalX=0 NormalY=0 NormalZ=1 AngleXU=0 Radius=1.5 StartAngle=4.71485 EndAngle=7.85398
    g18: ArcOfCircle CenterX=-16.2837 CenterY=27.25 CenterZ=0 NormalX=0 NormalY=0 NormalZ=1 AngleXU=0 Radius=1.5 StartAngle=4.71485 EndAngle=7.85398
    g19: ArcOfCircle CenterX=-18.2337 CenterY=33 CenterZ=0 NormalX=0 NormalY=0 NormalZ=1 AngleXU=0 Radius=1.5 StartAngle=4.71485 EndAngle=7.85398
    g20: ArcOfCircle CenterX=-11.49 CenterY=21.5 CenterZ=0 NormalX=0 NormalY=0 NormalZ=1 AngleXU=0 Radius=1.5 StartAngle=4.71239 EndAngle=7.85398
    g21: ArcOfCircle CenterX=-1.5 CenterY=4.25 CenterZ=0 NormalX=0 NormalY=0 NormalZ=1 AngleXU=0 Radius=1.5 StartAngle=4.71239 EndAngle=7.85398
    g22: ArcOfCircle CenterX=-1.5 CenterY=10 CenterZ=0 NormalX=0 NormalY=0 NormalZ=1 AngleXU=0 Radius=1.5 StartAngle=4.71239 EndAngle=7.85398
    g23: ArcOfCircle CenterX=-1.5 CenterY=15.75 CenterZ=0 NormalX=0 NormalY=0 NormalZ=1 AngleXU=0 Radius=1.5 StartAngle=4.71239 EndAngle=7.85398
    g24: LineSegment StartX=-49.19 StartY=69.25 StartZ=0 EndX=-1.5 EndY=69.25 EndZ=0
    g25: LineSegment StartX=-49.19 StartY=66.25 StartZ=0 EndX=-1.5 EndY=66.25 EndZ=0
    g26: LineSegment StartX=-49.19 StartY=63.5 StartZ=0 EndX=-1.5 EndY=63.5 EndZ=0
    g27: LineSegment StartX=-49.19 StartY=60.5 StartZ=0 EndX=-1.5 EndY=60.5 EndZ=0
    g28: LineSegment StartX=-49.19 StartY=57.75 StartZ=0 EndX=-1.5 EndY=57.75 EndZ=0
    g29: LineSegment StartX=-49.19 StartY=54.75 StartZ=0 EndX=-1.5 EndY=54.75 EndZ=0
    g30: LineSegment StartX=-49.19 StartY=52 StartZ=0 EndX=-11.49 EndY=52 EndZ=0
    g31: LineSegment StartX=-49.19 StartY=49 StartZ=0 EndX=-11.49 EndY=49 EndZ=0
    g32: LineSegment StartX=-49.19 StartY=46.25 StartZ=0 EndX=-16.28 EndY=46.25 EndZ=0
    g33: LineSegment StartX=-49.19 StartY=43.25 StartZ=0 EndX=-16.28 EndY=43.25 EndZ=0
    g34: LineSegment StartX=-49.19 StartY=40.5 StartZ=0 EndX=-18.2337 EndY=40.5 EndZ=0
    g35: LineSegment StartX=-49.19 StartY=37.5 StartZ=0 EndX=-18.23 EndY=37.5 EndZ=0
    g36: LineSegment StartX=-49.19 StartY=34.5 StartZ=0 EndX=-18.2337 EndY=34.5 EndZ=0
    g37: LineSegment StartX=-49.19 StartY=31.5 StartZ=0 EndX=-18.23 EndY=31.5 EndZ=0
    g38: LineSegment StartX=-49.19 StartY=28.75 StartZ=0 EndX=-16.2837 EndY=28.75 EndZ=0
    g39: LineSegment StartX=-49.19 StartY=25.75 StartZ=0 EndX=-16.28 EndY=25.75 EndZ=0
    g40: LineSegment StartX=-49.19 StartY=23 StartZ=0 EndX=-11.49 EndY=23 EndZ=0
    g41: LineSegment StartX=-49.19 StartY=20 StartZ=0 EndX=-11.49 EndY=20 EndZ=0
    g42: LineSegment StartX=-49.19 StartY=17.25 StartZ=0 EndX=-1.5 EndY=17.25 EndZ=0
    g43: LineSegment StartX=-49.19 StartY=14.25 StartZ=0 EndX=-1.5 EndY=14.25 EndZ=0
    g44: LineSegment StartX=-49.19 StartY=11.5 StartZ=0 EndX=-1.5 EndY=11.5 EndZ=0
    g45: LineSegment StartX=-49.19 StartY=8.5 StartZ=0 EndX=-1.5 EndY=8.5 EndZ=0
    g46: LineSegment StartX=-49.19 StartY=5.75 StartZ=0 EndX=-1.5 EndY=5.75 EndZ=0
    g47: LineSegment StartX=-49.19 StartY=2.75 StartZ=0 EndX=-1.5 EndY=2.75 EndZ=0
  constraints (120):
    c: Vertical(g0)
    c: Distance(g0) = 3
    c: Block(g0)
    c: Vertical(g1)
    c: Distance(g1) = 3
    c: Vertical(g2)
    c: Equal(g0,g2) = 3
    c: Block(g2)
    c: Vertical(g3)
    c: Equal(g1,g3) = 3
    c: Vertical(g4)
    c: Equal(g0,g4) = 3
    c: Block(g4)
    c: Vertical(g5)
    c: Equal(g1,g5) = 3
    c: Vertical(g6)
    c: Equal(g0,g6) = 3
    c: Block(g6)
    c: Vertical(g7)
    c: Equal(g1,g7) = 3
    c: Vertical(g8)
    c: Equal(g0,g8) = 3
    c: Block(g8)
    c: Vertical(g9)
    c: Equal(g1,g9) = 3
    c: Vertical(g10)
    c: Equal(g0,g10) = 3
    c: Block(g10)
    c: Vertical(g11)
    c: Equal(g1,g11) = 3
    c: Block(g12)
    c: Block(g13)
    c: Block(g14)
    c: Block(g15)
    c: Block(g16)
    c: Block(g17)
    c: Block(g18)
    c: Block(g19)
    c: Block(g20)
    c: Block(g21)
    c: Block(g22)
    c: Block(g23)
    c: Block(g11)
    c: Block(g9)
    c: Block(g7)
    c: Block(g5)
    c: Block(g3)
    c: Block(g1)
    c: Coincident(g24,g0)
    c: Coincident(g24,g12)
    c: Horizontal(g24)
    c: Coincident(g25,g0)
    c: Coincident(g25,g12)
    c: Horizontal(g25)
    c: Coincident(g26,g1)
    c: Coincident(g26,g13)
    c: Horizontal(g26)
    c: Coincident(g27,g1)
    c: Coincident(g27,g13)
    c: Horizontal(g27)
    c: Coincident(g28,g2)
    c: Coincident(g28,g14)
    c: Horizontal(g28)
    c: Coincident(g29,g2)
    c: Coincident(g29,g14)
    c: Horizontal(g29)
    c: Coincident(g30,g3)
    c: Coincident(g30,g15)
    c: Horizontal(g30)
    c: Coincident(g31,g3)
    c: Coincident(g31,g15)
    c: Horizontal(g31)
    c: Coincident(g32,g4)
    c: Coincident(g32,g16)
    c: Horizontal(g32)
    c: Coincident(g33,g4)
    c: Coincident(g33,g16)
    c: Horizontal(g33)
    c: Coincident(g34,g5)
    c: Coincident(g34,g17)
    c: Horizontal(g34)
    c: Coincident(g35,g5)
    c: Coincident(g35,g17)
    c: Horizontal(g35)
    c: Coincident(g36,g6)
    c: Coincident(g36,g19)
    c: Horizontal(g36)
    c: Coincident(g37,g6)
    c: Coincident(g37,g19)
    c: Horizontal(g37)
    c: Coincident(g38,g7)
    c: Coincident(g38,g18)
    c: Horizontal(g38)
    c: Coincident(g39,g7)
    c: Coincident(g39,g18)
    c: Horizontal(g39)
    c: Coincident(g40,g8)
    c: Coincident(g40,g20)
    c: Horizontal(g40)
    c: Coincident(g41,g8)
    c: Coincident(g41,g20)
    c: Horizontal(g41)
    c: Coincident(g42,g9)
    c: Coincident(g42,g23)
    c: Horizontal(g42)
    c: Coincident(g43,g9)
    c: Coincident(g43,g23)
    c: Horizontal(g43)
    c: Coincident(g44,g10)
    c: Coincident(g44,g22)
    c: Horizontal(g44)
    c: Coincident(g45,g10)
    c: Coincident(g45,g22)
    c: Horizontal(g45)
    c: Coincident(g46,g11)
    c: Coincident(g46,g21)
    c: Horizontal(g46)
    c: Coincident(g47,g11)
    c: Coincident(g47,g21)
    c: Horizontal(g47)
FEATURE [Part::Extrusion] Extrude061
  Base = -> Sketch070
  Dir = (1,0,0)
  DirMode = 2
  FaceMakerClass = Part::FaceMakerBullseye
  LengthFwd = 23
  LengthRev = 0
  Placement = pos=(-19,0,0) rot=(0,0,1;0rad)
  Solid = true
  Symmetric = false
FEATURE [Part::Fillet] Fillet052  label="removeToCreateVentalationHoles002"
  Base = -> Extrude061
  Edges = <same value as first occurrence — deduplicated (x6 in doc)>
  Placement = pos=(7,0.02,0) rot=(0,0,1;0rad)
FEATURE [Part::MultiFuse] Fusion130  label="bottom013"
  Shapes = -> [Cut054,Cut034]
FEATURE [Part::Cut] Cut055
  Base = -> Fusion130
  Tool = -> Fillet052
FEATURE [Part::Cylinder] Cylinder054
  Angle = 360
  AttacherType = Attacher::AttachEngine3D
  Height = 20
  Placement = pos=(0,0,36.15) rot=(0,0,1;0rad)
  Radius = 4
FEATURE [Sketcher::SketchObject] Sketch071  label="bottomSketch002"
  FullyConstrained = true
  sketch-geometry (32):
    g0: LineSegment StartX=3.3 StartY=-6.03275e-07 StartZ=0 EndX=98 EndY=-6.03275e-07 EndZ=0
    g1: ArcOfCircle CenterX=98 CenterY=19 CenterZ=0 NormalX=0 NormalY=0 NormalZ=1 AngleXU=0 Radius=19 StartAngle=4.71239 EndAngle=5.71103
    g2: LineSegment StartX=6.3 StartY=8 StartZ=0 EndX=3.3 EndY=8 EndZ=0
    g3: LineSegment StartX=3.3 StartY=8 StartZ=0 EndX=3.3 EndY=-6.03275e-07 EndZ=0
    g4: ArcOfCircle CenterX=8.3 CenterY=5 CenterZ=0 NormalX=0 NormalY=0 NormalZ=1 AngleXU=0 Radius=2 StartAngle=3.14159 EndAngle=4.71239
    g5: LineSegment StartX=6.3 StartY=8 StartZ=0 EndX=6.3 EndY=5 EndZ=0
    g6: ArcOfCircle CenterX=98 CenterY=19 CenterZ=0 NormalX=0 NormalY=0 NormalZ=1 AngleXU=0 Radius=12.7 StartAngle=4.71239 EndAngle=6.28319
    g7: LineSegment StartX=94.7 StartY=3 StartZ=0 EndX=8.3 EndY=3 EndZ=0
    g8-g12: Circle x5 (B-spline internal-alignment scaffolding for g13; pole/knot coordinates omitted)
    g13: BSplineCurve PolesCount=5 KnotsCount=3 Degree=3 IsPeriodic=0
    g14: GeomPoint X=98 Y=6.3 Z=0
    g15: GeomPoint X=96.3938 Y=4.71946 Z=0
    g16: GeomPoint X=94.7 Y=3 Z=0
    g17-g23: Circle x7 (B-spline internal-alignment scaffolding for g24; pole/knot coordinates omitted)
    g24: BSplineCurve PolesCount=7 KnotsCount=5 Degree=3 IsPeriodic=0
    g25-g29: GeomPoint x5 (B-spline internal-alignment scaffolding for g24; pole/knot coordinates omitted)
    g30: ArcOfCircle CenterX=98 CenterY=19 CenterZ=0 NormalX=0 NormalY=0 NormalZ=1 AngleXU=0 Radius=15.7 StartAngle=5.81226 EndAngle=6.28319
    g31: LineSegment StartX=110.7 StartY=19 StartZ=0 EndX=113.7 EndY=19 EndZ=0
  constraints (41):
    c: Horizontal(g0)
    c: Coincident(g1,g0)
    c: Block(g1)
    c: Horizontal(g2)
    c: Distance(g2) = 3
    c: Coincident(g3,g2)
    c: Vertical(g3)
    c: Coincident(g3,g0)
    c: Block(g4)
    c: Block(g2)
    c: Coincident(g5,g2)
    c: Coincident(g5,g4)
    c: Vertical(g5)
    c: Coincident(g6,g1)
    c: Block(g6)
    c: Coincident(g7,g4)
    c: Horizontal(g7)
    c: Block(g0)
    c: Block(g7)
    c: Block(g3)
    c: Coincident(g13,g6)
    c: Weight(g8) = 1
    c: Equal(g8, g9-g12) x4
    c: Coincident(g13,g7)
    c: InternalAlignment(g8-g12 -> g13) x5
    c: InternalAlignment(g14,g13)
    c: InternalAlignment(g15,g13)
    c: InternalAlignment(g16,g13)
    c: Block(g13)
    c: Weight(g17) = 1
    c: Equal(g17, g18-g23) x6
    c: Coincident(g24,g1)
    c: InternalAlignment(g17-g23 -> g24) x7
    c: InternalAlignment(g25-g29 -> g24) x5
    c: Block(g24)
    c: Coincident(g30,g24)
    c: Coincident(g31,g6)
    c: Coincident(g31,g30)
    c: Horizontal(g31)
    c: Block(g31)
    c: Block(g30)
FEATURE [Part::Extrusion] Extrude062  label="bottom014"
  Base = -> Sketch071
  Dir = (0,0,1)
  DirMode = 2
  FaceMakerClass = Part::FaceMakerBullseye
  LengthFwd = 71.4
  LengthRev = 0
  Placement = pos=(0,0,0.3) rot=(0,0,1;0rad)
  Solid = true
  Symmetric = false
FEATURE [Part::Fillet] Fillet054
  Base = -> Extrude062
  Edges = 1 edges r=2.4: [Edge17]
FEATURE [Part::Fillet] Fillet055  label="bottom015"
  Base = -> Fillet054
  Edges = 1 edges r=2.4: [Edge36]
FEATURE [Part::Cylinder] Cylinder055
  Angle = 360
  AttacherType = Attacher::AttachEngine3D
  Height = 10
  Placement = pos=(0,0,36.15) rot=(0,0,1;0rad)
  Radius = 4
FEATURE [Part::MultiFuse] Fusion131  label="removeToCreateHoleForPlugHousing002"
  Placement = pos=(70,19,36.15) rot=(0,1,0;1.5708rad)
  Shapes = -> [Cylinder054,Cylinder055]
FEATURE [Part::Cut] Cut056  label="Bottom001"
  Base = -> Fillet055
  Placement = pos=(9,0,0) rot=(0,0,1;0rad)
  Tool = -> Fusion131
FEATURE [Part::Cut] Cut057
  Base = -> Cut055
  Tool = -> Cut056
FEATURE [Sketcher::SketchObject] Sketch072  label="topSketch021"
  FullyConstrained = true
  sketch-geometry (4):
    g0: ArcOfCircle CenterX=105 CenterY=19 CenterZ=0 NormalX=0 NormalY=0 NormalZ=1 AngleXU=0 Radius=20.6155 StartAngle=5.54125 EndAngle=6.28319
    g1: ArcOfCircle CenterX=105 CenterY=19 CenterZ=0 NormalX=0 NormalY=0 NormalZ=1 AngleXU=0 Radius=13 StartAngle=5.54125 EndAngle=6.28319
    g2: LineSegment StartX=118 StartY=19 StartZ=0 EndX=125.616 EndY=19 EndZ=0
    g3: LineSegment StartX=114.583 StartY=10.2157 StartZ=0 EndX=120.197 EndY=5.06982 EndZ=0
  constraints (7):
    c: Block(g0)
    c: Block(g1)
    c: Coincident(g2,g1)
    c: Coincident(g2,g0)
    c: Horizontal(g2)
    c: Coincident(g3,g1)
    c: Coincident(g3,g0)
FEATURE [Part::Extrusion] Extrude063  label="bottomPlugHousingBit003"
  Base = -> Sketch072
  Dir = (0,0,1)
  DirMode = 2
  FaceMakerClass = Part::FaceMakerBullseye
  LengthFwd = 72
  LengthRev = 0
  Solid = true
  Symmetric = false
FEATURE [Part::Cylinder] Cylinder056
  Angle = 360
  AttacherType = Attacher::AttachEngine3D
  Height = 20
  Placement = pos=(0,0,36.15) rot=(0,0,1;0rad)
  Radius = 14.3
FEATURE [Part::Cylinder] Cylinder057
  Angle = 360
  AttacherType = Attacher::AttachEngine3D
  Height = 10
  Placement = pos=(0,0,36.15) rot=(0,0,1;0rad)
  Radius = 4
FEATURE [Part::Box] Box034  label="removeToCreteHoleForPlugHousing047"
  AttacherType = Attacher::AttachEngine3D
  Height = 28.6
  Length = 20
  Placement = pos=(106.15,0,21.7) rot=(0,0,1;0rad)
  Width = 19
FEATURE [Part::Cylinder] Cylinder058
  Angle = 360
  AttacherType = Attacher::AttachEngine3D
  Height = 20
  Placement = pos=(0,0,36.15) rot=(0,0,1;0rad)
  Radius = 14.3
FEATURE [Part::Cylinder] Cylinder059
  Angle = 360
  AttacherType = Attacher::AttachEngine3D
  Height = 10
  Placement = pos=(0,0,36.15) rot=(0,0,1;0rad)
  Radius = 4
FEATURE [Part::MultiFuse] Fusion134  label="removeToCreteHoleForPlugHousing046"
  Placement = pos=(70,19,36) rot=(0,1,0;1.5708rad)
  Shapes = -> [Cylinder058,Cylinder059]
FEATURE [Part::Cylinder] Cylinder060
  Angle = 360
  AttacherType = Attacher::AttachEngine3D
  Height = 20
  Placement = pos=(0,0,36.15) rot=(0,0,1;0rad)
  Radius = 14
FEATURE [Part::Cylinder] Cylinder061
  Angle = 360
  AttacherType = Attacher::AttachEngine3D
  Height = 10
  Placement = pos=(0,0,36.15) rot=(0,0,1;0rad)
  Radius = 4
FEATURE [Part::MultiFuse] Fusion135  label="removeToCreteHoleForPlugHousing048"
  Placement = pos=(70,19,36) rot=(0,1,0;1.5708rad)
  Shapes = -> [Cylinder060,Cylinder061]
FEATURE [Part::Box] Box035  label="removeToCreteHoleForPlugHousing049"
  AttacherType = Attacher::AttachEngine3D
  Height = 28.6
  Length = 20
  Placement = pos=(106.15,0,21.7) rot=(0,0,1;0rad)
  Width = 19
FEATURE [Part::MultiFuse] Fusion133  label="removeToCreteHoleForPlugHousing045"
  Placement = pos=(0,0,-28.3) rot=(0,0,1;0rad)
  Shapes = -> [Box035,Fusion134]
FEATURE [Part::MultiFuse] Fusion138  label="removeToCreteHoleForPlugHousing051"
  Placement = pos=(70,19,36) rot=(0,1,0;1.5708rad)
  Shapes = -> [Cylinder056,Cylinder057]
FEATURE [Part::MultiFuse] Fusion137  label="removeToCreteHoleForPlugHousing050"
  Placement = pos=(0,0,28.3) rot=(0,0,1;0rad)
  Shapes = -> [Box034,Fusion138]
FEATURE [Part::MultiFuse] Fusion132  label="removeToCreatePlugHousingBottomBit002"
  Shapes = -> [Fusion133,Fusion137]
FEATURE [Part::MultiFuse] Fusion136  label="removeToCreatePlugHousingBottomBit003"
  Shapes = -> [Fusion135,Fusion132]
FEATURE [Part::Cut] Cut058  label="bottomPlugHousingBit002"
  Base = -> Extrude063
  Placement = pos=(-0.09,0,0) rot=(0,0,1;0rad)
  Tool = -> Fusion136
FEATURE [Sketcher::SketchObject] Sketch073  label="bottomSketch003"
  FullyConstrained = true
  sketch-geometry (45):
    g0: LineSegment StartX=6.29999 StartY=8 StartZ=0 EndX=3.29999 EndY=8 EndZ=0
    g1: LineSegment StartX=3.29999 StartY=8 StartZ=0 EndX=3.29999 EndY=-6.03275e-07 EndZ=0
    g2: ArcOfCircle CenterX=8.29999 CenterY=5 CenterZ=0 NormalX=0 NormalY=0 NormalZ=1 AngleXU=0 Radius=2 StartAngle=3.14159 EndAngle=4.71239
    g3: LineSegment StartX=6.29999 StartY=8 StartZ=0 EndX=6.29999 EndY=5 EndZ=0
    g4: ArcOfCircle CenterX=105 CenterY=19 CenterZ=0 NormalX=0 NormalY=0 NormalZ=1 AngleXU=0 Radius=12.7 StartAngle=4.71239 EndAngle=5.94289
    g5-g11: Circle x7 (B-spline internal-alignment scaffolding for g12; pole/knot coordinates omitted)
    g12: BSplineCurve PolesCount=7 KnotsCount=5 Degree=3 IsPeriodic=0
    g13-g17: GeomPoint x5 (B-spline internal-alignment scaffolding for g12; pole/knot coordinates omitted)
    g18: ArcOfCircle CenterX=105 CenterY=19 CenterZ=0 NormalX=0 NormalY=0 NormalZ=1 AngleXU=0 Radius=15.7 StartAngle=5.81226 EndAngle=6.28319
    g19: BSplineCurve PolesCount=5 KnotsCount=3 Degree=3 IsPeriodic=0
    g20: LineSegment StartX=8.29999 StartY=3 StartZ=0 EndX=101.7 EndY=3 EndZ=0
    g21: LineSegment StartX=3.29999 StartY=-6.03275e-07 StartZ=0 EndX=105 EndY=-6.03275e-07 EndZ=0
    g22: LineSegment StartX=120.974 StartY=8.71251 StartZ=0 EndX=122.332 EndY=7.83778 EndZ=0
    g23: LineSegment StartX=105 StartY=-6.03274e-07 StartZ=0 EndX=113 EndY=-6.03274e-07 EndZ=0
    g24: ArcOfCircle CenterX=105 CenterY=19 CenterZ=0 NormalX=0 NormalY=0 NormalZ=1 AngleXU=0 Radius=20.6155 StartAngle=5.11091 EndAngle=5.71103
    g25: ArcOfCircle CenterX=117.7 CenterY=19 CenterZ=0 NormalX=0 NormalY=0 NormalZ=1 AngleXU=0 Radius=3 StartAngle=1.2e-15 EndAngle=2.10468
    g26: Circle CenterX=116.345 CenterY=16.3232 CenterZ=0 NormalX=0 NormalY=0 NormalZ=1 AngleXU=0 Radius=1
    g27: Circle CenterX=117.24 CenterY=15.7584 CenterZ=0 NormalX=0 NormalY=0 NormalZ=1 AngleXU=0 Radius=1
    g28: Circle CenterX=116.972 CenterY=14.7612 CenterZ=0 NormalX=0 NormalY=0 NormalZ=1 AngleXU=0 Radius=1
    g29: BSplineCurve PolesCount=3 KnotsCount=2 Degree=2 IsPeriodic=0
    g30: GeomPoint X=116.345 Y=16.3232 Z=0
    g31: GeomPoint X=116.972 Y=14.7612 Z=0
    g32: Circle CenterX=115.828 CenterY=17.157 CenterZ=0 NormalX=0 NormalY=0 NormalZ=1 AngleXU=0 Radius=1
    g33: Circle CenterX=115.841 CenterY=16.639 CenterZ=0 NormalX=0 NormalY=0 NormalZ=1 AngleXU=0 Radius=1
    g34: Circle CenterX=116.345 CenterY=16.3232 CenterZ=0 NormalX=0 NormalY=0 NormalZ=1 AngleXU=0 Radius=1
    g35: BSplineCurve PolesCount=3 KnotsCount=2 Degree=2 IsPeriodic=0
    g36: GeomPoint X=115.828 Y=17.157 Z=0
    g37: GeomPoint X=116.345 Y=16.3232 Z=0
    g38: LineSegment StartX=115.828 StartY=17.157 StartZ=0 EndX=115.828 EndY=20.8307 EndZ=0
    g39: Circle CenterX=115.828 CenterY=20.8307 CenterZ=0 NormalX=0 NormalY=0 NormalZ=1 AngleXU=0 Radius=1
    g40: Circle CenterX=115.831 CenterY=21.3396 CenterZ=0 NormalX=0 NormalY=0 NormalZ=1 AngleXU=0 Radius=1
    g41: Circle CenterX=116.173 CenterY=21.5825 CenterZ=0 NormalX=0 NormalY=0 NormalZ=1 AngleXU=0 Radius=1
    g42: BSplineCurve PolesCount=3 KnotsCount=2 Degree=2 IsPeriodic=0
    g43: GeomPoint X=115.828 Y=20.8307 Z=0
    g44: GeomPoint X=116.173 Y=21.5825 Z=0
  constraints (70):
    c: Horizontal(g0)
    c: Distance(g0) = 3
    c: Coincident(g1,g0)
    c: Vertical(g1)
    c: Block(g2)
    c: Block(g0)
    c: Coincident(g3,g0)
    c: Coincident(g3,g2)
    c: Vertical(g3)
    c: Block(g1)
    c: Block(g4)
    c: Coincident(g19,g4)
    c: Block(g19)
    c: Equal(g5, g6-g11) x6
    c: InternalAlignment(g5-g11 -> g12) x7
    c: InternalAlignment(g13-g17 -> g12) x5
    c: Block(g12)
    c: Coincident(g18,g12)
    c: Block(g18)
    c: Coincident(g20,g2)
    c: Coincident(g20,g19)
    c: Horizontal(g20)
    c: Distance(g20) = 93.4
    c: Coincident(g21,g1)
    c: Horizontal(g21)
    c: Distance(g21) = 101.7
    c: Horizontal(g23)
    c: Distance(g23) = 8
    c: Coincident(g24,g23)
    c: Block(g23)
    c: Coincident(g22,g24)
    c: Block(g24)
    c: Block(g22)
    c: Distance(g22) = 1.61553
    c: Coincident(g25,g18)
    c: Block(g25)
    c: Weight(g26) = 1
    c: Equal(g26,g27)
    c: Equal(g26,g28)
    c: Coincident(g29,g4)
    c: InternalAlignment(g26,g29)
    c: InternalAlignment(g27,g29)
    c: InternalAlignment(g28,g29)
    c: InternalAlignment(g30,g29)
    c: InternalAlignment(g31,g29)
    c: Block(g29)
    c: Weight(g32) = 1
    c: Equal(g32,g33)
    c: Equal(g32,g34)
    c: Coincident(g35,g29)
    c: InternalAlignment(g32,g35)
    c: InternalAlignment(g33,g35)
    c: InternalAlignment(g34,g35)
    c: InternalAlignment(g36,g35)
    c: InternalAlignment(g37,g35)
    c: Block(g35)
    c: Coincident(g38,g35)
    c: Vertical(g38)
    c: Block(g38)
    c: Coincident(g42,g38)
    c: Weight(g39) = 1
    c: Equal(g39,g40)
    c: Equal(g39,g41)
    c: Coincident(g42,g25)
    c: InternalAlignment(g39,g42)
    c: InternalAlignment(g40,g42)
    c: InternalAlignment(g41,g42)
    c: InternalAlignment(g43,g42)
    c: InternalAlignment(g44,g42)
    c: Block(g42)
FEATURE [Part::Extrusion] Extrude064  label="bottom016"
  Base = -> Sketch073
  Dir = (0,0,1)
  DirMode = 2
  FaceMakerClass = Part::FaceMakerBullseye
  LengthFwd = 71.4
  LengthRev = 0
  Placement = pos=(0,0,0.3) rot=(0,0,1;0rad)
  Solid = true
  Symmetric = false
FEATURE [Part::Revolution] Revolve157  label="removeToCreateScrewAndThreadedInsertHole063"
  Angle = 360
  Axis = (0,1,0)
  Base = (0,0,0)
  FaceMakerClass = Part::FaceMakerBullseye
  Placement = pos=(12.5,0,10) rot=(0,0,1;0rad)
  Solid = false
  Source = -> Face141
  Symmetric = false
FEATURE [Sketcher::SketchObject] Sketch074
  FullyConstrained = true
  Placement = pos=(117,19,0) rot=(0.57735,0.57735,0.57735;2.0944rad)
  sketch-geometry (48):
    g0: LineSegment StartX=-49.19 StartY=69.25 StartZ=0 EndX=-49.19 EndY=66.25 EndZ=0
    g1: LineSegment StartX=-49.19 StartY=63.5 StartZ=0 EndX=-49.19 EndY=60.5 EndZ=0
    g2: LineSegment StartX=-49.19 StartY=57.75 StartZ=0 EndX=-49.19 EndY=54.75 EndZ=0
    g3: LineSegment StartX=-49.19 StartY=52 StartZ=0 EndX=-49.19 EndY=49 EndZ=0
    g4: LineSegment StartX=-49.19 StartY=46.25 StartZ=0 EndX=-49.19 EndY=43.25 EndZ=0
    g5: LineSegment StartX=-49.19 StartY=40.5 StartZ=0 EndX=-49.19 EndY=37.5 EndZ=0
    g6: LineSegment StartX=-49.19 StartY=34.5 StartZ=0 EndX=-49.19 EndY=31.5 EndZ=0
    g7: LineSegment StartX=-49.19 StartY=28.75 StartZ=0 EndX=-49.19 EndY=25.75 EndZ=0
    g8: LineSegment StartX=-49.19 StartY=23 StartZ=0 EndX=-49.19 EndY=20 EndZ=0
    g9: LineSegment StartX=-49.19 StartY=17.25 StartZ=0 EndX=-49.19 EndY=14.25 EndZ=0
    g10: LineSegment StartX=-49.19 StartY=11.5 StartZ=0 EndX=-49.19 EndY=8.5 EndZ=0
    g11: LineSegment StartX=-49.19 StartY=5.75 StartZ=0 EndX=-49.19 EndY=2.75 EndZ=0
    g12: ArcOfCircle CenterX=-1.5 CenterY=67.75 CenterZ=0 NormalX=0 NormalY=0 NormalZ=1 AngleXU=0 Radius=1.5 StartAngle=4.71239 EndAngle=7.85398
    g13: ArcOfCircle CenterX=-1.5 CenterY=62 CenterZ=0 NormalX=0 NormalY=0 NormalZ=1 AngleXU=0 Radius=1.5 StartAngle=4.71239 EndAngle=7.85398
    g14: ArcOfCircle CenterX=-1.5 CenterY=56.25 CenterZ=0 NormalX=0 NormalY=0 NormalZ=1 AngleXU=0 Radius=1.5 StartAngle=4.71239 EndAngle=7.85398
    g15: ArcOfCircle CenterX=-11.49 CenterY=50.5 CenterZ=0 NormalX=0 NormalY=0 NormalZ=1 AngleXU=0 Radius=1.5 StartAngle=4.71239 EndAngle=7.85398
    g16: ArcOfCircle CenterX=-16.28 CenterY=44.75 CenterZ=0 NormalX=0 NormalY=0 NormalZ=1 AngleXU=0 Radius=1.5 StartAngle=4.71239 EndAngle=7.85398
    g17: ArcOfCircle CenterX=-18.2337 CenterY=39 CenterZ=0 NormalX=0 NormalY=0 NormalZ=1 AngleXU=0 Radius=1.5 StartAngle=4.71485 EndAngle=7.85398
    g18: ArcOfCircle CenterX=-16.2837 CenterY=27.25 CenterZ=0 NormalX=0 NormalY=0 NormalZ=1 AngleXU=0 Radius=1.5 StartAngle=4.71485 EndAngle=7.85398
    g19: ArcOfCircle CenterX=-18.2337 CenterY=33 CenterZ=0 NormalX=0 NormalY=0 NormalZ=1 AngleXU=0 Radius=1.5 StartAngle=4.71485 EndAngle=7.85398
    g20: ArcOfCircle CenterX=-11.49 CenterY=21.5 CenterZ=0 NormalX=0 NormalY=0 NormalZ=1 AngleXU=0 Radius=1.5 StartAngle=4.71239 EndAngle=7.85398
    g21: ArcOfCircle CenterX=-1.5 CenterY=4.25 CenterZ=0 NormalX=0 NormalY=0 NormalZ=1 AngleXU=0 Radius=1.5 StartAngle=4.71239 EndAngle=7.85398
    g22: ArcOfCircle CenterX=-1.5 CenterY=10 CenterZ=0 NormalX=0 NormalY=0 NormalZ=1 AngleXU=0 Radius=1.5 StartAngle=4.71239 EndAngle=7.85398
    g23: ArcOfCircle CenterX=-1.5 CenterY=15.75 CenterZ=0 NormalX=0 NormalY=0 NormalZ=1 AngleXU=0 Radius=1.5 StartAngle=4.71239 EndAngle=7.85398
    g24: LineSegment StartX=-49.19 StartY=69.25 StartZ=0 EndX=-1.5 EndY=69.25 EndZ=0
    g25: LineSegment StartX=-49.19 StartY=66.25 StartZ=0 EndX=-1.5 EndY=66.25 EndZ=0
    g26: LineSegment StartX=-49.19 StartY=63.5 StartZ=0 EndX=-1.5 EndY=63.5 EndZ=0
    g27: LineSegment StartX=-49.19 StartY=60.5 StartZ=0 EndX=-1.5 EndY=60.5 EndZ=0
    g28: LineSegment StartX=-49.19 StartY=57.75 StartZ=0 EndX=-1.5 EndY=57.75 EndZ=0
    g29: LineSegment StartX=-49.19 StartY=54.75 StartZ=0 EndX=-1.5 EndY=54.75 EndZ=0
    g30: LineSegment StartX=-49.19 StartY=52 StartZ=0 EndX=-11.49 EndY=52 EndZ=0
    g31: LineSegment StartX=-49.19 StartY=49 StartZ=0 EndX=-11.49 EndY=49 EndZ=0
    g32: LineSegment StartX=-49.19 StartY=46.25 StartZ=0 EndX=-16.28 EndY=46.25 EndZ=0
    g33: LineSegment StartX=-49.19 StartY=43.25 StartZ=0 EndX=-16.28 EndY=43.25 EndZ=0
    g34: LineSegment StartX=-49.19 StartY=40.5 StartZ=0 EndX=-18.2337 EndY=40.5 EndZ=0
    g35: LineSegment StartX=-49.19 StartY=37.5 StartZ=0 EndX=-18.23 EndY=37.5 EndZ=0
    g36: LineSegment StartX=-49.19 StartY=34.5 StartZ=0 EndX=-18.2337 EndY=34.5 EndZ=0
    g37: LineSegment StartX=-49.19 StartY=31.5 StartZ=0 EndX=-18.23 EndY=31.5 EndZ=0
    g38: LineSegment StartX=-49.19 StartY=28.75 StartZ=0 EndX=-16.2837 EndY=28.75 EndZ=0
    g39: LineSegment StartX=-49.19 StartY=25.75 StartZ=0 EndX=-16.28 EndY=25.75 EndZ=0
    g40: LineSegment StartX=-49.19 StartY=23 StartZ=0 EndX=-11.49 EndY=23 EndZ=0
    g41: LineSegment StartX=-49.19 StartY=20 StartZ=0 EndX=-11.49 EndY=20 EndZ=0
    g42: LineSegment StartX=-49.19 StartY=17.25 StartZ=0 EndX=-1.5 EndY=17.25 EndZ=0
    g43: LineSegment StartX=-49.19 StartY=14.25 StartZ=0 EndX=-1.5 EndY=14.25 EndZ=0
    g44: LineSegment StartX=-49.19 StartY=11.5 StartZ=0 EndX=-1.5 EndY=11.5 EndZ=0
    g45: LineSegment StartX=-49.19 StartY=8.5 StartZ=0 EndX=-1.5 EndY=8.5 EndZ=0
    g46: LineSegment StartX=-49.19 StartY=5.75 StartZ=0 EndX=-1.5 EndY=5.75 EndZ=0
    g47: LineSegment StartX=-49.19 StartY=2.75 StartZ=0 EndX=-1.5 EndY=2.75 EndZ=0
  constraints (120):
    c: Vertical(g0)
    c: Distance(g0) = 3
    c: Block(g0)
    c: Vertical(g1)
    c: Distance(g1) = 3
    c: Vertical(g2)
    c: Equal(g0,g2) = 3
    c: Block(g2)
    c: Vertical(g3)
    c: Equal(g1,g3) = 3
    c: Vertical(g4)
    c: Equal(g0,g4) = 3
    c: Block(g4)
    c: Vertical(g5)
    c: Equal(g1,g5) = 3
    c: Vertical(g6)
    c: Equal(g0,g6) = 3
    c: Block(g6)
    c: Vertical(g7)
    c: Equal(g1,g7) = 3
    c: Vertical(g8)
    c: Equal(g0,g8) = 3
    c: Block(g8)
    c: Vertical(g9)
    c: Equal(g1,g9) = 3
    c: Vertical(g10)
    c: Equal(g0,g10) = 3
    c: Block(g10)
    c: Vertical(g11)
    c: Equal(g1,g11) = 3
    c: Block(g12)
    c: Block(g13)
    c: Block(g14)
    c: Block(g15)
    c: Block(g16)
    c: Block(g17)
    c: Block(g18)
    c: Block(g19)
    c: Block(g20)
    c: Block(g21)
    c: Block(g22)
    c: Block(g23)
    c: Block(g11)
    c: Block(g9)
    c: Block(g7)
    c: Block(g5)
    c: Block(g3)
    c: Block(g1)
    c: Coincident(g24,g0)
    c: Coincident(g24,g12)
    c: Horizontal(g24)
    c: Coincident(g25,g0)
    c: Coincident(g25,g12)
    c: Horizontal(g25)
    c: Coincident(g26,g1)
    c: Coincident(g26,g13)
    c: Horizontal(g26)
    c: Coincident(g27,g1)
    c: Coincident(g27,g13)
    c: Horizontal(g27)
    c: Coincident(g28,g2)
    c: Coincident(g28,g14)
    c: Horizontal(g28)
    c: Coincident(g29,g2)
    c: Coincident(g29,g14)
    c: Horizontal(g29)
    c: Coincident(g30,g3)
    c: Coincident(g30,g15)
    c: Horizontal(g30)
    c: Coincident(g31,g3)
    c: Coincident(g31,g15)
    c: Horizontal(g31)
    c: Coincident(g32,g4)
    c: Coincident(g32,g16)
    c: Horizontal(g32)
    c: Coincident(g33,g4)
    c: Coincident(g33,g16)
    c: Horizontal(g33)
    c: Coincident(g34,g5)
    c: Coincident(g34,g17)
    c: Horizontal(g34)
    c: Coincident(g35,g5)
    c: Coincident(g35,g17)
    c: Horizontal(g35)
    c: Coincident(g36,g6)
    c: Coincident(g36,g19)
    c: Horizontal(g36)
    c: Coincident(g37,g6)
    c: Coincident(g37,g19)
    c: Horizontal(g37)
    c: Coincident(g38,g7)
    c: Coincident(g38,g18)
    c: Horizontal(g38)
    c: Coincident(g39,g7)
    c: Coincident(g39,g18)
    c: Horizontal(g39)
    c: Coincident(g40,g8)
    c: Coincident(g40,g20)
    c: Horizontal(g40)
    c: Coincident(g41,g8)
    c: Coincident(g41,g20)
    c: Horizontal(g41)
    c: Coincident(g42,g9)
    c: Coincident(g42,g23)
    c: Horizontal(g42)
    c: Coincident(g43,g9)
    c: Coincident(g43,g23)
    c: Horizontal(g43)
    c: Coincident(g44,g10)
    c: Coincident(g44,g22)
    c: Horizontal(g44)
    c: Coincident(g45,g10)
    c: Coincident(g45,g22)
    c: Horizontal(g45)
    c: Coincident(g46,g11)
    c: Coincident(g46,g21)
    c: Horizontal(g46)
    c: Coincident(g47,g11)
    c: Coincident(g47,g21)
    c: Horizontal(g47)
FEATURE [Part::Extrusion] Extrude065
  Base = -> Sketch074
  Dir = (1,0,0)
  DirMode = 2
  FaceMakerClass = Part::FaceMakerBullseye
  LengthFwd = 23
  LengthRev = 0
  Placement = pos=(-19,0,0) rot=(0,0,1;0rad)
  Solid = true
  Symmetric = false
FEATURE [Part::Fillet] Fillet056  label="removeToCreateVentalationHoles003"
  Base = -> Extrude065
  Edges = <same value as first occurrence — deduplicated (x6 in doc)>
  Placement = pos=(7,0.02,0) rot=(0,0,1;0rad)
FEATURE [Part::Revolution] Revolve158  label="removeToCreateScrewAndThreadedInsertHole065"
  Angle = 360
  Axis = (0,1,0)
  Base = (0,0,0)
  FaceMakerClass = Part::FaceMakerBullseye
  Placement = pos=(12.5,0,62) rot=(0,0,1;0rad)
  Solid = false
  Source = -> Face146
  Symmetric = false
FEATURE [Part::Revolution] Revolve159  label="removeToCreateScrewAndThreadedInsertHole066"
  Angle = 360
  Axis = (0,1,0)
  Base = (0,0,0)
  FaceMakerClass = Part::FaceMakerBullseye
  Placement = pos=(89.5,0,68.5) rot=(0,0,1;0rad)
  Solid = false
  Source = -> Face143
  Symmetric = false
FEATURE [Part::Revolution] Revolve160  label="removeToCreateScrewAndThreadedInsertHole067"
  Angle = 360
  Axis = (0,1,0)
  Base = (0,0,0)
  FaceMakerClass = Part::FaceMakerBullseye
  Placement = pos=(89.5,0,3.5) rot=(0,0,1;0rad)
  Solid = false
  Source = -> Face142
  Symmetric = false
FEATURE [Part::Revolution] Revolve161  label="removeToCreateScrewAndThreadedInsertHole068"
  Angle = 360
  Axis = (0,1,0)
  Base = (0,0,0)
  FaceMakerClass = Part::FaceMakerBullseye
  Placement = pos=(109.5,4.7,3.5) rot=(0,0,1;0rad)
  Solid = false
  Source = -> Face145
  Symmetric = false
FEATURE [Part::Revolution] Revolve162  label="removeToCreateScrewAndThreadedInsertHole069"
  Angle = 360
  Axis = (0,1,0)
  Base = (0,0,0)
  FaceMakerClass = Part::FaceMakerBullseye
  Placement = pos=(109.5,4.7,68.5) rot=(0,0,1;0rad)
  Solid = false
  Source = -> Face144
  Symmetric = false
FEATURE [Part::MultiFuse] Fusion141  label="removeToCreateScrewAndThreadedInsertHole064"
  Shapes = -> [Revolve162,Revolve161,Revolve160,Revolve159,Revolve158,Revolve157]
FEATURE [Part::Cylinder] Cylinder062
  Angle = 360
  AttacherType = Attacher::AttachEngine3D
  Height = 20
  Placement = pos=(0,0,36.15) rot=(0,0,1;0rad)
  Radius = 14
FEATURE [Part::Cylinder] Cylinder063
  Angle = 360
  AttacherType = Attacher::AttachEngine3D
  Height = 10
  Placement = pos=(0,0,36.15) rot=(0,0,1;0rad)
  Radius = 4
FEATURE [Part::MultiFuse] Fusion139  label="removeToCreteHoleForPlugHousing052"
  Placement = pos=(70,19,36) rot=(0,1,0;1.5708rad)
  Shapes = -> [Cylinder062,Cylinder063]
FEATURE [Part::Cut] Cut060  label="bottom017"
  Base = -> Extrude064
  Tool = -> Fusion139
FEATURE [Part::Cut] Cut061  label="bottom019"
  Base = -> Cut060
  Tool = -> Fusion141
FEATURE [Part::MultiFuse] Fusion140  label="bottom018"
  Shapes = -> [Cut061,Cut058]
FEATURE [Part::Cut] Cut059  label="bottom020"
  Base = -> Fusion140
  Tool = -> Fillet056
FEATURE [Part::Box] Box036  label="Cube021"
  AttacherType = Attacher::AttachEngine3D
  Height = 80
  Length = 26
  Placement = pos=(0,-1,-5) rot=(0,0,1;0rad)
  Width = 11
FEATURE [Part::Cut] Cut062  label="removeFromBottom002"
  Base = -> Cut057
  Tool = -> Box036
FEATURE [Part::Cut] Cut063
  Base = -> Cut059
  Tool = -> Cut062
FEATURE [Part::Cut] Cut064  label="pcbStands"
  Base = -> Fusion095
  Tool = -> Fusion127
FEATURE [Sketcher::SketchObject] Sketch075  label="topSketch022"
  FullyConstrained = true
  sketch-geometry (6):
    g0: LineSegment StartX=19 StartY=38 StartZ=0 EndX=117 EndY=38 EndZ=0
    g1: ArcOfCircle CenterX=19 CenterY=19 CenterZ=0 NormalX=0 NormalY=0 NormalZ=1 AngleXU=0 Radius=19 StartAngle=1.5708 EndAngle=3.14159
    g2: LineSegment StartX=117 StartY=38 StartZ=0 EndX=117 EndY=19 EndZ=0
    g3: LineSegment StartX=98 StartY=1.0161e-12 StartZ=0 EndX=5.22862e-06 EndY=1.0161e-12 EndZ=0
    g4: LineSegment StartX=5.22862e-06 StartY=19 StartZ=0 EndX=5.22862e-06 EndY=1.0161e-12 EndZ=0
    g5: ArcOfCircle CenterX=98 CenterY=19 CenterZ=0 NormalX=0 NormalY=0 NormalZ=1 AngleXU=0 Radius=19 StartAngle=4.71239 EndAngle=6.28319
  constraints (16):
    c: Horizontal(g0)
    c: Distance(g0) = 98
    c: Coincident(g1,g0)
    c: Block(g1)
    c: Coincident(g2,g0)
    c: Vertical(g2)
    c: Distance(g2) = 19
    c: Horizontal(g3)
    c: Coincident(g4,g1)
    c: Vertical(g4)
    c: Coincident(g3,g4)
    c: Block(g3)
    c: Coincident(g5,g2)
    c: Coincident(g5,g3)
    c: Block(g0)
    c: Block(g5)
FEATURE [Part::Extrusion] Extrude067  label="sideB003"
  Base = -> Sketch075
  Dir = (0,0,1)
  DirMode = 2
  FaceMakerClass = Part::FaceMakerBullseye
  LengthFwd = 3
  LengthRev = 0
  Placement = pos=(0,0,71.7) rot=(0,0,1;0rad)
  Solid = true
  Symmetric = false
FEATURE [Sketcher::SketchObject] Sketch076  label="topSketch023"
  FullyConstrained = true
  sketch-geometry (6):
    g0: LineSegment StartX=19 StartY=38 StartZ=0 EndX=117 EndY=38 EndZ=0
    g1: ArcOfCircle CenterX=19 CenterY=19 CenterZ=0 NormalX=0 NormalY=0 NormalZ=1 AngleXU=0 Radius=19 StartAngle=1.5708 EndAngle=3.14159
    g2: LineSegment StartX=117 StartY=38 StartZ=0 EndX=117 EndY=19 EndZ=0
    g3: LineSegment StartX=98 StartY=1.0161e-12 StartZ=0 EndX=5.22862e-06 EndY=1.0161e-12 EndZ=0
    g4: LineSegment StartX=5.22862e-06 StartY=19 StartZ=0 EndX=5.22862e-06 EndY=1.0161e-12 EndZ=0
    g5: ArcOfCircle CenterX=98 CenterY=19 CenterZ=0 NormalX=0 NormalY=0 NormalZ=1 AngleXU=0 Radius=19 StartAngle=4.71239 EndAngle=6.28319
  constraints (16):
    c: Horizontal(g0)
    c: Distance(g0) = 98
    c: Coincident(g1,g0)
    c: Block(g1)
    c: Coincident(g2,g0)
    c: Vertical(g2)
    c: Distance(g2) = 19
    c: Horizontal(g3)
    c: Coincident(g4,g1)
    c: Vertical(g4)
    c: Coincident(g3,g4)
    c: Block(g3)
    c: Coincident(g5,g2)
    c: Coincident(g5,g3)
    c: Block(g0)
    c: Block(g5)
FEATURE [Part::Extrusion] Extrude066  label="sideA003"
  Base = -> Sketch076
  Dir = (0,0,1)
  DirMode = 2
  FaceMakerClass = Part::FaceMakerBullseye
  LengthFwd = 3
  LengthRev = 0
  Placement = pos=(0,0,-2.7) rot=(0,0,1;0rad)
  Solid = true
  Symmetric = false
FEATURE [Part::MultiFuse] Fusion142  label="removeFromBottom003"
  Placement = pos=(2,0,0) rot=(0,0,1;0rad)
  Shapes = -> [Extrude066,Extrude067]
FEATURE [Part::Cut] Cut065  label="screwRetainers002"
  Base = -> Fusion096
  Tool = -> Fusion142
FEATURE [Sketcher::SketchObject] Sketch077
  FullyConstrained = true
  Placement = pos=(117,19,0) rot=(0.57735,0.57735,0.57735;2.0944rad)
  sketch-geometry (8):
    g0: LineSegment StartX=-49.19 StartY=63.5 StartZ=0 EndX=-49.19 EndY=60.5 EndZ=0
    g1: LineSegment StartX=-49.19 StartY=11.5 StartZ=0 EndX=-49.19 EndY=8.5 EndZ=0
    g2: ArcOfCircle CenterX=-1.5 CenterY=62 CenterZ=0 NormalX=0 NormalY=0 NormalZ=1 AngleXU=0 Radius=1.5 StartAngle=4.71239 EndAngle=7.85398
    g3: ArcOfCircle CenterX=-1.5 CenterY=10 CenterZ=0 NormalX=0 NormalY=0 NormalZ=1 AngleXU=0 Radius=1.5 StartAngle=4.71239 EndAngle=7.85398
    g4: LineSegment StartX=-49.19 StartY=63.5 StartZ=0 EndX=-1.5 EndY=63.5 EndZ=0
    g5: LineSegment StartX=-49.19 StartY=60.5 StartZ=0 EndX=-1.5 EndY=60.5 EndZ=0
    g6: LineSegment StartX=-49.19 StartY=11.5 StartZ=0 EndX=-1.5 EndY=11.5 EndZ=0
    g7: LineSegment StartX=-49.19 StartY=8.5 StartZ=0 EndX=-1.5 EndY=8.5 EndZ=0
  constraints (19):
    c: Vertical(g0)
    c: Distance(g0) = 3
    c: Vertical(g1)
    c: Block(g1)
    c: Block(g2)
    c: Block(g3)
    c: Block(g0)
    c: Coincident(g4,g0)
    c: Coincident(g4,g2)
    c: Horizontal(g4)
    c: Coincident(g5,g0)
    c: Coincident(g5,g2)
    c: Horizontal(g5)
    c: Coincident(g6,g1)
    c: Coincident(g6,g3)
    c: Horizontal(g6)
    c: Coincident(g7,g1)
    c: Coincident(g7,g3)
    c: Horizontal(g7)
FEATURE [Part::Extrusion] Extrude068
  Base = -> Sketch077
  Dir = (1,0,0)
  DirMode = 2
  FaceMakerClass = Part::FaceMakerBullseye
  LengthFwd = 10
  LengthRev = 0
  Solid = true
  Symmetric = false
FEATURE [Part::Fillet] Fillet057  label="removeFromtMoreFrontCaseScrewRetainers002"
  Base = -> Extrude068
  Edges = 4 edges r=1.49: [Edge6,Edge11,Edge18,Edge23]
  Placement = pos=(-12,0,0) rot=(0,0,1;0rad)
FEATURE [Sketcher::SketchObject] Sketch078
  FullyConstrained = true
  Placement = pos=(117,19,0) rot=(0.57735,0.57735,0.57735;2.0944rad)
  sketch-geometry (8):
    g0: LineSegment StartX=-49.19 StartY=69.25 StartZ=0 EndX=-49.19 EndY=66.25 EndZ=0
    g1: LineSegment StartX=-49.19 StartY=5.75 StartZ=0 EndX=-49.19 EndY=2.75 EndZ=0
    g2: ArcOfCircle CenterX=-1.5 CenterY=67.75 CenterZ=0 NormalX=0 NormalY=0 NormalZ=1 AngleXU=0 Radius=1.5 StartAngle=4.71239 EndAngle=7.85398
    g3: ArcOfCircle CenterX=-1.5 CenterY=4.25 CenterZ=0 NormalX=0 NormalY=0 NormalZ=1 AngleXU=0 Radius=1.5 StartAngle=4.71239 EndAngle=7.85398
    g4: LineSegment StartX=-49.19 StartY=69.25 StartZ=0 EndX=-1.5 EndY=69.25 EndZ=0
    g5: LineSegment StartX=-49.19 StartY=66.25 StartZ=0 EndX=-1.5 EndY=66.25 EndZ=0
    g6: LineSegment StartX=-49.19 StartY=5.75 StartZ=0 EndX=-1.5 EndY=5.75 EndZ=0
    g7: LineSegment StartX=-49.19 StartY=2.75 StartZ=0 EndX=-1.5 EndY=2.75 EndZ=0
  constraints (19):
    c: Vertical(g0)
    c: Distance(g0) = 3
    c: Block(g0)
    c: Vertical(g1)
    c: Block(g2)
    c: Block(g3)
    c: Block(g1)
    c: Coincident(g4,g0)
    c: Coincident(g4,g2)
    c: Horizontal(g4)
    c: Coincident(g5,g0)
    c: Coincident(g5,g2)
    c: Horizontal(g5)
    c: Coincident(g6,g1)
    c: Coincident(g6,g3)
    c: Horizontal(g6)
    c: Coincident(g7,g1)
    c: Coincident(g7,g3)
    c: Horizontal(g7)
FEATURE [Part::Extrusion] Extrude069
  Base = -> Sketch078
  Dir = (1,0,0)
  DirMode = 2
  FaceMakerClass = Part::FaceMakerBullseye
  LengthFwd = 10
  LengthRev = 0
  Solid = true
  Symmetric = false
FEATURE [Part::Fillet] Fillet058  label="removeFromtMoreFrontCaseScrewRetainers003"
  Base = -> Extrude069
  Edges = 4 edges r=1.49: [Edge6,Edge11,Edge18,Edge23]
  Placement = pos=(-4,0,0) rot=(0,0,1;0rad)
FEATURE [Part::Cut] Cut066
  Base = -> Cut065
  Tool = -> Fillet058
FEATURE [Part::Cut] Cut067  label="screwPillars"
  Base = -> Cut066
  Tool = -> Fillet057
FEATURE [Part::MultiFuse] Fusion143  label="bottom021"
  Shapes = -> [Cut031,Cut063]
FEATURE [Part::Cylinder] Cylinder
  Angle = 360
  AttacherType = Attacher::AttachEngine3D
  Height = 10
  Placement = pos=(20.65,12,4.68) rot=(1,0,0;1.5708rad)
  Radius = 2
FEATURE [Part::Cylinder] Cylinder064
  Angle = 360
  AttacherType = Attacher::AttachEngine3D
  Height = 10
  Placement = pos=(20.65,12,67.38) rot=(1,0,0;1.5708rad)
  Radius = 2
FEATURE [Part::Cylinder] Cylinder065
  Angle = 360
  AttacherType = Attacher::AttachEngine3D
  Height = 10
  Placement = pos=(77.15,12,67.38) rot=(1,0,0;1.5708rad)
  Radius = 2
FEATURE [Part::Cylinder] Cylinder066
  Angle = 360
  AttacherType = Attacher::AttachEngine3D
  Height = 10
  Placement = pos=(77.15,12,4.68) rot=(1,0,0;1.5708rad)
  Radius = 2
FEATURE [Part::MultiFuse] Fusion144  label="removeFromThreadedInsertHousing"
  Shapes = -> [Cylinder065,Cylinder064,Cylinder,Cylinder066]
FEATURE [Part::Cut] Cut068  label="pcbStands001"
  Base = -> Cut064
  Tool = -> Fusion144
FEATURE [Part::MultiFuse] Fusion145
  Shapes = -> [Cut068,Fusion143]
FEATURE [Part::MultiFuse] Fusion146
  Shapes = -> [Fusion145]
FEATURE [Part::MultiFuse] Fusion147  label="bottom022"
  Shapes = -> [Cut067,Fusion146]
FEATURE [Part::MultiFuse] Fusion148  label="casePillars005"
  Shapes = -> [Cut047,Fusion092]
FEATURE [Part::MultiFuse] Fusion149  label="bottom023"
  Shapes = -> [Fusion124,Fusion113,Fusion147]
FEATURE [Part::MultiFuse] Fusion150  label="topBits"
  Shapes = -> [Cut025,Fusion148,Cut030,Fillet034]
FEATURE [Part::Feature] Face149 .. Face152  x4 (patterned run collapsed; names and placements below)
  shape: bbox 3.2 x 1.5 x 2e-07 mm, 1 faces, 0 solids (baked)
FEATURE [Part::Feature] Face153
  shape: bbox 3.6 x 3.2 x 2e-07 mm, 1 faces, 0 solids (baked)
FEATURE [Part::Feature] Face154
  shape: bbox 3.6 x 3.2 x 2e-07 mm, 1 faces, 0 solids (baked)
FEATURE [Sketcher::SketchObject] Sketch079  label="topSketch024"
  FullyConstrained = true
  sketch-geometry (6):
    g0: LineSegment StartX=19 StartY=38 StartZ=0 EndX=117 EndY=38 EndZ=0
    g1: ArcOfCircle CenterX=19 CenterY=19 CenterZ=0 NormalX=0 NormalY=0 NormalZ=1 AngleXU=0 Radius=19 StartAngle=1.5708 EndAngle=3.14159
    g2: LineSegment StartX=117 StartY=38 StartZ=0 EndX=117 EndY=19 EndZ=0
    g3: LineSegment StartX=98 StartY=1.0161e-12 StartZ=0 EndX=5.22862e-06 EndY=1.0161e-12 EndZ=0
    g4: LineSegment StartX=5.22862e-06 StartY=19 StartZ=0 EndX=5.22862e-06 EndY=1.0161e-12 EndZ=0
    g5: ArcOfCircle CenterX=98 CenterY=19 CenterZ=0 NormalX=0 NormalY=0 NormalZ=1 AngleXU=0 Radius=19 StartAngle=4.71239 EndAngle=6.28319
  constraints (16):
    c: Horizontal(g0)
    c: Distance(g0) = 98
    c: Coincident(g1,g0)
    c: Block(g1)
    c: Coincident(g2,g0)
    c: Vertical(g2)
    c: Distance(g2) = 19
    c: Horizontal(g3)
    c: Coincident(g4,g1)
    c: Vertical(g4)
    c: Coincident(g3,g4)
    c: Block(g3)
    c: Coincident(g5,g2)
    c: Coincident(g5,g3)
    c: Block(g0)
    c: Block(g5)
FEATURE [Sketcher::SketchObject] Sketch080  label="topSketch025"
  FullyConstrained = true
  sketch-geometry (6):
    g0: LineSegment StartX=19 StartY=38 StartZ=0 EndX=117 EndY=38 EndZ=0
    g1: ArcOfCircle CenterX=19 CenterY=19 CenterZ=0 NormalX=0 NormalY=0 NormalZ=1 AngleXU=0 Radius=19 StartAngle=1.5708 EndAngle=3.14159
    g2: LineSegment StartX=117 StartY=38 StartZ=0 EndX=117 EndY=19 EndZ=0
    g3: LineSegment StartX=98 StartY=1.0161e-12 StartZ=0 EndX=5.22862e-06 EndY=1.0161e-12 EndZ=0
    g4: LineSegment StartX=5.22862e-06 StartY=19 StartZ=0 EndX=5.22862e-06 EndY=1.0161e-12 EndZ=0
    g5: ArcOfCircle CenterX=98 CenterY=19 CenterZ=0 NormalX=0 NormalY=0 NormalZ=1 AngleXU=0 Radius=19 StartAngle=4.71239 EndAngle=6.28319
  constraints (16):
    c: Horizontal(g0)
    c: Distance(g0) = 98
    c: Coincident(g1,g0)
    c: Block(g1)
    c: Coincident(g2,g0)
    c: Vertical(g2)
    c: Distance(g2) = 19
    c: Horizontal(g3)
    c: Coincident(g4,g1)
    c: Vertical(g4)
    c: Coincident(g3,g4)
    c: Block(g3)
    c: Coincident(g5,g2)
    c: Coincident(g5,g3)
    c: Block(g0)
    c: Block(g5)
FEATURE [Part::Extrusion] Extrude070  label="sideA004"
  Base = -> Sketch080
  Dir = (0,0,1)
  DirMode = 2
  FaceMakerClass = Part::FaceMakerBullseye
  LengthFwd = 3
  LengthRev = 0
  Placement = pos=(0,0,-2.7) rot=(0,0,1;0rad)
  Solid = true
  Symmetric = false
FEATURE [Sketcher::SketchObject] Sketch081
  FullyConstrained = true
  Placement = pos=(117,19,0) rot=(0.57735,0.57735,0.57735;2.0944rad)
  sketch-geometry (8):
    g0: LineSegment StartX=-49.19 StartY=63.5 StartZ=0 EndX=-49.19 EndY=60.5 EndZ=0
    g1: LineSegment StartX=-49.19 StartY=11.5 StartZ=0 EndX=-49.19 EndY=8.5 EndZ=0
    g2: ArcOfCircle CenterX=-1.5 CenterY=62 CenterZ=0 NormalX=0 NormalY=0 NormalZ=1 AngleXU=0 Radius=1.5 StartAngle=4.71239 EndAngle=7.85398
    g3: ArcOfCircle CenterX=-1.5 CenterY=10 CenterZ=0 NormalX=0 NormalY=0 NormalZ=1 AngleXU=0 Radius=1.5 StartAngle=4.71239 EndAngle=7.85398
    g4: LineSegment StartX=-49.19 StartY=63.5 StartZ=0 EndX=-1.5 EndY=63.5 EndZ=0
    g5: LineSegment StartX=-49.19 StartY=60.5 StartZ=0 EndX=-1.5 EndY=60.5 EndZ=0
    g6: LineSegment StartX=-49.19 StartY=11.5 StartZ=0 EndX=-1.5 EndY=11.5 EndZ=0
    g7: LineSegment StartX=-49.19 StartY=8.5 StartZ=0 EndX=-1.5 EndY=8.5 EndZ=0
  constraints (19):
    c: Vertical(g0)
    c: Distance(g0) = 3
    c: Vertical(g1)
    c: Block(g1)
    c: Block(g2)
    c: Block(g3)
    c: Block(g0)
    c: Coincident(g4,g0)
    c: Coincident(g4,g2)
    c: Horizontal(g4)
    c: Coincident(g5,g0)
    c: Coincident(g5,g2)
    c: Horizontal(g5)
    c: Coincident(g6,g1)
    c: Coincident(g6,g3)
    c: Horizontal(g6)
    c: Coincident(g7,g1)
    c: Coincident(g7,g3)
    c: Horizontal(g7)
FEATURE [Part::Extrusion] Extrude071  label="sideB004"
  Base = -> Sketch079
  Dir = (0,0,1)
  DirMode = 2
  FaceMakerClass = Part::FaceMakerBullseye
  LengthFwd = 3
  LengthRev = 0
  Placement = pos=(0,0,71.7) rot=(0,0,1;0rad)
  Solid = true
  Symmetric = false
FEATURE [Part::MultiFuse] Fusion152  label="removeFromBottom004"
  Placement = pos=(2,0,0) rot=(0,0,1;0rad)
  Shapes = -> [Extrude070,Extrude071]
FEATURE [Part::Extrusion] Extrude072
  Base = -> Sketch081
  Dir = (1,0,0)
  DirMode = 2
  FaceMakerClass = Part::FaceMakerBullseye
  LengthFwd = 10
  LengthRev = 0
  Solid = true
  Symmetric = false
FEATURE [Part::Fillet] Fillet059  label="removeFromtMoreFrontCaseScrewRetainers004"
  Base = -> Extrude072
  Edges = 4 edges r=1.49: [Edge6,Edge11,Edge18,Edge23]
  Placement = pos=(-12,0,0) rot=(0,0,1;0rad)
FEATURE [Sketcher::SketchObject] Sketch082
  FullyConstrained = true
  Placement = pos=(117,19,0) rot=(0.57735,0.57735,0.57735;2.0944rad)
  sketch-geometry (8):
    g0: LineSegment StartX=-49.19 StartY=69.25 StartZ=0 EndX=-49.19 EndY=66.25 EndZ=0
    g1: LineSegment StartX=-49.19 StartY=5.75 StartZ=0 EndX=-49.19 EndY=2.75 EndZ=0
    g2: ArcOfCircle CenterX=-1.5 CenterY=67.75 CenterZ=0 NormalX=0 NormalY=0 NormalZ=1 AngleXU=0 Radius=1.5 StartAngle=4.71239 EndAngle=7.85398
    g3: ArcOfCircle CenterX=-1.5 CenterY=4.25 CenterZ=0 NormalX=0 NormalY=0 NormalZ=1 AngleXU=0 Radius=1.5 StartAngle=4.71239 EndAngle=7.85398
    g4: LineSegment StartX=-49.19 StartY=69.25 StartZ=0 EndX=-1.5 EndY=69.25 EndZ=0
    g5: LineSegment StartX=-49.19 StartY=66.25 StartZ=0 EndX=-1.5 EndY=66.25 EndZ=0
    g6: LineSegment StartX=-49.19 StartY=5.75 StartZ=0 EndX=-1.5 EndY=5.75 EndZ=0
    g7: LineSegment StartX=-49.19 StartY=2.75 StartZ=0 EndX=-1.5 EndY=2.75 EndZ=0
  constraints (19):
    c: Vertical(g0)
    c: Distance(g0) = 3
    c: Block(g0)
    c: Vertical(g1)
    c: Block(g2)
    c: Block(g3)
    c: Block(g1)
    c: Coincident(g4,g0)
    c: Coincident(g4,g2)
    c: Horizontal(g4)
    c: Coincident(g5,g0)
    c: Coincident(g5,g2)
    c: Horizontal(g5)
    c: Coincident(g6,g1)
    c: Coincident(g6,g3)
    c: Horizontal(g6)
    c: Coincident(g7,g1)
    c: Coincident(g7,g3)
    c: Horizontal(g7)
FEATURE [Part::Extrusion] Extrude073
  Base = -> Sketch082
  Dir = (1,0,0)
  DirMode = 2
  FaceMakerClass = Part::FaceMakerBullseye
  LengthFwd = 10
  LengthRev = 0
  Solid = true
  Symmetric = false
FEATURE [Part::Fillet] Fillet060  label="removeFromtMoreFrontCaseScrewRetainers005"
  Base = -> Extrude073
  Edges = 4 edges r=1.49: [Edge6,Edge11,Edge18,Edge23]
  Placement = pos=(-4,0,0) rot=(0,0,1;0rad)
FEATURE [Part::Revolution] Revolve163  label="backCaseScrewRetainer004"
  Angle = 360
  Axis = (0,1,0)
  Base = (0,0,0)
  FaceMakerClass = Part::FaceMakerBullseye
  Placement = pos=(12.5,3,62) rot=(0,0,1;0rad)
  Solid = false
  Source = -> Face149
  Symmetric = false
FEATURE [Part::Revolution] Revolve164  label="frontCaseScrewRetainer006"
  Angle = 360
  Axis = (0,1,0)
  Base = (0,0,0)
  FaceMakerClass = Part::FaceMakerBullseye
  Placement = pos=(89.5,3,68.5) rot=(0,0,1;0rad)
  Solid = false
  Source = -> Face151
  Symmetric = false
FEATURE [Part::Revolution] Revolve165  label="frontCaseScrewRetainer007"
  Angle = 360
  Axis = (0,1,0)
  Base = (0,0,0)
  FaceMakerClass = Part::FaceMakerBullseye
  Placement = pos=(89.5,3,3.5) rot=(0,0,1;0rad)
  Solid = false
  Source = -> Face152
  Symmetric = false
FEATURE [Part::Revolution] Revolve166  label="backCaseScrewRetainer005"
  Angle = 360
  Axis = (0,1,0)
  Base = (0,0,0)
  FaceMakerClass = Part::FaceMakerBullseye
  Placement = pos=(12.5,3,10) rot=(0,0,1;0rad)
  Solid = false
  Source = -> Face150
  Symmetric = false
FEATURE [Part::Revolution] Revolve167  label="moreFrontCaseScrewRetainer006"
  Angle = 360
  Axis = (0,1,0)
  Base = (0,0,0)
  FaceMakerClass = Part::FaceMakerBullseye
  Placement = pos=(109.5,4.5,68.5) rot=(0,0,1;0rad)
  Solid = false
  Source = -> Face153
  Symmetric = false
FEATURE [Part::Revolution] Revolve168  label="moreFrontCaseScrewRetainer007"
  Angle = 360
  Axis = (0,1,0)
  Base = (0,0,0)
  FaceMakerClass = Part::FaceMakerBullseye
  Placement = pos=(109.5,4.5,3.5) rot=(0,0,1;0rad)
  Solid = false
  Source = -> Face154
  Symmetric = false
FEATURE [Part::MultiFuse] Fusion151  label="screwRetainers003"
  Shapes = -> [Revolve168,Revolve167,Revolve166,Revolve165,Revolve164,Revolve163]
FEATURE [Part::Cut] Cut069  label="screwRetainers004"
  Base = -> Fusion151
  Tool = -> Fusion152
FEATURE [Part::Cut] Cut070
  Base = -> Cut069
  Tool = -> Fillet060
FEATURE [Part::Cut] Cut071  label="screwPillars001"
  Base = -> Cut070
  Tool = -> Fillet059
FEATURE [Part::MultiFuse] Fusion153  label="bottom024"
  Shapes = -> [Fusion149,Cut071]
FEATURE [Part::Cylinder] Cylinder067
  Angle = 360
  AttacherType = Attacher::AttachEngine3D
  Height = 10
  Placement = pos=(20.65,12,4.68) rot=(1,0,0;1.5708rad)
  Radius = 2
FEATURE [Part::Cylinder] Cylinder068
  Angle = 360
  AttacherType = Attacher::AttachEngine3D
  Height = 10
  Placement = pos=(20.65,12,67.38) rot=(1,0,0;1.5708rad)
  Radius = 2
FEATURE [Part::Cylinder] Cylinder069
  Angle = 360
  AttacherType = Attacher::AttachEngine3D
  Height = 10
  Placement = pos=(77.15,12,67.38) rot=(1,0,0;1.5708rad)
  Radius = 2
FEATURE [Part::Cylinder] Cylinder070
  Angle = 360
  AttacherType = Attacher::AttachEngine3D
  Height = 10
  Placement = pos=(77.15,12,4.68) rot=(1,0,0;1.5708rad)
  Radius = 2
FEATURE [Part::MultiFuse] Fusion154  label="removeFromThreadedInsertHousing001"
  Shapes = -> [Cylinder069,Cylinder068,Cylinder067,Cylinder070]
FEATURE [Part::Cut] Cut072  label="bottom025"
  Base = -> Fusion153
  Tool = -> Fusion154
FEATURE [Image::ImagePlane] ImagePlane
  XSize = 339
  YSize = 72
FEATURE [Sketcher::SketchObject] Sketch083
  FullyConstrained = true
  MapMode = 5
  Support = -> [XY_Plane]
  sketch-geometry (338):
    g0: LineSegment StartX=-151.619 StartY=28.8932 StartZ=0 EndX=-140.819 EndY=28.8932 EndZ=0
    g1: LineSegment StartX=-151.619 StartY=24.0313 StartZ=0 EndX=-151.619 EndY=28.8932 EndZ=0
    g2: LineSegment StartX=-140.819 StartY=17.7713 StartZ=0 EndX=-151.619 EndY=17.7713 EndZ=0
    g3: LineSegment StartX=-151.619 StartY=17.7713 StartZ=0 EndX=-151.619 EndY=22.6313 EndZ=0
    g4: LineSegment StartX=-151.619 StartY=22.6313 StartZ=0 EndX=-145.128 EndY=22.6313 EndZ=0
    g5: LineSegment StartX=-145.128 StartY=24.0313 StartZ=0 EndX=-140.819 EndY=28.8932 EndZ=0
    g6: LineSegment StartX=-145.128 StartY=22.6313 StartZ=0 EndX=-140.819 EndY=17.7713 EndZ=0
    g7: ArcOfCircle CenterX=-155.157 CenterY=23.3323 CenterZ=0 NormalX=0 NormalY=0 NormalZ=1 AngleXU=0 Radius=6.92354 StartAngle=1.03434 EndAngle=5.24885
    g8: ArcOfCircle CenterX=-155.157 CenterY=23.3323 CenterZ=0 NormalX=0 NormalY=0 NormalZ=1 AngleXU=0 Radius=12.6269 StartAngle=1.28675 EndAngle=4.99643
    g9: LineSegment StartX=-151.619 StartY=35.4532 StartZ=0 EndX=-151.619 EndY=29.2832 EndZ=0
    g10: LineSegment StartX=-151.619 StartY=17.3813 StartZ=0 EndX=-151.619 EndY=11.2113 EndZ=0
    g11-g21: Circle x11 (B-spline internal-alignment scaffolding for g22; pole/knot coordinates omitted)
    g22: BSplineCurve PolesCount=11 KnotsCount=9 Degree=3 IsPeriodic=0
    g23-g31: GeomPoint x9 (B-spline internal-alignment scaffolding for g22; pole/knot coordinates omitted)
    g32-g49: Circle x18 (B-spline internal-alignment scaffolding for g50; pole/knot coordinates omitted)
    g50: BSplineCurve PolesCount=18 KnotsCount=16 Degree=3 IsPeriodic=0
    g51-g66: GeomPoint x16 (B-spline internal-alignment scaffolding for g50; pole/knot coordinates omitted)
    g67: LineSegment StartX=-117.124 StartY=30.093 StartZ=0 EndX=-117.603 EndY=26.5272 EndZ=0
    g68: LineSegment StartX=-117.603 StartY=17.8472 StartZ=0 EndX=-117.124 EndY=14.2659 EndZ=0
    g69: Ellipse CenterX=-109.671 CenterY=20.025 CenterZ=0 NormalX=0 NormalY=0 NormalZ=1 MajorRadius=3.34798 MinorRadius=2.71052 AngleXU=-1.56793
    g70: GeomPoint X=-109.666 Y=18.0598 Z=0
    g71: GeomPoint X=-109.677 Y=21.9902 Z=0
    g72: Ellipse CenterX=-109.671 CenterY=20.0123 CenterZ=0 NormalX=0 NormalY=0 NormalZ=1 MajorRadius=6.93002 MinorRadius=6.36273 AngleXU=-3.13976
    g73: GeomPoint X=-112.417 Y=20.0073 Z=0
    g74: GeomPoint X=-106.925 Y=20.0173 Z=0
    g75: Ellipse CenterX=-51.7682 CenterY=20.1463 CenterZ=0 NormalX=0 NormalY=0 NormalZ=1 MajorRadius=3.19279 MinorRadius=2.71052 AngleXU=-1.52774
    g76: GeomPoint X=-51.6955 Y=18.4606 Z=0
    g77: GeomPoint X=-51.8408 Y=21.832 Z=0
    g78: GeomPoint X=-54.5142 Y=20.1413 Z=0
    g79: GeomPoint X=-49.0221 Y=20.1513 Z=0
    g80: Ellipse CenterX=-51.7682 CenterY=20.1463 CenterZ=0 NormalX=0 NormalY=0 NormalZ=1 MajorRadius=6.93002 MinorRadius=6.36273 AngleXU=-3.13976
    g81: Ellipse CenterX=-22.8436 CenterY=20.1783 CenterZ=0 NormalX=0 NormalY=0 NormalZ=1 MajorRadius=3.31512 MinorRadius=2.71052 AngleXU=-1.60214
    g82: GeomPoint X=-22.9034 Y=18.2706 Z=0
    g83: GeomPoint X=-22.7838 Y=22.0861 Z=0
    g84: GeomPoint X=-25.5897 Y=20.1733 Z=0
    g85: GeomPoint X=-20.0976 Y=20.1833 Z=0
    g86: Ellipse CenterX=-22.8436 CenterY=20.1783 CenterZ=0 NormalX=0 NormalY=0 NormalZ=1 MajorRadius=6.93002 MinorRadius=6.36273 AngleXU=-3.13976
    g87: LineSegment StartX=-101.889 StartY=14.1107 StartZ=0 EndX=-97.7455 EndY=14.1107 EndZ=0
    g88: LineSegment StartX=-93.8155 StartY=14.1107 StartZ=0 EndX=-89.6755 EndY=14.1107 EndZ=0
    g89: LineSegment StartX=-85.7455 StartY=14.1107 StartZ=0 EndX=-81.6055 EndY=14.1107 EndZ=0
    g90: LineSegment StartX=-101.889 StartY=14.1107 StartZ=0 EndX=-101.889 EndY=25.9907 EndZ=0
    g91: LineSegment StartX=-101.889 StartY=25.9907 StartZ=0 EndX=-97.8594 EndY=25.9907 EndZ=0
    g92: LineSegment StartX=-97.8594 StartY=25.9907 StartZ=0 EndX=-97.8594 EndY=24.0907 EndZ=0
    g93: LineSegment StartX=-97.7455 StartY=14.1107 StartZ=0 EndX=-97.7455 EndY=19.9107 EndZ=0
    g94: LineSegment StartX=-89.6755 StartY=14.1107 StartZ=0 EndX=-89.6755 EndY=19.9107 EndZ=0
    g95: LineSegment StartX=-93.8155 StartY=14.1107 StartZ=0 EndX=-93.8155 EndY=21.0107 EndZ=0
    g96-g106: Circle x11 (B-spline internal-alignment scaffolding for g107; pole/knot coordinates omitted)
    g107: BSplineCurve PolesCount=11 KnotsCount=9 Degree=3 IsPeriodic=0
    g108-g116: GeomPoint x9 (B-spline internal-alignment scaffolding for g107; pole/knot coordinates omitted)
    g117: BSplineCurve PolesCount=11 KnotsCount=9 Degree=3 IsPeriodic=0
    g118-g125: Circle x8 (B-spline internal-alignment scaffolding for g126; pole/knot coordinates omitted)
    g126: BSplineCurve PolesCount=8 KnotsCount=6 Degree=3 IsPeriodic=0
    g127-g132: GeomPoint x6 (B-spline internal-alignment scaffolding for g126; pole/knot coordinates omitted)
    g133: BSplineCurve PolesCount=8 KnotsCount=6 Degree=3 IsPeriodic=0
    g134: LineSegment StartX=-85.7455 StartY=21.0107 StartZ=0 EndX=-85.7455 EndY=14.1107 EndZ=0
    g135: LineSegment StartX=-80.0879 StartY=14.1107 StartZ=0 EndX=-75.944 EndY=14.1107 EndZ=0
    g136: LineSegment StartX=-72.014 StartY=14.1107 StartZ=0 EndX=-67.874 EndY=14.1107 EndZ=0
    g137: LineSegment StartX=-63.944 StartY=14.1107 StartZ=0 EndX=-59.804 EndY=14.1107 EndZ=0
    g138: LineSegment StartX=-80.0879 StartY=14.1107 StartZ=0 EndX=-80.0879 EndY=25.9907 EndZ=0
    g139: LineSegment StartX=-80.0879 StartY=25.9907 StartZ=0 EndX=-76.0579 EndY=25.9907 EndZ=0
    g140: LineSegment StartX=-76.0579 StartY=25.9907 StartZ=0 EndX=-76.0579 EndY=24.0907 EndZ=0
    g141: LineSegment StartX=-75.944 StartY=14.1107 StartZ=0 EndX=-75.944 EndY=19.9107 EndZ=0
    g142: LineSegment StartX=-67.874 StartY=14.1107 StartZ=0 EndX=-67.874 EndY=19.9107 EndZ=0
    g143: LineSegment StartX=-72.014 StartY=14.1107 StartZ=0 EndX=-72.014 EndY=21.0107 EndZ=0
    g144-g148: Circle x5 (B-spline internal-alignment scaffolding for g149; pole/knot coordinates omitted)
    g149: BSplineCurve PolesCount=11 KnotsCount=9 Degree=3 IsPeriodic=0
    g150-g158: GeomPoint x9 (B-spline internal-alignment scaffolding for g149; pole/knot coordinates omitted)
    g159: BSplineCurve PolesCount=11 KnotsCount=9 Degree=3 IsPeriodic=0
    g160-g167: Circle x8 (B-spline internal-alignment scaffolding for g168; pole/knot coordinates omitted)
    g168: BSplineCurve PolesCount=8 KnotsCount=6 Degree=3 IsPeriodic=0
    g169-g174: GeomPoint x6 (B-spline internal-alignment scaffolding for g168; pole/knot coordinates omitted)
    g175: BSplineCurve PolesCount=8 KnotsCount=6 Degree=3 IsPeriodic=0
    g176: LineSegment StartX=-63.944 StartY=21.0107 StartZ=0 EndX=-63.944 EndY=14.1107 EndZ=0
    g177: LineSegment StartX=-59.804 StartY=14.1107 StartZ=0 EndX=-59.804 EndY=21.5868 EndZ=0
    g178: BSplineCurve PolesCount=4 KnotsCount=2 Degree=3 IsPeriodic=0
    g179: GeomPoint X=-59.804 Y=21.5868 Z=0
    g180: GeomPoint X=-60.2379 Y=24.0907 Z=0
    g181: LineSegment StartX=-81.6055 StartY=14.1107 StartZ=0 EndX=-81.6055 EndY=21.5868 EndZ=0
    g182: LineSegment StartX=-151.619 StartY=24.0313 StartZ=0 EndX=-145.128 EndY=24.0313 EndZ=0
    g183: Circle CenterX=-82.0394 CenterY=24.0907 CenterZ=0 NormalX=0 NormalY=0 NormalZ=1 AngleXU=0 Radius=1
    g184: Circle CenterX=-81.7131 CenterY=23.2736 CenterZ=0 NormalX=0 NormalY=0 NormalZ=1 AngleXU=0 Radius=1
    g185: Circle CenterX=-81.6055 CenterY=21.5868 CenterZ=0 NormalX=0 NormalY=0 NormalZ=1 AngleXU=0 Radius=1
    g186: BSplineCurve PolesCount=3 KnotsCount=2 Degree=2 IsPeriodic=0
    g187: GeomPoint X=-82.0394 Y=24.0907 Z=0
    g188: GeomPoint X=-81.6055 Y=21.5868 Z=0
    g189: Ellipse CenterX=-37.3522 CenterY=19.9515 CenterZ=0 NormalX=0 NormalY=0 NormalZ=1 MajorRadius=2.99755 MinorRadius=2.49 AngleXU=1.5708
    g190: GeomPoint X=-37.3522 Y=21.6203 Z=0
    g191: GeomPoint X=-37.3522 Y=18.2826 Z=0
    g192: ArcOfEllipse CenterX=-38.7647 CenterY=20.06 CenterZ=0 NormalX=0 NormalY=0 NormalZ=1 MajorRadius=6.30025 MinorRadius=5.3849 AngleXU=1.57276 StartAngle=5.50632 EndAngle=10.3035
    g193: GeomPoint X=-38.7711 Y=23.3304 Z=0
    g194: GeomPoint X=-38.7583 Y=16.7895 Z=0
    g195: LineSegment StartX=-34.6109 StartY=14.1107 StartZ=0 EndX=-30.8984 EndY=14.1107 EndZ=0
    g196: LineSegment StartX=-30.8984 StartY=14.1107 StartZ=0 EndX=-30.8984 EndY=31.1784 EndZ=0
    g197: LineSegment StartX=-30.8984 StartY=31.1784 StartZ=0 EndX=-34.9984 EndY=31.1784 EndZ=0
    g198: LineSegment StartX=-34.9984 StartY=24.5602 StartZ=0 EndX=-34.9984 EndY=31.1784 EndZ=0
    g199: LineSegment StartX=-34.6109 StartY=16.0476 StartZ=0 EndX=-34.6109 EndY=14.1107 EndZ=0
    g200: LineSegment StartX=-14.8781 StartY=14.1107 StartZ=0 EndX=-10.5106 EndY=14.1107 EndZ=0
    g201: LineSegment StartX=-14.8781 StartY=14.1107 StartZ=0 EndX=-14.8781 EndY=25.8504 EndZ=0
    g202: LineSegment StartX=-14.8781 StartY=25.8504 StartZ=0 EndX=-10.8534 EndY=25.8504 EndZ=0
    g203: LineSegment StartX=-10.8534 StartY=25.8504 StartZ=0 EndX=-10.8534 EndY=24.0923 EndZ=0
    g204: LineSegment StartX=-10.5106 StartY=14.1107 StartZ=0 EndX=-10.5106 EndY=19.7752 EndZ=0
    g205: LineSegment StartX=-5.96397 StartY=25.9304 StartZ=0 EndX=-5.96397 EndY=22.574 EndZ=0
    g206-g214: Circle x9 (B-spline internal-alignment scaffolding for g215; pole/knot coordinates omitted)
    g215: BSplineCurve PolesCount=9 KnotsCount=7 Degree=3 IsPeriodic=0
    g216-g222: GeomPoint x7 (B-spline internal-alignment scaffolding for g215; pole/knot coordinates omitted)
    g223-g232: Circle x10 (B-spline internal-alignment scaffolding for g233; pole/knot coordinates omitted)
    g233: BSplineCurve PolesCount=10 KnotsCount=8 Degree=3 IsPeriodic=0
    g234-g241: GeomPoint x8 (B-spline internal-alignment scaffolding for g233; pole/knot coordinates omitted)
    g242: LineSegment StartX=-1.58923 StartY=21.0696 StartZ=0 EndX=2.62034 EndY=21.0696 EndZ=0
    g243: LineSegment StartX=-1.55856 StartY=18.7342 StartZ=0 EndX=6.45946 EndY=18.7342 EndZ=0
    g244: LineSegment StartX=5.29231 StartY=17.386 StartZ=0 EndX=5.29231 EndY=14.3674 EndZ=0
    g245-g269: Circle x25 (B-spline internal-alignment scaffolding for g270; pole/knot coordinates omitted)
    g270: BSplineCurve PolesCount=25 KnotsCount=23 Degree=3 IsPeriodic=0
    g271-g293: GeomPoint x23 (B-spline internal-alignment scaffolding for g270; pole/knot coordinates omitted)
    g294-g304: Circle x11 (B-spline internal-alignment scaffolding for g305; pole/knot coordinates omitted)
    g305: BSplineCurve PolesCount=11 KnotsCount=9 Degree=3 IsPeriodic=0
    g306-g314: GeomPoint x9 (B-spline internal-alignment scaffolding for g305; pole/knot coordinates omitted)
    g315-g326: Circle x12 (B-spline internal-alignment scaffolding for g327; pole/knot coordinates omitted)
    g327: BSplineCurve PolesCount=12 KnotsCount=10 Degree=3 IsPeriodic=0
    g328-g337: GeomPoint x10 (B-spline internal-alignment scaffolding for g327; pole/knot coordinates omitted)
  constraints (252):
    c: Coincident(g1,g0)
    c: Horizontal(g0)
    c: Vertical(g1)
    c: Coincident(g2,g3)
    c: Coincident(g3,g4)
    c: Horizontal(g4)
    c: Horizontal(g2)
    c: Vertical(g3)
    c: Block(g1)
    c: Distance(g3) = 4.86
    c: Block(g4)
    c: Distance(g0) = 10.8
    c: Distance(g2) = 10.8
    c: Coincident(g5,g0)
    c: Coincident(g6,g4)
    c: Coincident(g6,g2)
    c: Block(g8)
    c: Block(g7)
    c: Coincident(g9,g8)
    c: Coincident(g9,g7)
    c: Vertical(g9)
    c: Coincident(g10,g7)
    c: Coincident(g10,g8)
    c: Vertical(g10)
    c: Weight(g11) = 1
    c: Equal(g11, g12-g21) x10
    c: InternalAlignment(g11-g21 -> g22) x11
    c: InternalAlignment(g23-g31 -> g22) x9
    c: Block(g22)
    c: Weight(g32) = 1
    c: Equal(g32, g33-g49) x17
    c: InternalAlignment(g32-g49 -> g50) x18
    c: InternalAlignment(g51-g66 -> g50) x16
    c: Block(g50)
    c: Coincident(g67,g50)
    c: Coincident(g67,g22)
    c: Coincident(g68,g22)
    c: Coincident(g68,g50)
    c: InternalAlignment(g70,g69)
    c: InternalAlignment(g71,g69)
    c: Block(g69)
    c: InternalAlignment(g73,g72)
    c: InternalAlignment(g74,g72)
    c: Block(g72)
    c: InternalAlignment(g76,g75)
    c: InternalAlignment(g77,g75)
    c: InternalAlignment(g78,g80)
    c: InternalAlignment(g79,g80)
    c: Block(g80)
    c: Coincident(g75,g80)
    c: Block(g75)
    c: InternalAlignment(g82,g81)
    c: InternalAlignment(g83,g81)
    c: InternalAlignment(g84,g86)
    c: InternalAlignment(g85,g86)
    c: Block(g86)
    c: Coincident(g81,g86)
    c: Block(g81)
    c: Horizontal(g87)
    c: Block(g87)
    c: Horizontal(g88)
    c: Distance(g88) = 4.14
    c: Horizontal(g89)
    c: Equal(g88,g89) = 4.14
    c: Block(g89)
    c: Block(g88)
    c: Coincident(g90,g87)
    c: Vertical(g90)
    c: Distance(g90) = 11.88
    c: Coincident(g91,g90)
    c: Horizontal(g91)
    c: Coincident(g92,g91)
    c: Vertical(g92)
    c: Distance(g91) = 4.03
    c: Distance(g92) = 1.9
    c: Coincident(g93,g87)
    c: Vertical(g93)
    c: Vertical(g94)
    c: Coincident(g94,g88)
    c: Distance(g93) = 5.8
    c: Distance(g94) = 5.8
    c: Vertical(g95)
    c: Coincident(g95,g88)
    c: Distance(g95) = 6.9
    c: Coincident(g107,g92)
    c: Weight(g96) = 1
    c: Equal(g96, g97-g106) x10
    c: InternalAlignment(g96-g106 -> g107) x11
    c: InternalAlignment(g108-g116 -> g107) x9
    c: Block(g107)
    c: Block(g117)
    c: Coincident(g126,g93)
    c: Weight(g118) = 1
    c: Equal(g118, g119-g125) x7
    c: Coincident(g126,g95)
    c: InternalAlignment(g118-g125 -> g126) x8
    c: InternalAlignment(g127-g132 -> g126) x6
    c: Coincident(g133,g94)
    c: Block(g126)
    c: Block(g133)
    c: Coincident(g134,g133)
    c: Coincident(g134,g89)
    c: Vertical(g134)
    c: Horizontal(g135)
    c: Block(g135)
    c: Horizontal(g136)
    c: Equal(g88,g136) = 4.14
    c: Horizontal(g137)
    c: Equal(g136,g137) = 4.14
    c: Block(g137)
    c: Block(g136)
    c: Coincident(g138,g135)
    c: Vertical(g138)
    c: Equal(g90,g138) = 11.88
    c: Coincident(g139,g138)
    c: Horizontal(g139)
    c: Coincident(g140,g139)
    c: Vertical(g140)
    c: Equal(g91,g139) = 4.03
    c: Equal(g92,g140) = 1.9
    c: Coincident(g141,g135)
    c: Vertical(g141)
    c: Vertical(g142)
    c: Coincident(g142,g136)
    c: Equal(g93,g141) = 5.8
    c: Equal(g94,g142) = 5.8
    c: Vertical(g143)
    c: Coincident(g143,g136)
    c: Equal(g95,g143) = 6.9
    c: Coincident(g149,g140)
    c: Equal(g96,g144) = 1
    c: Equal(g144, g145-g148) x4
    c: InternalAlignment(g144-g148 -> g149) x5
    c: InternalAlignment(g150-g158 -> g149) x9
    c: Block(g149)
    c: Block(g159)
    c: Coincident(g168,g141)
    c: Equal(g118,g160) = 1
    c: Equal(g160, g161-g167) x7
    c: Coincident(g168,g143)
    c: InternalAlignment(g160-g167 -> g168) x8
    c: InternalAlignment(g169-g174 -> g168) x6
    c: Coincident(g175,g142)
    c: Block(g168)
    c: Block(g175)
    c: Coincident(g176,g175)
    c: Coincident(g176,g137)
    c: Vertical(g176)
    c: Coincident(g177,g137)
    c: Vertical(g177)
    c: Coincident(g178,g177)
    c: Coincident(g178,g159)
    c: InternalAlignment(g179,g178)
    c: InternalAlignment(g180,g178)
    c: Block(g178)
    c: Vertical(g181)
    c: Coincident(g181,g89)
    c: Block(g5)
    c: Coincident(g182,g1)
    c: Coincident(g182,g5)
    c: Horizontal(g182)
    c: Coincident(g186,g117)
    c: Weight(g183) = 1
    c: Equal(g183,g184)
    c: Equal(g183,g185)
    c: Coincident(g186,g181)
    c: InternalAlignment(g183,g186)
    c: InternalAlignment(g184,g186)
    c: InternalAlignment(g185,g186)
    c: InternalAlignment(g187,g186)
    c: InternalAlignment(g188,g186)
    c: Block(g186)
    c: InternalAlignment(g190,g189)
    c: InternalAlignment(g191,g189)
    c: Block(g189)
    c: InternalAlignment(g193,g192)
    c: InternalAlignment(g194,g192)
    c: Block(g192)
    c: Horizontal(g195)
    c: Block(g195)
    c: Coincident(g196,g195)
    c: Vertical(g196)
    c: Block(g196)
    c: Distance(g195) = 3.71244
    c: Coincident(g197,g196)
    c: Horizontal(g197)
    c: Distance(g197) = 4.1
    c: Coincident(g198,g192)
    c: Coincident(g198,g197)
    c: Vertical(g198)
    c: Block(g198)
    c: Coincident(g199,g192)
    c: Coincident(g199,g195)
    c: Vertical(g199)
    c: Block(g199)
    c: Horizontal(g200)
    c: Block(g200)
    c: Coincident(g201,g200)
    c: Vertical(g201)
    c: Block(g201)
    c: Coincident(g202,g201)
    c: Horizontal(g202)
    c: Block(g202)
    c: Coincident(g203,g202)
    c: Vertical(g203)
    c: Block(g203)
    c: Coincident(g204,g200)
    c: Vertical(g204)
    c: Block(g204)
    c: Coincident(g215,g203)
    c: Weight(g206) = 1
    c: Equal(g206, g207-g214) x8
    c: Coincident(g215,g205)
    c: InternalAlignment(g206-g214 -> g215) x9
    c: InternalAlignment(g216-g222 -> g215) x7
    c: Coincident(g233,g204)
    c: Weight(g223) = 1
    c: Equal(g223, g224-g232) x9
    c: Coincident(g233,g205)
    c: InternalAlignment(g223-g232 -> g233) x10
    c: InternalAlignment(g234-g241 -> g233) x8
    c: Vertical(g205)
    c: Block(g205)
    c: Block(g215)
    c: Block(g233)
    c: Horizontal(g242)
    c: Horizontal(g243)
    c: Block(g242)
    c: Block(g243)
    c: Vertical(g244)
    c: Block(g244)
    c: Coincident(g270,g243)
    c: Weight(g245) = 1
    c: Equal(g245, g246-g269) x24
    c: Coincident(g270,g244)
    c: InternalAlignment(g245-g269 -> g270) x25
    c: InternalAlignment(g271-g293 -> g270) x23
    c: Coincident(g305,g242)
    c: Weight(g294) = 1
    c: Equal(g294, g295-g304) x10
    c: Coincident(g305,g242)
    c: InternalAlignment(g294-g304 -> g305) x11
    c: InternalAlignment(g306-g314 -> g305) x9
    c: Block(g305)
    c: Coincident(g327,g243)
    c: Weight(g315) = 1
    c: Equal(g315, g316-g326) x11
    c: Coincident(g327,g244)
    c: InternalAlignment(g315-g326 -> g327) x12
    c: InternalAlignment(g328-g337 -> g327) x10
    c: Block(g327)
    c: Block(g270)
FEATURE [PartDesign::Body] Body  label="CommodoreLogoAndText"
  Group = -> [Sketch083]
  Origin = -> Origin
FEATURE [Part::Extrusion] Extrude074  label="CommodoreLogoAndText001"
  Base = -> Sketch083
  Dir = (0,0,1)
  DirMode = 2
  FaceMakerClass = Part::FaceMakerBullseye
  LengthFwd = 10
  LengthRev = 0
  Solid = true
  Symmetric = false
FEATURE [Part::FeaturePython] Clone  label="CommodoreLogoAndTextScale"  # Draft clone (typed FeaturePython)
  AttacherType = Attacher::AttachEngine3D
  Fuse = false
  Objects = -> [Extrude074]
  Placement = pos=(111,5.37,-11.6) rot=(0,0,1;0rad)
  Scale = (0.62,0.62,1)
FEATURE [Part::Mirroring] Part__Mirroring  label="CommodoreLogoAndTextScale (Mirror #1)"
  Base = (0,0,0)
  Normal = (1,0,0)
  Source = -> Clone
